# Revit family: REVIT-QW
name_source: partatom
category: Mechanical Equipment
revit_build: Autodesk Revit 2017 (Build: 20190507_1515(x64)
units: mm (PartAtom-declared; Revit-internal decimal feet)

## family parameters
Always vertical = Yes
Cut with Voids When Loaded = No
Part Type = Normal
Room Calculation Point = No
Round Connector Dimension = Use Radius
Shared = No
Work Plane-Based = No

## types (263) — shared parameters
Assembly Code = D3040400
Current = 2 A
Description = PVI QuickDraw - Water Heater
Disclaimer = This rendering is for building modeling purposes only. Submittal/catalog is still the contract document. PVI reserves the right to change design and specification without notice.
Drain Angle = 90.00°
Drain Supplemental Extension = 1"
Drain Supplemental Radius = 1/2"
Energy Radius = 14 9/16"
Frequency = 60 Hz
Location (default) = Please Enter Installation Location
Manufacturer = PVI Industries, LLC
Phase = 1
Rear Access Extension = 0"
Relief Valve NPT = 1"
Relief Valve Radius = 1/2"
URL = www.pvi.com
Voltage = 120 V

## per-type parameters (varying)
- 8200 L 1000A-QW: BW Inlet Conn X=4 9/16"; BW Inlet NPT=4"; BW Inlet Radius=2"; BW Inlet Y=18 11/16"; BW Outlet Conn X=4 9/16"; BW Outlet NPT=4"; BW Outlet Radius=2"; BW Outlet Y=33 11/16"; BW Plumbing Total Z=20 15/16"; BW Up=17 9/16"; BW Up Radius=2"; BW X=24 1/16"; BW Z=7 1/2"; Boiler Water Flow Rate at 180F=322 GPM; Cold Water Extension=9"; Cold Water Inlet Z=5"; Cold Water NPT=2 1/2"; Cold Water Radius=1 1/4"; Control Enclosure Location=20"; Control Panel Extension=44 1/2"; Drain Extension=41 3/8"; Drain NPT=1 1/2"; Drain Radius=3/4"; Energy Extension=42 1/2"; Flat Side Distance=75"; Front Skid Extension=112 1/2"; Height to Drain=3"; Height to Energy=31 5/8"; Height to Hot Outlet=60 3/4"; Height to Relief=60 3/8"; Hot Outlet Angle=90.00°; Hot Outlet Extension=38 1/2"; Hot Outlet NPT=3"; Hot Outlet Offset Horiz=38 1/2"; Hot Outlet Offset Vert=0"; Hot Outlet Radius=1 1/2"; Rear Skid Extension=37 1/2"; Recovery Rate 40F to 140F (GPH)=3800; Relief Valve Extension=40 1/2"; Skid Length=75"; Skid Spacing=43"; U Tube Extension=13 7/16"; U Tube Radius=8"; Unit Height=80 7/16"; Unit Radius=37 1/2"; Weight=3890
- 6900 L 1000A-QWD: BW Inlet Conn X=4 9/16"; BW Inlet NPT=4"; BW Inlet Radius=2"; BW Inlet Y=18 11/16"; BW Outlet Conn X=4 9/16"; BW Outlet NPT=4"; BW Outlet Radius=2"; BW Outlet Y=33 11/16"; BW Plumbing Total Z=20 15/16"; BW Up=17 9/16"; BW Up Radius=2"; BW X=24 1/16"; BW Z=7 1/2"; Boiler Water Flow Rate at 180F=286 GPM; Cold Water Extension=9"; Cold Water Inlet Z=5"; Cold Water NPT=2 1/2"; Cold Water Radius=1 1/4"; Control Enclosure Location=20"; Control Panel Extension=44 1/2"; Drain Extension=41 3/8"; Drain NPT=1 1/2"; Drain Radius=3/4"; Energy Extension=42 1/2"; Flat Side Distance=75"; Front Skid Extension=112 1/2"; Height to Drain=3"; Height to Energy=31 5/8"; Height to Hot Outlet=60 3/4"; Height to Relief=60 3/8"; Hot Outlet Angle=90.00°; Hot Outlet Extension=38 1/2"; Hot Outlet NPT=3"; Hot Outlet Offset Horiz=38 1/2"; Hot Outlet Offset Vert=0"; Hot Outlet Radius=1 1/2"; Rear Skid Extension=37 1/2"; Recovery Rate 40F to 140F (GPH)=3370; Relief Valve Extension=40 1/2"; Skid Length=75"; Skid Spacing=43"; U Tube Extension=13 7/16"; U Tube Radius=8"; Unit Height=80 7/16"; Unit Radius=37 1/2"; Weight=4190
- 6300 L 1000A-QW: BW Inlet Conn X=4"; BW Inlet NPT=4"; BW Inlet Radius=2"; BW Inlet Y=18 11/16"; BW Outlet Conn X=4"; BW Outlet NPT=4"; BW Outlet Radius=2"; BW Outlet Y=33 11/16"; BW Plumbing Total Z=21 3/16"; BW Up=17"; BW Up Radius=2"; BW X=23 1/2"; BW Z=7 1/2"; Boiler Water Flow Rate at 180F=251 GPM; Cold Water Extension=8"; Cold Water Inlet Z=4 1/2"; Cold Water NPT=2 1/2"; Cold Water Radius=1 1/4"; Control Enclosure Location=20"; Control Panel Extension=44 1/2"; Drain Extension=41 3/8"; Drain NPT=1 1/2"; Drain Radius=3/4"; Energy Extension=42 1/2"; Flat Side Distance=75"; Front Skid Extension=112 1/2"; Height to Drain=3"; Height to Energy=31 5/8"; Height to Hot Outlet=60 3/4"; Height to Relief=60 3/8"; Hot Outlet Angle=90.00°; Hot Outlet Extension=38 1/2"; Hot Outlet NPT=3"; Hot Outlet Offset Horiz=38 1/2"; Hot Outlet Offset Vert=0"; Hot Outlet Radius=1 1/2"; Rear Skid Extension=37 1/2"; Recovery Rate 40F to 140F (GPH)=2960; Relief Valve Extension=40 1/2"; Skid Length=75"; Skid Spacing=43"; U Tube Extension=13 11/16"; U Tube Radius=7"; Unit Height=80 7/16"; Unit Radius=37 1/2"; Weight=3730
- 6100 L 1000A-QWD: BW Inlet Conn X=4 9/16"; BW Inlet NPT=4"; BW Inlet Radius=2"; BW Inlet Y=18 11/16"; BW Outlet Conn X=4 9/16"; BW Outlet NPT=4"; BW Outlet Radius=2"; BW Outlet Y=33 11/16"; BW Plumbing Total Z=20 15/16"; BW Up=17 9/16"; BW Up Radius=2"; BW X=24 1/16"; BW Z=7 1/2"; Boiler Water Flow Rate at 180F=249 GPM; Cold Water Extension=9"; Cold Water Inlet Z=5"; Cold Water NPT=2 1/2"; Cold Water Radius=1 1/4"; Control Enclosure Location=20"; Control Panel Extension=44 1/2"; Drain Extension=41 3/8"; Drain NPT=1 1/2"; Drain Radius=3/4"; Energy Extension=42 1/2"; Flat Side Distance=75"; Front Skid Extension=112 1/2"; Height to Drain=3"; Height to Energy=31 5/8"; Height to Hot Outlet=60 3/4"; Height to Relief=60 3/8"; Hot Outlet Angle=90.00°; Hot Outlet Extension=38 1/2"; Hot Outlet NPT=3"; Hot Outlet Offset Horiz=38 1/2"; Hot Outlet Offset Vert=0"; Hot Outlet Radius=1 1/2"; Rear Skid Extension=37 1/2"; Recovery Rate 40F to 140F (GPH)=2930; Relief Valve Extension=40 1/2"; Skid Length=75"; Skid Spacing=43"; U Tube Extension=13 7/16"; U Tube Radius=8"; Unit Height=80 7/16"; Unit Radius=37 1/2"; Weight=4120
- 5400 L 1000A-QWD: BW Inlet Conn X=4"; BW Inlet NPT=4"; BW Inlet Radius=2"; BW Inlet Y=18 11/16"; BW Outlet Conn X=4"; BW Outlet NPT=4"; BW Outlet Radius=2"; BW Outlet Y=33 11/16"; BW Plumbing Total Z=21 3/16"; BW Up=17"; BW Up Radius=2"; BW X=23 1/2"; BW Z=7 1/2"; Boiler Water Flow Rate at 180F=222 GPM; Cold Water Extension=8"; Cold Water Inlet Z=4 1/2"; Cold Water NPT=2 1/2"; Cold Water Radius=1 1/4"; Control Enclosure Location=20"; Control Panel Extension=44 1/2"; Drain Extension=41 3/8"; Drain NPT=1 1/2"; Drain Radius=3/4"; Energy Extension=42 1/2"; Flat Side Distance=75"; Front Skid Extension=112 1/2"; Height to Drain=3"; Height to Energy=31 5/8"; Height to Hot Outlet=60 3/4"; Height to Relief=60 3/8"; Hot Outlet Angle=90.00°; Hot Outlet Extension=38 1/2"; Hot Outlet NPT=3"; Hot Outlet Offset Horiz=38 1/2"; Hot Outlet Offset Vert=0"; Hot Outlet Radius=1 1/2"; Rear Skid Extension=37 1/2"; Recovery Rate 40F to 140F (GPH)=2620; Relief Valve Extension=40 1/2"; Skid Length=75"; Skid Spacing=43"; U Tube Extension=13 11/16"; U Tube Radius=7"; Unit Height=80 7/16"; Unit Radius=37 1/2"; Weight=3960
- 4500 L 1000A-QW: BW Inlet Conn X=3 13/16"; BW Inlet NPT=3"; BW Inlet Radius=1 1/2"; BW Inlet Y=18 11/16"; BW Outlet Conn X=3 13/16"; BW Outlet NPT=3"; BW Outlet Radius=1 1/2"; BW Outlet Y=33 11/16"; BW Plumbing Total Z=18 9/16"; BW Up=16 13/16"; BW Up Radius=1 1/2"; BW X=23 5/16"; BW Z=7 1/2"; Boiler Water Flow Rate at 180F=203 GPM; Cold Water Extension=7 3/8"; Cold Water Inlet Z=5"; Cold Water NPT=2 1/2"; Cold Water Radius=1 1/4"; Control Enclosure Location=20"; Control Panel Extension=44 1/2"; Drain Extension=41 3/8"; Drain NPT=1 1/2"; Drain Radius=3/4"; Energy Extension=42 1/2"; Flat Side Distance=75"; Front Skid Extension=112 1/2"; Height to Drain=3"; Height to Energy=31 5/8"; Height to Hot Outlet=60 3/4"; Height to Relief=60 3/8"; Hot Outlet Angle=90.00°; Hot Outlet Extension=38 1/2"; Hot Outlet NPT=3"; Hot Outlet Offset Horiz=38 1/2"; Hot Outlet Offset Vert=0"; Hot Outlet Radius=1 1/2"; Rear Skid Extension=37 1/2"; Recovery Rate 40F to 140F (GPH)=2390; Relief Valve Extension=40 1/2"; Skid Length=75"; Skid Spacing=43"; U Tube Extension=11 1/16"; U Tube Radius=6 3/8"; Unit Height=80 7/16"; Unit Radius=37 1/2"; Weight=3640
- 4300 L 1000A-QW: BW Inlet Conn X=3 13/16"; BW Inlet NPT=3"; BW Inlet Radius=1 1/2"; BW Inlet Y=18 11/16"; BW Outlet Conn X=3 13/16"; BW Outlet NPT=3"; BW Outlet Radius=1 1/2"; BW Outlet Y=33 11/16"; BW Plumbing Total Z=18 9/16"; BW Up=16 13/16"; BW Up Radius=1 1/2"; BW X=23 5/16"; BW Z=7 1/2"; Boiler Water Flow Rate at 180F=179 GPM; Cold Water Extension=7 3/8"; Cold Water Inlet Z=5"; Cold Water NPT=2 1/2"; Cold Water Radius=1 1/4"; Control Enclosure Location=20"; Control Panel Extension=44 1/2"; Drain Extension=41 3/8"; Drain NPT=1 1/2"; Drain Radius=3/4"; Energy Extension=42 1/2"; Flat Side Distance=75"; Front Skid Extension=112 1/2"; Height to Drain=3"; Height to Energy=31 5/8"; Height to Hot Outlet=60 3/4"; Height to Relief=60 3/8"; Hot Outlet Angle=90.00°; Hot Outlet Extension=38 1/2"; Hot Outlet NPT=3"; Hot Outlet Offset Horiz=38 1/2"; Hot Outlet Offset Vert=0"; Hot Outlet Radius=1 1/2"; Rear Skid Extension=37 1/2"; Recovery Rate 40F to 140F (GPH)=2110; Relief Valve Extension=40 1/2"; Skid Length=75"; Skid Spacing=43"; U Tube Extension=11 1/16"; U Tube Radius=6 3/8"; Unit Height=80 7/16"; Unit Radius=37 1/2"; Weight=3610
- 4200 L 1000A-QWD: BW Inlet Conn X=3 13/16"; BW Inlet NPT=3"; BW Inlet Radius=1 1/2"; BW Inlet Y=18 11/16"; BW Outlet Conn X=3 13/16"; BW Outlet NPT=3"; BW Outlet Radius=1 1/2"; BW Outlet Y=33 11/16"; BW Plumbing Total Z=18 9/16"; BW Up=16 13/16"; BW Up Radius=1 1/2"; BW X=23 5/16"; BW Z=7 1/2"; Boiler Water Flow Rate at 180F=179 GPM; Cold Water Extension=7 3/8"; Cold Water Inlet Z=5"; Cold Water NPT=2 1/2"; Cold Water Radius=1 1/4"; Control Enclosure Location=20"; Control Panel Extension=44 1/2"; Drain Extension=41 3/8"; Drain NPT=1 1/2"; Drain Radius=3/4"; Energy Extension=42 1/2"; Flat Side Distance=75"; Front Skid Extension=112 1/2"; Height to Drain=3"; Height to Energy=31 5/8"; Height to Hot Outlet=60 3/4"; Height to Relief=60 3/8"; Hot Outlet Angle=90.00°; Hot Outlet Extension=38 1/2"; Hot Outlet NPT=3"; Hot Outlet Offset Horiz=38 1/2"; Hot Outlet Offset Vert=0"; Hot Outlet Radius=1 1/2"; Rear Skid Extension=37 1/2"; Recovery Rate 40F to 140F (GPH)=2100; Relief Valve Extension=40 1/2"; Skid Length=75"; Skid Spacing=43"; U Tube Extension=11 1/16"; U Tube Radius=6 3/8"; Unit Height=80 7/16"; Unit Radius=37 1/2"; Weight=3840
- 4000 L 1000A-QW: BW Inlet Conn X=3 13/16"; BW Inlet NPT=3"; BW Inlet Radius=1 1/2"; BW Inlet Y=18 11/16"; BW Outlet Conn X=3 13/16"; BW Outlet NPT=3"; BW Outlet Radius=1 1/2"; BW Outlet Y=33 11/16"; BW Plumbing Total Z=18 9/16"; BW Up=16 13/16"; BW Up Radius=1 1/2"; BW X=23 5/16"; BW Z=7 1/2"; Boiler Water Flow Rate at 180F=152 GPM; Cold Water Extension=7 3/8"; Cold Water Inlet Z=5"; Cold Water NPT=2 1/2"; Cold Water Radius=1 1/4"; Control Enclosure Location=20"; Control Panel Extension=44 1/2"; Drain Extension=41 3/8"; Drain NPT=1 1/2"; Drain Radius=3/4"; Energy Extension=42 1/2"; Flat Side Distance=75"; Front Skid Extension=112 1/2"; Height to Drain=3"; Height to Energy=31 5/8"; Height to Hot Outlet=60 3/4"; Height to Relief=60 3/8"; Hot Outlet Angle=90.00°; Hot Outlet Extension=38 1/2"; Hot Outlet NPT=3"; Hot Outlet Offset Horiz=38 1/2"; Hot Outlet Offset Vert=0"; Hot Outlet Radius=1 1/2"; Rear Skid Extension=37 1/2"; Recovery Rate 40F to 140F (GPH)=1790; Relief Valve Extension=40 1/2"; Skid Length=75"; Skid Spacing=43"; U Tube Extension=11 1/16"; U Tube Radius=6 3/8"; Unit Height=80 7/16"; Unit Radius=37 1/2"; Weight=3590
- 3500 L 1000A-QW: BW Inlet Conn X=2 15/16"; BW Inlet NPT=2 1/2"; BW Inlet Radius=1 1/4"; BW Inlet Y=18 11/16"; BW Outlet Conn X=2 15/16"; BW Outlet NPT=2 1/2"; BW Outlet Radius=1 1/4"; BW Outlet Y=33 11/16"; BW Plumbing Total Z=18 1/16"; BW Up=15 15/16"; BW Up Radius=1 1/4"; BW X=22 7/16"; BW Z=7 1/2"; Boiler Water Flow Rate at 180F=138 GPM; Cold Water Extension=6 3/8"; Cold Water Inlet Z=5 1/8"; Cold Water NPT=2 1/2"; Cold Water Radius=1 1/4"; Control Enclosure Location=20"; Control Panel Extension=44 1/2"; Drain Extension=41 3/8"; Drain NPT=1 1/2"; Drain Radius=3/4"; Energy Extension=42 1/2"; Flat Side Distance=75"; Front Skid Extension=112 1/2"; Height to Drain=3"; Height to Energy=31 5/8"; Height to Hot Outlet=60 3/4"; Height to Relief=60 3/8"; Hot Outlet Angle=90.00°; Hot Outlet Extension=38 1/2"; Hot Outlet NPT=3"; Hot Outlet Offset Horiz=38 1/2"; Hot Outlet Offset Vert=0"; Hot Outlet Radius=1 1/2"; Rear Skid Extension=37 1/2"; Recovery Rate 40F to 140F (GPH)=1630; Relief Valve Extension=40 1/2"; Skid Length=75"; Skid Spacing=43"; U Tube Extension=10 9/16"; U Tube Radius=5 3/8"; Unit Height=80 7/16"; Unit Radius=37 1/2"; Weight=3510
- 3400 L 1000A-QWD: BW Inlet Conn X=3 11/16"; BW Inlet NPT=2 1/2"; BW Inlet Radius=1 1/4"; BW Inlet Y=18 11/16"; BW Outlet Conn X=3 11/16"; BW Outlet NPT=2 1/2"; BW Outlet Radius=1 1/4"; BW Outlet Y=33 11/16"; BW Plumbing Total Z=18 9/16"; BW Up=16 13/16"; BW Up Radius=1 1/4"; BW X=23 5/16"; BW Z=7 1/2"; Boiler Water Flow Rate at 180F=138 GPM; Cold Water Extension=7 3/8"; Cold Water Inlet Z=5"; Cold Water NPT=2 1/2"; Cold Water Radius=1 1/4"; Control Enclosure Location=20"; Control Panel Extension=44 1/2"; Drain Extension=41 3/8"; Drain NPT=1 1/2"; Drain Radius=3/4"; Energy Extension=42 1/2"; Flat Side Distance=75"; Front Skid Extension=112 1/2"; Height to Drain=3"; Height to Energy=31 5/8"; Height to Hot Outlet=60 3/4"; Height to Relief=60 3/8"; Hot Outlet Angle=90.00°; Hot Outlet Extension=38 1/2"; Hot Outlet NPT=3"; Hot Outlet Offset Horiz=38 1/2"; Hot Outlet Offset Vert=0"; Hot Outlet Radius=1 1/2"; Rear Skid Extension=37 1/2"; Recovery Rate 40F to 140F (GPH)=1620; Relief Valve Extension=40 1/2"; Skid Length=75"; Skid Spacing=43"; U Tube Extension=11 1/16"; U Tube Radius=6 3/8"; Unit Height=80 7/16"; Unit Radius=37 1/2"; Weight=3760
- 3000 L 1000A-QW: BW Inlet Conn X=2 15/16"; BW Inlet NPT=2 1/2"; BW Inlet Radius=1 1/4"; BW Inlet Y=18 11/16"; BW Outlet Conn X=2 15/16"; BW Outlet NPT=2 1/2"; BW Outlet Radius=1 1/4"; BW Outlet Y=33 11/16"; BW Plumbing Total Z=18 1/16"; BW Up=15 15/16"; BW Up Radius=1 1/4"; BW X=22 7/16"; BW Z=7 1/2"; Boiler Water Flow Rate at 180F=120 GPM; Cold Water Extension=6 3/8"; Cold Water Inlet Z=5 1/8"; Cold Water NPT=2 1/2"; Cold Water Radius=1 1/4"; Control Enclosure Location=20"; Control Panel Extension=44 1/2"; Drain Extension=41 3/8"; Drain NPT=1 1/2"; Drain Radius=3/4"; Energy Extension=42 1/2"; Flat Side Distance=75"; Front Skid Extension=112 1/2"; Height to Drain=3"; Height to Energy=31 5/8"; Height to Hot Outlet=60 3/4"; Height to Relief=60 3/8"; Hot Outlet Angle=90.00°; Hot Outlet Extension=38 1/2"; Hot Outlet NPT=3"; Hot Outlet Offset Horiz=38 1/2"; Hot Outlet Offset Vert=0"; Hot Outlet Radius=1 1/2"; Rear Skid Extension=37 1/2"; Recovery Rate 40F to 140F (GPH)=1420; Relief Valve Extension=40 1/2"; Skid Length=75"; Skid Spacing=43"; U Tube Extension=10 9/16"; U Tube Radius=5 3/8"; Unit Height=80 7/16"; Unit Radius=37 1/2"; Weight=3500
- 2800 L 1000A-QWD: BW Inlet Conn X=3 11/16"; BW Inlet NPT=2 1/2"; BW Inlet Radius=1 1/4"; BW Inlet Y=12 3/8"; BW Outlet Conn X=3 11/16"; BW Outlet NPT=2 1/2"; BW Outlet Radius=1 1/4"; BW Outlet Y=23 7/16"; BW Plumbing Total Z=22 1/16"; BW Up=13 1/16"; BW Up Radius=1 1/4"; BW X=17 13/16"; BW Z=11 1/2"; Boiler Water Flow Rate at 180F=122 GPM; Cold Water Extension=7 3/8"; Cold Water Inlet Z=5 1/8"; Cold Water NPT=2 1/2"; Cold Water Radius=1 1/4"; Control Enclosure Location=20"; Control Panel Extension=44 1/2"; Drain Extension=41 3/8"; Drain NPT=1 1/2"; Drain Radius=3/4"; Energy Extension=42 1/2"; Flat Side Distance=75"; Front Skid Extension=112 1/2"; Height to Drain=3"; Height to Energy=31 5/8"; Height to Hot Outlet=60 3/4"; Height to Relief=60 3/8"; Hot Outlet Angle=90.00°; Hot Outlet Extension=38 1/2"; Hot Outlet NPT=3"; Hot Outlet Offset Horiz=38 1/2"; Hot Outlet Offset Vert=0"; Hot Outlet Radius=1 1/2"; Rear Skid Extension=37 1/2"; Recovery Rate 40F to 140F (GPH)=1430; Relief Valve Extension=40 1/2"; Skid Length=75"; Skid Spacing=43"; U Tube Extension=10 9/16"; U Tube Radius=6 3/8"; Unit Height=80 7/16"; Unit Radius=37 1/2"; Weight=3570
- 2600 L 1000A-QW: BW Inlet Conn X=2 15/16"; BW Inlet NPT=2 1/2"; BW Inlet Radius=1 1/4"; BW Inlet Y=12 3/8"; BW Outlet Conn X=2 15/16"; BW Outlet NPT=2 1/2"; BW Outlet Radius=1 1/4"; BW Outlet Y=23 7/16"; BW Plumbing Total Z=22 1/16"; BW Up=13 1/16"; BW Up Radius=1 1/4"; BW X=17 13/16"; BW Z=11 1/2"; Boiler Water Flow Rate at 180F=102 GPM; Cold Water Extension=6 3/8"; Cold Water Inlet Z=5 1/8"; Cold Water NPT=2 1/2"; Cold Water Radius=1 1/4"; Control Enclosure Location=20"; Control Panel Extension=44 1/2"; Drain Extension=41 3/8"; Drain NPT=1 1/2"; Drain Radius=3/4"; Energy Extension=42 1/2"; Flat Side Distance=75"; Front Skid Extension=112 1/2"; Height to Drain=3"; Height to Energy=31 5/8"; Height to Hot Outlet=60 3/4"; Height to Relief=60 3/8"; Hot Outlet Angle=90.00°; Hot Outlet Extension=38 1/2"; Hot Outlet NPT=3"; Hot Outlet Offset Horiz=38 1/2"; Hot Outlet Offset Vert=0"; Hot Outlet Radius=1 1/2"; Rear Skid Extension=37 1/2"; Recovery Rate 40F to 140F (GPH)=1200; Relief Valve Extension=40 1/2"; Skid Length=75"; Skid Spacing=43"; U Tube Extension=10 9/16"; U Tube Radius=5 3/8"; Unit Height=80 7/16"; Unit Radius=37 1/2"; Weight=3410
- 900 L 1000A-QWD: BW Inlet Conn X=2 1/2"; BW Inlet NPT=1 1/4"; BW Inlet Radius=5/8"; BW Inlet Y=6 3/4"; BW Outlet Conn X=2 1/2"; BW Outlet NPT=1 1/4"; BW Outlet Radius=5/8"; BW Outlet Y=14 1/16"; BW Plumbing Total Z=18 1/8"; BW Up=8 7/16"; BW Up Radius=5/8"; BW X=10 7/8"; BW Z=8 5/16"; Boiler Water Flow Rate at 180F=38 GPM; Cold Water Extension=5 5/16"; Cold Water Inlet Z=5 5/8"; Cold Water NPT=2"; Cold Water Radius=1"; Control Enclosure Location=20"; Control Panel Extension=44 1/2"; Drain Extension=41 3/8"; Drain NPT=1 1/2"; Drain Radius=3/4"; Energy Extension=42 1/2"; Flat Side Distance=75"; Front Skid Extension=112 1/2"; Height to Drain=3"; Height to Energy=31 5/8"; Height to Hot Outlet=60 3/4"; Height to Relief=60 3/8"; Hot Outlet Angle=90.00°; Hot Outlet Extension=38 1/2"; Hot Outlet NPT=3"; Hot Outlet Offset Horiz=38 1/2"; Hot Outlet Offset Vert=0"; Hot Outlet Radius=1 1/2"; Rear Skid Extension=37 1/2"; Recovery Rate 40F to 140F (GPH)=440; Relief Valve Extension=40 1/2"; Skid Length=75"; Skid Spacing=43"; U Tube Extension=9 13/16"; U Tube Radius=4 5/16"; Unit Height=80 7/16"; Unit Radius=37 1/2"; Weight=3260
- 800 L 1000A-QW: BW Inlet Conn X=1 7/8"; BW Inlet NPT=1 1/4"; BW Inlet Radius=5/8"; BW Inlet Y=6 3/4"; BW Outlet Conn X=1 7/8"; BW Outlet NPT=1 1/4"; BW Outlet Radius=5/8"; BW Outlet Y=14 1/16"; BW Plumbing Total Z=18 1/8"; BW Up=8 7/16"; BW Up Radius=5/8"; BW X=10 7/8"; BW Z=8 5/16"; Boiler Water Flow Rate at 180F=32 GPM; Cold Water Extension=4 5/16"; Cold Water Inlet Z=5 5/8"; Cold Water NPT=2"; Cold Water Radius=1"; Control Enclosure Location=20"; Control Panel Extension=44 1/2"; Drain Extension=41 3/8"; Drain NPT=1 1/2"; Drain Radius=3/4"; Energy Extension=42 1/2"; Flat Side Distance=75"; Front Skid Extension=112 1/2"; Height to Drain=3"; Height to Energy=31 5/8"; Height to Hot Outlet=60 3/4"; Height to Relief=60 3/8"; Hot Outlet Angle=90.00°; Hot Outlet Extension=38 1/2"; Hot Outlet NPT=3"; Hot Outlet Offset Horiz=38 1/2"; Hot Outlet Offset Vert=0"; Hot Outlet Radius=1 1/2"; Rear Skid Extension=37 1/2"; Recovery Rate 40F to 140F (GPH)=380; Relief Valve Extension=40 1/2"; Skid Length=75"; Skid Spacing=43"; U Tube Extension=9 13/16"; U Tube Radius=3 5/16"; Unit Height=80 7/16"; Unit Radius=37 1/2"; Weight=3200
- 700 L 1000A-QWD: BW Inlet Conn X=2 1/2"; BW Inlet NPT=1 1/4"; BW Inlet Radius=5/8"; BW Inlet Y=6 3/4"; BW Outlet Conn X=2 1/2"; BW Outlet NPT=1 1/4"; BW Outlet Radius=5/8"; BW Outlet Y=14 1/16"; BW Plumbing Total Z=18 1/8"; BW Up=8 7/16"; BW Up Radius=5/8"; BW X=10 7/8"; BW Z=8 5/16"; Boiler Water Flow Rate at 180F=29 GPM; Cold Water Extension=5 5/16"; Cold Water Inlet Z=5 5/8"; Cold Water NPT=2"; Cold Water Radius=1"; Control Enclosure Location=20"; Control Panel Extension=44 1/2"; Drain Extension=41 3/8"; Drain NPT=1 1/2"; Drain Radius=3/4"; Energy Extension=42 1/2"; Flat Side Distance=75"; Front Skid Extension=112 1/2"; Height to Drain=3"; Height to Energy=31 5/8"; Height to Hot Outlet=60 3/4"; Height to Relief=60 3/8"; Hot Outlet Angle=90.00°; Hot Outlet Extension=38 1/2"; Hot Outlet NPT=3"; Hot Outlet Offset Horiz=38 1/2"; Hot Outlet Offset Vert=0"; Hot Outlet Radius=1 1/2"; Rear Skid Extension=37 1/2"; Recovery Rate 40F to 140F (GPH)=340; Relief Valve Extension=40 1/2"; Skid Length=75"; Skid Spacing=43"; U Tube Extension=9 13/16"; U Tube Radius=4 5/16"; Unit Height=80 7/16"; Unit Radius=37 1/2"; Weight=3220
- 600 L 1000A-QW: BW Inlet Conn X=1 5/16"; BW Inlet NPT=1"; BW Inlet Radius=1/2"; BW Inlet Y=5 1/2"; BW Outlet Conn X=1 5/16"; BW Outlet NPT=1"; BW Outlet Radius=1/2"; BW Outlet Y=11 3/16"; BW Plumbing Total Z=15 1/2"; BW Up=5 13/16"; BW Up Radius=1/2"; BW X=7 15/16"; BW Z=6 1/16"; Boiler Water Flow Rate at 180F=23 GPM; Cold Water Extension=3 1/4"; Cold Water Inlet Z=5 5/8"; Cold Water NPT=2"; Cold Water Radius=1"; Control Enclosure Location=20"; Control Panel Extension=44 1/2"; Drain Extension=41 3/8"; Drain NPT=1 1/2"; Drain Radius=3/4"; Energy Extension=42 1/2"; Flat Side Distance=75"; Front Skid Extension=112 1/2"; Height to Drain=3"; Height to Energy=31 5/8"; Height to Hot Outlet=60 3/4"; Height to Relief=60 3/8"; Hot Outlet Angle=90.00°; Hot Outlet Extension=38 1/2"; Hot Outlet NPT=3"; Hot Outlet Offset Horiz=38 1/2"; Hot Outlet Offset Vert=0"; Hot Outlet Radius=1 1/2"; Rear Skid Extension=37 1/2"; Recovery Rate 40F to 140F (GPH)=270; Relief Valve Extension=40 1/2"; Skid Length=75"; Skid Spacing=43"; U Tube Extension=9 7/16"; U Tube Radius=2 1/4"; Unit Height=80 7/16"; Unit Radius=37 1/2"; Weight=3160
- 500 L 1000A-QWD: BW Inlet Conn X=1 5/16"; BW Inlet NPT=1"; BW Inlet Radius=1/2"; BW Inlet Y=5 1/2"; BW Outlet Conn X=1 5/16"; BW Outlet NPT=1"; BW Outlet Radius=1/2"; BW Outlet Y=11 3/16"; BW Plumbing Total Z=15 1/2"; BW Up=5 13/16"; BW Up Radius=1/2"; BW X=7 15/16"; BW Z=6 1/16"; Boiler Water Flow Rate at 180F=20 GPM; Cold Water Extension=3 1/4"; Cold Water Inlet Z=5 5/8"; Cold Water NPT=2"; Cold Water Radius=1"; Control Enclosure Location=20"; Control Panel Extension=44 1/2"; Drain Extension=41 3/8"; Drain NPT=1 1/2"; Drain Radius=3/4"; Energy Extension=42 1/2"; Flat Side Distance=75"; Front Skid Extension=112 1/2"; Height to Drain=3"; Height to Energy=31 5/8"; Height to Hot Outlet=60 3/4"; Height to Relief=60 3/8"; Hot Outlet Angle=90.00°; Hot Outlet Extension=38 1/2"; Hot Outlet NPT=3"; Hot Outlet Offset Horiz=38 1/2"; Hot Outlet Offset Vert=0"; Hot Outlet Radius=1 1/2"; Rear Skid Extension=37 1/2"; Recovery Rate 40F to 140F (GPH)=240; Relief Valve Extension=40 1/2"; Skid Length=75"; Skid Spacing=43"; U Tube Extension=9 7/16"; U Tube Radius=2 1/4"; Unit Height=80 7/16"; Unit Radius=37 1/2"; Weight=3180
- 300 L 1000A-QW: BW Inlet Conn X=1 5/16"; BW Inlet NPT=3/4"; BW Inlet Radius=3/8"; BW Inlet Y=5"; BW Outlet Conn X=1 5/16"; BW Outlet NPT=3/4"; BW Outlet Radius=3/8"; BW Outlet Y=9 1/16"; BW Plumbing Total Z=15 3/8"; BW Up=5 3/4"; BW Up Radius=3/8"; BW X=8 1/16"; BW Z=5 15/16"; Boiler Water Flow Rate at 180F=12 GPM; Cold Water Extension=3 1/4"; Cold Water Inlet Z=5 5/8"; Cold Water NPT=2"; Cold Water Radius=1"; Control Enclosure Location=20"; Control Panel Extension=44 1/2"; Drain Extension=41 3/8"; Drain NPT=1 1/2"; Drain Radius=3/4"; Energy Extension=42 1/2"; Flat Side Distance=75"; Front Skid Extension=112 1/2"; Height to Drain=3"; Height to Energy=31 5/8"; Height to Hot Outlet=60 3/4"; Height to Relief=60 3/8"; Hot Outlet Angle=90.00°; Hot Outlet Extension=38 1/2"; Hot Outlet NPT=3"; Hot Outlet Offset Horiz=38 1/2"; Hot Outlet Offset Vert=0"; Hot Outlet Radius=1 1/2"; Rear Skid Extension=37 1/2"; Recovery Rate 40F to 140F (GPH)=140; Relief Valve Extension=40 1/2"; Skid Length=75"; Skid Spacing=43"; U Tube Extension=9 7/16"; U Tube Radius=2 1/4"; Unit Height=80 7/16"; Unit Radius=37 1/2"; Weight=3160
- 250 L 1000A-QWD: BW Inlet Conn X=1 5/16"; BW Inlet NPT=3/4"; BW Inlet Radius=3/8"; BW Inlet Y=5"; BW Outlet Conn X=1 5/16"; BW Outlet NPT=3/4"; BW Outlet Radius=3/8"; BW Outlet Y=9 1/16"; BW Plumbing Total Z=15 3/8"; BW Up=5 3/4"; BW Up Radius=3/8"; BW X=8 1/16"; BW Z=5 15/16"; Boiler Water Flow Rate at 180F=11 GPM; Cold Water Extension=3 1/4"; Cold Water Inlet Z=5 5/8"; Cold Water NPT=2"; Cold Water Radius=1"; Control Enclosure Location=20"; Control Panel Extension=44 1/2"; Drain Extension=41 3/8"; Drain NPT=1 1/2"; Drain Radius=3/4"; Energy Extension=42 1/2"; Flat Side Distance=75"; Front Skid Extension=112 1/2"; Height to Drain=3"; Height to Energy=31 5/8"; Height to Hot Outlet=60 3/4"; Height to Relief=60 3/8"; Hot Outlet Angle=90.00°; Hot Outlet Extension=38 1/2"; Hot Outlet NPT=3"; Hot Outlet Offset Horiz=38 1/2"; Hot Outlet Offset Vert=0"; Hot Outlet Radius=1 1/2"; Rear Skid Extension=37 1/2"; Recovery Rate 40F to 140F (GPH)=130; Relief Valve Extension=40 1/2"; Skid Length=75"; Skid Spacing=43"; U Tube Extension=9 7/16"; U Tube Radius=2 1/4"; Unit Height=80 7/16"; Unit Radius=37 1/2"; Weight=3170
- 2300 L 1000A-QW: BW Inlet Conn X=2 15/16"; BW Inlet NPT=2"; BW Inlet Radius=1"; BW Inlet Y=12 3/8"; BW Outlet Conn X=2 15/16"; BW Outlet NPT=2"; BW Outlet Radius=1"; BW Outlet Y=23 7/16"; BW Plumbing Total Z=22 1/16"; BW Up=13 1/16"; BW Up Radius=1"; BW X=17 13/16"; BW Z=11 1/2"; Boiler Water Flow Rate at 180F=87 GPM; Cold Water Extension=6 3/8"; Cold Water Inlet Z=5 1/8"; Cold Water NPT=2 1/2"; Cold Water Radius=1 1/4"; Control Enclosure Location=20"; Control Panel Extension=44 1/2"; Drain Extension=41 3/8"; Drain NPT=1 1/2"; Drain Radius=3/4"; Energy Extension=42 1/2"; Flat Side Distance=75"; Front Skid Extension=112 1/2"; Height to Drain=3"; Height to Energy=31 5/8"; Height to Hot Outlet=60 3/4"; Height to Relief=60 3/8"; Hot Outlet Angle=90.00°; Hot Outlet Extension=38 1/2"; Hot Outlet NPT=3"; Hot Outlet Offset Horiz=38 1/2"; Hot Outlet Offset Vert=0"; Hot Outlet Radius=1 1/2"; Rear Skid Extension=37 1/2"; Recovery Rate 40F to 140F (GPH)=1020; Relief Valve Extension=40 1/2"; Skid Length=75"; Skid Spacing=43"; U Tube Extension=10 9/16"; U Tube Radius=5 3/8"; Unit Height=80 7/16"; Unit Radius=37 1/2"; Weight=3400
- 2200 L 1000A-QWD: BW Inlet Conn X=2 15/16"; BW Inlet NPT=2"; BW Inlet Radius=1"; BW Inlet Y=12 3/8"; BW Outlet Conn X=2 15/16"; BW Outlet NPT=2"; BW Outlet Radius=1"; BW Outlet Y=23 7/16"; BW Plumbing Total Z=22 1/16"; BW Up=13 1/16"; BW Up Radius=1"; BW X=17 13/16"; BW Z=11 1/2"; Boiler Water Flow Rate at 180F=92 GPM; Cold Water Extension=6 3/8"; Cold Water Inlet Z=5 1/8"; Cold Water NPT=2 1/2"; Cold Water Radius=1 1/4"; Control Enclosure Location=20"; Control Panel Extension=44 1/2"; Drain Extension=41 3/8"; Drain NPT=1 1/2"; Drain Radius=3/4"; Energy Extension=42 1/2"; Flat Side Distance=75"; Front Skid Extension=112 1/2"; Height to Drain=3"; Height to Energy=31 5/8"; Height to Hot Outlet=60 3/4"; Height to Relief=60 3/8"; Hot Outlet Angle=90.00°; Hot Outlet Extension=38 1/2"; Hot Outlet NPT=3"; Hot Outlet Offset Horiz=38 1/2"; Hot Outlet Offset Vert=0"; Hot Outlet Radius=1 1/2"; Rear Skid Extension=37 1/2"; Recovery Rate 40F to 140F (GPH)=1090; Relief Valve Extension=40 1/2"; Skid Length=75"; Skid Spacing=43"; U Tube Extension=10 9/16"; U Tube Radius=5 3/8"; Unit Height=80 7/16"; Unit Radius=37 1/2"; Weight=3520
- 2000 L 1000A-QW: BW Inlet Conn X=2 1/2"; BW Inlet NPT=2"; BW Inlet Radius=1"; BW Inlet Y=10 3/8"; BW Outlet Conn X=2 1/2"; BW Outlet NPT=2"; BW Outlet Radius=1"; BW Outlet Y=17 9/16"; BW Plumbing Total Z=20 1/8"; BW Up=10 3/8"; BW Up Radius=1"; BW X=12 13/16"; BW Z=9 5/16"; Boiler Water Flow Rate at 180F=80 GPM; Cold Water Extension=5 5/16"; Cold Water Inlet Z=5 3/8"; Cold Water NPT=2"; Cold Water Radius=1"; Control Enclosure Location=20"; Control Panel Extension=44 1/2"; Drain Extension=41 3/8"; Drain NPT=1 1/2"; Drain Radius=3/4"; Energy Extension=42 1/2"; Flat Side Distance=75"; Front Skid Extension=112 1/2"; Height to Drain=3"; Height to Energy=31 5/8"; Height to Hot Outlet=60 3/4"; Height to Relief=60 3/8"; Hot Outlet Angle=90.00°; Hot Outlet Extension=38 1/2"; Hot Outlet NPT=3"; Hot Outlet Offset Horiz=38 1/2"; Hot Outlet Offset Vert=0"; Hot Outlet Radius=1 1/2"; Rear Skid Extension=37 1/2"; Recovery Rate 40F to 140F (GPH)=950; Relief Valve Extension=40 1/2"; Skid Length=75"; Skid Spacing=43"; U Tube Extension=10 13/16"; U Tube Radius=4 5/16"; Unit Height=80 7/16"; Unit Radius=37 1/2"; Weight=3320
- 1900 L 1000A-QWD: BW Inlet Conn X=2 15/16"; BW Inlet NPT=2"; BW Inlet Radius=1"; BW Inlet Y=10 3/8"; BW Outlet Conn X=2 15/16"; BW Outlet NPT=2"; BW Outlet Radius=1"; BW Outlet Y=17 9/16"; BW Plumbing Total Z=19 7/8"; BW Up=10 13/16"; BW Up Radius=1"; BW X=13 7/8"; BW Z=9 5/16"; Boiler Water Flow Rate at 180F=80 GPM; Cold Water Extension=6 3/8"; Cold Water Inlet Z=5 1/8"; Cold Water NPT=2 1/2"; Cold Water Radius=1 1/4"; Control Enclosure Location=20"; Control Panel Extension=44 1/2"; Drain Extension=41 3/8"; Drain NPT=1 1/2"; Drain Radius=3/4"; Energy Extension=42 1/2"; Flat Side Distance=75"; Front Skid Extension=112 1/2"; Height to Drain=3"; Height to Energy=31 5/8"; Height to Hot Outlet=60 3/4"; Height to Relief=60 3/8"; Hot Outlet Angle=90.00°; Hot Outlet Extension=38 1/2"; Hot Outlet NPT=3"; Hot Outlet Offset Horiz=38 1/2"; Hot Outlet Offset Vert=0"; Hot Outlet Radius=1 1/2"; Rear Skid Extension=37 1/2"; Recovery Rate 40F to 140F (GPH)=950; Relief Valve Extension=40 1/2"; Skid Length=75"; Skid Spacing=43"; U Tube Extension=10 9/16"; U Tube Radius=5 3/8"; Unit Height=80 7/16"; Unit Radius=37 1/2"; Weight=3490
- 1500 L 1000A-QW: BW Inlet Conn X=2 1/2"; BW Inlet NPT=1 1/2"; BW Inlet Radius=3/4"; BW Inlet Y=10 3/8"; BW Outlet Conn X=2 1/2"; BW Outlet NPT=1 1/2"; BW Outlet Radius=3/4"; BW Outlet Y=17 9/16"; BW Plumbing Total Z=20 1/8"; BW Up=10 3/8"; BW Up Radius=3/4"; BW X=12 13/16"; BW Z=9 5/16"; Boiler Water Flow Rate at 180F=58 GPM; Cold Water Extension=5 5/16"; Cold Water Inlet Z=5 3/8"; Cold Water NPT=2"; Cold Water Radius=1"; Control Enclosure Location=20"; Control Panel Extension=44 1/2"; Drain Extension=41 3/8"; Drain NPT=1 1/2"; Drain Radius=3/4"; Energy Extension=42 1/2"; Flat Side Distance=75"; Front Skid Extension=112 1/2"; Height to Drain=3"; Height to Energy=31 5/8"; Height to Hot Outlet=60 3/4"; Height to Relief=60 3/8"; Hot Outlet Angle=90.00°; Hot Outlet Extension=38 1/2"; Hot Outlet NPT=3"; Hot Outlet Offset Horiz=38 1/2"; Hot Outlet Offset Vert=0"; Hot Outlet Radius=1 1/2"; Rear Skid Extension=37 1/2"; Recovery Rate 40F to 140F (GPH)=690; Relief Valve Extension=40 1/2"; Skid Length=75"; Skid Spacing=43"; U Tube Extension=10 13/16"; U Tube Radius=4 5/16"; Unit Height=80 7/16"; Unit Radius=37 1/2"; Weight=3300
- 1300 L 1000A-QWD: BW Inlet Conn X=2 1/2"; BW Inlet NPT=1 1/2"; BW Inlet Radius=3/4"; BW Inlet Y=8 3/8"; BW Outlet Conn X=2 1/2"; BW Outlet NPT=1 1/2"; BW Outlet Radius=3/4"; BW Outlet Y=15 1/4"; BW Plumbing Total Z=19 1/4"; BW Up=8 5/8"; BW Up Radius=3/4"; BW X=11 11/16"; BW Z=8 7/16"; Boiler Water Flow Rate at 180F=53 GPM; Cold Water Extension=5 5/16"; Cold Water Inlet Z=5 3/8"; Cold Water NPT=2"; Cold Water Radius=1"; Control Enclosure Location=20"; Control Panel Extension=44 1/2"; Drain Extension=41 3/8"; Drain NPT=1 1/2"; Drain Radius=3/4"; Energy Extension=42 1/2"; Flat Side Distance=75"; Front Skid Extension=112 1/2"; Height to Drain=3"; Height to Energy=31 5/8"; Height to Hot Outlet=60 3/4"; Height to Relief=60 3/8"; Hot Outlet Angle=90.00°; Hot Outlet Extension=38 1/2"; Hot Outlet NPT=3"; Hot Outlet Offset Horiz=38 1/2"; Hot Outlet Offset Vert=0"; Hot Outlet Radius=1 1/2"; Rear Skid Extension=37 1/2"; Recovery Rate 40F to 140F (GPH)=620; Relief Valve Extension=40 1/2"; Skid Length=75"; Skid Spacing=43"; U Tube Extension=10 13/16"; U Tube Radius=4 5/16"; Unit Height=80 7/16"; Unit Radius=37 1/2"; Weight=3340
- 1100 L 1000A-QW: BW Inlet Conn X=1 7/8"; BW Inlet NPT=1 1/4"; BW Inlet Radius=5/8"; BW Inlet Y=8 3/8"; BW Outlet Conn X=1 7/8"; BW Outlet NPT=1 1/4"; BW Outlet Radius=5/8"; BW Outlet Y=15 1/4"; BW Plumbing Total Z=18 1/4"; BW Up=8"; BW Up Radius=5/8"; BW X=11 1/16"; BW Z=8 7/16"; Boiler Water Flow Rate at 180F=43 GPM; Cold Water Extension=4 5/16"; Cold Water Inlet Z=5 5/8"; Cold Water NPT=2"; Cold Water Radius=1"; Control Enclosure Location=20"; Control Panel Extension=44 1/2"; Drain Extension=41 3/8"; Drain NPT=1 1/2"; Drain Radius=3/4"; Energy Extension=42 1/2"; Flat Side Distance=75"; Front Skid Extension=112 1/2"; Height to Drain=3"; Height to Energy=31 5/8"; Height to Hot Outlet=60 3/4"; Height to Relief=60 3/8"; Hot Outlet Angle=90.00°; Hot Outlet Extension=38 1/2"; Hot Outlet NPT=3"; Hot Outlet Offset Horiz=38 1/2"; Hot Outlet Offset Vert=0"; Hot Outlet Radius=1 1/2"; Rear Skid Extension=37 1/2"; Recovery Rate 40F to 140F (GPH)=510; Relief Valve Extension=40 1/2"; Skid Length=75"; Skid Spacing=43"; U Tube Extension=9 13/16"; U Tube Radius=3 5/16"; Unit Height=80 7/16"; Unit Radius=37 1/2"; Weight=3220
- 900 L 900A-QWD: BW Inlet Conn X=2 1/2"; BW Inlet NPT=1 1/4"; BW Inlet Radius=5/8"; BW Inlet Y=6 3/4"; BW Outlet Conn X=2 1/2"; BW Outlet NPT=1 1/4"; BW Outlet Radius=5/8"; BW Outlet Y=14 1/16"; BW Plumbing Total Z=18 1/8"; BW Up=8 7/16"; BW Up Radius=5/8"; BW X=10 7/8"; BW Z=8 5/16"; Boiler Water Flow Rate at 180F=38 GPM; Cold Water Extension=5 5/16"; Cold Water Inlet Z=5 5/8"; Cold Water NPT=2"; Cold Water Radius=1"; Control Enclosure Location=20"; Control Panel Extension=40 3/16"; Drain Extension=37 1/16"; Drain NPT=1 1/2"; Drain Radius=3/4"; Energy Extension=49 3/16"; Flat Side Distance=66 3/8"; Front Skid Extension=101 3/16"; Height to Drain=3 7/8"; Height to Energy=32 11/16"; Height to Hot Outlet=72 13/16"; Height to Relief=73 7/16"; Hot Outlet Angle=90.00°; Hot Outlet Extension=34 3/16"; Hot Outlet NPT=3"; Hot Outlet Offset Horiz=34 3/16"; Hot Outlet Offset Vert=0"; Hot Outlet Radius=1 1/2"; Rear Skid Extension=33 3/16"; Recovery Rate 40F to 140F (GPH)=440; Relief Valve Extension=36 3/16"; Skid Length=68"; Skid Spacing=36"; U Tube Extension=9 13/16"; U Tube Radius=4 5/16"; Unit Height=93 1/8"; Unit Radius=33 3/16"; Weight=2360
- 900 L 750A-QWD: BW Inlet Conn X=2 1/2"; BW Inlet NPT=1 1/4"; BW Inlet Radius=5/8"; BW Inlet Y=6 3/4"; BW Outlet Conn X=2 1/2"; BW Outlet NPT=1 1/4"; BW Outlet Radius=5/8"; BW Outlet Y=14 1/16"; BW Plumbing Total Z=18 1/8"; BW Up=8 7/16"; BW Up Radius=5/8"; BW X=10 7/8"; BW Z=8 5/16"; Boiler Water Flow Rate at 180F=38 GPM; Cold Water Extension=5 5/16"; Cold Water Inlet Z=5 5/8"; Cold Water NPT=2"; Cold Water Radius=1"; Control Enclosure Location=20"; Control Panel Extension=40 3/16"; Drain Extension=37 1/16"; Drain NPT=1 1/2"; Drain Radius=3/4"; Energy Extension=49 3/16"; Flat Side Distance=66 3/8"; Front Skid Extension=101 3/16"; Height to Drain=3 7/8"; Height to Energy=32 11/16"; Height to Hot Outlet=60 13/16"; Height to Relief=61 7/16"; Hot Outlet Angle=90.00°; Hot Outlet Extension=34 3/16"; Hot Outlet NPT=3"; Hot Outlet Offset Horiz=34 3/16"; Hot Outlet Offset Vert=0"; Hot Outlet Radius=1 1/2"; Rear Skid Extension=33 3/16"; Recovery Rate 40F to 140F (GPH)=440; Relief Valve Extension=36 3/16"; Skid Length=68"; Skid Spacing=36"; U Tube Extension=9 13/16"; U Tube Radius=4 5/16"; Unit Height=81 1/8"; Unit Radius=33 3/16"; Weight=2140
- 8200 L 900A-QW: BW Inlet Conn X=4 9/16"; BW Inlet NPT=4"; BW Inlet Radius=2"; BW Inlet Y=18 11/16"; BW Outlet Conn X=4 9/16"; BW Outlet NPT=4"; BW Outlet Radius=2"; BW Outlet Y=33 11/16"; BW Plumbing Total Z=20 15/16"; BW Up=17 9/16"; BW Up Radius=2"; BW X=24 1/16"; BW Z=7 1/2"; Boiler Water Flow Rate at 180F=322 GPM; Cold Water Extension=9"; Cold Water Inlet Z=5"; Cold Water NPT=2 1/2"; Cold Water Radius=1 1/4"; Control Enclosure Location=20"; Control Panel Extension=40 3/16"; Drain Extension=37 1/16"; Drain NPT=1 1/2"; Drain Radius=3/4"; Energy Extension=49 3/16"; Flat Side Distance=66 3/8"; Front Skid Extension=101 3/16"; Height to Drain=3 7/8"; Height to Energy=32 11/16"; Height to Hot Outlet=72 13/16"; Height to Relief=73 7/16"; Hot Outlet Angle=90.00°; Hot Outlet Extension=34 3/16"; Hot Outlet NPT=3"; Hot Outlet Offset Horiz=34 3/16"; Hot Outlet Offset Vert=0"; Hot Outlet Radius=1 1/2"; Rear Skid Extension=33 3/16"; Recovery Rate 40F to 140F (GPH)=3800; Relief Valve Extension=36 3/16"; Skid Length=68"; Skid Spacing=36"; U Tube Extension=13 7/16"; U Tube Radius=8"; Unit Height=93 1/8"; Unit Radius=33 3/16"; Weight=3000
- 8200 L 750A-QW: BW Inlet Conn X=4 9/16"; BW Inlet NPT=4"; BW Inlet Radius=2"; BW Inlet Y=18 11/16"; BW Outlet Conn X=4 9/16"; BW Outlet NPT=4"; BW Outlet Radius=2"; BW Outlet Y=33 11/16"; BW Plumbing Total Z=20 15/16"; BW Up=17 9/16"; BW Up Radius=2"; BW X=24 1/16"; BW Z=7 1/2"; Boiler Water Flow Rate at 180F=322 GPM; Cold Water Extension=9"; Cold Water Inlet Z=5"; Cold Water NPT=2 1/2"; Cold Water Radius=1 1/4"; Control Enclosure Location=20"; Control Panel Extension=40 3/16"; Drain Extension=37 1/16"; Drain NPT=1 1/2"; Drain Radius=3/4"; Energy Extension=49 3/16"; Flat Side Distance=66 3/8"; Front Skid Extension=101 3/16"; Height to Drain=3 7/8"; Height to Energy=32 11/16"; Height to Hot Outlet=60 13/16"; Height to Relief=61 7/16"; Hot Outlet Angle=90.00°; Hot Outlet Extension=34 3/16"; Hot Outlet NPT=3"; Hot Outlet Offset Horiz=34 3/16"; Hot Outlet Offset Vert=0"; Hot Outlet Radius=1 1/2"; Rear Skid Extension=33 3/16"; Recovery Rate 40F to 140F (GPH)=3800; Relief Valve Extension=36 3/16"; Skid Length=68"; Skid Spacing=36"; U Tube Extension=13 7/16"; U Tube Radius=8"; Unit Height=81 1/8"; Unit Radius=33 3/16"; Weight=2770
- 800 L 900A-QW: BW Inlet Conn X=1 7/8"; BW Inlet NPT=1 1/4"; BW Inlet Radius=5/8"; BW Inlet Y=6 3/4"; BW Outlet Conn X=1 7/8"; BW Outlet NPT=1 1/4"; BW Outlet Radius=5/8"; BW Outlet Y=14 1/16"; BW Plumbing Total Z=18 1/8"; BW Up=8 7/16"; BW Up Radius=5/8"; BW X=10 7/8"; BW Z=8 5/16"; Boiler Water Flow Rate at 180F=32 GPM; Cold Water Extension=4 5/16"; Cold Water Inlet Z=5 5/8"; Cold Water NPT=2"; Cold Water Radius=1"; Control Enclosure Location=20"; Control Panel Extension=40 3/16"; Drain Extension=37 1/16"; Drain NPT=1 1/2"; Drain Radius=3/4"; Energy Extension=49 3/16"; Flat Side Distance=66 3/8"; Front Skid Extension=101 3/16"; Height to Drain=3 7/8"; Height to Energy=32 11/16"; Height to Hot Outlet=72 13/16"; Height to Relief=73 7/16"; Hot Outlet Angle=90.00°; Hot Outlet Extension=34 3/16"; Hot Outlet NPT=3"; Hot Outlet Offset Horiz=34 3/16"; Hot Outlet Offset Vert=0"; Hot Outlet Radius=1 1/2"; Rear Skid Extension=33 3/16"; Recovery Rate 40F to 140F (GPH)=380; Relief Valve Extension=36 3/16"; Skid Length=68"; Skid Spacing=36"; U Tube Extension=9 13/16"; U Tube Radius=3 5/16"; Unit Height=93 1/8"; Unit Radius=33 3/16"; Weight=2310
- 800 L 750A-QW: BW Inlet Conn X=1 7/8"; BW Inlet NPT=1 1/4"; BW Inlet Radius=5/8"; BW Inlet Y=6 3/4"; BW Outlet Conn X=1 7/8"; BW Outlet NPT=1 1/4"; BW Outlet Radius=5/8"; BW Outlet Y=14 1/16"; BW Plumbing Total Z=18 1/8"; BW Up=8 7/16"; BW Up Radius=5/8"; BW X=10 7/8"; BW Z=8 5/16"; Boiler Water Flow Rate at 180F=32 GPM; Cold Water Extension=4 5/16"; Cold Water Inlet Z=5 5/8"; Cold Water NPT=2"; Cold Water Radius=1"; Control Enclosure Location=20"; Control Panel Extension=40 3/16"; Drain Extension=37 1/16"; Drain NPT=1 1/2"; Drain Radius=3/4"; Energy Extension=49 3/16"; Flat Side Distance=66 3/8"; Front Skid Extension=101 3/16"; Height to Drain=3 7/8"; Height to Energy=32 11/16"; Height to Hot Outlet=60 13/16"; Height to Relief=61 7/16"; Hot Outlet Angle=90.00°; Hot Outlet Extension=34 3/16"; Hot Outlet NPT=3"; Hot Outlet Offset Horiz=34 3/16"; Hot Outlet Offset Vert=0"; Hot Outlet Radius=1 1/2"; Rear Skid Extension=33 3/16"; Recovery Rate 40F to 140F (GPH)=380; Relief Valve Extension=36 3/16"; Skid Length=68"; Skid Spacing=36"; U Tube Extension=9 13/16"; U Tube Radius=3 5/16"; Unit Height=81 1/8"; Unit Radius=33 3/16"; Weight=2080
- 700 L 900A-QWD: BW Inlet Conn X=2 1/2"; BW Inlet NPT=1 1/4"; BW Inlet Radius=5/8"; BW Inlet Y=6 3/4"; BW Outlet Conn X=2 1/2"; BW Outlet NPT=1 1/4"; BW Outlet Radius=5/8"; BW Outlet Y=14 1/16"; BW Plumbing Total Z=18 1/8"; BW Up=8 7/16"; BW Up Radius=5/8"; BW X=10 7/8"; BW Z=8 5/16"; Boiler Water Flow Rate at 180F=29 GPM; Cold Water Extension=5 5/16"; Cold Water Inlet Z=5 5/8"; Cold Water NPT=2"; Cold Water Radius=1"; Control Enclosure Location=20"; Control Panel Extension=40 3/16"; Drain Extension=37 1/16"; Drain NPT=1 1/2"; Drain Radius=3/4"; Energy Extension=49 3/16"; Flat Side Distance=66 3/8"; Front Skid Extension=101 3/16"; Height to Drain=3 7/8"; Height to Energy=32 11/16"; Height to Hot Outlet=72 13/16"; Height to Relief=73 7/16"; Hot Outlet Angle=90.00°; Hot Outlet Extension=34 3/16"; Hot Outlet NPT=3"; Hot Outlet Offset Horiz=34 3/16"; Hot Outlet Offset Vert=0"; Hot Outlet Radius=1 1/2"; Rear Skid Extension=33 3/16"; Recovery Rate 40F to 140F (GPH)=340; Relief Valve Extension=36 3/16"; Skid Length=68"; Skid Spacing=36"; U Tube Extension=9 13/16"; U Tube Radius=4 5/16"; Unit Height=93 1/8"; Unit Radius=33 3/16"; Weight=2330
- 700 L 750A-QWD: BW Inlet Conn X=2 1/2"; BW Inlet NPT=1 1/4"; BW Inlet Radius=5/8"; BW Inlet Y=6 3/4"; BW Outlet Conn X=2 1/2"; BW Outlet NPT=1 1/4"; BW Outlet Radius=5/8"; BW Outlet Y=14 1/16"; BW Plumbing Total Z=18 1/8"; BW Up=8 7/16"; BW Up Radius=5/8"; BW X=10 7/8"; BW Z=8 5/16"; Boiler Water Flow Rate at 180F=29 GPM; Cold Water Extension=5 5/16"; Cold Water Inlet Z=5 5/8"; Cold Water NPT=2"; Cold Water Radius=1"; Control Enclosure Location=20"; Control Panel Extension=40 3/16"; Drain Extension=37 1/16"; Drain NPT=1 1/2"; Drain Radius=3/4"; Energy Extension=49 3/16"; Flat Side Distance=66 3/8"; Front Skid Extension=101 3/16"; Height to Drain=3 7/8"; Height to Energy=32 11/16"; Height to Hot Outlet=60 13/16"; Height to Relief=61 7/16"; Hot Outlet Angle=90.00°; Hot Outlet Extension=34 3/16"; Hot Outlet NPT=3"; Hot Outlet Offset Horiz=34 3/16"; Hot Outlet Offset Vert=0"; Hot Outlet Radius=1 1/2"; Rear Skid Extension=33 3/16"; Recovery Rate 40F to 140F (GPH)=340; Relief Valve Extension=36 3/16"; Skid Length=68"; Skid Spacing=36"; U Tube Extension=9 13/16"; U Tube Radius=4 5/16"; Unit Height=81 1/8"; Unit Radius=33 3/16"; Weight=2100
- 6900 L 900A-QWD: BW Inlet Conn X=4 9/16"; BW Inlet NPT=4"; BW Inlet Radius=2"; BW Inlet Y=18 11/16"; BW Outlet Conn X=4 9/16"; BW Outlet NPT=4"; BW Outlet Radius=2"; BW Outlet Y=33 11/16"; BW Plumbing Total Z=20 15/16"; BW Up=17 9/16"; BW Up Radius=2"; BW X=24 1/16"; BW Z=7 1/2"; Boiler Water Flow Rate at 180F=286 GPM; Cold Water Extension=9"; Cold Water Inlet Z=5"; Cold Water NPT=2 1/2"; Cold Water Radius=1 1/4"; Control Enclosure Location=20"; Control Panel Extension=40 3/16"; Drain Extension=37 1/16"; Drain NPT=1 1/2"; Drain Radius=3/4"; Energy Extension=49 3/16"; Flat Side Distance=66 3/8"; Front Skid Extension=101 3/16"; Height to Drain=3 7/8"; Height to Energy=32 11/16"; Height to Hot Outlet=72 13/16"; Height to Relief=73 7/16"; Hot Outlet Angle=90.00°; Hot Outlet Extension=34 3/16"; Hot Outlet NPT=3"; Hot Outlet Offset Horiz=34 3/16"; Hot Outlet Offset Vert=0"; Hot Outlet Radius=1 1/2"; Rear Skid Extension=33 3/16"; Recovery Rate 40F to 140F (GPH)=3370; Relief Valve Extension=36 3/16"; Skid Length=68"; Skid Spacing=36"; U Tube Extension=13 7/16"; U Tube Radius=8"; Unit Height=93 1/8"; Unit Radius=33 3/16"; Weight=3300
- 6900 L 750A-QWD: BW Inlet Conn X=4 9/16"; BW Inlet NPT=4"; BW Inlet Radius=2"; BW Inlet Y=18 11/16"; BW Outlet Conn X=4 9/16"; BW Outlet NPT=4"; BW Outlet Radius=2"; BW Outlet Y=33 11/16"; BW Plumbing Total Z=20 15/16"; BW Up=17 9/16"; BW Up Radius=2"; BW X=24 1/16"; BW Z=7 1/2"; Boiler Water Flow Rate at 180F=286 GPM; Cold Water Extension=9"; Cold Water Inlet Z=5"; Cold Water NPT=2 1/2"; Cold Water Radius=1 1/4"; Control Enclosure Location=20"; Control Panel Extension=40 3/16"; Drain Extension=37 1/16"; Drain NPT=1 1/2"; Drain Radius=3/4"; Energy Extension=49 3/16"; Flat Side Distance=66 3/8"; Front Skid Extension=101 3/16"; Height to Drain=3 7/8"; Height to Energy=32 11/16"; Height to Hot Outlet=60 13/16"; Height to Relief=61 7/16"; Hot Outlet Angle=90.00°; Hot Outlet Extension=34 3/16"; Hot Outlet NPT=3"; Hot Outlet Offset Horiz=34 3/16"; Hot Outlet Offset Vert=0"; Hot Outlet Radius=1 1/2"; Rear Skid Extension=33 3/16"; Recovery Rate 40F to 140F (GPH)=3370; Relief Valve Extension=36 3/16"; Skid Length=68"; Skid Spacing=36"; U Tube Extension=13 7/16"; U Tube Radius=8"; Unit Height=81 1/8"; Unit Radius=33 3/16"; Weight=3070
- 6300 L 900A-QW: BW Inlet Conn X=4"; BW Inlet NPT=4"; BW Inlet Radius=2"; BW Inlet Y=18 11/16"; BW Outlet Conn X=4"; BW Outlet NPT=4"; BW Outlet Radius=2"; BW Outlet Y=33 11/16"; BW Plumbing Total Z=21 3/16"; BW Up=17"; BW Up Radius=2"; BW X=23 1/2"; BW Z=7 1/2"; Boiler Water Flow Rate at 180F=251 GPM; Cold Water Extension=8"; Cold Water Inlet Z=4 1/2"; Cold Water NPT=2 1/2"; Cold Water Radius=1 1/4"; Control Enclosure Location=20"; Control Panel Extension=40 3/16"; Drain Extension=37 1/16"; Drain NPT=1 1/2"; Drain Radius=3/4"; Energy Extension=49 3/16"; Flat Side Distance=66 3/8"; Front Skid Extension=101 3/16"; Height to Drain=3 7/8"; Height to Energy=32 11/16"; Height to Hot Outlet=72 13/16"; Height to Relief=73 7/16"; Hot Outlet Angle=90.00°; Hot Outlet Extension=34 3/16"; Hot Outlet NPT=3"; Hot Outlet Offset Horiz=34 3/16"; Hot Outlet Offset Vert=0"; Hot Outlet Radius=1 1/2"; Rear Skid Extension=33 3/16"; Recovery Rate 40F to 140F (GPH)=2960; Relief Valve Extension=36 3/16"; Skid Length=68"; Skid Spacing=36"; U Tube Extension=13 11/16"; U Tube Radius=7"; Unit Height=93 1/8"; Unit Radius=33 3/16"; Weight=2830
- 6300 L 750A-QW: BW Inlet Conn X=4"; BW Inlet NPT=4"; BW Inlet Radius=2"; BW Inlet Y=18 11/16"; BW Outlet Conn X=4"; BW Outlet NPT=4"; BW Outlet Radius=2"; BW Outlet Y=33 11/16"; BW Plumbing Total Z=21 3/16"; BW Up=17"; BW Up Radius=2"; BW X=23 1/2"; BW Z=7 1/2"; Boiler Water Flow Rate at 180F=251 GPM; Cold Water Extension=8"; Cold Water Inlet Z=4 1/2"; Cold Water NPT=2 1/2"; Cold Water Radius=1 1/4"; Control Enclosure Location=20"; Control Panel Extension=40 3/16"; Drain Extension=37 1/16"; Drain NPT=1 1/2"; Drain Radius=3/4"; Energy Extension=49 3/16"; Flat Side Distance=66 3/8"; Front Skid Extension=101 3/16"; Height to Drain=3 7/8"; Height to Energy=32 11/16"; Height to Hot Outlet=60 13/16"; Height to Relief=61 7/16"; Hot Outlet Angle=90.00°; Hot Outlet Extension=34 3/16"; Hot Outlet NPT=3"; Hot Outlet Offset Horiz=34 3/16"; Hot Outlet Offset Vert=0"; Hot Outlet Radius=1 1/2"; Rear Skid Extension=33 3/16"; Recovery Rate 40F to 140F (GPH)=2960; Relief Valve Extension=36 3/16"; Skid Length=68"; Skid Spacing=36"; U Tube Extension=13 11/16"; U Tube Radius=7"; Unit Height=81 1/8"; Unit Radius=33 3/16"; Weight=2600
- 6100 L 900A-QWD: BW Inlet Conn X=4 9/16"; BW Inlet NPT=4"; BW Inlet Radius=2"; BW Inlet Y=18 11/16"; BW Outlet Conn X=4 9/16"; BW Outlet NPT=4"; BW Outlet Radius=2"; BW Outlet Y=33 11/16"; BW Plumbing Total Z=20 15/16"; BW Up=17 9/16"; BW Up Radius=2"; BW X=24 1/16"; BW Z=7 1/2"; Boiler Water Flow Rate at 180F=249 GPM; Cold Water Extension=9"; Cold Water Inlet Z=5"; Cold Water NPT=2 1/2"; Cold Water Radius=1 1/4"; Control Enclosure Location=20"; Control Panel Extension=40 3/16"; Drain Extension=37 1/16"; Drain NPT=1 1/2"; Drain Radius=3/4"; Energy Extension=49 3/16"; Flat Side Distance=66 3/8"; Front Skid Extension=101 3/16"; Height to Drain=3 7/8"; Height to Energy=32 11/16"; Height to Hot Outlet=72 13/16"; Height to Relief=73 7/16"; Hot Outlet Angle=90.00°; Hot Outlet Extension=34 3/16"; Hot Outlet NPT=3"; Hot Outlet Offset Horiz=34 3/16"; Hot Outlet Offset Vert=0"; Hot Outlet Radius=1 1/2"; Rear Skid Extension=33 3/16"; Recovery Rate 40F to 140F (GPH)=2930; Relief Valve Extension=36 3/16"; Skid Length=68"; Skid Spacing=36"; U Tube Extension=13 7/16"; U Tube Radius=8"; Unit Height=93 1/8"; Unit Radius=33 3/16"; Weight=3220
- 6100 L 750A-QWD: BW Inlet Conn X=4 9/16"; BW Inlet NPT=4"; BW Inlet Radius=2"; BW Inlet Y=18 11/16"; BW Outlet Conn X=4 9/16"; BW Outlet NPT=4"; BW Outlet Radius=2"; BW Outlet Y=33 11/16"; BW Plumbing Total Z=20 15/16"; BW Up=17 9/16"; BW Up Radius=2"; BW X=24 1/16"; BW Z=7 1/2"; Boiler Water Flow Rate at 180F=249 GPM; Cold Water Extension=9"; Cold Water Inlet Z=5"; Cold Water NPT=2 1/2"; Cold Water Radius=1 1/4"; Control Enclosure Location=20"; Control Panel Extension=40 3/16"; Drain Extension=37 1/16"; Drain NPT=1 1/2"; Drain Radius=3/4"; Energy Extension=49 3/16"; Flat Side Distance=66 3/8"; Front Skid Extension=101 3/16"; Height to Drain=3 7/8"; Height to Energy=32 11/16"; Height to Hot Outlet=60 13/16"; Height to Relief=61 7/16"; Hot Outlet Angle=90.00°; Hot Outlet Extension=34 3/16"; Hot Outlet NPT=3"; Hot Outlet Offset Horiz=34 3/16"; Hot Outlet Offset Vert=0"; Hot Outlet Radius=1 1/2"; Rear Skid Extension=33 3/16"; Recovery Rate 40F to 140F (GPH)=2930; Relief Valve Extension=36 3/16"; Skid Length=68"; Skid Spacing=36"; U Tube Extension=13 7/16"; U Tube Radius=8"; Unit Height=81 1/8"; Unit Radius=33 3/16"; Weight=2990
- 600 L 900A-QW: BW Inlet Conn X=1 5/16"; BW Inlet NPT=1"; BW Inlet Radius=1/2"; BW Inlet Y=5 1/2"; BW Outlet Conn X=1 5/16"; BW Outlet NPT=1"; BW Outlet Radius=1/2"; BW Outlet Y=11 3/16"; BW Plumbing Total Z=15 1/2"; BW Up=5 13/16"; BW Up Radius=1/2"; BW X=7 15/16"; BW Z=6 1/16"; Boiler Water Flow Rate at 180F=23 GPM; Cold Water Extension=3 1/4"; Cold Water Inlet Z=5 5/8"; Cold Water NPT=2"; Cold Water Radius=1"; Control Enclosure Location=20"; Control Panel Extension=40 3/16"; Drain Extension=37 1/16"; Drain NPT=1 1/2"; Drain Radius=3/4"; Energy Extension=49 3/16"; Flat Side Distance=66 3/8"; Front Skid Extension=101 3/16"; Height to Drain=3 7/8"; Height to Energy=32 11/16"; Height to Hot Outlet=72 13/16"; Height to Relief=73 7/16"; Hot Outlet Angle=90.00°; Hot Outlet Extension=34 3/16"; Hot Outlet NPT=3"; Hot Outlet Offset Horiz=34 3/16"; Hot Outlet Offset Vert=0"; Hot Outlet Radius=1 1/2"; Rear Skid Extension=33 3/16"; Recovery Rate 40F to 140F (GPH)=270; Relief Valve Extension=36 3/16"; Skid Length=68"; Skid Spacing=36"; U Tube Extension=9 7/16"; U Tube Radius=2 1/4"; Unit Height=93 1/8"; Unit Radius=33 3/16"; Weight=2270
- 600 L 750A-QW: BW Inlet Conn X=1 5/16"; BW Inlet NPT=1"; BW Inlet Radius=1/2"; BW Inlet Y=5 1/2"; BW Outlet Conn X=1 5/16"; BW Outlet NPT=1"; BW Outlet Radius=1/2"; BW Outlet Y=11 3/16"; BW Plumbing Total Z=15 1/2"; BW Up=5 13/16"; BW Up Radius=1/2"; BW X=7 15/16"; BW Z=6 1/16"; Boiler Water Flow Rate at 180F=23 GPM; Cold Water Extension=3 1/4"; Cold Water Inlet Z=5 5/8"; Cold Water NPT=2"; Cold Water Radius=1"; Control Enclosure Location=20"; Control Panel Extension=40 3/16"; Drain Extension=37 1/16"; Drain NPT=1 1/2"; Drain Radius=3/4"; Energy Extension=49 3/16"; Flat Side Distance=66 3/8"; Front Skid Extension=101 3/16"; Height to Drain=3 7/8"; Height to Energy=32 11/16"; Height to Hot Outlet=60 13/16"; Height to Relief=61 7/16"; Hot Outlet Angle=90.00°; Hot Outlet Extension=34 3/16"; Hot Outlet NPT=3"; Hot Outlet Offset Horiz=34 3/16"; Hot Outlet Offset Vert=0"; Hot Outlet Radius=1 1/2"; Rear Skid Extension=33 3/16"; Recovery Rate 40F to 140F (GPH)=270; Relief Valve Extension=36 3/16"; Skid Length=68"; Skid Spacing=36"; U Tube Extension=9 7/16"; U Tube Radius=2 1/4"; Unit Height=81 1/8"; Unit Radius=33 3/16"; Weight=2040
- 5400 L 900A-QWD: BW Inlet Conn X=4"; BW Inlet NPT=4"; BW Inlet Radius=2"; BW Inlet Y=18 11/16"; BW Outlet Conn X=4"; BW Outlet NPT=4"; BW Outlet Radius=2"; BW Outlet Y=33 11/16"; BW Plumbing Total Z=21 3/16"; BW Up=17"; BW Up Radius=2"; BW X=23 1/2"; BW Z=7 1/2"; Boiler Water Flow Rate at 180F=222 GPM; Cold Water Extension=8"; Cold Water Inlet Z=4 1/2"; Cold Water NPT=2 1/2"; Cold Water Radius=1 1/4"; Control Enclosure Location=20"; Control Panel Extension=40 3/16"; Drain Extension=37 1/16"; Drain NPT=1 1/2"; Drain Radius=3/4"; Energy Extension=49 3/16"; Flat Side Distance=66 3/8"; Front Skid Extension=101 3/16"; Height to Drain=3 7/8"; Height to Energy=32 11/16"; Height to Hot Outlet=72 13/16"; Height to Relief=73 7/16"; Hot Outlet Angle=90.00°; Hot Outlet Extension=34 3/16"; Hot Outlet NPT=3"; Hot Outlet Offset Horiz=34 3/16"; Hot Outlet Offset Vert=0"; Hot Outlet Radius=1 1/2"; Rear Skid Extension=33 3/16"; Recovery Rate 40F to 140F (GPH)=2620; Relief Valve Extension=36 3/16"; Skid Length=68"; Skid Spacing=36"; U Tube Extension=13 11/16"; U Tube Radius=7"; Unit Height=93 1/8"; Unit Radius=33 3/16"; Weight=3060
- 5400 L 750A-QWD: BW Inlet Conn X=4"; BW Inlet NPT=4"; BW Inlet Radius=2"; BW Inlet Y=18 11/16"; BW Outlet Conn X=4"; BW Outlet NPT=4"; BW Outlet Radius=2"; BW Outlet Y=33 11/16"; BW Plumbing Total Z=21 3/16"; BW Up=17"; BW Up Radius=2"; BW X=23 1/2"; BW Z=7 1/2"; Boiler Water Flow Rate at 180F=222 GPM; Cold Water Extension=8"; Cold Water Inlet Z=4 1/2"; Cold Water NPT=2 1/2"; Cold Water Radius=1 1/4"; Control Enclosure Location=20"; Control Panel Extension=40 3/16"; Drain Extension=37 1/16"; Drain NPT=1 1/2"; Drain Radius=3/4"; Energy Extension=49 3/16"; Flat Side Distance=66 3/8"; Front Skid Extension=101 3/16"; Height to Drain=3 7/8"; Height to Energy=32 11/16"; Height to Hot Outlet=60 13/16"; Height to Relief=61 7/16"; Hot Outlet Angle=90.00°; Hot Outlet Extension=34 3/16"; Hot Outlet NPT=3"; Hot Outlet Offset Horiz=34 3/16"; Hot Outlet Offset Vert=0"; Hot Outlet Radius=1 1/2"; Rear Skid Extension=33 3/16"; Recovery Rate 40F to 140F (GPH)=2620; Relief Valve Extension=36 3/16"; Skid Length=68"; Skid Spacing=36"; U Tube Extension=13 11/16"; U Tube Radius=7"; Unit Height=81 1/8"; Unit Radius=33 3/16"; Weight=2830
- 500 L 900A-QWD: BW Inlet Conn X=1 5/16"; BW Inlet NPT=1"; BW Inlet Radius=1/2"; BW Inlet Y=5 1/2"; BW Outlet Conn X=1 5/16"; BW Outlet NPT=1"; BW Outlet Radius=1/2"; BW Outlet Y=11 3/16"; BW Plumbing Total Z=15 1/2"; BW Up=5 13/16"; BW Up Radius=1/2"; BW X=7 15/16"; BW Z=6 1/16"; Boiler Water Flow Rate at 180F=20 GPM; Cold Water Extension=3 1/4"; Cold Water Inlet Z=5 5/8"; Cold Water NPT=2"; Cold Water Radius=1"; Control Enclosure Location=20"; Control Panel Extension=40 3/16"; Drain Extension=37 1/16"; Drain NPT=1 1/2"; Drain Radius=3/4"; Energy Extension=49 3/16"; Flat Side Distance=66 3/8"; Front Skid Extension=101 3/16"; Height to Drain=3 7/8"; Height to Energy=32 11/16"; Height to Hot Outlet=72 13/16"; Height to Relief=73 7/16"; Hot Outlet Angle=90.00°; Hot Outlet Extension=34 3/16"; Hot Outlet NPT=3"; Hot Outlet Offset Horiz=34 3/16"; Hot Outlet Offset Vert=0"; Hot Outlet Radius=1 1/2"; Rear Skid Extension=33 3/16"; Recovery Rate 40F to 140F (GPH)=240; Relief Valve Extension=36 3/16"; Skid Length=68"; Skid Spacing=36"; U Tube Extension=9 7/16"; U Tube Radius=2 1/4"; Unit Height=93 1/8"; Unit Radius=33 3/16"; Weight=2290
- 500 L 750A-QWD: BW Inlet Conn X=1 5/16"; BW Inlet NPT=1"; BW Inlet Radius=1/2"; BW Inlet Y=5 1/2"; BW Outlet Conn X=1 5/16"; BW Outlet NPT=1"; BW Outlet Radius=1/2"; BW Outlet Y=11 3/16"; BW Plumbing Total Z=15 1/2"; BW Up=5 13/16"; BW Up Radius=1/2"; BW X=7 15/16"; BW Z=6 1/16"; Boiler Water Flow Rate at 180F=20 GPM; Cold Water Extension=3 1/4"; Cold Water Inlet Z=5 5/8"; Cold Water NPT=2"; Cold Water Radius=1"; Control Enclosure Location=20"; Control Panel Extension=40 3/16"; Drain Extension=37 1/16"; Drain NPT=1 1/2"; Drain Radius=3/4"; Energy Extension=49 3/16"; Flat Side Distance=66 3/8"; Front Skid Extension=101 3/16"; Height to Drain=3 7/8"; Height to Energy=32 11/16"; Height to Hot Outlet=60 13/16"; Height to Relief=61 7/16"; Hot Outlet Angle=90.00°; Hot Outlet Extension=34 3/16"; Hot Outlet NPT=3"; Hot Outlet Offset Horiz=34 3/16"; Hot Outlet Offset Vert=0"; Hot Outlet Radius=1 1/2"; Rear Skid Extension=33 3/16"; Recovery Rate 40F to 140F (GPH)=240; Relief Valve Extension=36 3/16"; Skid Length=68"; Skid Spacing=36"; U Tube Extension=9 7/16"; U Tube Radius=2 1/4"; Unit Height=81 1/8"; Unit Radius=33 3/16"; Weight=2060
- 4500 L 900A-QW: BW Inlet Conn X=3 13/16"; BW Inlet NPT=3"; BW Inlet Radius=1 1/2"; BW Inlet Y=18 11/16"; BW Outlet Conn X=3 13/16"; BW Outlet NPT=3"; BW Outlet Radius=1 1/2"; BW Outlet Y=33 11/16"; BW Plumbing Total Z=18 9/16"; BW Up=16 13/16"; BW Up Radius=1 1/2"; BW X=23 5/16"; BW Z=7 1/2"; Boiler Water Flow Rate at 180F=203 GPM; Cold Water Extension=7 3/8"; Cold Water Inlet Z=5"; Cold Water NPT=2 1/2"; Cold Water Radius=1 1/4"; Control Enclosure Location=20"; Control Panel Extension=40 3/16"; Drain Extension=37 1/16"; Drain NPT=1 1/2"; Drain Radius=3/4"; Energy Extension=49 3/16"; Flat Side Distance=66 3/8"; Front Skid Extension=101 3/16"; Height to Drain=3 7/8"; Height to Energy=32 11/16"; Height to Hot Outlet=72 13/16"; Height to Relief=73 7/16"; Hot Outlet Angle=90.00°; Hot Outlet Extension=34 3/16"; Hot Outlet NPT=3"; Hot Outlet Offset Horiz=34 3/16"; Hot Outlet Offset Vert=0"; Hot Outlet Radius=1 1/2"; Rear Skid Extension=33 3/16"; Recovery Rate 40F to 140F (GPH)=2390; Relief Valve Extension=36 3/16"; Skid Length=68"; Skid Spacing=36"; U Tube Extension=11 1/16"; U Tube Radius=6 3/8"; Unit Height=93 1/8"; Unit Radius=33 3/16"; Weight=2740
- 4500 L 750A-QW: BW Inlet Conn X=3 13/16"; BW Inlet NPT=3"; BW Inlet Radius=1 1/2"; BW Inlet Y=18 11/16"; BW Outlet Conn X=3 13/16"; BW Outlet NPT=3"; BW Outlet Radius=1 1/2"; BW Outlet Y=33 11/16"; BW Plumbing Total Z=18 9/16"; BW Up=16 13/16"; BW Up Radius=1 1/2"; BW X=23 5/16"; BW Z=7 1/2"; Boiler Water Flow Rate at 180F=203 GPM; Cold Water Extension=7 3/8"; Cold Water Inlet Z=5"; Cold Water NPT=2 1/2"; Cold Water Radius=1 1/4"; Control Enclosure Location=20"; Control Panel Extension=40 3/16"; Drain Extension=37 1/16"; Drain NPT=1 1/2"; Drain Radius=3/4"; Energy Extension=49 3/16"; Flat Side Distance=66 3/8"; Front Skid Extension=101 3/16"; Height to Drain=3 7/8"; Height to Energy=32 11/16"; Height to Hot Outlet=60 13/16"; Height to Relief=61 7/16"; Hot Outlet Angle=90.00°; Hot Outlet Extension=34 3/16"; Hot Outlet NPT=3"; Hot Outlet Offset Horiz=34 3/16"; Hot Outlet Offset Vert=0"; Hot Outlet Radius=1 1/2"; Rear Skid Extension=33 3/16"; Recovery Rate 40F to 140F (GPH)=2390; Relief Valve Extension=36 3/16"; Skid Length=68"; Skid Spacing=36"; U Tube Extension=11 1/16"; U Tube Radius=6 3/8"; Unit Height=81 1/8"; Unit Radius=33 3/16"; Weight=2510
- 4300 L 900A-QW: BW Inlet Conn X=3 13/16"; BW Inlet NPT=3"; BW Inlet Radius=1 1/2"; BW Inlet Y=18 11/16"; BW Outlet Conn X=3 13/16"; BW Outlet NPT=3"; BW Outlet Radius=1 1/2"; BW Outlet Y=33 11/16"; BW Plumbing Total Z=18 9/16"; BW Up=16 13/16"; BW Up Radius=1 1/2"; BW X=23 5/16"; BW Z=7 1/2"; Boiler Water Flow Rate at 180F=179 GPM; Cold Water Extension=7 3/8"; Cold Water Inlet Z=5"; Cold Water NPT=2 1/2"; Cold Water Radius=1 1/4"; Control Enclosure Location=20"; Control Panel Extension=40 3/16"; Drain Extension=37 1/16"; Drain NPT=1 1/2"; Drain Radius=3/4"; Energy Extension=49 3/16"; Flat Side Distance=66 3/8"; Front Skid Extension=101 3/16"; Height to Drain=3 7/8"; Height to Energy=32 11/16"; Height to Hot Outlet=72 13/16"; Height to Relief=73 7/16"; Hot Outlet Angle=90.00°; Hot Outlet Extension=34 3/16"; Hot Outlet NPT=3"; Hot Outlet Offset Horiz=34 3/16"; Hot Outlet Offset Vert=0"; Hot Outlet Radius=1 1/2"; Rear Skid Extension=33 3/16"; Recovery Rate 40F to 140F (GPH)=2110; Relief Valve Extension=36 3/16"; Skid Length=68"; Skid Spacing=36"; U Tube Extension=11 1/16"; U Tube Radius=6 3/8"; Unit Height=93 1/8"; Unit Radius=33 3/16"; Weight=2720
- 4300 L 750A-QW: BW Inlet Conn X=3 13/16"; BW Inlet NPT=3"; BW Inlet Radius=1 1/2"; BW Inlet Y=18 11/16"; BW Outlet Conn X=3 13/16"; BW Outlet NPT=3"; BW Outlet Radius=1 1/2"; BW Outlet Y=33 11/16"; BW Plumbing Total Z=18 9/16"; BW Up=16 13/16"; BW Up Radius=1 1/2"; BW X=23 5/16"; BW Z=7 1/2"; Boiler Water Flow Rate at 180F=179 GPM; Cold Water Extension=7 3/8"; Cold Water Inlet Z=5"; Cold Water NPT=2 1/2"; Cold Water Radius=1 1/4"; Control Enclosure Location=20"; Control Panel Extension=40 3/16"; Drain Extension=37 1/16"; Drain NPT=1 1/2"; Drain Radius=3/4"; Energy Extension=49 3/16"; Flat Side Distance=66 3/8"; Front Skid Extension=101 3/16"; Height to Drain=3 7/8"; Height to Energy=32 11/16"; Height to Hot Outlet=60 13/16"; Height to Relief=61 7/16"; Hot Outlet Angle=90.00°; Hot Outlet Extension=34 3/16"; Hot Outlet NPT=3"; Hot Outlet Offset Horiz=34 3/16"; Hot Outlet Offset Vert=0"; Hot Outlet Radius=1 1/2"; Rear Skid Extension=33 3/16"; Recovery Rate 40F to 140F (GPH)=2110; Relief Valve Extension=36 3/16"; Skid Length=68"; Skid Spacing=36"; U Tube Extension=11 1/16"; U Tube Radius=6 3/8"; Unit Height=81 1/8"; Unit Radius=33 3/16"; Weight=2490
- 4200 L 900A-QWD: BW Inlet Conn X=3 13/16"; BW Inlet NPT=3"; BW Inlet Radius=1 1/2"; BW Inlet Y=18 11/16"; BW Outlet Conn X=3 13/16"; BW Outlet NPT=3"; BW Outlet Radius=1 1/2"; BW Outlet Y=33 11/16"; BW Plumbing Total Z=18 9/16"; BW Up=16 13/16"; BW Up Radius=1 1/2"; BW X=23 5/16"; BW Z=7 1/2"; Boiler Water Flow Rate at 180F=179 GPM; Cold Water Extension=7 3/8"; Cold Water Inlet Z=5"; Cold Water NPT=2 1/2"; Cold Water Radius=1 1/4"; Control Enclosure Location=20"; Control Panel Extension=40 3/16"; Drain Extension=37 1/16"; Drain NPT=1 1/2"; Drain Radius=3/4"; Energy Extension=49 3/16"; Flat Side Distance=66 3/8"; Front Skid Extension=101 3/16"; Height to Drain=3 7/8"; Height to Energy=32 11/16"; Height to Hot Outlet=72 13/16"; Height to Relief=73 7/16"; Hot Outlet Angle=90.00°; Hot Outlet Extension=34 3/16"; Hot Outlet NPT=3"; Hot Outlet Offset Horiz=34 3/16"; Hot Outlet Offset Vert=0"; Hot Outlet Radius=1 1/2"; Rear Skid Extension=33 3/16"; Recovery Rate 40F to 140F (GPH)=2100; Relief Valve Extension=36 3/16"; Skid Length=68"; Skid Spacing=36"; U Tube Extension=11 1/16"; U Tube Radius=6 3/8"; Unit Height=93 1/8"; Unit Radius=33 3/16"; Weight=2950
- 4200 L 750A-QWD: BW Inlet Conn X=3 13/16"; BW Inlet NPT=3"; BW Inlet Radius=1 1/2"; BW Inlet Y=18 11/16"; BW Outlet Conn X=3 13/16"; BW Outlet NPT=3"; BW Outlet Radius=1 1/2"; BW Outlet Y=33 11/16"; BW Plumbing Total Z=18 9/16"; BW Up=16 13/16"; BW Up Radius=1 1/2"; BW X=23 5/16"; BW Z=7 1/2"; Boiler Water Flow Rate at 180F=179 GPM; Cold Water Extension=7 3/8"; Cold Water Inlet Z=5"; Cold Water NPT=2 1/2"; Cold Water Radius=1 1/4"; Control Enclosure Location=20"; Control Panel Extension=40 3/16"; Drain Extension=37 1/16"; Drain NPT=1 1/2"; Drain Radius=3/4"; Energy Extension=49 3/16"; Flat Side Distance=66 3/8"; Front Skid Extension=101 3/16"; Height to Drain=3 7/8"; Height to Energy=32 11/16"; Height to Hot Outlet=60 13/16"; Height to Relief=61 7/16"; Hot Outlet Angle=90.00°; Hot Outlet Extension=34 3/16"; Hot Outlet NPT=3"; Hot Outlet Offset Horiz=34 3/16"; Hot Outlet Offset Vert=0"; Hot Outlet Radius=1 1/2"; Rear Skid Extension=33 3/16"; Recovery Rate 40F to 140F (GPH)=2100; Relief Valve Extension=36 3/16"; Skid Length=68"; Skid Spacing=36"; U Tube Extension=11 1/16"; U Tube Radius=6 3/8"; Unit Height=81 1/8"; Unit Radius=33 3/16"; Weight=2720
- 4000 L 900A-QW: BW Inlet Conn X=3 13/16"; BW Inlet NPT=3"; BW Inlet Radius=1 1/2"; BW Inlet Y=18 11/16"; BW Outlet Conn X=3 13/16"; BW Outlet NPT=3"; BW Outlet Radius=1 1/2"; BW Outlet Y=33 11/16"; BW Plumbing Total Z=18 9/16"; BW Up=16 13/16"; BW Up Radius=1 1/2"; BW X=23 5/16"; BW Z=7 1/2"; Boiler Water Flow Rate at 180F=152 GPM; Cold Water Extension=7 3/8"; Cold Water Inlet Z=5"; Cold Water NPT=2 1/2"; Cold Water Radius=1 1/4"; Control Enclosure Location=20"; Control Panel Extension=40 3/16"; Drain Extension=37 1/16"; Drain NPT=1 1/2"; Drain Radius=3/4"; Energy Extension=49 3/16"; Flat Side Distance=66 3/8"; Front Skid Extension=101 3/16"; Height to Drain=3 7/8"; Height to Energy=32 11/16"; Height to Hot Outlet=72 13/16"; Height to Relief=73 7/16"; Hot Outlet Angle=90.00°; Hot Outlet Extension=34 3/16"; Hot Outlet NPT=3"; Hot Outlet Offset Horiz=34 3/16"; Hot Outlet Offset Vert=0"; Hot Outlet Radius=1 1/2"; Rear Skid Extension=33 3/16"; Recovery Rate 40F to 140F (GPH)=1790; Relief Valve Extension=36 3/16"; Skid Length=68"; Skid Spacing=36"; U Tube Extension=11 1/16"; U Tube Radius=6 3/8"; Unit Height=93 1/8"; Unit Radius=33 3/16"; Weight=2690
- 4000 L 750A-QW: BW Inlet Conn X=3 13/16"; BW Inlet NPT=3"; BW Inlet Radius=1 1/2"; BW Inlet Y=18 11/16"; BW Outlet Conn X=3 13/16"; BW Outlet NPT=3"; BW Outlet Radius=1 1/2"; BW Outlet Y=33 11/16"; BW Plumbing Total Z=18 9/16"; BW Up=16 13/16"; BW Up Radius=1 1/2"; BW X=23 5/16"; BW Z=7 1/2"; Boiler Water Flow Rate at 180F=152 GPM; Cold Water Extension=7 3/8"; Cold Water Inlet Z=5"; Cold Water NPT=2 1/2"; Cold Water Radius=1 1/4"; Control Enclosure Location=20"; Control Panel Extension=40 3/16"; Drain Extension=37 1/16"; Drain NPT=1 1/2"; Drain Radius=3/4"; Energy Extension=49 3/16"; Flat Side Distance=66 3/8"; Front Skid Extension=101 3/16"; Height to Drain=3 7/8"; Height to Energy=32 11/16"; Height to Hot Outlet=60 13/16"; Height to Relief=61 7/16"; Hot Outlet Angle=90.00°; Hot Outlet Extension=34 3/16"; Hot Outlet NPT=3"; Hot Outlet Offset Horiz=34 3/16"; Hot Outlet Offset Vert=0"; Hot Outlet Radius=1 1/2"; Rear Skid Extension=33 3/16"; Recovery Rate 40F to 140F (GPH)=1790; Relief Valve Extension=36 3/16"; Skid Length=68"; Skid Spacing=36"; U Tube Extension=11 1/16"; U Tube Radius=6 3/8"; Unit Height=81 1/8"; Unit Radius=33 3/16"; Weight=2460
- 3500 L 900A-QW: BW Inlet Conn X=2 15/16"; BW Inlet NPT=2 1/2"; BW Inlet Radius=1 1/4"; BW Inlet Y=18 11/16"; BW Outlet Conn X=2 15/16"; BW Outlet NPT=2 1/2"; BW Outlet Radius=1 1/4"; BW Outlet Y=33 11/16"; BW Plumbing Total Z=18 1/16"; BW Up=15 15/16"; BW Up Radius=1 1/4"; BW X=22 7/16"; BW Z=7 1/2"; Boiler Water Flow Rate at 180F=138 GPM; Cold Water Extension=6 3/8"; Cold Water Inlet Z=5 1/8"; Cold Water NPT=2 1/2"; Cold Water Radius=1 1/4"; Control Enclosure Location=20"; Control Panel Extension=40 3/16"; Drain Extension=37 1/16"; Drain NPT=1 1/2"; Drain Radius=3/4"; Energy Extension=49 3/16"; Flat Side Distance=66 3/8"; Front Skid Extension=101 3/16"; Height to Drain=3 7/8"; Height to Energy=32 11/16"; Height to Hot Outlet=72 13/16"; Height to Relief=73 7/16"; Hot Outlet Angle=90.00°; Hot Outlet Extension=34 3/16"; Hot Outlet NPT=3"; Hot Outlet Offset Horiz=34 3/16"; Hot Outlet Offset Vert=0"; Hot Outlet Radius=1 1/2"; Rear Skid Extension=33 3/16"; Recovery Rate 40F to 140F (GPH)=1630; Relief Valve Extension=36 3/16"; Skid Length=68"; Skid Spacing=36"; U Tube Extension=10 9/16"; U Tube Radius=5 3/8"; Unit Height=93 1/8"; Unit Radius=33 3/16"; Weight=2610
- 3500 L 750A-QW: BW Inlet Conn X=2 15/16"; BW Inlet NPT=2 1/2"; BW Inlet Radius=1 1/4"; BW Inlet Y=18 11/16"; BW Outlet Conn X=2 15/16"; BW Outlet NPT=2 1/2"; BW Outlet Radius=1 1/4"; BW Outlet Y=33 11/16"; BW Plumbing Total Z=18 1/16"; BW Up=15 15/16"; BW Up Radius=1 1/4"; BW X=22 7/16"; BW Z=7 1/2"; Boiler Water Flow Rate at 180F=138 GPM; Cold Water Extension=6 3/8"; Cold Water Inlet Z=5 1/8"; Cold Water NPT=2 1/2"; Cold Water Radius=1 1/4"; Control Enclosure Location=20"; Control Panel Extension=40 3/16"; Drain Extension=37 1/16"; Drain NPT=1 1/2"; Drain Radius=3/4"; Energy Extension=49 3/16"; Flat Side Distance=66 3/8"; Front Skid Extension=101 3/16"; Height to Drain=3 7/8"; Height to Energy=32 11/16"; Height to Hot Outlet=60 13/16"; Height to Relief=61 7/16"; Hot Outlet Angle=90.00°; Hot Outlet Extension=34 3/16"; Hot Outlet NPT=3"; Hot Outlet Offset Horiz=34 3/16"; Hot Outlet Offset Vert=0"; Hot Outlet Radius=1 1/2"; Rear Skid Extension=33 3/16"; Recovery Rate 40F to 140F (GPH)=1630; Relief Valve Extension=36 3/16"; Skid Length=68"; Skid Spacing=36"; U Tube Extension=10 9/16"; U Tube Radius=5 3/8"; Unit Height=81 1/8"; Unit Radius=33 3/16"; Weight=2370
- 3400 L 900A-QWD: BW Inlet Conn X=3 11/16"; BW Inlet NPT=2 1/2"; BW Inlet Radius=1 1/4"; BW Inlet Y=18 11/16"; BW Outlet Conn X=3 11/16"; BW Outlet NPT=2 1/2"; BW Outlet Radius=1 1/4"; BW Outlet Y=33 11/16"; BW Plumbing Total Z=18 9/16"; BW Up=16 13/16"; BW Up Radius=1 1/4"; BW X=23 5/16"; BW Z=7 1/2"; Boiler Water Flow Rate at 180F=138 GPM; Cold Water Extension=7 3/8"; Cold Water Inlet Z=5"; Cold Water NPT=2 1/2"; Cold Water Radius=1 1/4"; Control Enclosure Location=20"; Control Panel Extension=40 3/16"; Drain Extension=37 1/16"; Drain NPT=1 1/2"; Drain Radius=3/4"; Energy Extension=49 3/16"; Flat Side Distance=66 3/8"; Front Skid Extension=101 3/16"; Height to Drain=3 7/8"; Height to Energy=32 11/16"; Height to Hot Outlet=72 13/16"; Height to Relief=73 7/16"; Hot Outlet Angle=90.00°; Hot Outlet Extension=34 3/16"; Hot Outlet NPT=3"; Hot Outlet Offset Horiz=34 3/16"; Hot Outlet Offset Vert=0"; Hot Outlet Radius=1 1/2"; Rear Skid Extension=33 3/16"; Recovery Rate 40F to 140F (GPH)=1620; Relief Valve Extension=36 3/16"; Skid Length=68"; Skid Spacing=36"; U Tube Extension=11 1/16"; U Tube Radius=6 3/8"; Unit Height=93 1/8"; Unit Radius=33 3/16"; Weight=2860
- 3400 L 750A-QWD: BW Inlet Conn X=3 11/16"; BW Inlet NPT=2 1/2"; BW Inlet Radius=1 1/4"; BW Inlet Y=18 11/16"; BW Outlet Conn X=3 11/16"; BW Outlet NPT=2 1/2"; BW Outlet Radius=1 1/4"; BW Outlet Y=33 11/16"; BW Plumbing Total Z=18 9/16"; BW Up=16 13/16"; BW Up Radius=1 1/4"; BW X=23 5/16"; BW Z=7 1/2"; Boiler Water Flow Rate at 180F=138 GPM; Cold Water Extension=7 3/8"; Cold Water Inlet Z=5"; Cold Water NPT=2 1/2"; Cold Water Radius=1 1/4"; Control Enclosure Location=20"; Control Panel Extension=40 3/16"; Drain Extension=37 1/16"; Drain NPT=1 1/2"; Drain Radius=3/4"; Energy Extension=49 3/16"; Flat Side Distance=66 3/8"; Front Skid Extension=101 3/16"; Height to Drain=3 7/8"; Height to Energy=32 11/16"; Height to Hot Outlet=60 13/16"; Height to Relief=61 7/16"; Hot Outlet Angle=90.00°; Hot Outlet Extension=34 3/16"; Hot Outlet NPT=3"; Hot Outlet Offset Horiz=34 3/16"; Hot Outlet Offset Vert=0"; Hot Outlet Radius=1 1/2"; Rear Skid Extension=33 3/16"; Recovery Rate 40F to 140F (GPH)=1620; Relief Valve Extension=36 3/16"; Skid Length=68"; Skid Spacing=36"; U Tube Extension=11 1/16"; U Tube Radius=6 3/8"; Unit Height=81 1/8"; Unit Radius=33 3/16"; Weight=2640
- 3000 L 900A-QW: BW Inlet Conn X=2 15/16"; BW Inlet NPT=2 1/2"; BW Inlet Radius=1 1/4"; BW Inlet Y=18 11/16"; BW Outlet Conn X=2 15/16"; BW Outlet NPT=2 1/2"; BW Outlet Radius=1 1/4"; BW Outlet Y=33 11/16"; BW Plumbing Total Z=18 1/16"; BW Up=15 15/16"; BW Up Radius=1 1/4"; BW X=22 7/16"; BW Z=7 1/2"; Boiler Water Flow Rate at 180F=120 GPM; Cold Water Extension=6 3/8"; Cold Water Inlet Z=5 1/8"; Cold Water NPT=2 1/2"; Cold Water Radius=1 1/4"; Control Enclosure Location=20"; Control Panel Extension=40 3/16"; Drain Extension=37 1/16"; Drain NPT=1 1/2"; Drain Radius=3/4"; Energy Extension=49 3/16"; Flat Side Distance=66 3/8"; Front Skid Extension=101 3/16"; Height to Drain=3 7/8"; Height to Energy=32 11/16"; Height to Hot Outlet=72 13/16"; Height to Relief=73 7/16"; Hot Outlet Angle=90.00°; Hot Outlet Extension=34 3/16"; Hot Outlet NPT=3"; Hot Outlet Offset Horiz=34 3/16"; Hot Outlet Offset Vert=0"; Hot Outlet Radius=1 1/2"; Rear Skid Extension=33 3/16"; Recovery Rate 40F to 140F (GPH)=1420; Relief Valve Extension=36 3/16"; Skid Length=68"; Skid Spacing=36"; U Tube Extension=10 9/16"; U Tube Radius=5 3/8"; Unit Height=93 1/8"; Unit Radius=33 3/16"; Weight=2600
- 3000 L 750A-QW: BW Inlet Conn X=2 15/16"; BW Inlet NPT=2 1/2"; BW Inlet Radius=1 1/4"; BW Inlet Y=18 11/16"; BW Outlet Conn X=2 15/16"; BW Outlet NPT=2 1/2"; BW Outlet Radius=1 1/4"; BW Outlet Y=33 11/16"; BW Plumbing Total Z=18 1/16"; BW Up=15 15/16"; BW Up Radius=1 1/4"; BW X=22 7/16"; BW Z=7 1/2"; Boiler Water Flow Rate at 180F=120 GPM; Cold Water Extension=6 3/8"; Cold Water Inlet Z=5 1/8"; Cold Water NPT=2 1/2"; Cold Water Radius=1 1/4"; Control Enclosure Location=20"; Control Panel Extension=40 3/16"; Drain Extension=37 1/16"; Drain NPT=1 1/2"; Drain Radius=3/4"; Energy Extension=49 3/16"; Flat Side Distance=66 3/8"; Front Skid Extension=101 3/16"; Height to Drain=3 7/8"; Height to Energy=32 11/16"; Height to Hot Outlet=60 13/16"; Height to Relief=61 7/16"; Hot Outlet Angle=90.00°; Hot Outlet Extension=34 3/16"; Hot Outlet NPT=3"; Hot Outlet Offset Horiz=34 3/16"; Hot Outlet Offset Vert=0"; Hot Outlet Radius=1 1/2"; Rear Skid Extension=33 3/16"; Recovery Rate 40F to 140F (GPH)=1420; Relief Valve Extension=36 3/16"; Skid Length=68"; Skid Spacing=36"; U Tube Extension=10 9/16"; U Tube Radius=5 3/8"; Unit Height=81 1/8"; Unit Radius=33 3/16"; Weight=2370
- 300 L 900A-QW: BW Inlet Conn X=1 5/16"; BW Inlet NPT=3/4"; BW Inlet Radius=3/8"; BW Inlet Y=5"; BW Outlet Conn X=1 5/16"; BW Outlet NPT=3/4"; BW Outlet Radius=3/8"; BW Outlet Y=9 1/16"; BW Plumbing Total Z=15 3/8"; BW Up=5 3/4"; BW Up Radius=3/8"; BW X=8 1/16"; BW Z=5 15/16"; Boiler Water Flow Rate at 180F=12 GPM; Cold Water Extension=3 1/4"; Cold Water Inlet Z=5 5/8"; Cold Water NPT=2"; Cold Water Radius=1"; Control Enclosure Location=20"; Control Panel Extension=40 3/16"; Drain Extension=37 1/16"; Drain NPT=1 1/2"; Drain Radius=3/4"; Energy Extension=49 3/16"; Flat Side Distance=66 3/8"; Front Skid Extension=101 3/16"; Height to Drain=3 7/8"; Height to Energy=32 11/16"; Height to Hot Outlet=72 13/16"; Height to Relief=73 7/16"; Hot Outlet Angle=90.00°; Hot Outlet Extension=34 3/16"; Hot Outlet NPT=3"; Hot Outlet Offset Horiz=34 3/16"; Hot Outlet Offset Vert=0"; Hot Outlet Radius=1 1/2"; Rear Skid Extension=33 3/16"; Recovery Rate 40F to 140F (GPH)=140; Relief Valve Extension=36 3/16"; Skid Length=68"; Skid Spacing=36"; U Tube Extension=9 7/16"; U Tube Radius=2 1/4"; Unit Height=93 1/8"; Unit Radius=33 3/16"; Weight=2260
- 300 L 750A-QW: BW Inlet Conn X=1 5/16"; BW Inlet NPT=3/4"; BW Inlet Radius=3/8"; BW Inlet Y=5"; BW Outlet Conn X=1 5/16"; BW Outlet NPT=3/4"; BW Outlet Radius=3/8"; BW Outlet Y=9 1/16"; BW Plumbing Total Z=15 3/8"; BW Up=5 3/4"; BW Up Radius=3/8"; BW X=8 1/16"; BW Z=5 15/16"; Boiler Water Flow Rate at 180F=12 GPM; Cold Water Extension=3 1/4"; Cold Water Inlet Z=5 5/8"; Cold Water NPT=2"; Cold Water Radius=1"; Control Enclosure Location=20"; Control Panel Extension=40 3/16"; Drain Extension=37 1/16"; Drain NPT=1 1/2"; Drain Radius=3/4"; Energy Extension=49 3/16"; Flat Side Distance=66 3/8"; Front Skid Extension=101 3/16"; Height to Drain=3 7/8"; Height to Energy=32 11/16"; Height to Hot Outlet=60 13/16"; Height to Relief=61 7/16"; Hot Outlet Angle=90.00°; Hot Outlet Extension=34 3/16"; Hot Outlet NPT=3"; Hot Outlet Offset Horiz=34 3/16"; Hot Outlet Offset Vert=0"; Hot Outlet Radius=1 1/2"; Rear Skid Extension=33 3/16"; Recovery Rate 40F to 140F (GPH)=140; Relief Valve Extension=36 3/16"; Skid Length=68"; Skid Spacing=36"; U Tube Extension=9 7/16"; U Tube Radius=2 1/4"; Unit Height=81 1/8"; Unit Radius=33 3/16"; Weight=2030
- 2800 L 900A-QWD: BW Inlet Conn X=3 11/16"; BW Inlet NPT=2 1/2"; BW Inlet Radius=1 1/4"; BW Inlet Y=12 3/8"; BW Outlet Conn X=3 11/16"; BW Outlet NPT=2 1/2"; BW Outlet Radius=1 1/4"; BW Outlet Y=23 7/16"; BW Plumbing Total Z=22 1/16"; BW Up=13 1/16"; BW Up Radius=1 1/4"; BW X=17 13/16"; BW Z=11 1/2"; Boiler Water Flow Rate at 180F=122 GPM; Cold Water Extension=7 3/8"; Cold Water Inlet Z=5 1/8"; Cold Water NPT=2 1/2"; Cold Water Radius=1 1/4"; Control Enclosure Location=20"; Control Panel Extension=40 3/16"; Drain Extension=37 1/16"; Drain NPT=1 1/2"; Drain Radius=3/4"; Energy Extension=49 3/16"; Flat Side Distance=66 3/8"; Front Skid Extension=101 3/16"; Height to Drain=3 7/8"; Height to Energy=32 11/16"; Height to Hot Outlet=72 13/16"; Height to Relief=73 7/16"; Hot Outlet Angle=90.00°; Hot Outlet Extension=34 3/16"; Hot Outlet NPT=3"; Hot Outlet Offset Horiz=34 3/16"; Hot Outlet Offset Vert=0"; Hot Outlet Radius=1 1/2"; Rear Skid Extension=33 3/16"; Recovery Rate 40F to 140F (GPH)=1430; Relief Valve Extension=36 3/16"; Skid Length=68"; Skid Spacing=36"; U Tube Extension=10 9/16"; U Tube Radius=6 3/8"; Unit Height=93 1/8"; Unit Radius=33 3/16"; Weight=2680
- 2800 L 750A-QWD: BW Inlet Conn X=3 11/16"; BW Inlet NPT=2 1/2"; BW Inlet Radius=1 1/4"; BW Inlet Y=12 3/8"; BW Outlet Conn X=3 11/16"; BW Outlet NPT=2 1/2"; BW Outlet Radius=1 1/4"; BW Outlet Y=23 7/16"; BW Plumbing Total Z=22 1/16"; BW Up=13 1/16"; BW Up Radius=1 1/4"; BW X=17 13/16"; BW Z=11 1/2"; Boiler Water Flow Rate at 180F=122 GPM; Cold Water Extension=7 3/8"; Cold Water Inlet Z=5 1/8"; Cold Water NPT=2 1/2"; Cold Water Radius=1 1/4"; Control Enclosure Location=20"; Control Panel Extension=40 3/16"; Drain Extension=37 1/16"; Drain NPT=1 1/2"; Drain Radius=3/4"; Energy Extension=49 3/16"; Flat Side Distance=66 3/8"; Front Skid Extension=101 3/16"; Height to Drain=3 7/8"; Height to Energy=32 11/16"; Height to Hot Outlet=60 13/16"; Height to Relief=61 7/16"; Hot Outlet Angle=90.00°; Hot Outlet Extension=34 3/16"; Hot Outlet NPT=3"; Hot Outlet Offset Horiz=34 3/16"; Hot Outlet Offset Vert=0"; Hot Outlet Radius=1 1/2"; Rear Skid Extension=33 3/16"; Recovery Rate 40F to 140F (GPH)=1430; Relief Valve Extension=36 3/16"; Skid Length=68"; Skid Spacing=36"; U Tube Extension=10 9/16"; U Tube Radius=6 3/8"; Unit Height=81 1/8"; Unit Radius=33 3/16"; Weight=2440
- 2600 L 900A-QW: BW Inlet Conn X=2 15/16"; BW Inlet NPT=2 1/2"; BW Inlet Radius=1 1/4"; BW Inlet Y=12 3/8"; BW Outlet Conn X=2 15/16"; BW Outlet NPT=2 1/2"; BW Outlet Radius=1 1/4"; BW Outlet Y=23 7/16"; BW Plumbing Total Z=22 1/16"; BW Up=13 1/16"; BW Up Radius=1 1/4"; BW X=17 13/16"; BW Z=11 1/2"; Boiler Water Flow Rate at 180F=102 GPM; Cold Water Extension=6 3/8"; Cold Water Inlet Z=5 1/8"; Cold Water NPT=2 1/2"; Cold Water Radius=1 1/4"; Control Enclosure Location=20"; Control Panel Extension=40 3/16"; Drain Extension=37 1/16"; Drain NPT=1 1/2"; Drain Radius=3/4"; Energy Extension=49 3/16"; Flat Side Distance=66 3/8"; Front Skid Extension=101 3/16"; Height to Drain=3 7/8"; Height to Energy=32 11/16"; Height to Hot Outlet=72 13/16"; Height to Relief=73 7/16"; Hot Outlet Angle=90.00°; Hot Outlet Extension=34 3/16"; Hot Outlet NPT=3"; Hot Outlet Offset Horiz=34 3/16"; Hot Outlet Offset Vert=0"; Hot Outlet Radius=1 1/2"; Rear Skid Extension=33 3/16"; Recovery Rate 40F to 140F (GPH)=1200; Relief Valve Extension=36 3/16"; Skid Length=68"; Skid Spacing=36"; U Tube Extension=10 9/16"; U Tube Radius=5 3/8"; Unit Height=93 1/8"; Unit Radius=33 3/16"; Weight=2510
- 2600 L 750A-QW: BW Inlet Conn X=2 15/16"; BW Inlet NPT=2 1/2"; BW Inlet Radius=1 1/4"; BW Inlet Y=12 3/8"; BW Outlet Conn X=2 15/16"; BW Outlet NPT=2 1/2"; BW Outlet Radius=1 1/4"; BW Outlet Y=23 7/16"; BW Plumbing Total Z=22 1/16"; BW Up=13 1/16"; BW Up Radius=1 1/4"; BW X=17 13/16"; BW Z=11 1/2"; Boiler Water Flow Rate at 180F=102 GPM; Cold Water Extension=6 3/8"; Cold Water Inlet Z=5 1/8"; Cold Water NPT=2 1/2"; Cold Water Radius=1 1/4"; Control Enclosure Location=20"; Control Panel Extension=40 3/16"; Drain Extension=37 1/16"; Drain NPT=1 1/2"; Drain Radius=3/4"; Energy Extension=49 3/16"; Flat Side Distance=66 3/8"; Front Skid Extension=101 3/16"; Height to Drain=3 7/8"; Height to Energy=32 11/16"; Height to Hot Outlet=60 13/16"; Height to Relief=61 7/16"; Hot Outlet Angle=90.00°; Hot Outlet Extension=34 3/16"; Hot Outlet NPT=3"; Hot Outlet Offset Horiz=34 3/16"; Hot Outlet Offset Vert=0"; Hot Outlet Radius=1 1/2"; Rear Skid Extension=33 3/16"; Recovery Rate 40F to 140F (GPH)=1200; Relief Valve Extension=36 3/16"; Skid Length=68"; Skid Spacing=36"; U Tube Extension=10 9/16"; U Tube Radius=5 3/8"; Unit Height=81 1/8"; Unit Radius=33 3/16"; Weight=2280
- 250 L 900A-QWD: BW Inlet Conn X=1 5/16"; BW Inlet NPT=3/4"; BW Inlet Radius=3/8"; BW Inlet Y=5"; BW Outlet Conn X=1 5/16"; BW Outlet NPT=3/4"; BW Outlet Radius=3/8"; BW Outlet Y=9 1/16"; BW Plumbing Total Z=15 3/8"; BW Up=5 3/4"; BW Up Radius=3/8"; BW X=8 1/16"; BW Z=5 15/16"; Boiler Water Flow Rate at 180F=11 GPM; Cold Water Extension=3 1/4"; Cold Water Inlet Z=5 5/8"; Cold Water NPT=2"; Cold Water Radius=1"; Control Enclosure Location=20"; Control Panel Extension=40 3/16"; Drain Extension=37 1/16"; Drain NPT=1 1/2"; Drain Radius=3/4"; Energy Extension=49 3/16"; Flat Side Distance=66 3/8"; Front Skid Extension=101 3/16"; Height to Drain=3 7/8"; Height to Energy=32 11/16"; Height to Hot Outlet=72 13/16"; Height to Relief=73 7/16"; Hot Outlet Angle=90.00°; Hot Outlet Extension=34 3/16"; Hot Outlet NPT=3"; Hot Outlet Offset Horiz=34 3/16"; Hot Outlet Offset Vert=0"; Hot Outlet Radius=1 1/2"; Rear Skid Extension=33 3/16"; Recovery Rate 40F to 140F (GPH)=130; Relief Valve Extension=36 3/16"; Skid Length=68"; Skid Spacing=36"; U Tube Extension=9 7/16"; U Tube Radius=2 1/4"; Unit Height=93 1/8"; Unit Radius=33 3/16"; Weight=2280
- 250 L 750A-QWD: BW Inlet Conn X=1 5/16"; BW Inlet NPT=3/4"; BW Inlet Radius=3/8"; BW Inlet Y=5"; BW Outlet Conn X=1 5/16"; BW Outlet NPT=3/4"; BW Outlet Radius=3/8"; BW Outlet Y=9 1/16"; BW Plumbing Total Z=15 3/8"; BW Up=5 3/4"; BW Up Radius=3/8"; BW X=8 1/16"; BW Z=5 15/16"; Boiler Water Flow Rate at 180F=11 GPM; Cold Water Extension=3 1/4"; Cold Water Inlet Z=5 5/8"; Cold Water NPT=2"; Cold Water Radius=1"; Control Enclosure Location=20"; Control Panel Extension=40 3/16"; Drain Extension=37 1/16"; Drain NPT=1 1/2"; Drain Radius=3/4"; Energy Extension=49 3/16"; Flat Side Distance=66 3/8"; Front Skid Extension=101 3/16"; Height to Drain=3 7/8"; Height to Energy=32 11/16"; Height to Hot Outlet=60 13/16"; Height to Relief=61 7/16"; Hot Outlet Angle=90.00°; Hot Outlet Extension=34 3/16"; Hot Outlet NPT=3"; Hot Outlet Offset Horiz=34 3/16"; Hot Outlet Offset Vert=0"; Hot Outlet Radius=1 1/2"; Rear Skid Extension=33 3/16"; Recovery Rate 40F to 140F (GPH)=130; Relief Valve Extension=36 3/16"; Skid Length=68"; Skid Spacing=36"; U Tube Extension=9 7/16"; U Tube Radius=2 1/4"; Unit Height=81 1/8"; Unit Radius=33 3/16"; Weight=2050
- 2300 L 900A-QW: BW Inlet Conn X=2 15/16"; BW Inlet NPT=2"; BW Inlet Radius=1"; BW Inlet Y=12 3/8"; BW Outlet Conn X=2 15/16"; BW Outlet NPT=2"; BW Outlet Radius=1"; BW Outlet Y=23 7/16"; BW Plumbing Total Z=22 1/16"; BW Up=13 1/16"; BW Up Radius=1"; BW X=17 13/16"; BW Z=11 1/2"; Boiler Water Flow Rate at 180F=87 GPM; Cold Water Extension=6 3/8"; Cold Water Inlet Z=5 1/8"; Cold Water NPT=2 1/2"; Cold Water Radius=1 1/4"; Control Enclosure Location=20"; Control Panel Extension=40 3/16"; Drain Extension=37 1/16"; Drain NPT=1 1/2"; Drain Radius=3/4"; Energy Extension=49 3/16"; Flat Side Distance=66 3/8"; Front Skid Extension=101 3/16"; Height to Drain=3 7/8"; Height to Energy=32 11/16"; Height to Hot Outlet=72 13/16"; Height to Relief=73 7/16"; Hot Outlet Angle=90.00°; Hot Outlet Extension=34 3/16"; Hot Outlet NPT=3"; Hot Outlet Offset Horiz=34 3/16"; Hot Outlet Offset Vert=0"; Hot Outlet Radius=1 1/2"; Rear Skid Extension=33 3/16"; Recovery Rate 40F to 140F (GPH)=1020; Relief Valve Extension=36 3/16"; Skid Length=68"; Skid Spacing=36"; U Tube Extension=10 9/16"; U Tube Radius=5 3/8"; Unit Height=93 1/8"; Unit Radius=33 3/16"; Weight=2500
- 2300 L 750A-QW: BW Inlet Conn X=2 15/16"; BW Inlet NPT=2"; BW Inlet Radius=1"; BW Inlet Y=12 3/8"; BW Outlet Conn X=2 15/16"; BW Outlet NPT=2"; BW Outlet Radius=1"; BW Outlet Y=23 7/16"; BW Plumbing Total Z=22 1/16"; BW Up=13 1/16"; BW Up Radius=1"; BW X=17 13/16"; BW Z=11 1/2"; Boiler Water Flow Rate at 180F=87 GPM; Cold Water Extension=6 3/8"; Cold Water Inlet Z=5 1/8"; Cold Water NPT=2 1/2"; Cold Water Radius=1 1/4"; Control Enclosure Location=20"; Control Panel Extension=40 3/16"; Drain Extension=37 1/16"; Drain NPT=1 1/2"; Drain Radius=3/4"; Energy Extension=49 3/16"; Flat Side Distance=66 3/8"; Front Skid Extension=101 3/16"; Height to Drain=3 7/8"; Height to Energy=32 11/16"; Height to Hot Outlet=60 13/16"; Height to Relief=61 7/16"; Hot Outlet Angle=90.00°; Hot Outlet Extension=34 3/16"; Hot Outlet NPT=3"; Hot Outlet Offset Horiz=34 3/16"; Hot Outlet Offset Vert=0"; Hot Outlet Radius=1 1/2"; Rear Skid Extension=33 3/16"; Recovery Rate 40F to 140F (GPH)=1020; Relief Valve Extension=36 3/16"; Skid Length=68"; Skid Spacing=36"; U Tube Extension=10 9/16"; U Tube Radius=5 3/8"; Unit Height=81 1/8"; Unit Radius=33 3/16"; Weight=2270
- 2200 L 900A-QWD: BW Inlet Conn X=2 15/16"; BW Inlet NPT=2"; BW Inlet Radius=1"; BW Inlet Y=12 3/8"; BW Outlet Conn X=2 15/16"; BW Outlet NPT=2"; BW Outlet Radius=1"; BW Outlet Y=23 7/16"; BW Plumbing Total Z=22 1/16"; BW Up=13 1/16"; BW Up Radius=1"; BW X=17 13/16"; BW Z=11 1/2"; Boiler Water Flow Rate at 180F=92 GPM; Cold Water Extension=6 3/8"; Cold Water Inlet Z=5 1/8"; Cold Water NPT=2 1/2"; Cold Water Radius=1 1/4"; Control Enclosure Location=20"; Control Panel Extension=40 3/16"; Drain Extension=37 1/16"; Drain NPT=1 1/2"; Drain Radius=3/4"; Energy Extension=49 3/16"; Flat Side Distance=66 3/8"; Front Skid Extension=101 3/16"; Height to Drain=3 7/8"; Height to Energy=32 11/16"; Height to Hot Outlet=72 13/16"; Height to Relief=73 7/16"; Hot Outlet Angle=90.00°; Hot Outlet Extension=34 3/16"; Hot Outlet NPT=3"; Hot Outlet Offset Horiz=34 3/16"; Hot Outlet Offset Vert=0"; Hot Outlet Radius=1 1/2"; Rear Skid Extension=33 3/16"; Recovery Rate 40F to 140F (GPH)=1090; Relief Valve Extension=36 3/16"; Skid Length=68"; Skid Spacing=36"; U Tube Extension=10 9/16"; U Tube Radius=5 3/8"; Unit Height=93 1/8"; Unit Radius=33 3/16"; Weight=2630
- 2200 L 750A-QWD: BW Inlet Conn X=2 15/16"; BW Inlet NPT=2"; BW Inlet Radius=1"; BW Inlet Y=12 3/8"; BW Outlet Conn X=2 15/16"; BW Outlet NPT=2"; BW Outlet Radius=1"; BW Outlet Y=23 7/16"; BW Plumbing Total Z=22 1/16"; BW Up=13 1/16"; BW Up Radius=1"; BW X=17 13/16"; BW Z=11 1/2"; Boiler Water Flow Rate at 180F=92 GPM; Cold Water Extension=6 3/8"; Cold Water Inlet Z=5 1/8"; Cold Water NPT=2 1/2"; Cold Water Radius=1 1/4"; Control Enclosure Location=20"; Control Panel Extension=40 3/16"; Drain Extension=37 1/16"; Drain NPT=1 1/2"; Drain Radius=3/4"; Energy Extension=49 3/16"; Flat Side Distance=66 3/8"; Front Skid Extension=101 3/16"; Height to Drain=3 7/8"; Height to Energy=32 11/16"; Height to Hot Outlet=60 13/16"; Height to Relief=61 7/16"; Hot Outlet Angle=90.00°; Hot Outlet Extension=34 3/16"; Hot Outlet NPT=3"; Hot Outlet Offset Horiz=34 3/16"; Hot Outlet Offset Vert=0"; Hot Outlet Radius=1 1/2"; Rear Skid Extension=33 3/16"; Recovery Rate 40F to 140F (GPH)=1090; Relief Valve Extension=36 3/16"; Skid Length=68"; Skid Spacing=36"; U Tube Extension=10 9/16"; U Tube Radius=5 3/8"; Unit Height=81 1/8"; Unit Radius=33 3/16"; Weight=2400
- 2000 L 900A-QW: BW Inlet Conn X=2 1/2"; BW Inlet NPT=2"; BW Inlet Radius=1"; BW Inlet Y=10 3/8"; BW Outlet Conn X=2 1/2"; BW Outlet NPT=2"; BW Outlet Radius=1"; BW Outlet Y=17 9/16"; BW Plumbing Total Z=20 1/8"; BW Up=10 3/8"; BW Up Radius=1"; BW X=12 13/16"; BW Z=9 5/16"; Boiler Water Flow Rate at 180F=80 GPM; Cold Water Extension=5 5/16"; Cold Water Inlet Z=5 3/8"; Cold Water NPT=2"; Cold Water Radius=1"; Control Enclosure Location=20"; Control Panel Extension=40 3/16"; Drain Extension=37 1/16"; Drain NPT=1 1/2"; Drain Radius=3/4"; Energy Extension=49 3/16"; Flat Side Distance=66 3/8"; Front Skid Extension=101 3/16"; Height to Drain=3 7/8"; Height to Energy=32 11/16"; Height to Hot Outlet=72 13/16"; Height to Relief=73 7/16"; Hot Outlet Angle=90.00°; Hot Outlet Extension=34 3/16"; Hot Outlet NPT=3"; Hot Outlet Offset Horiz=34 3/16"; Hot Outlet Offset Vert=0"; Hot Outlet Radius=1 1/2"; Rear Skid Extension=33 3/16"; Recovery Rate 40F to 140F (GPH)=950; Relief Valve Extension=36 3/16"; Skid Length=68"; Skid Spacing=36"; U Tube Extension=10 13/16"; U Tube Radius=4 5/16"; Unit Height=93 1/8"; Unit Radius=33 3/16"; Weight=2420
- 2000 L 750A-QW: BW Inlet Conn X=2 1/2"; BW Inlet NPT=2"; BW Inlet Radius=1"; BW Inlet Y=10 3/8"; BW Outlet Conn X=2 1/2"; BW Outlet NPT=2"; BW Outlet Radius=1"; BW Outlet Y=17 9/16"; BW Plumbing Total Z=20 1/8"; BW Up=10 3/8"; BW Up Radius=1"; BW X=12 13/16"; BW Z=9 5/16"; Boiler Water Flow Rate at 180F=80 GPM; Cold Water Extension=5 5/16"; Cold Water Inlet Z=5 3/8"; Cold Water NPT=2"; Cold Water Radius=1"; Control Enclosure Location=20"; Control Panel Extension=40 3/16"; Drain Extension=37 1/16"; Drain NPT=1 1/2"; Drain Radius=3/4"; Energy Extension=49 3/16"; Flat Side Distance=66 3/8"; Front Skid Extension=101 3/16"; Height to Drain=3 7/8"; Height to Energy=32 11/16"; Height to Hot Outlet=60 13/16"; Height to Relief=61 7/16"; Hot Outlet Angle=90.00°; Hot Outlet Extension=34 3/16"; Hot Outlet NPT=3"; Hot Outlet Offset Horiz=34 3/16"; Hot Outlet Offset Vert=0"; Hot Outlet Radius=1 1/2"; Rear Skid Extension=33 3/16"; Recovery Rate 40F to 140F (GPH)=950; Relief Valve Extension=36 3/16"; Skid Length=68"; Skid Spacing=36"; U Tube Extension=10 13/16"; U Tube Radius=4 5/16"; Unit Height=81 1/8"; Unit Radius=33 3/16"; Weight=2200
- 1900 L 900A-QWD: BW Inlet Conn X=2 15/16"; BW Inlet NPT=2"; BW Inlet Radius=1"; BW Inlet Y=10 3/8"; BW Outlet Conn X=2 15/16"; BW Outlet NPT=2"; BW Outlet Radius=1"; BW Outlet Y=17 9/16"; BW Plumbing Total Z=19 7/8"; BW Up=10 13/16"; BW Up Radius=1"; BW X=13 7/8"; BW Z=9 5/16"; Boiler Water Flow Rate at 180F=80 GPM; Cold Water Extension=6 3/8"; Cold Water Inlet Z=5 1/8"; Cold Water NPT=2 1/2"; Cold Water Radius=1 1/4"; Control Enclosure Location=20"; Control Panel Extension=40 3/16"; Drain Extension=37 1/16"; Drain NPT=1 1/2"; Drain Radius=3/4"; Energy Extension=49 3/16"; Flat Side Distance=66 3/8"; Front Skid Extension=101 3/16"; Height to Drain=3 7/8"; Height to Energy=32 11/16"; Height to Hot Outlet=72 13/16"; Height to Relief=73 7/16"; Hot Outlet Angle=90.00°; Hot Outlet Extension=34 3/16"; Hot Outlet NPT=3"; Hot Outlet Offset Horiz=34 3/16"; Hot Outlet Offset Vert=0"; Hot Outlet Radius=1 1/2"; Rear Skid Extension=33 3/16"; Recovery Rate 40F to 140F (GPH)=950; Relief Valve Extension=36 3/16"; Skid Length=68"; Skid Spacing=36"; U Tube Extension=10 9/16"; U Tube Radius=5 3/8"; Unit Height=93 1/8"; Unit Radius=33 3/16"; Weight=2590
- 1900 L 750A-QWD: BW Inlet Conn X=2 15/16"; BW Inlet NPT=2"; BW Inlet Radius=1"; BW Inlet Y=10 3/8"; BW Outlet Conn X=2 15/16"; BW Outlet NPT=2"; BW Outlet Radius=1"; BW Outlet Y=17 9/16"; BW Plumbing Total Z=19 7/8"; BW Up=10 13/16"; BW Up Radius=1"; BW X=13 7/8"; BW Z=9 5/16"; Boiler Water Flow Rate at 180F=80 GPM; Cold Water Extension=6 3/8"; Cold Water Inlet Z=5 1/8"; Cold Water NPT=2 1/2"; Cold Water Radius=1 1/4"; Control Enclosure Location=20"; Control Panel Extension=40 3/16"; Drain Extension=37 1/16"; Drain NPT=1 1/2"; Drain Radius=3/4"; Energy Extension=49 3/16"; Flat Side Distance=66 3/8"; Front Skid Extension=101 3/16"; Height to Drain=3 7/8"; Height to Energy=32 11/16"; Height to Hot Outlet=60 13/16"; Height to Relief=61 7/16"; Hot Outlet Angle=90.00°; Hot Outlet Extension=34 3/16"; Hot Outlet NPT=3"; Hot Outlet Offset Horiz=34 3/16"; Hot Outlet Offset Vert=0"; Hot Outlet Radius=1 1/2"; Rear Skid Extension=33 3/16"; Recovery Rate 40F to 140F (GPH)=920; Relief Valve Extension=36 3/16"; Skid Length=68"; Skid Spacing=36"; U Tube Extension=10 9/16"; U Tube Radius=5 3/8"; Unit Height=81 1/8"; Unit Radius=33 3/16"; Weight=2360
- 1500 L 900A-QW: BW Inlet Conn X=2 1/2"; BW Inlet NPT=1 1/2"; BW Inlet Radius=3/4"; BW Inlet Y=10 3/8"; BW Outlet Conn X=2 1/2"; BW Outlet NPT=1 1/2"; BW Outlet Radius=3/4"; BW Outlet Y=17 9/16"; BW Plumbing Total Z=20 1/8"; BW Up=10 3/8"; BW Up Radius=3/4"; BW X=12 13/16"; BW Z=9 5/16"; Boiler Water Flow Rate at 180F=58 GPM; Cold Water Extension=5 5/16"; Cold Water Inlet Z=5 3/8"; Cold Water NPT=2"; Cold Water Radius=1"; Control Enclosure Location=20"; Control Panel Extension=40 3/16"; Drain Extension=37 1/16"; Drain NPT=1 1/2"; Drain Radius=3/4"; Energy Extension=49 3/16"; Flat Side Distance=66 3/8"; Front Skid Extension=101 3/16"; Height to Drain=3 7/8"; Height to Energy=32 11/16"; Height to Hot Outlet=72 13/16"; Height to Relief=73 7/16"; Hot Outlet Angle=90.00°; Hot Outlet Extension=34 3/16"; Hot Outlet NPT=3"; Hot Outlet Offset Horiz=34 3/16"; Hot Outlet Offset Vert=0"; Hot Outlet Radius=1 1/2"; Rear Skid Extension=33 3/16"; Recovery Rate 40F to 140F (GPH)=690; Relief Valve Extension=36 3/16"; Skid Length=68"; Skid Spacing=36"; U Tube Extension=10 13/16"; U Tube Radius=4 5/16"; Unit Height=93 1/8"; Unit Radius=33 3/16"; Weight=2400
- 1500 L 750A-QW: BW Inlet Conn X=2 1/2"; BW Inlet NPT=1 1/2"; BW Inlet Radius=3/4"; BW Inlet Y=10 3/8"; BW Outlet Conn X=2 1/2"; BW Outlet NPT=1 1/2"; BW Outlet Radius=3/4"; BW Outlet Y=17 9/16"; BW Plumbing Total Z=20 1/8"; BW Up=10 3/8"; BW Up Radius=3/4"; BW X=12 13/16"; BW Z=9 5/16"; Boiler Water Flow Rate at 180F=58 GPM; Cold Water Extension=5 5/16"; Cold Water Inlet Z=5 3/8"; Cold Water NPT=2"; Cold Water Radius=1"; Control Enclosure Location=20"; Control Panel Extension=40 3/16"; Drain Extension=37 1/16"; Drain NPT=1 1/2"; Drain Radius=3/4"; Energy Extension=49 3/16"; Flat Side Distance=66 3/8"; Front Skid Extension=101 3/16"; Height to Drain=3 7/8"; Height to Energy=32 11/16"; Height to Hot Outlet=60 13/16"; Height to Relief=61 7/16"; Hot Outlet Angle=90.00°; Hot Outlet Extension=34 3/16"; Hot Outlet NPT=3"; Hot Outlet Offset Horiz=34 3/16"; Hot Outlet Offset Vert=0"; Hot Outlet Radius=1 1/2"; Rear Skid Extension=33 3/16"; Recovery Rate 40F to 140F (GPH)=690; Relief Valve Extension=36 3/16"; Skid Length=68"; Skid Spacing=36"; U Tube Extension=10 13/16"; U Tube Radius=4 5/16"; Unit Height=81 1/8"; Unit Radius=33 3/16"; Weight=2180
- 1300 L 900A-QWD: BW Inlet Conn X=2 1/2"; BW Inlet NPT=1 1/2"; BW Inlet Radius=3/4"; BW Inlet Y=8 3/8"; BW Outlet Conn X=2 1/2"; BW Outlet NPT=1 1/2"; BW Outlet Radius=3/4"; BW Outlet Y=15 1/4"; BW Plumbing Total Z=19 1/4"; BW Up=8 5/8"; BW Up Radius=3/4"; BW X=11 11/16"; BW Z=8 7/16"; Boiler Water Flow Rate at 180F=53 GPM; Cold Water Extension=5 5/16"; Cold Water Inlet Z=5 3/8"; Cold Water NPT=2"; Cold Water Radius=1"; Control Enclosure Location=20"; Control Panel Extension=40 3/16"; Drain Extension=37 1/16"; Drain NPT=1 1/2"; Drain Radius=3/4"; Energy Extension=49 3/16"; Flat Side Distance=66 3/8"; Front Skid Extension=101 3/16"; Height to Drain=3 7/8"; Height to Energy=32 11/16"; Height to Hot Outlet=72 13/16"; Height to Relief=73 7/16"; Hot Outlet Angle=90.00°; Hot Outlet Extension=34 3/16"; Hot Outlet NPT=3"; Hot Outlet Offset Horiz=34 3/16"; Hot Outlet Offset Vert=0"; Hot Outlet Radius=1 1/2"; Rear Skid Extension=33 3/16"; Recovery Rate 40F to 140F (GPH)=620; Relief Valve Extension=36 3/16"; Skid Length=68"; Skid Spacing=36"; U Tube Extension=10 13/16"; U Tube Radius=4 5/16"; Unit Height=93 1/8"; Unit Radius=33 3/16"; Weight=2450
- 1300 L 750A-QWD: BW Inlet Conn X=2 1/2"; BW Inlet NPT=1 1/2"; BW Inlet Radius=3/4"; BW Inlet Y=8 3/8"; BW Outlet Conn X=2 1/2"; BW Outlet NPT=1 1/2"; BW Outlet Radius=3/4"; BW Outlet Y=15 1/4"; BW Plumbing Total Z=19 1/4"; BW Up=8 5/8"; BW Up Radius=3/4"; BW X=11 11/16"; BW Z=8 7/16"; Boiler Water Flow Rate at 180F=53 GPM; Cold Water Extension=5 5/16"; Cold Water Inlet Z=5 3/8"; Cold Water NPT=2"; Cold Water Radius=1"; Control Enclosure Location=20"; Control Panel Extension=40 3/16"; Drain Extension=37 1/16"; Drain NPT=1 1/2"; Drain Radius=3/4"; Energy Extension=49 3/16"; Flat Side Distance=66 3/8"; Front Skid Extension=101 3/16"; Height to Drain=3 7/8"; Height to Energy=32 11/16"; Height to Hot Outlet=60 13/16"; Height to Relief=61 7/16"; Hot Outlet Angle=90.00°; Hot Outlet Extension=34 3/16"; Hot Outlet NPT=3"; Hot Outlet Offset Horiz=34 3/16"; Hot Outlet Offset Vert=0"; Hot Outlet Radius=1 1/2"; Rear Skid Extension=33 3/16"; Recovery Rate 40F to 140F (GPH)=620; Relief Valve Extension=36 3/16"; Skid Length=68"; Skid Spacing=36"; U Tube Extension=10 13/16"; U Tube Radius=4 5/16"; Unit Height=81 1/8"; Unit Radius=33 3/16"; Weight=2220
- 1100 L 900A-QW: BW Inlet Conn X=1 7/8"; BW Inlet NPT=1 1/4"; BW Inlet Radius=5/8"; BW Inlet Y=8 3/8"; BW Outlet Conn X=1 7/8"; BW Outlet NPT=1 1/4"; BW Outlet Radius=5/8"; BW Outlet Y=15 1/4"; BW Plumbing Total Z=18 1/4"; BW Up=8"; BW Up Radius=5/8"; BW X=11 1/16"; BW Z=8 7/16"; Boiler Water Flow Rate at 180F=43 GPM; Cold Water Extension=4 5/16"; Cold Water Inlet Z=5 5/8"; Cold Water NPT=2"; Cold Water Radius=1"; Control Enclosure Location=20"; Control Panel Extension=40 3/16"; Drain Extension=37 1/16"; Drain NPT=1 1/2"; Drain Radius=3/4"; Energy Extension=49 3/16"; Flat Side Distance=66 3/8"; Front Skid Extension=101 3/16"; Height to Drain=3 7/8"; Height to Energy=32 11/16"; Height to Hot Outlet=72 13/16"; Height to Relief=73 7/16"; Hot Outlet Angle=90.00°; Hot Outlet Extension=34 3/16"; Hot Outlet NPT=3"; Hot Outlet Offset Horiz=34 3/16"; Hot Outlet Offset Vert=0"; Hot Outlet Radius=1 1/2"; Rear Skid Extension=33 3/16"; Recovery Rate 40F to 140F (GPH)=510; Relief Valve Extension=36 3/16"; Skid Length=68"; Skid Spacing=36"; U Tube Extension=9 13/16"; U Tube Radius=3 5/16"; Unit Height=93 1/8"; Unit Radius=33 3/16"; Weight=2323
- 1100 L 750A-QW: BW Inlet Conn X=1 7/8"; BW Inlet NPT=1 1/4"; BW Inlet Radius=5/8"; BW Inlet Y=8 3/8"; BW Outlet Conn X=1 7/8"; BW Outlet NPT=1 1/4"; BW Outlet Radius=5/8"; BW Outlet Y=15 1/4"; BW Plumbing Total Z=18 1/4"; BW Up=8"; BW Up Radius=5/8"; BW X=11 1/16"; BW Z=8 7/16"; Boiler Water Flow Rate at 180F=43 GPM; Cold Water Extension=4 5/16"; Cold Water Inlet Z=5 5/8"; Cold Water NPT=2"; Cold Water Radius=1"; Control Enclosure Location=20"; Control Panel Extension=40 3/16"; Drain Extension=37 1/16"; Drain NPT=1 1/2"; Drain Radius=3/4"; Energy Extension=49 3/16"; Flat Side Distance=66 3/8"; Front Skid Extension=101 3/16"; Height to Drain=3 7/8"; Height to Energy=32 11/16"; Height to Hot Outlet=60 13/16"; Height to Relief=61 7/16"; Hot Outlet Angle=90.00°; Hot Outlet Extension=34 3/16"; Hot Outlet NPT=3"; Hot Outlet Offset Horiz=34 3/16"; Hot Outlet Offset Vert=0"; Hot Outlet Radius=1 1/2"; Rear Skid Extension=33 3/16"; Recovery Rate 40F to 140F (GPH)=510; Relief Valve Extension=36 3/16"; Skid Length=68"; Skid Spacing=36"; U Tube Extension=9 13/16"; U Tube Radius=3 5/16"; Unit Height=81 1/8"; Unit Radius=33 3/16"; Weight=2093
- 900 L 600A-QWD: BW Inlet Conn X=2 1/2"; BW Inlet NPT=1 1/4"; BW Inlet Radius=5/8"; BW Inlet Y=6 3/4"; BW Outlet Conn X=2 1/2"; BW Outlet NPT=1 1/4"; BW Outlet Radius=5/8"; BW Outlet Y=14 1/16"; BW Plumbing Total Z=18 1/8"; BW Up=8 7/16"; BW Up Radius=5/8"; BW X=10 7/8"; BW Z=8 5/16"; Boiler Water Flow Rate at 180F=38 GPM; Cold Water Extension=5 5/16"; Cold Water Inlet Z=5 5/8"; Cold Water NPT=2"; Cold Water Radius=1"; Control Enclosure Location=20"; Control Panel Extension=34 7/8"; Drain Extension=31 3/4"; Drain NPT=1 1/2"; Drain Radius=3/4"; Energy Extension=32 7/8"; Flat Side Distance=55 3/4"; Front Skid Extension=82 3/8"; Height to Drain=1 3/4"; Height to Energy=29 15/16"; Height to Hot Outlet=69 3/8"; Height to Relief=70"; Hot Outlet Angle=90.00°; Hot Outlet Extension=28 7/8"; Hot Outlet NPT=3"; Hot Outlet Offset Horiz=28 7/8"; Hot Outlet Offset Vert=0"; Hot Outlet Radius=1 1/2"; Rear Skid Extension=27 7/8"; Recovery Rate 40F to 140F (GPH)=440; Relief Valve Extension=30 7/8"; Skid Length=54 1/2"; Skid Spacing=27"; U Tube Extension=9 13/16"; U Tube Radius=4 5/16"; Unit Height=88 5/8"; Unit Radius=27 7/8"; Weight=2000
- 900 L 500A-QWD: BW Inlet Conn X=2 1/2"; BW Inlet NPT=1 1/4"; BW Inlet Radius=5/8"; BW Inlet Y=6 3/4"; BW Outlet Conn X=2 1/2"; BW Outlet NPT=1 1/4"; BW Outlet Radius=5/8"; BW Outlet Y=14 1/16"; BW Plumbing Total Z=18 1/8"; BW Up=8 7/16"; BW Up Radius=5/8"; BW X=10 7/8"; BW Z=8 5/16"; Boiler Water Flow Rate at 180F=38 GPM; Cold Water Extension=5 5/16"; Cold Water Inlet Z=5 5/8"; Cold Water NPT=2"; Cold Water Radius=1"; Control Enclosure Location=20"; Control Panel Extension=34 7/8"; Drain Extension=31 3/4"; Drain NPT=1 1/2"; Drain Radius=3/4"; Energy Extension=32 7/8"; Flat Side Distance=55 3/4"; Front Skid Extension=82 3/8"; Height to Drain=1 3/4"; Height to Energy=29 15/16"; Height to Hot Outlet=57 3/8"; Height to Relief=58"; Hot Outlet Angle=90.00°; Hot Outlet Extension=28 7/8"; Hot Outlet NPT=3"; Hot Outlet Offset Horiz=28 7/8"; Hot Outlet Offset Vert=0"; Hot Outlet Radius=1 1/2"; Rear Skid Extension=27 7/8"; Recovery Rate 40F to 140F (GPH)=440; Relief Valve Extension=30 7/8"; Skid Length=54 1/2"; Skid Spacing=27"; U Tube Extension=9 13/16"; U Tube Radius=4 5/16"; Unit Height=76 1/16"; Unit Radius=27 7/8"; Weight=1770
- 8200 L 600A-QW: BW Inlet Conn X=4 9/16"; BW Inlet NPT=4"; BW Inlet Radius=2"; BW Inlet Y=18 11/16"; BW Outlet Conn X=4 9/16"; BW Outlet NPT=4"; BW Outlet Radius=2"; BW Outlet Y=33 11/16"; BW Plumbing Total Z=20 15/16"; BW Up=17 9/16"; BW Up Radius=2"; BW X=24 1/16"; BW Z=7 1/2"; Boiler Water Flow Rate at 180F=322 GPM; Cold Water Extension=9"; Cold Water Inlet Z=5"; Cold Water NPT=2 1/2"; Cold Water Radius=1 1/4"; Control Enclosure Location=20"; Control Panel Extension=34 7/8"; Drain Extension=31 3/4"; Drain NPT=1 1/2"; Drain Radius=3/4"; Energy Extension=32 7/8"; Flat Side Distance=55 3/4"; Front Skid Extension=82 3/8"; Height to Drain=1 3/4"; Height to Energy=29 15/16"; Height to Hot Outlet=69 3/8"; Height to Relief=70"; Hot Outlet Angle=90.00°; Hot Outlet Extension=28 7/8"; Hot Outlet NPT=3"; Hot Outlet Offset Horiz=28 7/8"; Hot Outlet Offset Vert=0"; Hot Outlet Radius=1 1/2"; Rear Skid Extension=27 7/8"; Recovery Rate 40F to 140F (GPH)=3800; Relief Valve Extension=30 7/8"; Skid Length=54 1/2"; Skid Spacing=27"; U Tube Extension=13 7/16"; U Tube Radius=8"; Unit Height=88 5/8"; Unit Radius=27 7/8"; Weight=2630
- 8200 L 500A-QW: BW Inlet Conn X=4 9/16"; BW Inlet NPT=4"; BW Inlet Radius=2"; BW Inlet Y=18 11/16"; BW Outlet Conn X=4 9/16"; BW Outlet NPT=4"; BW Outlet Radius=2"; BW Outlet Y=33 11/16"; BW Plumbing Total Z=20 15/16"; BW Up=17 9/16"; BW Up Radius=2"; BW X=24 1/16"; BW Z=7 1/2"; Boiler Water Flow Rate at 180F=322 GPM; Cold Water Extension=9"; Cold Water Inlet Z=5"; Cold Water NPT=2 1/2"; Cold Water Radius=1 1/4"; Control Enclosure Location=20"; Control Panel Extension=34 7/8"; Drain Extension=31 3/4"; Drain NPT=1 1/2"; Drain Radius=3/4"; Energy Extension=32 7/8"; Flat Side Distance=55 3/4"; Front Skid Extension=82 3/8"; Height to Drain=1 3/4"; Height to Energy=29 15/16"; Height to Hot Outlet=57 3/8"; Height to Relief=58"; Hot Outlet Angle=90.00°; Hot Outlet Extension=28 7/8"; Hot Outlet NPT=3"; Hot Outlet Offset Horiz=28 7/8"; Hot Outlet Offset Vert=0"; Hot Outlet Radius=1 1/2"; Rear Skid Extension=27 7/8"; Recovery Rate 40F to 140F (GPH)=3800; Relief Valve Extension=30 7/8"; Skid Length=54 1/2"; Skid Spacing=27"; U Tube Extension=13 7/16"; U Tube Radius=8"; Unit Height=76 1/16"; Unit Radius=27 7/8"; Weight=2400
- 800 L 600A-QW: BW Inlet Conn X=1 7/8"; BW Inlet NPT=1 1/4"; BW Inlet Radius=5/8"; BW Inlet Y=6 3/4"; BW Outlet Conn X=1 7/8"; BW Outlet NPT=1 1/4"; BW Outlet Radius=5/8"; BW Outlet Y=14 1/16"; BW Plumbing Total Z=18 1/8"; BW Up=8 7/16"; BW Up Radius=5/8"; BW X=10 7/8"; BW Z=8 5/16"; Boiler Water Flow Rate at 180F=32 GPM; Cold Water Extension=4 5/16"; Cold Water Inlet Z=5 5/8"; Cold Water NPT=2"; Cold Water Radius=1"; Control Enclosure Location=20"; Control Panel Extension=34 7/8"; Drain Extension=31 3/4"; Drain NPT=1 1/2"; Drain Radius=3/4"; Energy Extension=32 7/8"; Flat Side Distance=55 3/4"; Front Skid Extension=82 3/8"; Height to Drain=1 3/4"; Height to Energy=29 15/16"; Height to Hot Outlet=69 3/8"; Height to Relief=70"; Hot Outlet Angle=90.00°; Hot Outlet Extension=28 7/8"; Hot Outlet NPT=3"; Hot Outlet Offset Horiz=28 7/8"; Hot Outlet Offset Vert=0"; Hot Outlet Radius=1 1/2"; Rear Skid Extension=27 7/8"; Recovery Rate 40F to 140F (GPH)=380; Relief Valve Extension=30 7/8"; Skid Length=54 1/2"; Skid Spacing=27"; U Tube Extension=9 13/16"; U Tube Radius=3 5/16"; Unit Height=88 5/8"; Unit Radius=27 7/8"; Weight=1950
- 800 L 500A-QW: BW Inlet Conn X=1 7/8"; BW Inlet NPT=1 1/4"; BW Inlet Radius=5/8"; BW Inlet Y=6 3/4"; BW Outlet Conn X=1 7/8"; BW Outlet NPT=1 1/4"; BW Outlet Radius=5/8"; BW Outlet Y=14 1/16"; BW Plumbing Total Z=18 1/8"; BW Up=8 7/16"; BW Up Radius=5/8"; BW X=10 7/8"; BW Z=8 5/16"; Boiler Water Flow Rate at 180F=32 GPM; Cold Water Extension=4 5/16"; Cold Water Inlet Z=5 5/8"; Cold Water NPT=2"; Cold Water Radius=1"; Control Enclosure Location=20"; Control Panel Extension=34 7/8"; Drain Extension=31 3/4"; Drain NPT=1 1/2"; Drain Radius=3/4"; Energy Extension=32 7/8"; Flat Side Distance=55 3/4"; Front Skid Extension=82 3/8"; Height to Drain=1 3/4"; Height to Energy=29 15/16"; Height to Hot Outlet=57 3/8"; Height to Relief=58"; Hot Outlet Angle=90.00°; Hot Outlet Extension=28 7/8"; Hot Outlet NPT=3"; Hot Outlet Offset Horiz=28 7/8"; Hot Outlet Offset Vert=0"; Hot Outlet Radius=1 1/2"; Rear Skid Extension=27 7/8"; Recovery Rate 40F to 140F (GPH)=380; Relief Valve Extension=30 7/8"; Skid Length=54 1/2"; Skid Spacing=27"; U Tube Extension=9 13/16"; U Tube Radius=3 5/16"; Unit Height=76 1/16"; Unit Radius=27 7/8"; Weight=1720
- 700 L 600A-QWD: BW Inlet Conn X=2 1/2"; BW Inlet NPT=1 1/4"; BW Inlet Radius=5/8"; BW Inlet Y=6 3/4"; BW Outlet Conn X=2 1/2"; BW Outlet NPT=1 1/4"; BW Outlet Radius=5/8"; BW Outlet Y=14 1/16"; BW Plumbing Total Z=18 1/8"; BW Up=8 7/16"; BW Up Radius=5/8"; BW X=10 7/8"; BW Z=8 5/16"; Boiler Water Flow Rate at 180F=29 GPM; Cold Water Extension=5 5/16"; Cold Water Inlet Z=5 5/8"; Cold Water NPT=2"; Cold Water Radius=1"; Control Enclosure Location=20"; Control Panel Extension=34 7/8"; Drain Extension=31 3/4"; Drain NPT=1 1/2"; Drain Radius=3/4"; Energy Extension=32 7/8"; Flat Side Distance=55 3/4"; Front Skid Extension=82 3/8"; Height to Drain=1 3/4"; Height to Energy=29 15/16"; Height to Hot Outlet=69 3/8"; Height to Relief=70"; Hot Outlet Angle=90.00°; Hot Outlet Extension=28 7/8"; Hot Outlet NPT=3"; Hot Outlet Offset Horiz=28 7/8"; Hot Outlet Offset Vert=0"; Hot Outlet Radius=1 1/2"; Rear Skid Extension=27 7/8"; Recovery Rate 40F to 140F (GPH)=340; Relief Valve Extension=30 7/8"; Skid Length=54 1/2"; Skid Spacing=27"; U Tube Extension=9 13/16"; U Tube Radius=4 5/16"; Unit Height=88 5/8"; Unit Radius=27 7/8"; Weight=1960
- 700 L 500A-QWD: BW Inlet Conn X=2 1/2"; BW Inlet NPT=1 1/4"; BW Inlet Radius=5/8"; BW Inlet Y=6 3/4"; BW Outlet Conn X=2 1/2"; BW Outlet NPT=1 1/4"; BW Outlet Radius=5/8"; BW Outlet Y=14 1/16"; BW Plumbing Total Z=18 1/8"; BW Up=8 7/16"; BW Up Radius=5/8"; BW X=10 7/8"; BW Z=8 5/16"; Boiler Water Flow Rate at 180F=29 GPM; Cold Water Extension=5 5/16"; Cold Water Inlet Z=5 5/8"; Cold Water NPT=2"; Cold Water Radius=1"; Control Enclosure Location=20"; Control Panel Extension=34 7/8"; Drain Extension=31 3/4"; Drain NPT=1 1/2"; Drain Radius=3/4"; Energy Extension=32 7/8"; Flat Side Distance=55 3/4"; Front Skid Extension=82 3/8"; Height to Drain=1 3/4"; Height to Energy=29 15/16"; Height to Hot Outlet=57 3/8"; Height to Relief=58"; Hot Outlet Angle=90.00°; Hot Outlet Extension=28 7/8"; Hot Outlet NPT=3"; Hot Outlet Offset Horiz=28 7/8"; Hot Outlet Offset Vert=0"; Hot Outlet Radius=1 1/2"; Rear Skid Extension=27 7/8"; Recovery Rate 40F to 140F (GPH)=340; Relief Valve Extension=30 7/8"; Skid Length=54 1/2"; Skid Spacing=27"; U Tube Extension=9 13/16"; U Tube Radius=4 5/16"; Unit Height=76 1/16"; Unit Radius=27 7/8"; Weight=1740
- 6900 L 600A-QWD: BW Inlet Conn X=4 9/16"; BW Inlet NPT=4"; BW Inlet Radius=2"; BW Inlet Y=18 11/16"; BW Outlet Conn X=4 9/16"; BW Outlet NPT=4"; BW Outlet Radius=2"; BW Outlet Y=33 11/16"; BW Plumbing Total Z=20 15/16"; BW Up=17 9/16"; BW Up Radius=2"; BW X=24 1/16"; BW Z=7 1/2"; Boiler Water Flow Rate at 180F=286 GPM; Cold Water Extension=9"; Cold Water Inlet Z=5"; Cold Water NPT=2 1/2"; Cold Water Radius=1 1/4"; Control Enclosure Location=20"; Control Panel Extension=34 7/8"; Drain Extension=31 3/4"; Drain NPT=1 1/2"; Drain Radius=3/4"; Energy Extension=32 7/8"; Flat Side Distance=55 3/4"; Front Skid Extension=82 3/8"; Height to Drain=1 3/4"; Height to Energy=29 15/16"; Height to Hot Outlet=69 3/8"; Height to Relief=70"; Hot Outlet Angle=90.00°; Hot Outlet Extension=28 7/8"; Hot Outlet NPT=3"; Hot Outlet Offset Horiz=28 7/8"; Hot Outlet Offset Vert=0"; Hot Outlet Radius=1 1/2"; Rear Skid Extension=27 7/8"; Recovery Rate 40F to 140F (GPH)=3370; Relief Valve Extension=30 7/8"; Skid Length=54 1/2"; Skid Spacing=27"; U Tube Extension=13 7/16"; U Tube Radius=8"; Unit Height=88 5/8"; Unit Radius=27 7/8"; Weight=2930
- 6900 L 500A-QWD: BW Inlet Conn X=4 9/16"; BW Inlet NPT=4"; BW Inlet Radius=2"; BW Inlet Y=18 11/16"; BW Outlet Conn X=4 9/16"; BW Outlet NPT=4"; BW Outlet Radius=2"; BW Outlet Y=33 11/16"; BW Plumbing Total Z=20 15/16"; BW Up=17 9/16"; BW Up Radius=2"; BW X=24 1/16"; BW Z=7 1/2"; Boiler Water Flow Rate at 180F=286 GPM; Cold Water Extension=9"; Cold Water Inlet Z=5"; Cold Water NPT=2 1/2"; Cold Water Radius=1 1/4"; Control Enclosure Location=20"; Control Panel Extension=34 7/8"; Drain Extension=31 3/4"; Drain NPT=1 1/2"; Drain Radius=3/4"; Energy Extension=32 7/8"; Flat Side Distance=55 3/4"; Front Skid Extension=82 3/8"; Height to Drain=1 3/4"; Height to Energy=29 15/16"; Height to Hot Outlet=57 3/8"; Height to Relief=58"; Hot Outlet Angle=90.00°; Hot Outlet Extension=28 7/8"; Hot Outlet NPT=3"; Hot Outlet Offset Horiz=28 7/8"; Hot Outlet Offset Vert=0"; Hot Outlet Radius=1 1/2"; Rear Skid Extension=27 7/8"; Recovery Rate 40F to 140F (GPH)=3370; Relief Valve Extension=30 7/8"; Skid Length=54 1/2"; Skid Spacing=27"; U Tube Extension=13 7/16"; U Tube Radius=8"; Unit Height=76 1/16"; Unit Radius=27 7/8"; Weight=2700
- 6300 L 600A-QW: BW Inlet Conn X=4"; BW Inlet NPT=4"; BW Inlet Radius=2"; BW Inlet Y=18 11/16"; BW Outlet Conn X=4"; BW Outlet NPT=4"; BW Outlet Radius=2"; BW Outlet Y=33 11/16"; BW Plumbing Total Z=21 3/16"; BW Up=17"; BW Up Radius=2"; BW X=23 1/2"; BW Z=7 1/2"; Boiler Water Flow Rate at 180F=251 GPM; Cold Water Extension=8"; Cold Water Inlet Z=4 1/2"; Cold Water NPT=2 1/2"; Cold Water Radius=1 1/4"; Control Enclosure Location=20"; Control Panel Extension=34 7/8"; Drain Extension=31 3/4"; Drain NPT=1 1/2"; Drain Radius=3/4"; Energy Extension=32 7/8"; Flat Side Distance=55 3/4"; Front Skid Extension=82 3/8"; Height to Drain=1 3/4"; Height to Energy=29 15/16"; Height to Hot Outlet=69 3/8"; Height to Relief=70"; Hot Outlet Angle=90.00°; Hot Outlet Extension=28 7/8"; Hot Outlet NPT=3"; Hot Outlet Offset Horiz=28 7/8"; Hot Outlet Offset Vert=0"; Hot Outlet Radius=1 1/2"; Rear Skid Extension=27 7/8"; Recovery Rate 40F to 140F (GPH)=2960; Relief Valve Extension=30 7/8"; Skid Length=54 1/2"; Skid Spacing=27"; U Tube Extension=13 11/16"; U Tube Radius=7"; Unit Height=88 5/8"; Unit Radius=27 7/8"; Weight=2460
- 6300 L 500A-QW: BW Inlet Conn X=4"; BW Inlet NPT=4"; BW Inlet Radius=2"; BW Inlet Y=18 11/16"; BW Outlet Conn X=4"; BW Outlet NPT=4"; BW Outlet Radius=2"; BW Outlet Y=33 11/16"; BW Plumbing Total Z=21 3/16"; BW Up=17"; BW Up Radius=2"; BW X=23 1/2"; BW Z=7 1/2"; Boiler Water Flow Rate at 180F=251 GPM; Cold Water Extension=8"; Cold Water Inlet Z=4 1/2"; Cold Water NPT=2 1/2"; Cold Water Radius=1 1/4"; Control Enclosure Location=20"; Control Panel Extension=34 7/8"; Drain Extension=31 3/4"; Drain NPT=1 1/2"; Drain Radius=3/4"; Energy Extension=32 7/8"; Flat Side Distance=55 3/4"; Front Skid Extension=82 3/8"; Height to Drain=1 3/4"; Height to Energy=29 15/16"; Height to Hot Outlet=57 3/8"; Height to Relief=58"; Hot Outlet Angle=90.00°; Hot Outlet Extension=28 7/8"; Hot Outlet NPT=3"; Hot Outlet Offset Horiz=28 7/8"; Hot Outlet Offset Vert=0"; Hot Outlet Radius=1 1/2"; Rear Skid Extension=27 7/8"; Recovery Rate 40F to 140F (GPH)=2960; Relief Valve Extension=30 7/8"; Skid Length=54 1/2"; Skid Spacing=27"; U Tube Extension=13 11/16"; U Tube Radius=7"; Unit Height=76 1/16"; Unit Radius=27 7/8"; Weight=2240
- 6100 L 600A-QWD: BW Inlet Conn X=4 9/16"; BW Inlet NPT=4"; BW Inlet Radius=2"; BW Inlet Y=18 11/16"; BW Outlet Conn X=4 9/16"; BW Outlet NPT=4"; BW Outlet Radius=2"; BW Outlet Y=33 11/16"; BW Plumbing Total Z=20 15/16"; BW Up=17 9/16"; BW Up Radius=2"; BW X=24 1/16"; BW Z=7 1/2"; Boiler Water Flow Rate at 180F=249 GPM; Cold Water Extension=9"; Cold Water Inlet Z=5"; Cold Water NPT=2 1/2"; Cold Water Radius=1 1/4"; Control Enclosure Location=20"; Control Panel Extension=34 7/8"; Drain Extension=31 3/4"; Drain NPT=1 1/2"; Drain Radius=3/4"; Energy Extension=32 7/8"; Flat Side Distance=55 3/4"; Front Skid Extension=82 3/8"; Height to Drain=1 3/4"; Height to Energy=29 15/16"; Height to Hot Outlet=69 3/8"; Height to Relief=70"; Hot Outlet Angle=90.00°; Hot Outlet Extension=28 7/8"; Hot Outlet NPT=3"; Hot Outlet Offset Horiz=28 7/8"; Hot Outlet Offset Vert=0"; Hot Outlet Radius=1 1/2"; Rear Skid Extension=27 7/8"; Recovery Rate 40F to 140F (GPH)=2930; Relief Valve Extension=30 7/8"; Skid Length=54 1/2"; Skid Spacing=27"; U Tube Extension=13 7/16"; U Tube Radius=8"; Unit Height=88 5/8"; Unit Radius=27 7/8"; Weight=2850
- 6100 L 500A-QWD: BW Inlet Conn X=4 9/16"; BW Inlet NPT=4"; BW Inlet Radius=2"; BW Inlet Y=18 11/16"; BW Outlet Conn X=4 9/16"; BW Outlet NPT=4"; BW Outlet Radius=2"; BW Outlet Y=33 11/16"; BW Plumbing Total Z=20 15/16"; BW Up=17 9/16"; BW Up Radius=2"; BW X=24 1/16"; BW Z=7 1/2"; Boiler Water Flow Rate at 180F=249 GPM; Cold Water Extension=9"; Cold Water Inlet Z=5"; Cold Water NPT=2 1/2"; Cold Water Radius=1 1/4"; Control Enclosure Location=20"; Control Panel Extension=34 7/8"; Drain Extension=31 3/4"; Drain NPT=1 1/2"; Drain Radius=3/4"; Energy Extension=32 7/8"; Flat Side Distance=55 3/4"; Front Skid Extension=82 3/8"; Height to Drain=1 3/4"; Height to Energy=29 15/16"; Height to Hot Outlet=57 3/8"; Height to Relief=58"; Hot Outlet Angle=90.00°; Hot Outlet Extension=28 7/8"; Hot Outlet NPT=3"; Hot Outlet Offset Horiz=28 7/8"; Hot Outlet Offset Vert=0"; Hot Outlet Radius=1 1/2"; Rear Skid Extension=27 7/8"; Recovery Rate 40F to 140F (GPH)=2930; Relief Valve Extension=30 7/8"; Skid Length=54 1/2"; Skid Spacing=27"; U Tube Extension=13 7/16"; U Tube Radius=8"; Unit Height=76 1/16"; Unit Radius=27 7/8"; Weight=2630
- 600 L 600A-QW: BW Inlet Conn X=1 5/16"; BW Inlet NPT=1"; BW Inlet Radius=1/2"; BW Inlet Y=5 1/2"; BW Outlet Conn X=1 5/16"; BW Outlet NPT=1"; BW Outlet Radius=1/2"; BW Outlet Y=11 3/16"; BW Plumbing Total Z=15 1/2"; BW Up=5 13/16"; BW Up Radius=1/2"; BW X=7 15/16"; BW Z=6 1/16"; Boiler Water Flow Rate at 180F=23 GPM; Cold Water Extension=3 1/4"; Cold Water Inlet Z=5 5/8"; Cold Water NPT=2"; Cold Water Radius=1"; Control Enclosure Location=20"; Control Panel Extension=34 7/8"; Drain Extension=31 3/4"; Drain NPT=1 1/2"; Drain Radius=3/4"; Energy Extension=32 7/8"; Flat Side Distance=55 3/4"; Front Skid Extension=82 3/8"; Height to Drain=1 3/4"; Height to Energy=29 15/16"; Height to Hot Outlet=69 3/8"; Height to Relief=70"; Hot Outlet Angle=90.00°; Hot Outlet Extension=28 7/8"; Hot Outlet NPT=3"; Hot Outlet Offset Horiz=28 7/8"; Hot Outlet Offset Vert=0"; Hot Outlet Radius=1 1/2"; Rear Skid Extension=27 7/8"; Recovery Rate 40F to 140F (GPH)=270; Relief Valve Extension=30 7/8"; Skid Length=54 1/2"; Skid Spacing=27"; U Tube Extension=9 7/16"; U Tube Radius=2 1/4"; Unit Height=88 5/8"; Unit Radius=27 7/8"; Weight=1900
- 600 L 500A-QW: BW Inlet Conn X=1 5/16"; BW Inlet NPT=1"; BW Inlet Radius=1/2"; BW Inlet Y=5 1/2"; BW Outlet Conn X=1 5/16"; BW Outlet NPT=1"; BW Outlet Radius=1/2"; BW Outlet Y=11 3/16"; BW Plumbing Total Z=15 1/2"; BW Up=5 13/16"; BW Up Radius=1/2"; BW X=7 15/16"; BW Z=6 1/16"; Boiler Water Flow Rate at 180F=23 GPM; Cold Water Extension=3 1/4"; Cold Water Inlet Z=5 5/8"; Cold Water NPT=2"; Cold Water Radius=1"; Control Enclosure Location=20"; Control Panel Extension=34 7/8"; Drain Extension=31 3/4"; Drain NPT=1 1/2"; Drain Radius=3/4"; Energy Extension=32 7/8"; Flat Side Distance=55 3/4"; Front Skid Extension=82 3/8"; Height to Drain=1 3/4"; Height to Energy=29 15/16"; Height to Hot Outlet=57 3/8"; Height to Relief=58"; Hot Outlet Angle=90.00°; Hot Outlet Extension=28 7/8"; Hot Outlet NPT=3"; Hot Outlet Offset Horiz=28 7/8"; Hot Outlet Offset Vert=0"; Hot Outlet Radius=1 1/2"; Rear Skid Extension=27 7/8"; Recovery Rate 40F to 140F (GPH)=270; Relief Valve Extension=30 7/8"; Skid Length=54 1/2"; Skid Spacing=27"; U Tube Extension=9 7/16"; U Tube Radius=2 1/4"; Unit Height=76 1/16"; Unit Radius=27 7/8"; Weight=1680
- 5400 L 600A-QWD: BW Inlet Conn X=4"; BW Inlet NPT=4"; BW Inlet Radius=2"; BW Inlet Y=18 11/16"; BW Outlet Conn X=4"; BW Outlet NPT=4"; BW Outlet Radius=2"; BW Outlet Y=33 11/16"; BW Plumbing Total Z=21 3/16"; BW Up=17"; BW Up Radius=2"; BW X=23 1/2"; BW Z=7 1/2"; Boiler Water Flow Rate at 180F=222 GPM; Cold Water Extension=8"; Cold Water Inlet Z=4 1/2"; Cold Water NPT=2 1/2"; Cold Water Radius=1 1/4"; Control Enclosure Location=20"; Control Panel Extension=34 7/8"; Drain Extension=31 3/4"; Drain NPT=1 1/2"; Drain Radius=3/4"; Energy Extension=32 7/8"; Flat Side Distance=55 3/4"; Front Skid Extension=82 3/8"; Height to Drain=1 3/4"; Height to Energy=29 15/16"; Height to Hot Outlet=69 3/8"; Height to Relief=70"; Hot Outlet Angle=90.00°; Hot Outlet Extension=28 7/8"; Hot Outlet NPT=3"; Hot Outlet Offset Horiz=28 7/8"; Hot Outlet Offset Vert=0"; Hot Outlet Radius=1 1/2"; Rear Skid Extension=27 7/8"; Recovery Rate 40F to 140F (GPH)=2620; Relief Valve Extension=30 7/8"; Skid Length=54 1/2"; Skid Spacing=27"; U Tube Extension=13 11/16"; U Tube Radius=7"; Unit Height=88 5/8"; Unit Radius=27 7/8"; Weight=2690
- 5400 L 500A-QWD: BW Inlet Conn X=4"; BW Inlet NPT=4"; BW Inlet Radius=2"; BW Inlet Y=18 11/16"; BW Outlet Conn X=4"; BW Outlet NPT=4"; BW Outlet Radius=2"; BW Outlet Y=33 11/16"; BW Plumbing Total Z=21 3/16"; BW Up=17"; BW Up Radius=2"; BW X=23 1/2"; BW Z=7 1/2"; Boiler Water Flow Rate at 180F=222 GPM; Cold Water Extension=8"; Cold Water Inlet Z=4 1/2"; Cold Water NPT=2 1/2"; Cold Water Radius=1 1/4"; Control Enclosure Location=20"; Control Panel Extension=34 7/8"; Drain Extension=31 3/4"; Drain NPT=1 1/2"; Drain Radius=3/4"; Energy Extension=32 7/8"; Flat Side Distance=55 3/4"; Front Skid Extension=82 3/8"; Height to Drain=1 3/4"; Height to Energy=29 15/16"; Height to Hot Outlet=57 3/8"; Height to Relief=58"; Hot Outlet Angle=90.00°; Hot Outlet Extension=28 7/8"; Hot Outlet NPT=3"; Hot Outlet Offset Horiz=28 7/8"; Hot Outlet Offset Vert=0"; Hot Outlet Radius=1 1/2"; Rear Skid Extension=27 7/8"; Recovery Rate 40F to 140F (GPH)=2620; Relief Valve Extension=30 7/8"; Skid Length=54 1/2"; Skid Spacing=27"; U Tube Extension=13 11/16"; U Tube Radius=7"; Unit Height=76 1/16"; Unit Radius=27 7/8"; Weight=2470
- 500 L 600A-QWD: BW Inlet Conn X=1 5/16"; BW Inlet NPT=1"; BW Inlet Radius=1/2"; BW Inlet Y=5 1/2"; BW Outlet Conn X=1 5/16"; BW Outlet NPT=1"; BW Outlet Radius=1/2"; BW Outlet Y=11 3/16"; BW Plumbing Total Z=15 1/2"; BW Up=5 13/16"; BW Up Radius=1/2"; BW X=7 15/16"; BW Z=6 1/16"; Boiler Water Flow Rate at 180F=20 GPM; Cold Water Extension=3 1/4"; Cold Water Inlet Z=5 5/8"; Cold Water NPT=2"; Cold Water Radius=1"; Control Enclosure Location=20"; Control Panel Extension=34 7/8"; Drain Extension=31 3/4"; Drain NPT=1 1/2"; Drain Radius=3/4"; Energy Extension=32 7/8"; Flat Side Distance=55 3/4"; Front Skid Extension=82 3/8"; Height to Drain=1 3/4"; Height to Energy=29 15/16"; Height to Hot Outlet=69 3/8"; Height to Relief=70"; Hot Outlet Angle=90.00°; Hot Outlet Extension=28 7/8"; Hot Outlet NPT=3"; Hot Outlet Offset Horiz=28 7/8"; Hot Outlet Offset Vert=0"; Hot Outlet Radius=1 1/2"; Rear Skid Extension=27 7/8"; Recovery Rate 40F to 140F (GPH)=240; Relief Valve Extension=30 7/8"; Skid Length=54 1/2"; Skid Spacing=27"; U Tube Extension=9 7/16"; U Tube Radius=2 1/4"; Unit Height=88 5/8"; Unit Radius=27 7/8"; Weight=1920
- 500 L 500A-QWD: BW Inlet Conn X=1 5/16"; BW Inlet NPT=1"; BW Inlet Radius=1/2"; BW Inlet Y=5 1/2"; BW Outlet Conn X=1 5/16"; BW Outlet NPT=1"; BW Outlet Radius=1/2"; BW Outlet Y=11 3/16"; BW Plumbing Total Z=15 1/2"; BW Up=5 13/16"; BW Up Radius=1/2"; BW X=7 15/16"; BW Z=6 1/16"; Boiler Water Flow Rate at 180F=20 GPM; Cold Water Extension=3 1/4"; Cold Water Inlet Z=5 5/8"; Cold Water NPT=2"; Cold Water Radius=1"; Control Enclosure Location=20"; Control Panel Extension=34 7/8"; Drain Extension=31 3/4"; Drain NPT=1 1/2"; Drain Radius=3/4"; Energy Extension=32 7/8"; Flat Side Distance=55 3/4"; Front Skid Extension=82 3/8"; Height to Drain=1 3/4"; Height to Energy=29 15/16"; Height to Hot Outlet=57 3/8"; Height to Relief=58"; Hot Outlet Angle=90.00°; Hot Outlet Extension=28 7/8"; Hot Outlet NPT=3"; Hot Outlet Offset Horiz=28 7/8"; Hot Outlet Offset Vert=0"; Hot Outlet Radius=1 1/2"; Rear Skid Extension=27 7/8"; Recovery Rate 40F to 140F (GPH)=240; Relief Valve Extension=30 7/8"; Skid Length=54 1/2"; Skid Spacing=27"; U Tube Extension=9 7/16"; U Tube Radius=2 1/4"; Unit Height=76 1/16"; Unit Radius=27 7/8"; Weight=1690
- 4500 L 600A-QW: BW Inlet Conn X=3 13/16"; BW Inlet NPT=3"; BW Inlet Radius=1 1/2"; BW Inlet Y=18 11/16"; BW Outlet Conn X=3 13/16"; BW Outlet NPT=3"; BW Outlet Radius=1 1/2"; BW Outlet Y=33 11/16"; BW Plumbing Total Z=18 9/16"; BW Up=16 13/16"; BW Up Radius=1 1/2"; BW X=23 5/16"; BW Z=7 1/2"; Boiler Water Flow Rate at 180F=203 GPM; Cold Water Extension=7 3/8"; Cold Water Inlet Z=5"; Cold Water NPT=2 1/2"; Cold Water Radius=1 1/4"; Control Enclosure Location=20"; Control Panel Extension=34 7/8"; Drain Extension=31 3/4"; Drain NPT=1 1/2"; Drain Radius=3/4"; Energy Extension=32 7/8"; Flat Side Distance=55 3/4"; Front Skid Extension=82 3/8"; Height to Drain=1 3/4"; Height to Energy=29 15/16"; Height to Hot Outlet=69 3/8"; Height to Relief=70"; Hot Outlet Angle=90.00°; Hot Outlet Extension=28 7/8"; Hot Outlet NPT=3"; Hot Outlet Offset Horiz=28 7/8"; Hot Outlet Offset Vert=0"; Hot Outlet Radius=1 1/2"; Rear Skid Extension=27 7/8"; Recovery Rate 40F to 140F (GPH)=2390; Relief Valve Extension=30 7/8"; Skid Length=54 1/2"; Skid Spacing=27"; U Tube Extension=11 1/16"; U Tube Radius=6 3/8"; Unit Height=88 5/8"; Unit Radius=27 7/8"; Weight=2370
- 4500 L 500A-QW: BW Inlet Conn X=3 13/16"; BW Inlet NPT=3"; BW Inlet Radius=1 1/2"; BW Inlet Y=18 11/16"; BW Outlet Conn X=3 13/16"; BW Outlet NPT=3"; BW Outlet Radius=1 1/2"; BW Outlet Y=33 11/16"; BW Plumbing Total Z=18 9/16"; BW Up=16 13/16"; BW Up Radius=1 1/2"; BW X=23 5/16"; BW Z=7 1/2"; Boiler Water Flow Rate at 180F=203 GPM; Cold Water Extension=7 3/8"; Cold Water Inlet Z=5"; Cold Water NPT=2 1/2"; Cold Water Radius=1 1/4"; Control Enclosure Location=20"; Control Panel Extension=34 7/8"; Drain Extension=31 3/4"; Drain NPT=1 1/2"; Drain Radius=3/4"; Energy Extension=32 7/8"; Flat Side Distance=55 3/4"; Front Skid Extension=82 3/8"; Height to Drain=1 3/4"; Height to Energy=29 15/16"; Height to Hot Outlet=57 3/8"; Height to Relief=58"; Hot Outlet Angle=90.00°; Hot Outlet Extension=28 7/8"; Hot Outlet NPT=3"; Hot Outlet Offset Horiz=28 7/8"; Hot Outlet Offset Vert=0"; Hot Outlet Radius=1 1/2"; Rear Skid Extension=27 7/8"; Recovery Rate 40F to 140F (GPH)=2390; Relief Valve Extension=30 7/8"; Skid Length=54 1/2"; Skid Spacing=27"; U Tube Extension=11 1/16"; U Tube Radius=6 3/8"; Unit Height=76 1/16"; Unit Radius=27 7/8"; Weight=2140
- 4300 L 600A-QW: BW Inlet Conn X=3 13/16"; BW Inlet NPT=3"; BW Inlet Radius=1 1/2"; BW Inlet Y=18 11/16"; BW Outlet Conn X=3 13/16"; BW Outlet NPT=3"; BW Outlet Radius=1 1/2"; BW Outlet Y=33 11/16"; BW Plumbing Total Z=18 9/16"; BW Up=16 13/16"; BW Up Radius=1 1/2"; BW X=23 5/16"; BW Z=7 1/2"; Boiler Water Flow Rate at 180F=179 GPM; Cold Water Extension=7 3/8"; Cold Water Inlet Z=5"; Cold Water NPT=2 1/2"; Cold Water Radius=1 1/4"; Control Enclosure Location=20"; Control Panel Extension=34 7/8"; Drain Extension=31 3/4"; Drain NPT=1 1/2"; Drain Radius=3/4"; Energy Extension=32 7/8"; Flat Side Distance=55 3/4"; Front Skid Extension=82 3/8"; Height to Drain=1 3/4"; Height to Energy=29 15/16"; Height to Hot Outlet=69 3/8"; Height to Relief=70"; Hot Outlet Angle=90.00°; Hot Outlet Extension=28 7/8"; Hot Outlet NPT=3"; Hot Outlet Offset Horiz=28 7/8"; Hot Outlet Offset Vert=0"; Hot Outlet Radius=1 1/2"; Rear Skid Extension=27 7/8"; Recovery Rate 40F to 140F (GPH)=2110; Relief Valve Extension=30 7/8"; Skid Length=54 1/2"; Skid Spacing=27"; U Tube Extension=11 1/16"; U Tube Radius=6 3/8"; Unit Height=88 5/8"; Unit Radius=27 7/8"; Weight=2350
- 4300 L 500A-QW: BW Inlet Conn X=3 13/16"; BW Inlet NPT=3"; BW Inlet Radius=1 1/2"; BW Inlet Y=18 11/16"; BW Outlet Conn X=3 13/16"; BW Outlet NPT=3"; BW Outlet Radius=1 1/2"; BW Outlet Y=33 11/16"; BW Plumbing Total Z=18 9/16"; BW Up=16 13/16"; BW Up Radius=1 1/2"; BW X=23 5/16"; BW Z=7 1/2"; Boiler Water Flow Rate at 180F=179 GPM; Cold Water Extension=7 3/8"; Cold Water Inlet Z=5"; Cold Water NPT=2 1/2"; Cold Water Radius=1 1/4"; Control Enclosure Location=20"; Control Panel Extension=34 7/8"; Drain Extension=31 3/4"; Drain NPT=1 1/2"; Drain Radius=3/4"; Energy Extension=32 7/8"; Flat Side Distance=55 3/4"; Front Skid Extension=82 3/8"; Height to Drain=1 3/4"; Height to Energy=29 15/16"; Height to Hot Outlet=57 3/8"; Height to Relief=58"; Hot Outlet Angle=90.00°; Hot Outlet Extension=28 7/8"; Hot Outlet NPT=3"; Hot Outlet Offset Horiz=28 7/8"; Hot Outlet Offset Vert=0"; Hot Outlet Radius=1 1/2"; Rear Skid Extension=27 7/8"; Recovery Rate 40F to 140F (GPH)=2110; Relief Valve Extension=30 7/8"; Skid Length=54 1/2"; Skid Spacing=27"; U Tube Extension=11 1/16"; U Tube Radius=6 3/8"; Unit Height=76 1/16"; Unit Radius=27 7/8"; Weight=2120
- 4200 L 600A-QWD: BW Inlet Conn X=3 13/16"; BW Inlet NPT=3"; BW Inlet Radius=1 1/2"; BW Inlet Y=18 11/16"; BW Outlet Conn X=3 13/16"; BW Outlet NPT=3"; BW Outlet Radius=1 1/2"; BW Outlet Y=33 11/16"; BW Plumbing Total Z=18 9/16"; BW Up=16 13/16"; BW Up Radius=1 1/2"; BW X=23 5/16"; BW Z=7 1/2"; Boiler Water Flow Rate at 180F=179 GPM; Cold Water Extension=7 3/8"; Cold Water Inlet Z=5"; Cold Water NPT=2 1/2"; Cold Water Radius=1 1/4"; Control Enclosure Location=20"; Control Panel Extension=34 7/8"; Drain Extension=31 3/4"; Drain NPT=1 1/2"; Drain Radius=3/4"; Energy Extension=32 7/8"; Flat Side Distance=55 3/4"; Front Skid Extension=82 3/8"; Height to Drain=1 3/4"; Height to Energy=29 15/16"; Height to Hot Outlet=69 3/8"; Height to Relief=70"; Hot Outlet Angle=90.00°; Hot Outlet Extension=28 7/8"; Hot Outlet NPT=3"; Hot Outlet Offset Horiz=28 7/8"; Hot Outlet Offset Vert=0"; Hot Outlet Radius=1 1/2"; Rear Skid Extension=27 7/8"; Recovery Rate 40F to 140F (GPH)=2100; Relief Valve Extension=30 7/8"; Skid Length=54 1/2"; Skid Spacing=27"; U Tube Extension=11 1/16"; U Tube Radius=6 3/8"; Unit Height=88 5/8"; Unit Radius=27 7/8"; Weight=2580
- 4200 L 500A-QWD: BW Inlet Conn X=3 13/16"; BW Inlet NPT=3"; BW Inlet Radius=1 1/2"; BW Inlet Y=18 11/16"; BW Outlet Conn X=3 13/16"; BW Outlet NPT=3"; BW Outlet Radius=1 1/2"; BW Outlet Y=33 11/16"; BW Plumbing Total Z=18 9/16"; BW Up=16 13/16"; BW Up Radius=1 1/2"; BW X=23 5/16"; BW Z=7 1/2"; Boiler Water Flow Rate at 180F=179 GPM; Cold Water Extension=7 3/8"; Cold Water Inlet Z=5"; Cold Water NPT=2 1/2"; Cold Water Radius=1 1/4"; Control Enclosure Location=20"; Control Panel Extension=34 7/8"; Drain Extension=31 3/4"; Drain NPT=1 1/2"; Drain Radius=3/4"; Energy Extension=32 7/8"; Flat Side Distance=55 3/4"; Front Skid Extension=82 3/8"; Height to Drain=1 3/4"; Height to Energy=29 15/16"; Height to Hot Outlet=57 3/8"; Height to Relief=58"; Hot Outlet Angle=90.00°; Hot Outlet Extension=28 7/8"; Hot Outlet NPT=3"; Hot Outlet Offset Horiz=28 7/8"; Hot Outlet Offset Vert=0"; Hot Outlet Radius=1 1/2"; Rear Skid Extension=27 7/8"; Recovery Rate 40F to 140F (GPH)=2100; Relief Valve Extension=30 7/8"; Skid Length=54 1/2"; Skid Spacing=27"; U Tube Extension=11 1/16"; U Tube Radius=6 3/8"; Unit Height=76 1/16"; Unit Radius=27 7/8"; Weight=2350
- 4000 L 600A-QW: BW Inlet Conn X=3 13/16"; BW Inlet NPT=3"; BW Inlet Radius=1 1/2"; BW Inlet Y=18 11/16"; BW Outlet Conn X=3 13/16"; BW Outlet NPT=3"; BW Outlet Radius=1 1/2"; BW Outlet Y=33 11/16"; BW Plumbing Total Z=18 9/16"; BW Up=16 13/16"; BW Up Radius=1 1/2"; BW X=23 5/16"; BW Z=7 1/2"; Boiler Water Flow Rate at 180F=152 GPM; Cold Water Extension=7 3/8"; Cold Water Inlet Z=5"; Cold Water NPT=2 1/2"; Cold Water Radius=1 1/4"; Control Enclosure Location=20"; Control Panel Extension=34 7/8"; Drain Extension=31 3/4"; Drain NPT=1 1/2"; Drain Radius=3/4"; Energy Extension=32 7/8"; Flat Side Distance=55 3/4"; Front Skid Extension=82 3/8"; Height to Drain=1 3/4"; Height to Energy=29 15/16"; Height to Hot Outlet=69 3/8"; Height to Relief=70"; Hot Outlet Angle=90.00°; Hot Outlet Extension=28 7/8"; Hot Outlet NPT=3"; Hot Outlet Offset Horiz=28 7/8"; Hot Outlet Offset Vert=0"; Hot Outlet Radius=1 1/2"; Rear Skid Extension=27 7/8"; Recovery Rate 40F to 140F (GPH)=1790; Relief Valve Extension=30 7/8"; Skid Length=54 1/2"; Skid Spacing=27"; U Tube Extension=11 1/16"; U Tube Radius=6 3/8"; Unit Height=88 5/8"; Unit Radius=27 7/8"; Weight=2320
- 4000 L 500A-QW: BW Inlet Conn X=3 13/16"; BW Inlet NPT=3"; BW Inlet Radius=1 1/2"; BW Inlet Y=18 11/16"; BW Outlet Conn X=3 13/16"; BW Outlet NPT=3"; BW Outlet Radius=1 1/2"; BW Outlet Y=33 11/16"; BW Plumbing Total Z=18 9/16"; BW Up=16 13/16"; BW Up Radius=1 1/2"; BW X=23 5/16"; BW Z=7 1/2"; Boiler Water Flow Rate at 180F=152 GPM; Cold Water Extension=7 3/8"; Cold Water Inlet Z=5"; Cold Water NPT=2 1/2"; Cold Water Radius=1 1/4"; Control Enclosure Location=20"; Control Panel Extension=34 7/8"; Drain Extension=31 3/4"; Drain NPT=1 1/2"; Drain Radius=3/4"; Energy Extension=32 7/8"; Flat Side Distance=55 3/4"; Front Skid Extension=82 3/8"; Height to Drain=1 3/4"; Height to Energy=29 15/16"; Height to Hot Outlet=57 3/8"; Height to Relief=58"; Hot Outlet Angle=90.00°; Hot Outlet Extension=28 7/8"; Hot Outlet NPT=3"; Hot Outlet Offset Horiz=28 7/8"; Hot Outlet Offset Vert=0"; Hot Outlet Radius=1 1/2"; Rear Skid Extension=27 7/8"; Recovery Rate 40F to 140F (GPH)=1790; Relief Valve Extension=30 7/8"; Skid Length=54 1/2"; Skid Spacing=27"; U Tube Extension=11 1/16"; U Tube Radius=6 3/8"; Unit Height=76 1/16"; Unit Radius=27 7/8"; Weight=2100
- 3500 L 600A-QW: BW Inlet Conn X=2 15/16"; BW Inlet NPT=2 1/2"; BW Inlet Radius=1 1/4"; BW Inlet Y=18 11/16"; BW Outlet Conn X=2 15/16"; BW Outlet NPT=2 1/2"; BW Outlet Radius=1 1/4"; BW Outlet Y=33 11/16"; BW Plumbing Total Z=18 1/16"; BW Up=15 15/16"; BW Up Radius=1 1/4"; BW X=22 7/16"; BW Z=7 1/2"; Boiler Water Flow Rate at 180F=138 GPM; Cold Water Extension=6 3/8"; Cold Water Inlet Z=5 1/8"; Cold Water NPT=2 1/2"; Cold Water Radius=1 1/4"; Control Enclosure Location=20"; Control Panel Extension=34 7/8"; Drain Extension=31 3/4"; Drain NPT=1 1/2"; Drain Radius=3/4"; Energy Extension=32 7/8"; Flat Side Distance=55 3/4"; Front Skid Extension=82 3/8"; Height to Drain=1 3/4"; Height to Energy=29 15/16"; Height to Hot Outlet=69 3/8"; Height to Relief=70"; Hot Outlet Angle=90.00°; Hot Outlet Extension=28 7/8"; Hot Outlet NPT=3"; Hot Outlet Offset Horiz=28 7/8"; Hot Outlet Offset Vert=0"; Hot Outlet Radius=1 1/2"; Rear Skid Extension=27 7/8"; Recovery Rate 40F to 140F (GPH)=1630; Relief Valve Extension=30 7/8"; Skid Length=54 1/2"; Skid Spacing=27"; U Tube Extension=10 9/16"; U Tube Radius=5 3/8"; Unit Height=88 5/8"; Unit Radius=27 7/8"; Weight=2230
- 3500 L 500A-QW: BW Inlet Conn X=2 15/16"; BW Inlet NPT=2 1/2"; BW Inlet Radius=1 1/4"; BW Inlet Y=18 11/16"; BW Outlet Conn X=2 15/16"; BW Outlet NPT=2 1/2"; BW Outlet Radius=1 1/4"; BW Outlet Y=33 11/16"; BW Plumbing Total Z=18 1/16"; BW Up=15 15/16"; BW Up Radius=1 1/4"; BW X=22 7/16"; BW Z=7 1/2"; Boiler Water Flow Rate at 180F=138 GPM; Cold Water Extension=6 3/8"; Cold Water Inlet Z=5 1/8"; Cold Water NPT=2 1/2"; Cold Water Radius=1 1/4"; Control Enclosure Location=20"; Control Panel Extension=34 7/8"; Drain Extension=31 3/4"; Drain NPT=1 1/2"; Drain Radius=3/4"; Energy Extension=32 7/8"; Flat Side Distance=55 3/4"; Front Skid Extension=82 3/8"; Height to Drain=1 3/4"; Height to Energy=29 15/16"; Height to Hot Outlet=57 3/8"; Height to Relief=58"; Hot Outlet Angle=90.00°; Hot Outlet Extension=28 7/8"; Hot Outlet NPT=3"; Hot Outlet Offset Horiz=28 7/8"; Hot Outlet Offset Vert=0"; Hot Outlet Radius=1 1/2"; Rear Skid Extension=27 7/8"; Recovery Rate 40F to 140F (GPH)=1630; Relief Valve Extension=30 7/8"; Skid Length=54 1/2"; Skid Spacing=27"; U Tube Extension=10 9/16"; U Tube Radius=5 3/8"; Unit Height=76 1/16"; Unit Radius=27 7/8"; Weight=2000
- 3400 L 600A-QWD: BW Inlet Conn X=3 11/16"; BW Inlet NPT=2 1/2"; BW Inlet Radius=1 1/4"; BW Inlet Y=18 11/16"; BW Outlet Conn X=3 11/16"; BW Outlet NPT=2 1/2"; BW Outlet Radius=1 1/4"; BW Outlet Y=33 11/16"; BW Plumbing Total Z=18 9/16"; BW Up=16 13/16"; BW Up Radius=1 1/4"; BW X=23 5/16"; BW Z=7 1/2"; Boiler Water Flow Rate at 180F=138 GPM; Cold Water Extension=7 3/8"; Cold Water Inlet Z=5"; Cold Water NPT=2 1/2"; Cold Water Radius=1 1/4"; Control Enclosure Location=20"; Control Panel Extension=34 7/8"; Drain Extension=31 3/4"; Drain NPT=1 1/2"; Drain Radius=3/4"; Energy Extension=32 7/8"; Flat Side Distance=55 3/4"; Front Skid Extension=82 3/8"; Height to Drain=1 3/4"; Height to Energy=29 15/16"; Height to Hot Outlet=69 3/8"; Height to Relief=70"; Hot Outlet Angle=90.00°; Hot Outlet Extension=28 7/8"; Hot Outlet NPT=3"; Hot Outlet Offset Horiz=28 7/8"; Hot Outlet Offset Vert=0"; Hot Outlet Radius=1 1/2"; Rear Skid Extension=27 7/8"; Recovery Rate 40F to 140F (GPH)=1620; Relief Valve Extension=30 7/8"; Skid Length=54 1/2"; Skid Spacing=27"; U Tube Extension=11 1/16"; U Tube Radius=6 3/8"; Unit Height=88 5/8"; Unit Radius=27 7/8"; Weight=2500
- 3400 L 500A-QWD: BW Inlet Conn X=3 11/16"; BW Inlet NPT=2 1/2"; BW Inlet Radius=1 1/4"; BW Inlet Y=18 11/16"; BW Outlet Conn X=3 11/16"; BW Outlet NPT=2 1/2"; BW Outlet Radius=1 1/4"; BW Outlet Y=33 11/16"; BW Plumbing Total Z=18 9/16"; BW Up=16 13/16"; BW Up Radius=1 1/4"; BW X=23 5/16"; BW Z=7 1/2"; Boiler Water Flow Rate at 180F=138 GPM; Cold Water Extension=7 3/8"; Cold Water Inlet Z=5"; Cold Water NPT=2 1/2"; Cold Water Radius=1 1/4"; Control Enclosure Location=20"; Control Panel Extension=34 7/8"; Drain Extension=31 3/4"; Drain NPT=1 1/2"; Drain Radius=3/4"; Energy Extension=32 7/8"; Flat Side Distance=55 3/4"; Front Skid Extension=82 3/8"; Height to Drain=1 3/4"; Height to Energy=29 15/16"; Height to Hot Outlet=57 3/8"; Height to Relief=58"; Hot Outlet Angle=90.00°; Hot Outlet Extension=28 7/8"; Hot Outlet NPT=3"; Hot Outlet Offset Horiz=28 7/8"; Hot Outlet Offset Vert=0"; Hot Outlet Radius=1 1/2"; Rear Skid Extension=27 7/8"; Recovery Rate 40F to 140F (GPH)=1620; Relief Valve Extension=30 7/8"; Skid Length=54 1/2"; Skid Spacing=27"; U Tube Extension=11 1/16"; U Tube Radius=6 3/8"; Unit Height=76 1/16"; Unit Radius=27 7/8"; Weight=2270
- 3000 L 600A-QW: BW Inlet Conn X=2 15/16"; BW Inlet NPT=2 1/2"; BW Inlet Radius=1 1/4"; BW Inlet Y=18 11/16"; BW Outlet Conn X=2 15/16"; BW Outlet NPT=2 1/2"; BW Outlet Radius=1 1/4"; BW Outlet Y=33 11/16"; BW Plumbing Total Z=18 1/16"; BW Up=15 15/16"; BW Up Radius=1 1/4"; BW X=22 7/16"; BW Z=7 1/2"; Boiler Water Flow Rate at 180F=120 GPM; Cold Water Extension=6 3/8"; Cold Water Inlet Z=5 1/8"; Cold Water NPT=2 1/2"; Cold Water Radius=1 1/4"; Control Enclosure Location=20"; Control Panel Extension=34 7/8"; Drain Extension=31 3/4"; Drain NPT=1 1/2"; Drain Radius=3/4"; Energy Extension=32 7/8"; Flat Side Distance=55 3/4"; Front Skid Extension=82 3/8"; Height to Drain=1 3/4"; Height to Energy=29 15/16"; Height to Hot Outlet=69 3/8"; Height to Relief=70"; Hot Outlet Angle=90.00°; Hot Outlet Extension=28 7/8"; Hot Outlet NPT=3"; Hot Outlet Offset Horiz=28 7/8"; Hot Outlet Offset Vert=0"; Hot Outlet Radius=1 1/2"; Rear Skid Extension=27 7/8"; Recovery Rate 40F to 140F (GPH)=1420; Relief Valve Extension=30 7/8"; Skid Length=54 1/2"; Skid Spacing=27"; U Tube Extension=10 9/16"; U Tube Radius=5 3/8"; Unit Height=88 5/8"; Unit Radius=27 7/8"; Weight=2230
- 3000 L 500A-QW: BW Inlet Conn X=2 15/16"; BW Inlet NPT=2 1/2"; BW Inlet Radius=1 1/4"; BW Inlet Y=18 11/16"; BW Outlet Conn X=2 15/16"; BW Outlet NPT=2 1/2"; BW Outlet Radius=1 1/4"; BW Outlet Y=33 11/16"; BW Plumbing Total Z=18 1/16"; BW Up=15 15/16"; BW Up Radius=1 1/4"; BW X=22 7/16"; BW Z=7 1/2"; Boiler Water Flow Rate at 180F=120 GPM; Cold Water Extension=6 3/8"; Cold Water Inlet Z=5 1/8"; Cold Water NPT=2 1/2"; Cold Water Radius=1 1/4"; Control Enclosure Location=20"; Control Panel Extension=34 7/8"; Drain Extension=31 3/4"; Drain NPT=1 1/2"; Drain Radius=3/4"; Energy Extension=32 7/8"; Flat Side Distance=55 3/4"; Front Skid Extension=82 3/8"; Height to Drain=1 3/4"; Height to Energy=29 15/16"; Height to Hot Outlet=57 3/8"; Height to Relief=58"; Hot Outlet Angle=90.00°; Hot Outlet Extension=28 7/8"; Hot Outlet NPT=3"; Hot Outlet Offset Horiz=28 7/8"; Hot Outlet Offset Vert=0"; Hot Outlet Radius=1 1/2"; Rear Skid Extension=27 7/8"; Recovery Rate 40F to 140F (GPH)=1420; Relief Valve Extension=30 7/8"; Skid Length=54 1/2"; Skid Spacing=27"; U Tube Extension=10 9/16"; U Tube Radius=5 3/8"; Unit Height=76 1/16"; Unit Radius=27 7/8"; Weight=2000
- 300 L 600A-QW: BW Inlet Conn X=1 5/16"; BW Inlet NPT=3/4"; BW Inlet Radius=3/8"; BW Inlet Y=5"; BW Outlet Conn X=1 5/16"; BW Outlet NPT=3/4"; BW Outlet Radius=3/8"; BW Outlet Y=9 1/16"; BW Plumbing Total Z=15 3/8"; BW Up=5 3/4"; BW Up Radius=3/8"; BW X=8 1/16"; BW Z=5 15/16"; Boiler Water Flow Rate at 180F=12 GPM; Cold Water Extension=3 1/4"; Cold Water Inlet Z=5 5/8"; Cold Water NPT=2"; Cold Water Radius=1"; Control Enclosure Location=20"; Control Panel Extension=34 7/8"; Drain Extension=31 3/4"; Drain NPT=1 1/2"; Drain Radius=3/4"; Energy Extension=32 7/8"; Flat Side Distance=55 3/4"; Front Skid Extension=82 3/8"; Height to Drain=1 3/4"; Height to Energy=29 15/16"; Height to Hot Outlet=69 3/8"; Height to Relief=70"; Hot Outlet Angle=90.00°; Hot Outlet Extension=28 7/8"; Hot Outlet NPT=3"; Hot Outlet Offset Horiz=28 7/8"; Hot Outlet Offset Vert=0"; Hot Outlet Radius=1 1/2"; Rear Skid Extension=27 7/8"; Recovery Rate 40F to 140F (GPH)=140; Relief Valve Extension=30 7/8"; Skid Length=54 1/2"; Skid Spacing=27"; U Tube Extension=9 7/16"; U Tube Radius=2 1/4"; Unit Height=88 5/8"; Unit Radius=27 7/8"; Weight=1890
- 300 L 500A-QW: BW Inlet Conn X=1 5/16"; BW Inlet NPT=3/4"; BW Inlet Radius=3/8"; BW Inlet Y=5"; BW Outlet Conn X=1 5/16"; BW Outlet NPT=3/4"; BW Outlet Radius=3/8"; BW Outlet Y=9 1/16"; BW Plumbing Total Z=15 3/8"; BW Up=5 3/4"; BW Up Radius=3/8"; BW X=8 1/16"; BW Z=5 15/16"; Boiler Water Flow Rate at 180F=12 GPM; Cold Water Extension=3 1/4"; Cold Water Inlet Z=5 5/8"; Cold Water NPT=2"; Cold Water Radius=1"; Control Enclosure Location=20"; Control Panel Extension=34 7/8"; Drain Extension=31 3/4"; Drain NPT=1 1/2"; Drain Radius=3/4"; Energy Extension=32 7/8"; Flat Side Distance=55 3/4"; Front Skid Extension=82 3/8"; Height to Drain=1 3/4"; Height to Energy=29 15/16"; Height to Hot Outlet=57 3/8"; Height to Relief=58"; Hot Outlet Angle=90.00°; Hot Outlet Extension=28 7/8"; Hot Outlet NPT=3"; Hot Outlet Offset Horiz=28 7/8"; Hot Outlet Offset Vert=0"; Hot Outlet Radius=1 1/2"; Rear Skid Extension=27 7/8"; Recovery Rate 40F to 140F (GPH)=140; Relief Valve Extension=30 7/8"; Skid Length=54 1/2"; Skid Spacing=27"; U Tube Extension=9 7/16"; U Tube Radius=2 1/4"; Unit Height=76 1/16"; Unit Radius=27 7/8"; Weight=1670
- 2800 L 600A-QWD: BW Inlet Conn X=3 11/16"; BW Inlet NPT=2 1/2"; BW Inlet Radius=1 1/4"; BW Inlet Y=12 3/8"; BW Outlet Conn X=3 11/16"; BW Outlet NPT=2 1/2"; BW Outlet Radius=1 1/4"; BW Outlet Y=23 7/16"; BW Plumbing Total Z=22 1/16"; BW Up=13 1/16"; BW Up Radius=1 1/4"; BW X=17 13/16"; BW Z=11 1/2"; Boiler Water Flow Rate at 180F=122 GPM; Cold Water Extension=7 3/8"; Cold Water Inlet Z=5 1/8"; Cold Water NPT=2 1/2"; Cold Water Radius=1 1/4"; Control Enclosure Location=20"; Control Panel Extension=34 7/8"; Drain Extension=31 3/4"; Drain NPT=1 1/2"; Drain Radius=3/4"; Energy Extension=32 7/8"; Flat Side Distance=55 3/4"; Front Skid Extension=82 3/8"; Height to Drain=1 3/4"; Height to Energy=29 15/16"; Height to Hot Outlet=69 3/8"; Height to Relief=70"; Hot Outlet Angle=90.00°; Hot Outlet Extension=28 7/8"; Hot Outlet NPT=3"; Hot Outlet Offset Horiz=28 7/8"; Hot Outlet Offset Vert=0"; Hot Outlet Radius=1 1/2"; Rear Skid Extension=27 7/8"; Recovery Rate 40F to 140F (GPH)=1430; Relief Valve Extension=30 7/8"; Skid Length=54 1/2"; Skid Spacing=27"; U Tube Extension=10 9/16"; U Tube Radius=6 3/8"; Unit Height=88 5/8"; Unit Radius=27 7/8"; Weight=2300
- 2800 L 500A-QWD: BW Inlet Conn X=3 11/16"; BW Inlet NPT=2 1/2"; BW Inlet Radius=1 1/4"; BW Inlet Y=12 3/8"; BW Outlet Conn X=3 11/16"; BW Outlet NPT=2 1/2"; BW Outlet Radius=1 1/4"; BW Outlet Y=23 7/16"; BW Plumbing Total Z=22 1/16"; BW Up=13 1/16"; BW Up Radius=1 1/4"; BW X=17 13/16"; BW Z=11 1/2"; Boiler Water Flow Rate at 180F=122 GPM; Cold Water Extension=7 3/8"; Cold Water Inlet Z=5 1/8"; Cold Water NPT=2 1/2"; Cold Water Radius=1 1/4"; Control Enclosure Location=20"; Control Panel Extension=34 7/8"; Drain Extension=31 3/4"; Drain NPT=1 1/2"; Drain Radius=3/4"; Energy Extension=32 7/8"; Flat Side Distance=55 3/4"; Front Skid Extension=82 3/8"; Height to Drain=1 3/4"; Height to Energy=29 15/16"; Height to Hot Outlet=57 3/8"; Height to Relief=58"; Hot Outlet Angle=90.00°; Hot Outlet Extension=28 7/8"; Hot Outlet NPT=3"; Hot Outlet Offset Horiz=28 7/8"; Hot Outlet Offset Vert=0"; Hot Outlet Radius=1 1/2"; Rear Skid Extension=27 7/8"; Recovery Rate 40F to 140F (GPH)=1430; Relief Valve Extension=30 7/8"; Skid Length=54 1/2"; Skid Spacing=27"; U Tube Extension=10 9/16"; U Tube Radius=6 3/8"; Unit Height=76 1/16"; Unit Radius=27 7/8"; Weight=2080
- 2600 L 600A-QW: BW Inlet Conn X=2 15/16"; BW Inlet NPT=2 1/2"; BW Inlet Radius=1 1/4"; BW Inlet Y=12 3/8"; BW Outlet Conn X=2 15/16"; BW Outlet NPT=2 1/2"; BW Outlet Radius=1 1/4"; BW Outlet Y=23 7/16"; BW Plumbing Total Z=22 1/16"; BW Up=13 1/16"; BW Up Radius=1 1/4"; BW X=17 13/16"; BW Z=11 1/2"; Boiler Water Flow Rate at 180F=102 GPM; Cold Water Extension=6 3/8"; Cold Water Inlet Z=5 1/8"; Cold Water NPT=2 1/2"; Cold Water Radius=1 1/4"; Control Enclosure Location=20"; Control Panel Extension=34 7/8"; Drain Extension=31 3/4"; Drain NPT=1 1/2"; Drain Radius=3/4"; Energy Extension=32 7/8"; Flat Side Distance=55 3/4"; Front Skid Extension=82 3/8"; Height to Drain=1 3/4"; Height to Energy=29 15/16"; Height to Hot Outlet=69 3/8"; Height to Relief=70"; Hot Outlet Angle=90.00°; Hot Outlet Extension=28 7/8"; Hot Outlet NPT=3"; Hot Outlet Offset Horiz=28 7/8"; Hot Outlet Offset Vert=0"; Hot Outlet Radius=1 1/2"; Rear Skid Extension=27 7/8"; Recovery Rate 40F to 140F (GPH)=1200; Relief Valve Extension=30 7/8"; Skid Length=54 1/2"; Skid Spacing=27"; U Tube Extension=10 9/16"; U Tube Radius=5 3/8"; Unit Height=88 5/8"; Unit Radius=27 7/8"; Weight=2140
- 2600 L 500A-QW: BW Inlet Conn X=2 15/16"; BW Inlet NPT=2 1/2"; BW Inlet Radius=1 1/4"; BW Inlet Y=12 3/8"; BW Outlet Conn X=2 15/16"; BW Outlet NPT=2 1/2"; BW Outlet Radius=1 1/4"; BW Outlet Y=23 7/16"; BW Plumbing Total Z=22 1/16"; BW Up=13 1/16"; BW Up Radius=1 1/4"; BW X=17 13/16"; BW Z=11 1/2"; Boiler Water Flow Rate at 180F=102 GPM; Cold Water Extension=6 3/8"; Cold Water Inlet Z=5 1/8"; Cold Water NPT=2 1/2"; Cold Water Radius=1 1/4"; Control Enclosure Location=20"; Control Panel Extension=34 7/8"; Drain Extension=31 3/4"; Drain NPT=1 1/2"; Drain Radius=3/4"; Energy Extension=32 7/8"; Flat Side Distance=55 3/4"; Front Skid Extension=82 3/8"; Height to Drain=1 3/4"; Height to Energy=29 15/16"; Height to Hot Outlet=57 3/8"; Height to Relief=58"; Hot Outlet Angle=90.00°; Hot Outlet Extension=28 7/8"; Hot Outlet NPT=3"; Hot Outlet Offset Horiz=28 7/8"; Hot Outlet Offset Vert=0"; Hot Outlet Radius=1 1/2"; Rear Skid Extension=27 7/8"; Recovery Rate 40F to 140F (GPH)=1200; Relief Valve Extension=30 7/8"; Skid Length=54 1/2"; Skid Spacing=27"; U Tube Extension=10 9/16"; U Tube Radius=5 3/8"; Unit Height=76 1/16"; Unit Radius=27 7/8"; Weight=1920
- 250 L 600A-QWD: BW Inlet Conn X=1 5/16"; BW Inlet NPT=3/4"; BW Inlet Radius=3/8"; BW Inlet Y=5"; BW Outlet Conn X=1 5/16"; BW Outlet NPT=3/4"; BW Outlet Radius=3/8"; BW Outlet Y=9 1/16"; BW Plumbing Total Z=15 3/8"; BW Up=5 3/4"; BW Up Radius=3/8"; BW X=8 1/16"; BW Z=5 15/16"; Boiler Water Flow Rate at 180F=16 GPM; Cold Water Extension=3 1/4"; Cold Water Inlet Z=5 5/8"; Cold Water NPT=2"; Cold Water Radius=1"; Control Enclosure Location=20"; Control Panel Extension=34 7/8"; Drain Extension=31 3/4"; Drain NPT=1 1/2"; Drain Radius=3/4"; Energy Extension=32 7/8"; Flat Side Distance=55 3/4"; Front Skid Extension=82 3/8"; Height to Drain=1 3/4"; Height to Energy=29 15/16"; Height to Hot Outlet=69 3/8"; Height to Relief=70"; Hot Outlet Angle=90.00°; Hot Outlet Extension=28 7/8"; Hot Outlet NPT=3"; Hot Outlet Offset Horiz=28 7/8"; Hot Outlet Offset Vert=0"; Hot Outlet Radius=1 1/2"; Rear Skid Extension=27 7/8"; Recovery Rate 40F to 140F (GPH)=180; Relief Valve Extension=30 7/8"; Skid Length=54 1/2"; Skid Spacing=27"; U Tube Extension=9 7/16"; U Tube Radius=2 1/4"; Unit Height=88 5/8"; Unit Radius=27 7/8"; Weight=1910
- 250 L 500A-QWD: BW Inlet Conn X=1 5/16"; BW Inlet NPT=3/4"; BW Inlet Radius=3/8"; BW Inlet Y=5"; BW Outlet Conn X=1 5/16"; BW Outlet NPT=3/4"; BW Outlet Radius=3/8"; BW Outlet Y=9 1/16"; BW Plumbing Total Z=15 3/8"; BW Up=5 3/4"; BW Up Radius=3/8"; BW X=8 1/16"; BW Z=5 15/16"; Boiler Water Flow Rate at 180F=11 GPM; Cold Water Extension=3 1/4"; Cold Water Inlet Z=5 5/8"; Cold Water NPT=2"; Cold Water Radius=1"; Control Enclosure Location=20"; Control Panel Extension=34 7/8"; Drain Extension=31 3/4"; Drain NPT=1 1/2"; Drain Radius=3/4"; Energy Extension=32 7/8"; Flat Side Distance=55 3/4"; Front Skid Extension=82 3/8"; Height to Drain=1 3/4"; Height to Energy=29 15/16"; Height to Hot Outlet=57 3/8"; Height to Relief=58"; Hot Outlet Angle=90.00°; Hot Outlet Extension=28 7/8"; Hot Outlet NPT=3"; Hot Outlet Offset Horiz=28 7/8"; Hot Outlet Offset Vert=0"; Hot Outlet Radius=1 1/2"; Rear Skid Extension=27 7/8"; Recovery Rate 40F to 140F (GPH)=130; Relief Valve Extension=30 7/8"; Skid Length=54 1/2"; Skid Spacing=27"; U Tube Extension=9 7/16"; U Tube Radius=2 1/4"; Unit Height=76 1/16"; Unit Radius=27 7/8"; Weight=1680
- 2300 L 600A-QW: BW Inlet Conn X=2 15/16"; BW Inlet NPT=2"; BW Inlet Radius=1"; BW Inlet Y=12 3/8"; BW Outlet Conn X=2 15/16"; BW Outlet NPT=2"; BW Outlet Radius=1"; BW Outlet Y=23 7/16"; BW Plumbing Total Z=22 1/16"; BW Up=13 1/16"; BW Up Radius=1"; BW X=17 13/16"; BW Z=11 1/2"; Boiler Water Flow Rate at 180F=87 GPM; Cold Water Extension=6 3/8"; Cold Water Inlet Z=5 1/8"; Cold Water NPT=2 1/2"; Cold Water Radius=1 1/4"; Control Enclosure Location=20"; Control Panel Extension=34 7/8"; Drain Extension=31 3/4"; Drain NPT=1 1/2"; Drain Radius=3/4"; Energy Extension=32 7/8"; Flat Side Distance=55 3/4"; Front Skid Extension=82 3/8"; Height to Drain=1 3/4"; Height to Energy=29 15/16"; Height to Hot Outlet=69 3/8"; Height to Relief=70"; Hot Outlet Angle=90.00°; Hot Outlet Extension=28 7/8"; Hot Outlet NPT=3"; Hot Outlet Offset Horiz=28 7/8"; Hot Outlet Offset Vert=0"; Hot Outlet Radius=1 1/2"; Rear Skid Extension=27 7/8"; Recovery Rate 40F to 140F (GPH)=1020; Relief Valve Extension=30 7/8"; Skid Length=54 1/2"; Skid Spacing=27"; U Tube Extension=10 9/16"; U Tube Radius=5 3/8"; Unit Height=88 5/8"; Unit Radius=27 7/8"; Weight=2130
- 2300 L 500A-QW: BW Inlet Conn X=2 15/16"; BW Inlet NPT=2"; BW Inlet Radius=1"; BW Inlet Y=12 3/8"; BW Outlet Conn X=2 15/16"; BW Outlet NPT=2"; BW Outlet Radius=1"; BW Outlet Y=23 7/16"; BW Plumbing Total Z=22 1/16"; BW Up=13 1/16"; BW Up Radius=1"; BW X=17 13/16"; BW Z=11 1/2"; Boiler Water Flow Rate at 180F=87 GPM; Cold Water Extension=6 3/8"; Cold Water Inlet Z=5 1/8"; Cold Water NPT=2 1/2"; Cold Water Radius=1 1/4"; Control Enclosure Location=20"; Control Panel Extension=34 7/8"; Drain Extension=31 3/4"; Drain NPT=1 1/2"; Drain Radius=3/4"; Energy Extension=32 7/8"; Flat Side Distance=55 3/4"; Front Skid Extension=82 3/8"; Height to Drain=1 3/4"; Height to Energy=29 15/16"; Height to Hot Outlet=57 3/8"; Height to Relief=58"; Hot Outlet Angle=90.00°; Hot Outlet Extension=28 7/8"; Hot Outlet NPT=3"; Hot Outlet Offset Horiz=28 7/8"; Hot Outlet Offset Vert=0"; Hot Outlet Radius=1 1/2"; Rear Skid Extension=27 7/8"; Recovery Rate 40F to 140F (GPH)=1020; Relief Valve Extension=30 7/8"; Skid Length=54 1/2"; Skid Spacing=27"; U Tube Extension=10 9/16"; U Tube Radius=5 3/8"; Unit Height=76 1/16"; Unit Radius=27 7/8"; Weight=1910
- 2200 L 600A-QWD: BW Inlet Conn X=2 15/16"; BW Inlet NPT=2"; BW Inlet Radius=1"; BW Inlet Y=12 3/8"; BW Outlet Conn X=2 15/16"; BW Outlet NPT=2"; BW Outlet Radius=1"; BW Outlet Y=23 7/16"; BW Plumbing Total Z=22 1/16"; BW Up=13 1/16"; BW Up Radius=1"; BW X=17 13/16"; BW Z=11 1/2"; Boiler Water Flow Rate at 180F=92 GPM; Cold Water Extension=6 3/8"; Cold Water Inlet Z=5 1/8"; Cold Water NPT=2 1/2"; Cold Water Radius=1 1/4"; Control Enclosure Location=20"; Control Panel Extension=34 7/8"; Drain Extension=31 3/4"; Drain NPT=1 1/2"; Drain Radius=3/4"; Energy Extension=32 7/8"; Flat Side Distance=55 3/4"; Front Skid Extension=82 3/8"; Height to Drain=1 3/4"; Height to Energy=29 15/16"; Height to Hot Outlet=69 3/8"; Height to Relief=70"; Hot Outlet Angle=90.00°; Hot Outlet Extension=28 7/8"; Hot Outlet NPT=3"; Hot Outlet Offset Horiz=28 7/8"; Hot Outlet Offset Vert=0"; Hot Outlet Radius=1 1/2"; Rear Skid Extension=27 7/8"; Recovery Rate 40F to 140F (GPH)=1090; Relief Valve Extension=30 7/8"; Skid Length=54 1/2"; Skid Spacing=27"; U Tube Extension=10 9/16"; U Tube Radius=5 3/8"; Unit Height=88 5/8"; Unit Radius=27 7/8"; Weight=2260
- 2200 L 500A-QWD: BW Inlet Conn X=2 15/16"; BW Inlet NPT=2"; BW Inlet Radius=1"; BW Inlet Y=12 3/8"; BW Outlet Conn X=2 15/16"; BW Outlet NPT=2"; BW Outlet Radius=1"; BW Outlet Y=23 7/16"; BW Plumbing Total Z=22 1/16"; BW Up=13 1/16"; BW Up Radius=1"; BW X=17 13/16"; BW Z=11 1/2"; Boiler Water Flow Rate at 180F=92 GPM; Cold Water Extension=6 3/8"; Cold Water Inlet Z=5 1/8"; Cold Water NPT=2 1/2"; Cold Water Radius=1 1/4"; Control Enclosure Location=20"; Control Panel Extension=34 7/8"; Drain Extension=31 3/4"; Drain NPT=1 1/2"; Drain Radius=3/4"; Energy Extension=32 7/8"; Flat Side Distance=55 3/4"; Front Skid Extension=82 3/8"; Height to Drain=1 3/4"; Height to Energy=29 15/16"; Height to Hot Outlet=57 3/8"; Height to Relief=58"; Hot Outlet Angle=90.00°; Hot Outlet Extension=28 7/8"; Hot Outlet NPT=3"; Hot Outlet Offset Horiz=28 7/8"; Hot Outlet Offset Vert=0"; Hot Outlet Radius=1 1/2"; Rear Skid Extension=27 7/8"; Recovery Rate 40F to 140F (GPH)=1090; Relief Valve Extension=30 7/8"; Skid Length=54 1/2"; Skid Spacing=27"; U Tube Extension=10 9/16"; U Tube Radius=5 3/8"; Unit Height=76 1/16"; Unit Radius=27 7/8"; Weight=2030
- 2000 L 600A-QW: BW Inlet Conn X=2 1/2"; BW Inlet NPT=2"; BW Inlet Radius=1"; BW Inlet Y=10 3/8"; BW Outlet Conn X=2 1/2"; BW Outlet NPT=2"; BW Outlet Radius=1"; BW Outlet Y=17 9/16"; BW Plumbing Total Z=20 1/8"; BW Up=10 3/8"; BW Up Radius=1"; BW X=12 13/16"; BW Z=9 5/16"; Boiler Water Flow Rate at 180F=80 GPM; Cold Water Extension=5 5/16"; Cold Water Inlet Z=5 3/8"; Cold Water NPT=2"; Cold Water Radius=1"; Control Enclosure Location=20"; Control Panel Extension=34 7/8"; Drain Extension=31 3/4"; Drain NPT=1 1/2"; Drain Radius=3/4"; Energy Extension=32 7/8"; Flat Side Distance=55 3/4"; Front Skid Extension=82 3/8"; Height to Drain=1 3/4"; Height to Energy=29 15/16"; Height to Hot Outlet=69 3/8"; Height to Relief=70"; Hot Outlet Angle=90.00°; Hot Outlet Extension=28 7/8"; Hot Outlet NPT=3"; Hot Outlet Offset Horiz=28 7/8"; Hot Outlet Offset Vert=0"; Hot Outlet Radius=1 1/2"; Rear Skid Extension=27 7/8"; Recovery Rate 40F to 140F (GPH)=950; Relief Valve Extension=30 7/8"; Skid Length=54 1/2"; Skid Spacing=27"; U Tube Extension=10 13/16"; U Tube Radius=4 5/16"; Unit Height=88 5/8"; Unit Radius=27 7/8"; Weight=2060
- 2000 L 500A-QW: BW Inlet Conn X=2 1/2"; BW Inlet NPT=2"; BW Inlet Radius=1"; BW Inlet Y=10 3/8"; BW Outlet Conn X=2 1/2"; BW Outlet NPT=2"; BW Outlet Radius=1"; BW Outlet Y=17 9/16"; BW Plumbing Total Z=20 1/8"; BW Up=10 3/8"; BW Up Radius=1"; BW X=12 13/16"; BW Z=9 5/16"; Boiler Water Flow Rate at 180F=80 GPM; Cold Water Extension=5 5/16"; Cold Water Inlet Z=5 3/8"; Cold Water NPT=2"; Cold Water Radius=1"; Control Enclosure Location=20"; Control Panel Extension=34 7/8"; Drain Extension=31 3/4"; Drain NPT=1 1/2"; Drain Radius=3/4"; Energy Extension=32 7/8"; Flat Side Distance=55 3/4"; Front Skid Extension=82 3/8"; Height to Drain=1 3/4"; Height to Energy=29 15/16"; Height to Hot Outlet=57 3/8"; Height to Relief=58"; Hot Outlet Angle=90.00°; Hot Outlet Extension=28 7/8"; Hot Outlet NPT=3"; Hot Outlet Offset Horiz=28 7/8"; Hot Outlet Offset Vert=0"; Hot Outlet Radius=1 1/2"; Rear Skid Extension=27 7/8"; Recovery Rate 40F to 140F (GPH)=950; Relief Valve Extension=30 7/8"; Skid Length=54 1/2"; Skid Spacing=27"; U Tube Extension=10 13/16"; U Tube Radius=4 5/16"; Unit Height=76 1/16"; Unit Radius=27 7/8"; Weight=1830
- 1900 L 600A-QWD: BW Inlet Conn X=2 15/16"; BW Inlet NPT=2"; BW Inlet Radius=1"; BW Inlet Y=10 3/8"; BW Outlet Conn X=2 15/16"; BW Outlet NPT=2"; BW Outlet Radius=1"; BW Outlet Y=17 9/16"; BW Plumbing Total Z=19 7/8"; BW Up=10 13/16"; BW Up Radius=1"; BW X=13 7/8"; BW Z=9 5/16"; Boiler Water Flow Rate at 180F=80 GPM; Cold Water Extension=6 3/8"; Cold Water Inlet Z=5 1/8"; Cold Water NPT=2 1/2"; Cold Water Radius=1 1/4"; Control Enclosure Location=20"; Control Panel Extension=34 7/8"; Drain Extension=31 3/4"; Drain NPT=1 1/2"; Drain Radius=3/4"; Energy Extension=32 7/8"; Flat Side Distance=55 3/4"; Front Skid Extension=82 3/8"; Height to Drain=1 3/4"; Height to Energy=29 15/16"; Height to Hot Outlet=69 3/8"; Height to Relief=70"; Hot Outlet Angle=90.00°; Hot Outlet Extension=28 7/8"; Hot Outlet NPT=3"; Hot Outlet Offset Horiz=28 7/8"; Hot Outlet Offset Vert=0"; Hot Outlet Radius=1 1/2"; Rear Skid Extension=27 7/8"; Recovery Rate 40F to 140F (GPH)=950; Relief Valve Extension=30 7/8"; Skid Length=54 1/2"; Skid Spacing=27"; U Tube Extension=10 9/16"; U Tube Radius=5 3/8"; Unit Height=88 5/8"; Unit Radius=27 7/8"; Weight=2220
- 1900 L 500A-QWD: BW Inlet Conn X=2 15/16"; BW Inlet NPT=2"; BW Inlet Radius=1"; BW Inlet Y=10 3/8"; BW Outlet Conn X=2 15/16"; BW Outlet NPT=2"; BW Outlet Radius=1"; BW Outlet Y=17 9/16"; BW Plumbing Total Z=19 7/8"; BW Up=10 13/16"; BW Up Radius=1"; BW X=13 7/8"; BW Z=9 5/16"; Boiler Water Flow Rate at 180F=80 GPM; Cold Water Extension=6 3/8"; Cold Water Inlet Z=5 1/8"; Cold Water NPT=2 1/2"; Cold Water Radius=1 1/4"; Control Enclosure Location=20"; Control Panel Extension=34 7/8"; Drain Extension=31 3/4"; Drain NPT=1 1/2"; Drain Radius=3/4"; Energy Extension=32 7/8"; Flat Side Distance=55 3/4"; Front Skid Extension=82 3/8"; Height to Drain=1 3/4"; Height to Energy=29 15/16"; Height to Hot Outlet=57 3/8"; Height to Relief=58"; Hot Outlet Angle=90.00°; Hot Outlet Extension=28 7/8"; Hot Outlet NPT=3"; Hot Outlet Offset Horiz=28 7/8"; Hot Outlet Offset Vert=0"; Hot Outlet Radius=1 1/2"; Rear Skid Extension=27 7/8"; Recovery Rate 40F to 140F (GPH)=950; Relief Valve Extension=30 7/8"; Skid Length=54 1/2"; Skid Spacing=27"; U Tube Extension=10 9/16"; U Tube Radius=5 3/8"; Unit Height=76 1/16"; Unit Radius=27 7/8"; Weight=2000
- 1500 L 600A-QW: BW Inlet Conn X=2 1/2"; BW Inlet NPT=1 1/2"; BW Inlet Radius=3/4"; BW Inlet Y=10 3/8"; BW Outlet Conn X=2 1/2"; BW Outlet NPT=1 1/2"; BW Outlet Radius=3/4"; BW Outlet Y=17 9/16"; BW Plumbing Total Z=20 1/8"; BW Up=10 3/8"; BW Up Radius=3/4"; BW X=12 13/16"; BW Z=9 5/16"; Boiler Water Flow Rate at 180F=58 GPM; Cold Water Extension=5 5/16"; Cold Water Inlet Z=5 3/8"; Cold Water NPT=2"; Cold Water Radius=1"; Control Enclosure Location=20"; Control Panel Extension=34 7/8"; Drain Extension=31 3/4"; Drain NPT=1 1/2"; Drain Radius=3/4"; Energy Extension=32 7/8"; Flat Side Distance=55 3/4"; Front Skid Extension=82 3/8"; Height to Drain=1 3/4"; Height to Energy=29 15/16"; Height to Hot Outlet=69 3/8"; Height to Relief=70"; Hot Outlet Angle=90.00°; Hot Outlet Extension=28 7/8"; Hot Outlet NPT=3"; Hot Outlet Offset Horiz=28 7/8"; Hot Outlet Offset Vert=0"; Hot Outlet Radius=1 1/2"; Rear Skid Extension=27 7/8"; Recovery Rate 40F to 140F (GPH)=690; Relief Valve Extension=30 7/8"; Skid Length=54 1/2"; Skid Spacing=27"; U Tube Extension=10 13/16"; U Tube Radius=4 5/16"; Unit Height=88 5/8"; Unit Radius=27 7/8"; Weight=2040
- 1500 L 500A-QW: BW Inlet Conn X=2 1/2"; BW Inlet NPT=1 1/2"; BW Inlet Radius=3/4"; BW Inlet Y=10 3/8"; BW Outlet Conn X=2 1/2"; BW Outlet NPT=1 1/2"; BW Outlet Radius=3/4"; BW Outlet Y=17 9/16"; BW Plumbing Total Z=20 1/8"; BW Up=10 3/8"; BW Up Radius=3/4"; BW X=12 13/16"; BW Z=9 5/16"; Boiler Water Flow Rate at 180F=58 GPM; Cold Water Extension=5 5/16"; Cold Water Inlet Z=5 3/8"; Cold Water NPT=2"; Cold Water Radius=1"; Control Enclosure Location=20"; Control Panel Extension=34 7/8"; Drain Extension=31 3/4"; Drain NPT=1 1/2"; Drain Radius=3/4"; Energy Extension=32 7/8"; Flat Side Distance=55 3/4"; Front Skid Extension=82 3/8"; Height to Drain=1 3/4"; Height to Energy=29 15/16"; Height to Hot Outlet=57 3/8"; Height to Relief=58"; Hot Outlet Angle=90.00°; Hot Outlet Extension=28 7/8"; Hot Outlet NPT=3"; Hot Outlet Offset Horiz=28 7/8"; Hot Outlet Offset Vert=0"; Hot Outlet Radius=1 1/2"; Rear Skid Extension=27 7/8"; Recovery Rate 40F to 140F (GPH)=690; Relief Valve Extension=30 7/8"; Skid Length=54 1/2"; Skid Spacing=27"; U Tube Extension=10 13/16"; U Tube Radius=4 5/16"; Unit Height=76 1/16"; Unit Radius=27 7/8"; Weight=1810
- 1300 L 600A-QWD: BW Inlet Conn X=2 1/2"; BW Inlet NPT=1 1/2"; BW Inlet Radius=3/4"; BW Inlet Y=8 3/8"; BW Outlet Conn X=2 1/2"; BW Outlet NPT=1 1/2"; BW Outlet Radius=3/4"; BW Outlet Y=15 1/4"; BW Plumbing Total Z=19 1/4"; BW Up=8 5/8"; BW Up Radius=3/4"; BW X=11 11/16"; BW Z=8 7/16"; Boiler Water Flow Rate at 180F=53 GPM; Cold Water Extension=5 5/16"; Cold Water Inlet Z=5 3/8"; Cold Water NPT=2"; Cold Water Radius=1"; Control Enclosure Location=20"; Control Panel Extension=34 7/8"; Drain Extension=31 3/4"; Drain NPT=1 1/2"; Drain Radius=3/4"; Energy Extension=32 7/8"; Flat Side Distance=55 3/4"; Front Skid Extension=82 3/8"; Height to Drain=1 3/4"; Height to Energy=29 15/16"; Height to Hot Outlet=69 3/8"; Height to Relief=70"; Hot Outlet Angle=90.00°; Hot Outlet Extension=28 7/8"; Hot Outlet NPT=3"; Hot Outlet Offset Horiz=28 7/8"; Hot Outlet Offset Vert=0"; Hot Outlet Radius=1 1/2"; Rear Skid Extension=27 7/8"; Recovery Rate 40F to 140F (GPH)=620; Relief Valve Extension=30 7/8"; Skid Length=54 1/2"; Skid Spacing=27"; U Tube Extension=10 13/16"; U Tube Radius=4 5/16"; Unit Height=88 5/8"; Unit Radius=27 7/8"; Weight=2080
- 1300 L 500A-QWD: BW Inlet Conn X=2 1/2"; BW Inlet NPT=1 1/2"; BW Inlet Radius=3/4"; BW Inlet Y=8 3/8"; BW Outlet Conn X=2 1/2"; BW Outlet NPT=1 1/2"; BW Outlet Radius=3/4"; BW Outlet Y=15 1/4"; BW Plumbing Total Z=19 1/4"; BW Up=8 5/8"; BW Up Radius=3/4"; BW X=11 11/16"; BW Z=8 7/16"; Boiler Water Flow Rate at 180F=53 GPM; Cold Water Extension=5 5/16"; Cold Water Inlet Z=5 3/8"; Cold Water NPT=2"; Cold Water Radius=1"; Control Enclosure Location=20"; Control Panel Extension=34 7/8"; Drain Extension=31 3/4"; Drain NPT=1 1/2"; Drain Radius=3/4"; Energy Extension=32 7/8"; Flat Side Distance=55 3/4"; Front Skid Extension=82 3/8"; Height to Drain=1 3/4"; Height to Energy=29 15/16"; Height to Hot Outlet=57 3/8"; Height to Relief=58"; Hot Outlet Angle=90.00°; Hot Outlet Extension=28 7/8"; Hot Outlet NPT=3"; Hot Outlet Offset Horiz=28 7/8"; Hot Outlet Offset Vert=0"; Hot Outlet Radius=1 1/2"; Rear Skid Extension=27 7/8"; Recovery Rate 40F to 140F (GPH)=620; Relief Valve Extension=30 7/8"; Skid Length=54 1/2"; Skid Spacing=27"; U Tube Extension=10 13/16"; U Tube Radius=4 5/16"; Unit Height=76 1/16"; Unit Radius=27 7/8"; Weight=1850
- 1100 L 600A-QW: BW Inlet Conn X=1 7/8"; BW Inlet NPT=1 1/4"; BW Inlet Radius=5/8"; BW Inlet Y=8 3/8"; BW Outlet Conn X=1 7/8"; BW Outlet NPT=1 1/4"; BW Outlet Radius=5/8"; BW Outlet Y=15 1/4"; BW Plumbing Total Z=18 1/4"; BW Up=8"; BW Up Radius=5/8"; BW X=11 1/16"; BW Z=8 7/16"; Boiler Water Flow Rate at 180F=43 GPM; Cold Water Extension=4 5/16"; Cold Water Inlet Z=5 5/8"; Cold Water NPT=2"; Cold Water Radius=1"; Control Enclosure Location=20"; Control Panel Extension=34 7/8"; Drain Extension=31 3/4"; Drain NPT=1 1/2"; Drain Radius=3/4"; Energy Extension=32 7/8"; Flat Side Distance=55 3/4"; Front Skid Extension=82 3/8"; Height to Drain=1 3/4"; Height to Energy=29 15/16"; Height to Hot Outlet=69 3/8"; Height to Relief=70"; Hot Outlet Angle=90.00°; Hot Outlet Extension=28 7/8"; Hot Outlet NPT=3"; Hot Outlet Offset Horiz=28 7/8"; Hot Outlet Offset Vert=0"; Hot Outlet Radius=1 1/2"; Rear Skid Extension=27 7/8"; Recovery Rate 40F to 140F (GPH)=510; Relief Valve Extension=30 7/8"; Skid Length=54 1/2"; Skid Spacing=27"; U Tube Extension=9 13/16"; U Tube Radius=3 5/16"; Unit Height=88 5/8"; Unit Radius=27 7/8"; Weight=1950
- 1100 L 500A-QW: BW Inlet Conn X=1 7/8"; BW Inlet NPT=1 1/4"; BW Inlet Radius=5/8"; BW Inlet Y=8 3/8"; BW Outlet Conn X=1 7/8"; BW Outlet NPT=1 1/4"; BW Outlet Radius=5/8"; BW Outlet Y=15 1/4"; BW Plumbing Total Z=18 1/4"; BW Up=8"; BW Up Radius=5/8"; BW X=11 1/16"; BW Z=8 7/16"; Boiler Water Flow Rate at 180F=43 GPM; Cold Water Extension=4 5/16"; Cold Water Inlet Z=5 5/8"; Cold Water NPT=2"; Cold Water Radius=1"; Control Enclosure Location=20"; Control Panel Extension=34 7/8"; Drain Extension=31 3/4"; Drain NPT=1 1/2"; Drain Radius=3/4"; Energy Extension=32 7/8"; Flat Side Distance=55 3/4"; Front Skid Extension=82 3/8"; Height to Drain=1 3/4"; Height to Energy=29 15/16"; Height to Hot Outlet=57 3/8"; Height to Relief=58"; Hot Outlet Angle=90.00°; Hot Outlet Extension=28 7/8"; Hot Outlet NPT=3"; Hot Outlet Offset Horiz=28 7/8"; Hot Outlet Offset Vert=0"; Hot Outlet Radius=1 1/2"; Rear Skid Extension=27 7/8"; Recovery Rate 40F to 140F (GPH)=510; Relief Valve Extension=30 7/8"; Skid Length=54 1/2"; Skid Spacing=27"; U Tube Extension=9 13/16"; U Tube Radius=3 5/16"; Unit Height=76 1/16"; Unit Radius=27 7/8"; Weight=1730
- 900 L 400A-QWD: BW Inlet Conn X=2 1/2"; BW Inlet NPT=1 1/4"; BW Inlet Radius=5/8"; BW Inlet Y=6 3/4"; BW Outlet Conn X=2 1/2"; BW Outlet NPT=1 1/4"; BW Outlet Radius=5/8"; BW Outlet Y=14 1/16"; BW Plumbing Total Z=18 1/8"; BW Up=8 7/16"; BW Up Radius=5/8"; BW X=10 7/8"; BW Z=8 5/16"; Boiler Water Flow Rate at 180F=38 GPM; Cold Water Extension=5 5/16"; Cold Water Inlet Z=5 5/8"; Cold Water NPT=2"; Cold Water Radius=1"; Control Enclosure Location=20"; Control Panel Extension=29 3/4"; Drain Extension=26 5/8"; Drain NPT=1"; Drain Radius=1/2"; Energy Extension=27 13/16"; Flat Side Distance=45 1/2"; Front Skid Extension=77 3/4"; Height to Drain=1 3/4"; Height to Energy=28 11/16"; Height to Hot Outlet=68 1/8"; Height to Relief=68 11/16"; Hot Outlet Angle=90.00°; Hot Outlet Extension=23 3/4"; Hot Outlet NPT=2"; Hot Outlet Offset Horiz=23 3/4"; Hot Outlet Offset Vert=0"; Hot Outlet Radius=1"; Rear Skid Extension=22 3/4"; Recovery Rate 40F to 140F (GPH)=440; Relief Valve Extension=25 3/4"; Skid Length=55"; Skid Spacing=27"; U Tube Extension=9 13/16"; U Tube Radius=4 5/16"; Unit Height=85 1/8"; Unit Radius=22 3/4"; Weight=1430
- 900 L 300A-QWD: BW Inlet Conn X=2 1/2"; BW Inlet NPT=1 1/4"; BW Inlet Radius=5/8"; BW Inlet Y=6 3/4"; BW Outlet Conn X=2 1/2"; BW Outlet NPT=1 1/4"; BW Outlet Radius=5/8"; BW Outlet Y=14 1/16"; BW Plumbing Total Z=18 1/8"; BW Up=8 7/16"; BW Up Radius=5/8"; BW X=10 7/8"; BW Z=8 5/16"; Boiler Water Flow Rate at 180F=38 GPM; Cold Water Extension=5 5/16"; Cold Water Inlet Z=5 5/8"; Cold Water NPT=2"; Cold Water Radius=1"; Control Enclosure Location=20"; Control Panel Extension=29 3/4"; Drain Extension=26 5/8"; Drain NPT=1"; Drain Radius=1/2"; Energy Extension=27 13/16"; Flat Side Distance=45 1/2"; Front Skid Extension=77 3/4"; Height to Drain=1 3/4"; Height to Energy=28 11/16"; Height to Hot Outlet=50 3/8"; Height to Relief=56 3/4"; Hot Outlet Angle=0.00°; Hot Outlet Extension=23 3/4"; Hot Outlet NPT=2"; Hot Outlet Offset Horiz=0"; Hot Outlet Offset Vert=23 3/4"; Hot Outlet Radius=1"; Rear Skid Extension=22 3/4"; Recovery Rate 40F to 140F (GPH)=440; Relief Valve Extension=25 3/4"; Skid Length=55"; Skid Spacing=27"; U Tube Extension=9 13/16"; U Tube Radius=4 5/16"; Unit Height=73 1/8"; Unit Radius=22 3/4"; Weight=1340
- 900 L 250A-QWD: BW Inlet Conn X=2 1/2"; BW Inlet NPT=1 1/4"; BW Inlet Radius=5/8"; BW Inlet Y=6 3/4"; BW Outlet Conn X=2 1/2"; BW Outlet NPT=1 1/4"; BW Outlet Radius=5/8"; BW Outlet Y=14 1/16"; BW Plumbing Total Z=20 7/16"; BW Up=8 7/16"; BW Up Radius=5/8"; BW X=10 7/8"; BW Z=8 5/16"; Boiler Water Flow Rate at 180F=38 GPM; Cold Water Extension=5 5/16"; Cold Water Inlet Z=5 5/8"; Cold Water NPT=2"; Cold Water Radius=1"; Control Enclosure Location=15 1/2"; Control Panel Extension=29 3/4"; Drain Extension=26 5/8"; Drain NPT=1"; Drain Radius=1/2"; Energy Extension=38 13/16"; Flat Side Distance=45 1/2"; Front Skid Extension=77 3/4"; Height to Drain=1 3/4"; Height to Energy=28 11/16"; Height to Hot Outlet=38 3/8"; Height to Relief=44 3/4"; Hot Outlet Angle=0.00°; Hot Outlet Extension=23 3/4"; Hot Outlet NPT=2"; Hot Outlet Offset Horiz=0"; Hot Outlet Offset Vert=23 3/4"; Hot Outlet Radius=1"; Rear Skid Extension=22 3/4"; Recovery Rate 40F to 140F (GPH)=440; Relief Valve Extension=25 3/4"; Skid Length=55"; Skid Spacing=27"; U Tube Extension=12 1/8"; U Tube Radius=4 5/16"; Unit Height=61 1/8"; Unit Radius=22 3/4"; Weight=1280
- 8200 L 400A-QW: BW Inlet Conn X=4 9/16"; BW Inlet NPT=4"; BW Inlet Radius=2"; BW Inlet Y=18 11/16"; BW Outlet Conn X=4 9/16"; BW Outlet NPT=4"; BW Outlet Radius=2"; BW Outlet Y=33 11/16"; BW Plumbing Total Z=20 15/16"; BW Up=17 9/16"; BW Up Radius=2"; BW X=24 1/16"; BW Z=7 1/2"; Boiler Water Flow Rate at 180F=322 GPM; Cold Water Extension=9"; Cold Water Inlet Z=5"; Cold Water NPT=2 1/2"; Cold Water Radius=1 1/4"; Control Enclosure Location=20"; Control Panel Extension=29 3/4"; Drain Extension=26 5/8"; Drain NPT=1"; Drain Radius=1/2"; Energy Extension=38 13/16"; Flat Side Distance=45 1/2"; Front Skid Extension=77 3/4"; Height to Drain=1 3/4"; Height to Energy=28 11/16"; Height to Hot Outlet=68 1/8"; Height to Relief=68 11/16"; Hot Outlet Angle=90.00°; Hot Outlet Extension=23 3/4"; Hot Outlet NPT=2"; Hot Outlet Offset Horiz=23 3/4"; Hot Outlet Offset Vert=0"; Hot Outlet Radius=1"; Rear Skid Extension=22 3/4"; Recovery Rate 40F to 140F (GPH)=3800; Relief Valve Extension=25 3/4"; Skid Length=55"; Skid Spacing=27"; U Tube Extension=13 7/16"; U Tube Radius=8"; Unit Height=85 1/8"; Unit Radius=22 3/4"; Weight=2060
- 8200 L 300A-QW: BW Inlet Conn X=4 9/16"; BW Inlet NPT=4"; BW Inlet Radius=2"; BW Inlet Y=18 11/16"; BW Outlet Conn X=4 9/16"; BW Outlet NPT=4"; BW Outlet Radius=2"; BW Outlet Y=33 11/16"; BW Plumbing Total Z=20 15/16"; BW Up=17 9/16"; BW Up Radius=2"; BW X=24 1/16"; BW Z=7 1/2"; Boiler Water Flow Rate at 180F=322 GPM; Cold Water Extension=9"; Cold Water Inlet Z=5"; Cold Water NPT=2 1/2"; Cold Water Radius=1 1/4"; Control Enclosure Location=20"; Control Panel Extension=29 3/4"; Drain Extension=26 5/8"; Drain NPT=1"; Drain Radius=1/2"; Energy Extension=38 13/16"; Flat Side Distance=45 1/2"; Front Skid Extension=77 3/4"; Height to Drain=1 3/4"; Height to Energy=28 11/16"; Height to Hot Outlet=50 3/8"; Height to Relief=56 3/4"; Hot Outlet Angle=0.00°; Hot Outlet Extension=23 3/4"; Hot Outlet NPT=2"; Hot Outlet Offset Horiz=0"; Hot Outlet Offset Vert=23 3/4"; Hot Outlet Radius=1"; Rear Skid Extension=22 3/4"; Recovery Rate 40F to 140F (GPH)=3800; Relief Valve Extension=25 3/4"; Skid Length=55"; Skid Spacing=27"; U Tube Extension=13 7/16"; U Tube Radius=8"; Unit Height=73 1/8"; Unit Radius=22 3/4"; Weight=1980
- 8200 L 250A-QW: BW Inlet Conn X=4 9/16"; BW Inlet NPT=4"; BW Inlet Radius=2"; BW Inlet Y=18 11/16"; BW Outlet Conn X=4 9/16"; BW Outlet NPT=4"; BW Outlet Radius=2"; BW Outlet Y=33 11/16"; BW Plumbing Total Z=24 3/8"; BW Up=17 9/16"; BW Up Radius=2"; BW X=24 1/16"; BW Z=7 1/2"; Boiler Water Flow Rate at 180F=322 GPM; Cold Water Extension=9"; Cold Water Inlet Z=5"; Cold Water NPT=2 1/2"; Cold Water Radius=1 1/4"; Control Enclosure Location=15 1/2"; Control Panel Extension=29 3/4"; Drain Extension=26 5/8"; Drain NPT=1"; Drain Radius=1/2"; Energy Extension=38 13/16"; Flat Side Distance=45 1/2"; Front Skid Extension=77 3/4"; Height to Drain=1 3/4"; Height to Energy=28 11/16"; Height to Hot Outlet=38 3/8"; Height to Relief=44 3/4"; Hot Outlet Angle=0.00°; Hot Outlet Extension=23 3/4"; Hot Outlet NPT=2"; Hot Outlet Offset Horiz=0"; Hot Outlet Offset Vert=23 3/4"; Hot Outlet Radius=1"; Rear Skid Extension=22 3/4"; Recovery Rate 40F to 140F (GPH)=3800; Relief Valve Extension=25 3/4"; Skid Length=55"; Skid Spacing=27"; U Tube Extension=16 7/8"; U Tube Radius=8"; Unit Height=61 1/8"; Unit Radius=22 3/4"; Weight=1920
- 800 L 400A-QW: BW Inlet Conn X=1 7/8"; BW Inlet NPT=1 1/4"; BW Inlet Radius=5/8"; BW Inlet Y=6 3/4"; BW Outlet Conn X=1 7/8"; BW Outlet NPT=1 1/4"; BW Outlet Radius=5/8"; BW Outlet Y=14 1/16"; BW Plumbing Total Z=18 1/8"; BW Up=8 7/16"; BW Up Radius=5/8"; BW X=10 7/8"; BW Z=8 5/16"; Boiler Water Flow Rate at 180F=32 GPM; Cold Water Extension=4 5/16"; Cold Water Inlet Z=5 5/8"; Cold Water NPT=2"; Cold Water Radius=1"; Control Enclosure Location=20"; Control Panel Extension=29 3/4"; Drain Extension=26 5/8"; Drain NPT=1"; Drain Radius=1/2"; Energy Extension=27 13/16"; Flat Side Distance=45 1/2"; Front Skid Extension=68 3/4"; Height to Drain=1 3/4"; Height to Energy=28 11/16"; Height to Hot Outlet=68 1/8"; Height to Relief=68 11/16"; Hot Outlet Angle=90.00°; Hot Outlet Extension=23 3/4"; Hot Outlet NPT=2"; Hot Outlet Offset Horiz=23 3/4"; Hot Outlet Offset Vert=0"; Hot Outlet Radius=1"; Rear Skid Extension=22 3/4"; Recovery Rate 40F to 140F (GPH)=380; Relief Valve Extension=25 3/4"; Skid Length=46"; Skid Spacing=27"; U Tube Extension=9 13/16"; U Tube Radius=3 5/16"; Unit Height=85 1/8"; Unit Radius=22 3/4"; Weight=1380
- 800 L 300A-QW: BW Inlet Conn X=1 7/8"; BW Inlet NPT=1 1/4"; BW Inlet Radius=5/8"; BW Inlet Y=6 3/4"; BW Outlet Conn X=1 7/8"; BW Outlet NPT=1 1/4"; BW Outlet Radius=5/8"; BW Outlet Y=14 1/16"; BW Plumbing Total Z=18 1/8"; BW Up=8 7/16"; BW Up Radius=5/8"; BW X=10 7/8"; BW Z=8 5/16"; Boiler Water Flow Rate at 180F=32 GPM; Cold Water Extension=4 5/16"; Cold Water Inlet Z=5 5/8"; Cold Water NPT=2"; Cold Water Radius=1"; Control Enclosure Location=20"; Control Panel Extension=29 3/4"; Drain Extension=26 5/8"; Drain NPT=1"; Drain Radius=1/2"; Energy Extension=27 13/16"; Flat Side Distance=45 1/2"; Front Skid Extension=68 3/4"; Height to Drain=1 3/4"; Height to Energy=28 11/16"; Height to Hot Outlet=50 3/8"; Height to Relief=56 3/4"; Hot Outlet Angle=0.00°; Hot Outlet Extension=23 3/4"; Hot Outlet NPT=2"; Hot Outlet Offset Horiz=0"; Hot Outlet Offset Vert=23 3/4"; Hot Outlet Radius=1"; Rear Skid Extension=22 3/4"; Recovery Rate 40F to 140F (GPH)=380; Relief Valve Extension=25 3/4"; Skid Length=46"; Skid Spacing=27"; U Tube Extension=9 13/16"; U Tube Radius=3 5/16"; Unit Height=73 1/8"; Unit Radius=22 3/4"; Weight=1290
- 800 L 250A-QW: BW Inlet Conn X=1 7/8"; BW Inlet NPT=1 1/4"; BW Inlet Radius=5/8"; BW Inlet Y=6 3/4"; BW Outlet Conn X=1 7/8"; BW Outlet NPT=1 1/4"; BW Outlet Radius=5/8"; BW Outlet Y=14 1/16"; BW Plumbing Total Z=20 7/16"; BW Up=8 7/16"; BW Up Radius=5/8"; BW X=10 7/8"; BW Z=8 5/16"; Boiler Water Flow Rate at 180F=32 GPM; Cold Water Extension=4 5/16"; Cold Water Inlet Z=5 5/8"; Cold Water NPT=2"; Cold Water Radius=1"; Control Enclosure Location=15 1/2"; Control Panel Extension=29 3/4"; Drain Extension=26 5/8"; Drain NPT=1"; Drain Radius=1/2"; Energy Extension=27 13/16"; Flat Side Distance=45 1/2"; Front Skid Extension=68 3/4"; Height to Drain=1 3/4"; Height to Energy=28 11/16"; Height to Hot Outlet=38 3/8"; Height to Relief=44 3/4"; Hot Outlet Angle=0.00°; Hot Outlet Extension=23 3/4"; Hot Outlet NPT=2"; Hot Outlet Offset Horiz=0"; Hot Outlet Offset Vert=23 3/4"; Hot Outlet Radius=1"; Rear Skid Extension=22 3/4"; Recovery Rate 40F to 140F (GPH)=380; Relief Valve Extension=25 3/4"; Skid Length=46"; Skid Spacing=27"; U Tube Extension=12 1/8"; U Tube Radius=3 5/16"; Unit Height=61 1/8"; Unit Radius=22 3/4"; Weight=1230
- 700 L 400A-QWD: BW Inlet Conn X=2 1/2"; BW Inlet NPT=1 1/4"; BW Inlet Radius=5/8"; BW Inlet Y=6 3/4"; BW Outlet Conn X=2 1/2"; BW Outlet NPT=1 1/4"; BW Outlet Radius=5/8"; BW Outlet Y=14 1/16"; BW Plumbing Total Z=18 1/8"; BW Up=8 7/16"; BW Up Radius=5/8"; BW X=10 7/8"; BW Z=8 5/16"; Boiler Water Flow Rate at 180F=29 GPM; Cold Water Extension=5 5/16"; Cold Water Inlet Z=5 5/8"; Cold Water NPT=2"; Cold Water Radius=1"; Control Enclosure Location=20"; Control Panel Extension=29 3/4"; Drain Extension=26 5/8"; Drain NPT=1"; Drain Radius=1/2"; Energy Extension=27 13/16"; Flat Side Distance=45 1/2"; Front Skid Extension=68 3/4"; Height to Drain=1 3/4"; Height to Energy=28 11/16"; Height to Hot Outlet=68 1/8"; Height to Relief=68 11/16"; Hot Outlet Angle=90.00°; Hot Outlet Extension=23 3/4"; Hot Outlet NPT=2"; Hot Outlet Offset Horiz=23 3/4"; Hot Outlet Offset Vert=0"; Hot Outlet Radius=1"; Rear Skid Extension=22 3/4"; Recovery Rate 40F to 140F (GPH)=340; Relief Valve Extension=25 3/4"; Skid Length=46"; Skid Spacing=27"; U Tube Extension=9 13/16"; U Tube Radius=4 5/16"; Unit Height=85 1/8"; Unit Radius=22 3/4"; Weight=1400
- 700 L 300A-QWD: BW Inlet Conn X=2 1/2"; BW Inlet NPT=1 1/4"; BW Inlet Radius=5/8"; BW Inlet Y=6 3/4"; BW Outlet Conn X=2 1/2"; BW Outlet NPT=1 1/4"; BW Outlet Radius=5/8"; BW Outlet Y=14 1/16"; BW Plumbing Total Z=18 1/8"; BW Up=8 7/16"; BW Up Radius=5/8"; BW X=10 7/8"; BW Z=8 5/16"; Boiler Water Flow Rate at 180F=29 GPM; Cold Water Extension=5 5/16"; Cold Water Inlet Z=5 5/8"; Cold Water NPT=2"; Cold Water Radius=1"; Control Enclosure Location=20"; Control Panel Extension=29 3/4"; Drain Extension=26 5/8"; Drain NPT=1"; Drain Radius=1/2"; Energy Extension=27 13/16"; Flat Side Distance=45 1/2"; Front Skid Extension=68 3/4"; Height to Drain=1 3/4"; Height to Energy=28 11/16"; Height to Hot Outlet=50 3/8"; Height to Relief=56 3/4"; Hot Outlet Angle=0.00°; Hot Outlet Extension=23 3/4"; Hot Outlet NPT=2"; Hot Outlet Offset Horiz=0"; Hot Outlet Offset Vert=23 3/4"; Hot Outlet Radius=1"; Rear Skid Extension=22 3/4"; Recovery Rate 40F to 140F (GPH)=340; Relief Valve Extension=25 3/4"; Skid Length=46"; Skid Spacing=27"; U Tube Extension=9 13/16"; U Tube Radius=4 5/16"; Unit Height=73 1/8"; Unit Radius=22 3/4"; Weight=1310
- 700 L 250A-QWD: BW Inlet Conn X=2 1/2"; BW Inlet NPT=1 1/4"; BW Inlet Radius=5/8"; BW Inlet Y=6 3/4"; BW Outlet Conn X=2 1/2"; BW Outlet NPT=1 1/4"; BW Outlet Radius=5/8"; BW Outlet Y=14 1/16"; BW Plumbing Total Z=20 7/16"; BW Up=8 7/16"; BW Up Radius=5/8"; BW X=10 7/8"; BW Z=8 5/16"; Boiler Water Flow Rate at 180F=29 GPM; Cold Water Extension=5 5/16"; Cold Water Inlet Z=5 5/8"; Cold Water NPT=2"; Cold Water Radius=1"; Control Enclosure Location=15 1/2"; Control Panel Extension=29 3/4"; Drain Extension=26 5/8"; Drain NPT=1"; Drain Radius=1/2"; Energy Extension=27 13/16"; Flat Side Distance=45 1/2"; Front Skid Extension=68 3/4"; Height to Drain=1 3/4"; Height to Energy=28 11/16"; Height to Hot Outlet=38 3/8"; Height to Relief=44 3/4"; Hot Outlet Angle=0.00°; Hot Outlet Extension=23 3/4"; Hot Outlet NPT=2"; Hot Outlet Offset Horiz=0"; Hot Outlet Offset Vert=23 3/4"; Hot Outlet Radius=1"; Rear Skid Extension=22 3/4"; Recovery Rate 40F to 140F (GPH)=340; Relief Valve Extension=25 3/4"; Skid Length=46"; Skid Spacing=27"; U Tube Extension=12 1/8"; U Tube Radius=4 5/16"; Unit Height=61 1/8"; Unit Radius=22 3/4"; Weight=1250
- 6900 L 400A-QWD: BW Inlet Conn X=4 9/16"; BW Inlet NPT=4"; BW Inlet Radius=2"; BW Inlet Y=18 11/16"; BW Outlet Conn X=4 9/16"; BW Outlet NPT=4"; BW Outlet Radius=2"; BW Outlet Y=33 11/16"; BW Plumbing Total Z=20 15/16"; BW Up=17 9/16"; BW Up Radius=2"; BW X=24 1/16"; BW Z=7 1/2"; Boiler Water Flow Rate at 180F=286 GPM; Cold Water Extension=9"; Cold Water Inlet Z=5"; Cold Water NPT=2 1/2"; Cold Water Radius=1 1/4"; Control Enclosure Location=20"; Control Panel Extension=29 3/4"; Drain Extension=26 5/8"; Drain NPT=1"; Drain Radius=1/2"; Energy Extension=38 13/16"; Flat Side Distance=45 1/2"; Front Skid Extension=77 3/4"; Height to Drain=1 3/4"; Height to Energy=28 11/16"; Height to Hot Outlet=68 1/8"; Height to Relief=68 11/16"; Hot Outlet Angle=90.00°; Hot Outlet Extension=23 3/4"; Hot Outlet NPT=2"; Hot Outlet Offset Horiz=23 3/4"; Hot Outlet Offset Vert=0"; Hot Outlet Radius=1"; Rear Skid Extension=22 3/4"; Recovery Rate 40F to 140F (GPH)=3370; Relief Valve Extension=25 3/4"; Skid Length=55"; Skid Spacing=27"; U Tube Extension=13 7/16"; U Tube Radius=8"; Unit Height=85 1/8"; Unit Radius=22 3/4"; Weight=2360
- 6900 L 300A-QWD: BW Inlet Conn X=4 9/16"; BW Inlet NPT=4"; BW Inlet Radius=2"; BW Inlet Y=18 11/16"; BW Outlet Conn X=4 9/16"; BW Outlet NPT=4"; BW Outlet Radius=2"; BW Outlet Y=33 11/16"; BW Plumbing Total Z=20 15/16"; BW Up=17 9/16"; BW Up Radius=2"; BW X=24 1/16"; BW Z=7 1/2"; Boiler Water Flow Rate at 180F=286 GPM; Cold Water Extension=9"; Cold Water Inlet Z=5"; Cold Water NPT=2 1/2"; Cold Water Radius=1 1/4"; Control Enclosure Location=20"; Control Panel Extension=29 3/4"; Drain Extension=26 5/8"; Drain NPT=1"; Drain Radius=1/2"; Energy Extension=38 13/16"; Flat Side Distance=45 1/2"; Front Skid Extension=77 3/4"; Height to Drain=1 3/4"; Height to Energy=28 11/16"; Height to Hot Outlet=50 3/8"; Height to Relief=56 3/4"; Hot Outlet Angle=0.00°; Hot Outlet Extension=23 3/4"; Hot Outlet NPT=2"; Hot Outlet Offset Horiz=0"; Hot Outlet Offset Vert=23 3/4"; Hot Outlet Radius=1"; Rear Skid Extension=22 3/4"; Recovery Rate 40F to 140F (GPH)=3370; Relief Valve Extension=25 3/4"; Skid Length=55"; Skid Spacing=27"; U Tube Extension=13 7/16"; U Tube Radius=8"; Unit Height=73 1/8"; Unit Radius=22 3/4"; Weight=2280
- 6900 L 250A-QWD: BW Inlet Conn X=4 9/16"; BW Inlet NPT=4"; BW Inlet Radius=2"; BW Inlet Y=18 11/16"; BW Outlet Conn X=4 9/16"; BW Outlet NPT=4"; BW Outlet Radius=2"; BW Outlet Y=33 11/16"; BW Plumbing Total Z=24 3/8"; BW Up=17 9/16"; BW Up Radius=2"; BW X=24 1/16"; BW Z=7 1/2"; Boiler Water Flow Rate at 180F=286 GPM; Cold Water Extension=9"; Cold Water Inlet Z=5"; Cold Water NPT=2 1/2"; Cold Water Radius=1 1/4"; Control Enclosure Location=15 1/2"; Control Panel Extension=29 3/4"; Drain Extension=26 5/8"; Drain NPT=1"; Drain Radius=1/2"; Energy Extension=38 13/16"; Flat Side Distance=45 1/2"; Front Skid Extension=77 3/4"; Height to Drain=1 3/4"; Height to Energy=28 11/16"; Height to Hot Outlet=38 3/8"; Height to Relief=44 3/4"; Hot Outlet Angle=0.00°; Hot Outlet Extension=23 3/4"; Hot Outlet NPT=2"; Hot Outlet Offset Horiz=0"; Hot Outlet Offset Vert=23 3/4"; Hot Outlet Radius=1"; Rear Skid Extension=22 3/4"; Recovery Rate 40F to 140F (GPH)=3370; Relief Valve Extension=25 3/4"; Skid Length=55"; Skid Spacing=27"; U Tube Extension=16 7/8"; U Tube Radius=8"; Unit Height=61 1/8"; Unit Radius=22 3/4"; Weight=2220
- 6300 L 400A-QW: BW Inlet Conn X=4"; BW Inlet NPT=4"; BW Inlet Radius=2"; BW Inlet Y=18 11/16"; BW Outlet Conn X=4"; BW Outlet NPT=4"; BW Outlet Radius=2"; BW Outlet Y=33 11/16"; BW Plumbing Total Z=21 3/16"; BW Up=17"; BW Up Radius=2"; BW X=23 1/2"; BW Z=7 1/2"; Boiler Water Flow Rate at 180F=251 GPM; Cold Water Extension=8"; Cold Water Inlet Z=4 1/2"; Cold Water NPT=2 1/2"; Cold Water Radius=1 1/4"; Control Enclosure Location=20"; Control Panel Extension=29 3/4"; Drain Extension=26 5/8"; Drain NPT=1"; Drain Radius=1/2"; Energy Extension=38 13/16"; Flat Side Distance=45 1/2"; Front Skid Extension=77 3/4"; Height to Drain=1 3/4"; Height to Energy=28 11/16"; Height to Hot Outlet=68 1/8"; Height to Relief=68 11/16"; Hot Outlet Angle=90.00°; Hot Outlet Extension=23 3/4"; Hot Outlet NPT=2"; Hot Outlet Offset Horiz=23 3/4"; Hot Outlet Offset Vert=0"; Hot Outlet Radius=1"; Rear Skid Extension=22 3/4"; Recovery Rate 40F to 140F (GPH)=2960; Relief Valve Extension=25 3/4"; Skid Length=55"; Skid Spacing=27"; U Tube Extension=13 11/16"; U Tube Radius=7"; Unit Height=85 1/8"; Unit Radius=22 3/4"; Weight=1900
- 6300 L 300A-QW: BW Inlet Conn X=4"; BW Inlet NPT=4"; BW Inlet Radius=2"; BW Inlet Y=18 11/16"; BW Outlet Conn X=4"; BW Outlet NPT=4"; BW Outlet Radius=2"; BW Outlet Y=33 11/16"; BW Plumbing Total Z=21 3/16"; BW Up=17"; BW Up Radius=2"; BW X=23 1/2"; BW Z=7 1/2"; Boiler Water Flow Rate at 180F=251 GPM; Cold Water Extension=8"; Cold Water Inlet Z=4 1/2"; Cold Water NPT=2 1/2"; Cold Water Radius=1 1/4"; Control Enclosure Location=20"; Control Panel Extension=29 3/4"; Drain Extension=26 5/8"; Drain NPT=1"; Drain Radius=1/2"; Energy Extension=38 13/16"; Flat Side Distance=45 1/2"; Front Skid Extension=77 3/4"; Height to Drain=1 3/4"; Height to Energy=28 11/16"; Height to Hot Outlet=50 3/8"; Height to Relief=56 3/4"; Hot Outlet Angle=0.00°; Hot Outlet Extension=23 3/4"; Hot Outlet NPT=2"; Hot Outlet Offset Horiz=0"; Hot Outlet Offset Vert=23 3/4"; Hot Outlet Radius=1"; Rear Skid Extension=22 3/4"; Recovery Rate 40F to 140F (GPH)=2960; Relief Valve Extension=25 3/4"; Skid Length=55"; Skid Spacing=27"; U Tube Extension=13 11/16"; U Tube Radius=7"; Unit Height=73 1/8"; Unit Radius=22 3/4"; Weight=1810
- 6300 L 250A-QW: BW Inlet Conn X=4"; BW Inlet NPT=4"; BW Inlet Radius=2"; BW Inlet Y=18 11/16"; BW Outlet Conn X=4"; BW Outlet NPT=4"; BW Outlet Radius=2"; BW Outlet Y=33 11/16"; BW Plumbing Total Z=23 7/8"; BW Up=17"; BW Up Radius=2"; BW X=23 1/2"; BW Z=7 1/2"; Boiler Water Flow Rate at 180F=251 GPM; Cold Water Extension=8"; Cold Water Inlet Z=4 1/2"; Cold Water NPT=2 1/2"; Cold Water Radius=1 1/4"; Control Enclosure Location=15 1/2"; Control Panel Extension=29 3/4"; Drain Extension=26 5/8"; Drain NPT=1"; Drain Radius=1/2"; Energy Extension=38 13/16"; Flat Side Distance=45 1/2"; Front Skid Extension=77 3/4"; Height to Drain=1 3/4"; Height to Energy=28 11/16"; Height to Hot Outlet=38 3/8"; Height to Relief=44 3/4"; Hot Outlet Angle=0.00°; Hot Outlet Extension=23 3/4"; Hot Outlet NPT=2"; Hot Outlet Offset Horiz=0"; Hot Outlet Offset Vert=23 3/4"; Hot Outlet Radius=1"; Rear Skid Extension=22 3/4"; Recovery Rate 40F to 140F (GPH)=2960; Relief Valve Extension=25 3/4"; Skid Length=55"; Skid Spacing=27"; U Tube Extension=16 3/8"; U Tube Radius=7"; Unit Height=61 1/8"; Unit Radius=22 3/4"; Weight=1750
- 6100 L 400A-QWD: BW Inlet Conn X=4 9/16"; BW Inlet NPT=4"; BW Inlet Radius=2"; BW Inlet Y=18 11/16"; BW Outlet Conn X=4 9/16"; BW Outlet NPT=4"; BW Outlet Radius=2"; BW Outlet Y=33 11/16"; BW Plumbing Total Z=20 15/16"; BW Up=17 9/16"; BW Up Radius=2"; BW X=24 1/16"; BW Z=7 1/2"; Boiler Water Flow Rate at 180F=249 GPM; Cold Water Extension=9"; Cold Water Inlet Z=5"; Cold Water NPT=2 1/2"; Cold Water Radius=1 1/4"; Control Enclosure Location=20"; Control Panel Extension=29 3/4"; Drain Extension=26 5/8"; Drain NPT=1"; Drain Radius=1/2"; Energy Extension=27 13/16"; Flat Side Distance=45 1/2"; Front Skid Extension=77 3/4"; Height to Drain=1 3/4"; Height to Energy=28 11/16"; Height to Hot Outlet=68 1/8"; Height to Relief=68 11/16"; Hot Outlet Angle=90.00°; Hot Outlet Extension=23 3/4"; Hot Outlet NPT=2"; Hot Outlet Offset Horiz=23 3/4"; Hot Outlet Offset Vert=0"; Hot Outlet Radius=1"; Rear Skid Extension=22 3/4"; Recovery Rate 40F to 140F (GPH)=2930; Relief Valve Extension=25 3/4"; Skid Length=55"; Skid Spacing=27"; U Tube Extension=13 7/16"; U Tube Radius=8"; Unit Height=85 1/8"; Unit Radius=22 3/4"; Weight=2290
- 6100 L 300A-QWD: BW Inlet Conn X=4 9/16"; BW Inlet NPT=4"; BW Inlet Radius=2"; BW Inlet Y=18 11/16"; BW Outlet Conn X=4 9/16"; BW Outlet NPT=4"; BW Outlet Radius=2"; BW Outlet Y=33 11/16"; BW Plumbing Total Z=20 15/16"; BW Up=17 9/16"; BW Up Radius=2"; BW X=24 1/16"; BW Z=7 1/2"; Boiler Water Flow Rate at 180F=249 GPM; Cold Water Extension=9"; Cold Water Inlet Z=5"; Cold Water NPT=2 1/2"; Cold Water Radius=1 1/4"; Control Enclosure Location=20"; Control Panel Extension=29 3/4"; Drain Extension=26 5/8"; Drain NPT=1"; Drain Radius=1/2"; Energy Extension=27 13/16"; Flat Side Distance=45 1/2"; Front Skid Extension=77 3/4"; Height to Drain=1 3/4"; Height to Energy=28 11/16"; Height to Hot Outlet=50 3/8"; Height to Relief=56 3/4"; Hot Outlet Angle=0.00°; Hot Outlet Extension=23 3/4"; Hot Outlet NPT=2"; Hot Outlet Offset Horiz=0"; Hot Outlet Offset Vert=23 3/4"; Hot Outlet Radius=1"; Rear Skid Extension=22 3/4"; Recovery Rate 40F to 140F (GPH)=2930; Relief Valve Extension=25 3/4"; Skid Length=55"; Skid Spacing=27"; U Tube Extension=13 7/16"; U Tube Radius=8"; Unit Height=73 1/8"; Unit Radius=22 3/4"; Weight=2200
- 6100 L 250A-QWD: BW Inlet Conn X=4 9/16"; BW Inlet NPT=4"; BW Inlet Radius=2"; BW Inlet Y=18 11/16"; BW Outlet Conn X=4 9/16"; BW Outlet NPT=4"; BW Outlet Radius=2"; BW Outlet Y=33 11/16"; BW Plumbing Total Z=24 3/8"; BW Up=17 9/16"; BW Up Radius=2"; BW X=24 1/16"; BW Z=7 1/2"; Boiler Water Flow Rate at 180F=249 GPM; Cold Water Extension=9"; Cold Water Inlet Z=5"; Cold Water NPT=2 1/2"; Cold Water Radius=1 1/4"; Control Enclosure Location=15 1/2"; Control Panel Extension=29 3/4"; Drain Extension=26 5/8"; Drain NPT=1"; Drain Radius=1/2"; Energy Extension=27 13/16"; Flat Side Distance=45 1/2"; Front Skid Extension=77 3/4"; Height to Drain=1 3/4"; Height to Energy=28 11/16"; Height to Hot Outlet=38 3/8"; Height to Relief=44 3/4"; Hot Outlet Angle=0.00°; Hot Outlet Extension=23 3/4"; Hot Outlet NPT=2"; Hot Outlet Offset Horiz=0"; Hot Outlet Offset Vert=23 3/4"; Hot Outlet Radius=1"; Rear Skid Extension=22 3/4"; Recovery Rate 40F to 140F (GPH)=2930; Relief Valve Extension=25 3/4"; Skid Length=55"; Skid Spacing=27"; U Tube Extension=16 7/8"; U Tube Radius=8"; Unit Height=61 1/8"; Unit Radius=22 3/4"; Weight=2140
- 600 L 400A-QW: BW Inlet Conn X=1 5/16"; BW Inlet NPT=1"; BW Inlet Radius=1/2"; BW Inlet Y=5 1/2"; BW Outlet Conn X=1 5/16"; BW Outlet NPT=1"; BW Outlet Radius=1/2"; BW Outlet Y=11 3/16"; BW Plumbing Total Z=15 1/2"; BW Up=5 13/16"; BW Up Radius=1/2"; BW X=7 15/16"; BW Z=6 1/16"; Boiler Water Flow Rate at 180F=23 GPM; Cold Water Extension=3 1/4"; Cold Water Inlet Z=5 5/8"; Cold Water NPT=2"; Cold Water Radius=1"; Control Enclosure Location=20"; Control Panel Extension=29 3/4"; Drain Extension=26 5/8"; Drain NPT=1"; Drain Radius=1/2"; Energy Extension=38 13/16"; Flat Side Distance=45 1/2"; Front Skid Extension=77 3/4"; Height to Drain=1 3/4"; Height to Energy=28 11/16"; Height to Hot Outlet=68 1/8"; Height to Relief=68 11/16"; Hot Outlet Angle=90.00°; Hot Outlet Extension=23 3/4"; Hot Outlet NPT=2"; Hot Outlet Offset Horiz=23 3/4"; Hot Outlet Offset Vert=0"; Hot Outlet Radius=1"; Rear Skid Extension=22 3/4"; Recovery Rate 40F to 140F (GPH)=270; Relief Valve Extension=25 3/4"; Skid Length=55"; Skid Spacing=27"; U Tube Extension=9 7/16"; U Tube Radius=2 1/4"; Unit Height=85 1/8"; Unit Radius=22 3/4"; Weight=1340
- 600 L 300A-QW: BW Inlet Conn X=1 5/16"; BW Inlet NPT=1"; BW Inlet Radius=1/2"; BW Inlet Y=5 1/2"; BW Outlet Conn X=1 5/16"; BW Outlet NPT=1"; BW Outlet Radius=1/2"; BW Outlet Y=11 3/16"; BW Plumbing Total Z=15 1/2"; BW Up=5 13/16"; BW Up Radius=1/2"; BW X=7 15/16"; BW Z=6 1/16"; Boiler Water Flow Rate at 180F=23 GPM; Cold Water Extension=3 1/4"; Cold Water Inlet Z=5 5/8"; Cold Water NPT=2"; Cold Water Radius=1"; Control Enclosure Location=20"; Control Panel Extension=29 3/4"; Drain Extension=26 5/8"; Drain NPT=1"; Drain Radius=1/2"; Energy Extension=38 13/16"; Flat Side Distance=45 1/2"; Front Skid Extension=77 3/4"; Height to Drain=1 3/4"; Height to Energy=28 11/16"; Height to Hot Outlet=50 3/8"; Height to Relief=56 3/4"; Hot Outlet Angle=0.00°; Hot Outlet Extension=23 3/4"; Hot Outlet NPT=2"; Hot Outlet Offset Horiz=0"; Hot Outlet Offset Vert=23 3/4"; Hot Outlet Radius=1"; Rear Skid Extension=22 3/4"; Recovery Rate 40F to 140F (GPH)=270; Relief Valve Extension=25 3/4"; Skid Length=55"; Skid Spacing=27"; U Tube Extension=9 7/16"; U Tube Radius=2 1/4"; Unit Height=73 1/8"; Unit Radius=22 3/4"; Weight=1250
- 600 L 250A-QW: BW Inlet Conn X=1 5/16"; BW Inlet NPT=1"; BW Inlet Radius=1/2"; BW Inlet Y=5 1/2"; BW Outlet Conn X=1 5/16"; BW Outlet NPT=1"; BW Outlet Radius=1/2"; BW Outlet Y=11 3/16"; BW Plumbing Total Z=17 5/16"; BW Up=5 13/16"; BW Up Radius=1/2"; BW X=7 15/16"; BW Z=6 1/16"; Boiler Water Flow Rate at 180F=23 GPM; Cold Water Extension=3 1/4"; Cold Water Inlet Z=5 5/8"; Cold Water NPT=2"; Cold Water Radius=1"; Control Enclosure Location=15 1/2"; Control Panel Extension=29 3/4"; Drain Extension=26 5/8"; Drain NPT=1"; Drain Radius=1/2"; Energy Extension=38 13/16"; Flat Side Distance=45 1/2"; Front Skid Extension=77 3/4"; Height to Drain=1 3/4"; Height to Energy=28 11/16"; Height to Hot Outlet=38 3/8"; Height to Relief=44 3/4"; Hot Outlet Angle=0.00°; Hot Outlet Extension=23 3/4"; Hot Outlet NPT=2"; Hot Outlet Offset Horiz=0"; Hot Outlet Offset Vert=23 3/4"; Hot Outlet Radius=1"; Rear Skid Extension=22 3/4"; Recovery Rate 40F to 140F (GPH)=270; Relief Valve Extension=25 3/4"; Skid Length=55"; Skid Spacing=27"; U Tube Extension=11 1/4"; U Tube Radius=2 1/4"; Unit Height=61 1/8"; Unit Radius=22 3/4"; Weight=1190
- 5400 L 400A-QWD: BW Inlet Conn X=4"; BW Inlet NPT=4"; BW Inlet Radius=2"; BW Inlet Y=18 11/16"; BW Outlet Conn X=4"; BW Outlet NPT=4"; BW Outlet Radius=2"; BW Outlet Y=33 11/16"; BW Plumbing Total Z=21 3/16"; BW Up=17"; BW Up Radius=2"; BW X=23 1/2"; BW Z=7 1/2"; Boiler Water Flow Rate at 180F=222 GPM; Cold Water Extension=8"; Cold Water Inlet Z=4 1/2"; Cold Water NPT=2 1/2"; Cold Water Radius=1 1/4"; Control Enclosure Location=20"; Control Panel Extension=29 3/4"; Drain Extension=26 5/8"; Drain NPT=1"; Drain Radius=1/2"; Energy Extension=38 13/16"; Flat Side Distance=45 1/2"; Front Skid Extension=77 3/4"; Height to Drain=1 3/4"; Height to Energy=28 11/16"; Height to Hot Outlet=68 1/8"; Height to Relief=68 11/16"; Hot Outlet Angle=90.00°; Hot Outlet Extension=23 3/4"; Hot Outlet NPT=2"; Hot Outlet Offset Horiz=23 3/4"; Hot Outlet Offset Vert=0"; Hot Outlet Radius=1"; Rear Skid Extension=22 3/4"; Recovery Rate 40F to 140F (GPH)=2620; Relief Valve Extension=25 3/4"; Skid Length=55"; Skid Spacing=27"; U Tube Extension=13 11/16"; U Tube Radius=7"; Unit Height=85 1/8"; Unit Radius=22 3/4"; Weight=2130
- 5400 L 300A-QWD: BW Inlet Conn X=4"; BW Inlet NPT=4"; BW Inlet Radius=2"; BW Inlet Y=18 11/16"; BW Outlet Conn X=4"; BW Outlet NPT=4"; BW Outlet Radius=2"; BW Outlet Y=33 11/16"; BW Plumbing Total Z=21 3/16"; BW Up=17"; BW Up Radius=2"; BW X=23 1/2"; BW Z=7 1/2"; Boiler Water Flow Rate at 180F=222 GPM; Cold Water Extension=8"; Cold Water Inlet Z=4 1/2"; Cold Water NPT=2 1/2"; Cold Water Radius=1 1/4"; Control Enclosure Location=20"; Control Panel Extension=29 3/4"; Drain Extension=26 5/8"; Drain NPT=1"; Drain Radius=1/2"; Energy Extension=38 13/16"; Flat Side Distance=45 1/2"; Front Skid Extension=77 3/4"; Height to Drain=1 3/4"; Height to Energy=28 11/16"; Height to Hot Outlet=50 3/8"; Height to Relief=56 3/4"; Hot Outlet Angle=0.00°; Hot Outlet Extension=23 3/4"; Hot Outlet NPT=2"; Hot Outlet Offset Horiz=0"; Hot Outlet Offset Vert=23 3/4"; Hot Outlet Radius=1"; Rear Skid Extension=22 3/4"; Recovery Rate 40F to 140F (GPH)=2620; Relief Valve Extension=25 3/4"; Skid Length=55"; Skid Spacing=27"; U Tube Extension=13 11/16"; U Tube Radius=7"; Unit Height=73 1/8"; Unit Radius=22 3/4"; Weight=2040
- 5400 L 250A-QWD: BW Inlet Conn X=4"; BW Inlet NPT=4"; BW Inlet Radius=2"; BW Inlet Y=18 11/16"; BW Outlet Conn X=4"; BW Outlet NPT=4"; BW Outlet Radius=2"; BW Outlet Y=33 11/16"; BW Plumbing Total Z=23 7/8"; BW Up=17"; BW Up Radius=2"; BW X=23 1/2"; BW Z=7 1/2"; Boiler Water Flow Rate at 180F=222 GPM; Cold Water Extension=8"; Cold Water Inlet Z=4 1/2"; Cold Water NPT=2 1/2"; Cold Water Radius=1 1/4"; Control Enclosure Location=15 1/2"; Control Panel Extension=29 3/4"; Drain Extension=26 5/8"; Drain NPT=1"; Drain Radius=1/2"; Energy Extension=38 13/16"; Flat Side Distance=45 1/2"; Front Skid Extension=77 3/4"; Height to Drain=1 3/4"; Height to Energy=28 11/16"; Height to Hot Outlet=38 3/8"; Height to Relief=44 3/4"; Hot Outlet Angle=0.00°; Hot Outlet Extension=23 3/4"; Hot Outlet NPT=2"; Hot Outlet Offset Horiz=0"; Hot Outlet Offset Vert=23 3/4"; Hot Outlet Radius=1"; Rear Skid Extension=22 3/4"; Recovery Rate 40F to 140F (GPH)=2620; Relief Valve Extension=25 3/4"; Skid Length=55"; Skid Spacing=27"; U Tube Extension=16 3/8"; U Tube Radius=7"; Unit Height=61 1/8"; Unit Radius=22 3/4"; Weight=1980
- 500 L 400A-QWD: BW Inlet Conn X=1 5/16"; BW Inlet NPT=1"; BW Inlet Radius=1/2"; BW Inlet Y=5 1/2"; BW Outlet Conn X=1 5/16"; BW Outlet NPT=1"; BW Outlet Radius=1/2"; BW Outlet Y=11 3/16"; BW Plumbing Total Z=15 1/2"; BW Up=5 13/16"; BW Up Radius=1/2"; BW X=7 15/16"; BW Z=6 1/16"; Boiler Water Flow Rate at 180F=20 GPM; Cold Water Extension=3 1/4"; Cold Water Inlet Z=5 5/8"; Cold Water NPT=2"; Cold Water Radius=1"; Control Enclosure Location=20"; Control Panel Extension=29 3/4"; Drain Extension=26 5/8"; Drain NPT=1"; Drain Radius=1/2"; Energy Extension=38 13/16"; Flat Side Distance=45 1/2"; Front Skid Extension=77 3/4"; Height to Drain=1 3/4"; Height to Energy=28 11/16"; Height to Hot Outlet=68 1/8"; Height to Relief=68 11/16"; Hot Outlet Angle=90.00°; Hot Outlet Extension=23 3/4"; Hot Outlet NPT=2"; Hot Outlet Offset Horiz=23 3/4"; Hot Outlet Offset Vert=0"; Hot Outlet Radius=1"; Rear Skid Extension=22 3/4"; Recovery Rate 40F to 140F (GPH)=240; Relief Valve Extension=25 3/4"; Skid Length=55"; Skid Spacing=27"; U Tube Extension=9 7/16"; U Tube Radius=2 1/4"; Unit Height=85 1/8"; Unit Radius=22 3/4"; Weight=1350
- 500 L 300A-QWD: BW Inlet Conn X=1 5/16"; BW Inlet NPT=1"; BW Inlet Radius=1/2"; BW Inlet Y=5 1/2"; BW Outlet Conn X=1 5/16"; BW Outlet NPT=1"; BW Outlet Radius=1/2"; BW Outlet Y=11 3/16"; BW Plumbing Total Z=15 1/2"; BW Up=5 13/16"; BW Up Radius=1/2"; BW X=7 15/16"; BW Z=6 1/16"; Boiler Water Flow Rate at 180F=20 GPM; Cold Water Extension=3 1/4"; Cold Water Inlet Z=5 5/8"; Cold Water NPT=2"; Cold Water Radius=1"; Control Enclosure Location=20"; Control Panel Extension=29 3/4"; Drain Extension=26 5/8"; Drain NPT=1"; Drain Radius=1/2"; Energy Extension=38 13/16"; Flat Side Distance=45 1/2"; Front Skid Extension=77 3/4"; Height to Drain=1 3/4"; Height to Energy=28 11/16"; Height to Hot Outlet=50 3/8"; Height to Relief=56 3/4"; Hot Outlet Angle=0.00°; Hot Outlet Extension=23 3/4"; Hot Outlet NPT=2"; Hot Outlet Offset Horiz=0"; Hot Outlet Offset Vert=23 3/4"; Hot Outlet Radius=1"; Rear Skid Extension=22 3/4"; Recovery Rate 40F to 140F (GPH)=240; Relief Valve Extension=25 3/4"; Skid Length=55"; Skid Spacing=27"; U Tube Extension=9 7/16"; U Tube Radius=2 1/4"; Unit Height=73 1/8"; Unit Radius=22 3/4"; Weight=1270
- 500 L 250A-QWD: BW Inlet Conn X=1 5/16"; BW Inlet NPT=1"; BW Inlet Radius=1/2"; BW Inlet Y=5 1/2"; BW Outlet Conn X=1 5/16"; BW Outlet NPT=1"; BW Outlet Radius=1/2"; BW Outlet Y=11 3/16"; BW Plumbing Total Z=17 5/16"; BW Up=5 13/16"; BW Up Radius=1/2"; BW X=7 15/16"; BW Z=6 1/16"; Boiler Water Flow Rate at 180F=20 GPM; Cold Water Extension=3 1/4"; Cold Water Inlet Z=5 5/8"; Cold Water NPT=2"; Cold Water Radius=1"; Control Enclosure Location=15 1/2"; Control Panel Extension=29 3/4"; Drain Extension=26 5/8"; Drain NPT=1"; Drain Radius=1/2"; Energy Extension=38 13/16"; Flat Side Distance=45 1/2"; Front Skid Extension=77 3/4"; Height to Drain=1 3/4"; Height to Energy=28 11/16"; Height to Hot Outlet=38 3/8"; Height to Relief=44 3/4"; Hot Outlet Angle=0.00°; Hot Outlet Extension=23 3/4"; Hot Outlet NPT=2"; Hot Outlet Offset Horiz=0"; Hot Outlet Offset Vert=23 3/4"; Hot Outlet Radius=1"; Rear Skid Extension=22 3/4"; Recovery Rate 40F to 140F (GPH)=240; Relief Valve Extension=25 3/4"; Skid Length=55"; Skid Spacing=27"; U Tube Extension=11 1/4"; U Tube Radius=2 1/4"; Unit Height=61 1/8"; Unit Radius=22 3/4"; Weight=1210
- 4500 L 400A-QW: BW Inlet Conn X=3 13/16"; BW Inlet NPT=3"; BW Inlet Radius=1 1/2"; BW Inlet Y=18 11/16"; BW Outlet Conn X=3 13/16"; BW Outlet NPT=3"; BW Outlet Radius=1 1/2"; BW Outlet Y=33 11/16"; BW Plumbing Total Z=18 9/16"; BW Up=16 13/16"; BW Up Radius=1 1/2"; BW X=23 5/16"; BW Z=7 1/2"; Boiler Water Flow Rate at 180F=203 GPM; Cold Water Extension=7 3/8"; Cold Water Inlet Z=5"; Cold Water NPT=2 1/2"; Cold Water Radius=1 1/4"; Control Enclosure Location=20"; Control Panel Extension=29 3/4"; Drain Extension=26 5/8"; Drain NPT=1"; Drain Radius=1/2"; Energy Extension=38 13/16"; Flat Side Distance=45 1/2"; Front Skid Extension=77 3/4"; Height to Drain=1 3/4"; Height to Energy=28 11/16"; Height to Hot Outlet=68 1/8"; Height to Relief=68 11/16"; Hot Outlet Angle=90.00°; Hot Outlet Extension=23 3/4"; Hot Outlet NPT=2"; Hot Outlet Offset Horiz=23 3/4"; Hot Outlet Offset Vert=0"; Hot Outlet Radius=1"; Rear Skid Extension=22 3/4"; Recovery Rate 40F to 140F (GPH)=2390; Relief Valve Extension=25 3/4"; Skid Length=55"; Skid Spacing=27"; U Tube Extension=11 1/16"; U Tube Radius=6 3/8"; Unit Height=85 1/8"; Unit Radius=22 3/4"; Weight=1800
- 4500 L 300A-QW: BW Inlet Conn X=3 13/16"; BW Inlet NPT=3"; BW Inlet Radius=1 1/2"; BW Inlet Y=18 11/16"; BW Outlet Conn X=3 13/16"; BW Outlet NPT=3"; BW Outlet Radius=1 1/2"; BW Outlet Y=33 11/16"; BW Plumbing Total Z=18 9/16"; BW Up=16 13/16"; BW Up Radius=1 1/2"; BW X=23 5/16"; BW Z=7 1/2"; Boiler Water Flow Rate at 180F=203 GPM; Cold Water Extension=7 3/8"; Cold Water Inlet Z=5"; Cold Water NPT=2 1/2"; Cold Water Radius=1 1/4"; Control Enclosure Location=20"; Control Panel Extension=29 3/4"; Drain Extension=26 5/8"; Drain NPT=1"; Drain Radius=1/2"; Energy Extension=38 13/16"; Flat Side Distance=45 1/2"; Front Skid Extension=77 3/4"; Height to Drain=1 3/4"; Height to Energy=28 11/16"; Height to Hot Outlet=50 3/8"; Height to Relief=56 3/4"; Hot Outlet Angle=0.00°; Hot Outlet Extension=23 3/4"; Hot Outlet NPT=2"; Hot Outlet Offset Horiz=0"; Hot Outlet Offset Vert=23 3/4"; Hot Outlet Radius=1"; Rear Skid Extension=22 3/4"; Recovery Rate 40F to 140F (GPH)=2390; Relief Valve Extension=25 3/4"; Skid Length=55"; Skid Spacing=27"; U Tube Extension=11 1/16"; U Tube Radius=6 3/8"; Unit Height=73 1/8"; Unit Radius=22 3/4"; Weight=1720
- 4500 L 250A-QW: BW Inlet Conn X=3 13/16"; BW Inlet NPT=3"; BW Inlet Radius=1 1/2"; BW Inlet Y=18 11/16"; BW Outlet Conn X=3 13/16"; BW Outlet NPT=3"; BW Outlet Radius=1 1/2"; BW Outlet Y=33 11/16"; BW Plumbing Total Z=20 3/4"; BW Up=16 13/16"; BW Up Radius=1 1/2"; BW X=23 5/16"; BW Z=7 1/2"; Boiler Water Flow Rate at 180F=203 GPM; Cold Water Extension=7 3/8"; Cold Water Inlet Z=5"; Cold Water NPT=2 1/2"; Cold Water Radius=1 1/4"; Control Enclosure Location=15 1/2"; Control Panel Extension=29 3/4"; Drain Extension=26 5/8"; Drain NPT=1"; Drain Radius=1/2"; Energy Extension=38 13/16"; Flat Side Distance=45 1/2"; Front Skid Extension=77 3/4"; Height to Drain=1 3/4"; Height to Energy=28 11/16"; Height to Hot Outlet=38 3/8"; Height to Relief=44 3/4"; Hot Outlet Angle=0.00°; Hot Outlet Extension=23 3/4"; Hot Outlet NPT=2"; Hot Outlet Offset Horiz=0"; Hot Outlet Offset Vert=23 3/4"; Hot Outlet Radius=1"; Rear Skid Extension=22 3/4"; Recovery Rate 40F to 140F (GPH)=2390; Relief Valve Extension=25 3/4"; Skid Length=55"; Skid Spacing=27"; U Tube Extension=13 1/4"; U Tube Radius=6 3/8"; Unit Height=61 1/8"; Unit Radius=22 3/4"; Weight=1660
- 4300 L 400A-QW: BW Inlet Conn X=3 13/16"; BW Inlet NPT=3"; BW Inlet Radius=1 1/2"; BW Inlet Y=18 11/16"; BW Outlet Conn X=3 13/16"; BW Outlet NPT=3"; BW Outlet Radius=1 1/2"; BW Outlet Y=33 11/16"; BW Plumbing Total Z=18 9/16"; BW Up=16 13/16"; BW Up Radius=1 1/2"; BW X=23 5/16"; BW Z=7 1/2"; Boiler Water Flow Rate at 180F=179 GPM; Cold Water Extension=7 3/8"; Cold Water Inlet Z=5"; Cold Water NPT=2 1/2"; Cold Water Radius=1 1/4"; Control Enclosure Location=20"; Control Panel Extension=29 3/4"; Drain Extension=26 5/8"; Drain NPT=1"; Drain Radius=1/2"; Energy Extension=38 13/16"; Flat Side Distance=45 1/2"; Front Skid Extension=77 3/4"; Height to Drain=1 3/4"; Height to Energy=28 11/16"; Height to Hot Outlet=68 1/8"; Height to Relief=68 11/16"; Hot Outlet Angle=90.00°; Hot Outlet Extension=23 3/4"; Hot Outlet NPT=2"; Hot Outlet Offset Horiz=23 3/4"; Hot Outlet Offset Vert=0"; Hot Outlet Radius=1"; Rear Skid Extension=22 3/4"; Recovery Rate 40F to 140F (GPH)=2110; Relief Valve Extension=25 3/4"; Skid Length=55"; Skid Spacing=27"; U Tube Extension=11 1/16"; U Tube Radius=6 3/8"; Unit Height=85 1/8"; Unit Radius=22 3/4"; Weight=1780
- 4300 L 300A-QW: BW Inlet Conn X=3 13/16"; BW Inlet NPT=3"; BW Inlet Radius=1 1/2"; BW Inlet Y=18 11/16"; BW Outlet Conn X=3 13/16"; BW Outlet NPT=3"; BW Outlet Radius=1 1/2"; BW Outlet Y=33 11/16"; BW Plumbing Total Z=18 9/16"; BW Up=16 13/16"; BW Up Radius=1 1/2"; BW X=23 5/16"; BW Z=7 1/2"; Boiler Water Flow Rate at 180F=152 GPM; Cold Water Extension=7 3/8"; Cold Water Inlet Z=5"; Cold Water NPT=2 1/2"; Cold Water Radius=1 1/4"; Control Enclosure Location=20"; Control Panel Extension=29 3/4"; Drain Extension=26 5/8"; Drain NPT=1"; Drain Radius=1/2"; Energy Extension=38 13/16"; Flat Side Distance=45 1/2"; Front Skid Extension=77 3/4"; Height to Drain=1 3/4"; Height to Energy=28 11/16"; Height to Hot Outlet=50 3/8"; Height to Relief=56 3/4"; Hot Outlet Angle=0.00°; Hot Outlet Extension=23 3/4"; Hot Outlet NPT=2"; Hot Outlet Offset Horiz=0"; Hot Outlet Offset Vert=23 3/4"; Hot Outlet Radius=1"; Rear Skid Extension=22 3/4"; Recovery Rate 40F to 140F (GPH)=1790; Relief Valve Extension=25 3/4"; Skid Length=55"; Skid Spacing=27"; U Tube Extension=11 1/16"; U Tube Radius=6 3/8"; Unit Height=73 1/8"; Unit Radius=22 3/4"; Weight=1700
- 4300 L 250A-QW: BW Inlet Conn X=3 13/16"; BW Inlet NPT=3"; BW Inlet Radius=1 1/2"; BW Inlet Y=18 11/16"; BW Outlet Conn X=3 13/16"; BW Outlet NPT=3"; BW Outlet Radius=1 1/2"; BW Outlet Y=33 11/16"; BW Plumbing Total Z=20 3/4"; BW Up=16 13/16"; BW Up Radius=1 1/2"; BW X=23 5/16"; BW Z=7 1/2"; Boiler Water Flow Rate at 180F=179 GPM; Cold Water Extension=7 3/8"; Cold Water Inlet Z=5"; Cold Water NPT=2 1/2"; Cold Water Radius=1 1/4"; Control Enclosure Location=15 1/2"; Control Panel Extension=29 3/4"; Drain Extension=26 5/8"; Drain NPT=1"; Drain Radius=1/2"; Energy Extension=38 13/16"; Flat Side Distance=45 1/2"; Front Skid Extension=77 3/4"; Height to Drain=1 3/4"; Height to Energy=28 11/16"; Height to Hot Outlet=38 3/8"; Height to Relief=44 3/4"; Hot Outlet Angle=0.00°; Hot Outlet Extension=23 3/4"; Hot Outlet NPT=2"; Hot Outlet Offset Horiz=0"; Hot Outlet Offset Vert=23 3/4"; Hot Outlet Radius=1"; Rear Skid Extension=22 3/4"; Recovery Rate 40F to 140F (GPH)=2110; Relief Valve Extension=25 3/4"; Skid Length=55"; Skid Spacing=27"; U Tube Extension=13 1/4"; U Tube Radius=6 3/8"; Unit Height=61 1/8"; Unit Radius=22 3/4"; Weight=1640
- 4200 L 400A-QWD: BW Inlet Conn X=3 13/16"; BW Inlet NPT=3"; BW Inlet Radius=1 1/2"; BW Inlet Y=18 11/16"; BW Outlet Conn X=3 13/16"; BW Outlet NPT=3"; BW Outlet Radius=1 1/2"; BW Outlet Y=33 11/16"; BW Plumbing Total Z=18 9/16"; BW Up=16 13/16"; BW Up Radius=1 1/2"; BW X=23 5/16"; BW Z=7 1/2"; Boiler Water Flow Rate at 180F=179 GPM; Cold Water Extension=7 3/8"; Cold Water Inlet Z=5"; Cold Water NPT=2 1/2"; Cold Water Radius=1 1/4"; Control Enclosure Location=20"; Control Panel Extension=29 3/4"; Drain Extension=26 5/8"; Drain NPT=1"; Drain Radius=1/2"; Energy Extension=38 13/16"; Flat Side Distance=45 1/2"; Front Skid Extension=77 3/4"; Height to Drain=1 3/4"; Height to Energy=28 11/16"; Height to Hot Outlet=68 1/8"; Height to Relief=68 11/16"; Hot Outlet Angle=90.00°; Hot Outlet Extension=23 3/4"; Hot Outlet NPT=2"; Hot Outlet Offset Horiz=23 3/4"; Hot Outlet Offset Vert=0"; Hot Outlet Radius=1"; Rear Skid Extension=22 3/4"; Recovery Rate 40F to 140F (GPH)=2100; Relief Valve Extension=25 3/4"; Skid Length=55"; Skid Spacing=27"; U Tube Extension=11 1/16"; U Tube Radius=6 3/8"; Unit Height=85 1/8"; Unit Radius=22 3/4"; Weight=2010
- 4200 L 300A-QWD: BW Inlet Conn X=3 13/16"; BW Inlet NPT=3"; BW Inlet Radius=1 1/2"; BW Inlet Y=18 11/16"; BW Outlet Conn X=3 13/16"; BW Outlet NPT=3"; BW Outlet Radius=1 1/2"; BW Outlet Y=33 11/16"; BW Plumbing Total Z=18 9/16"; BW Up=16 13/16"; BW Up Radius=1 1/2"; BW X=23 5/16"; BW Z=7 1/2"; Boiler Water Flow Rate at 180F=179 GPM; Cold Water Extension=7 3/8"; Cold Water Inlet Z=5"; Cold Water NPT=2 1/2"; Cold Water Radius=1 1/4"; Control Enclosure Location=20"; Control Panel Extension=29 3/4"; Drain Extension=26 5/8"; Drain NPT=1"; Drain Radius=1/2"; Energy Extension=38 13/16"; Flat Side Distance=45 1/2"; Front Skid Extension=77 3/4"; Height to Drain=1 3/4"; Height to Energy=28 11/16"; Height to Hot Outlet=50 3/8"; Height to Relief=56 3/4"; Hot Outlet Angle=0.00°; Hot Outlet Extension=23 3/4"; Hot Outlet NPT=2"; Hot Outlet Offset Horiz=0"; Hot Outlet Offset Vert=23 3/4"; Hot Outlet Radius=1"; Rear Skid Extension=22 3/4"; Recovery Rate 40F to 140F (GPH)=2100; Relief Valve Extension=25 3/4"; Skid Length=55"; Skid Spacing=27"; U Tube Extension=11 1/16"; U Tube Radius=6 3/8"; Unit Height=73 1/8"; Unit Radius=22 3/4"; Weight=1930
- 4200 L 250A-QWD: BW Inlet Conn X=3 13/16"; BW Inlet NPT=3"; BW Inlet Radius=1 1/2"; BW Inlet Y=18 11/16"; BW Outlet Conn X=3 13/16"; BW Outlet NPT=3"; BW Outlet Radius=1 1/2"; BW Outlet Y=33 11/16"; BW Plumbing Total Z=20 3/4"; BW Up=16 13/16"; BW Up Radius=1 1/2"; BW X=23 5/16"; BW Z=7 1/2"; Boiler Water Flow Rate at 180F=179 GPM; Cold Water Extension=7 3/8"; Cold Water Inlet Z=5"; Cold Water NPT=2 1/2"; Cold Water Radius=1 1/4"; Control Enclosure Location=15 1/2"; Control Panel Extension=29 3/4"; Drain Extension=26 5/8"; Drain NPT=1"; Drain Radius=1/2"; Energy Extension=38 13/16"; Flat Side Distance=45 1/2"; Front Skid Extension=77 3/4"; Height to Drain=1 3/4"; Height to Energy=28 11/16"; Height to Hot Outlet=38 3/8"; Height to Relief=44 3/4"; Hot Outlet Angle=0.00°; Hot Outlet Extension=23 3/4"; Hot Outlet NPT=2"; Hot Outlet Offset Horiz=0"; Hot Outlet Offset Vert=23 3/4"; Hot Outlet Radius=1"; Rear Skid Extension=22 3/4"; Recovery Rate 40F to 140F (GPH)=2100; Relief Valve Extension=25 3/4"; Skid Length=55"; Skid Spacing=27"; U Tube Extension=13 1/4"; U Tube Radius=6 3/8"; Unit Height=61 1/8"; Unit Radius=22 3/4"; Weight=1870
- 4000 L 400A-QW: BW Inlet Conn X=3 13/16"; BW Inlet NPT=3"; BW Inlet Radius=1 1/2"; BW Inlet Y=18 11/16"; BW Outlet Conn X=3 13/16"; BW Outlet NPT=3"; BW Outlet Radius=1 1/2"; BW Outlet Y=33 11/16"; BW Plumbing Total Z=18 9/16"; BW Up=16 13/16"; BW Up Radius=1 1/2"; BW X=23 5/16"; BW Z=7 1/2"; Boiler Water Flow Rate at 180F=152 GPM; Cold Water Extension=7 3/8"; Cold Water Inlet Z=5"; Cold Water NPT=2 1/2"; Cold Water Radius=1 1/4"; Control Enclosure Location=20"; Control Panel Extension=29 3/4"; Drain Extension=26 5/8"; Drain NPT=1"; Drain Radius=1/2"; Energy Extension=27 13/16"; Flat Side Distance=45 1/2"; Front Skid Extension=77 3/4"; Height to Drain=1 3/4"; Height to Energy=28 11/16"; Height to Hot Outlet=68 1/8"; Height to Relief=68 11/16"; Hot Outlet Angle=90.00°; Hot Outlet Extension=23 3/4"; Hot Outlet NPT=2"; Hot Outlet Offset Horiz=23 3/4"; Hot Outlet Offset Vert=0"; Hot Outlet Radius=1"; Rear Skid Extension=22 3/4"; Recovery Rate 40F to 140F (GPH)=1790; Relief Valve Extension=25 3/4"; Skid Length=55"; Skid Spacing=27"; U Tube Extension=11 1/16"; U Tube Radius=6 3/8"; Unit Height=85 1/8"; Unit Radius=22 3/4"; Weight=1760
- 4000 L 300A-QW: BW Inlet Conn X=3 13/16"; BW Inlet NPT=3"; BW Inlet Radius=1 1/2"; BW Inlet Y=18 11/16"; BW Outlet Conn X=3 13/16"; BW Outlet NPT=3"; BW Outlet Radius=1 1/2"; BW Outlet Y=33 11/16"; BW Plumbing Total Z=18 9/16"; BW Up=16 13/16"; BW Up Radius=1 1/2"; BW X=23 5/16"; BW Z=7 1/2"; Boiler Water Flow Rate at 180F=152 GPM; Cold Water Extension=7 3/8"; Cold Water Inlet Z=5"; Cold Water NPT=2 1/2"; Cold Water Radius=1 1/4"; Control Enclosure Location=20"; Control Panel Extension=29 3/4"; Drain Extension=26 5/8"; Drain NPT=1"; Drain Radius=1/2"; Energy Extension=27 13/16"; Flat Side Distance=45 1/2"; Front Skid Extension=77 3/4"; Height to Drain=1 3/4"; Height to Energy=28 11/16"; Height to Hot Outlet=50 3/8"; Height to Relief=56 3/4"; Hot Outlet Angle=0.00°; Hot Outlet Extension=23 3/4"; Hot Outlet NPT=2"; Hot Outlet Offset Horiz=0"; Hot Outlet Offset Vert=23 3/4"; Hot Outlet Radius=1"; Rear Skid Extension=22 3/4"; Recovery Rate 40F to 140F (GPH)=1790; Relief Valve Extension=25 3/4"; Skid Length=55"; Skid Spacing=27"; U Tube Extension=11 1/16"; U Tube Radius=6 3/8"; Unit Height=73 1/8"; Unit Radius=22 3/4"; Weight=1670
- 4000 L 250A-QW: BW Inlet Conn X=3 13/16"; BW Inlet NPT=3"; BW Inlet Radius=1 1/2"; BW Inlet Y=18 11/16"; BW Outlet Conn X=3 13/16"; BW Outlet NPT=3"; BW Outlet Radius=1 1/2"; BW Outlet Y=33 11/16"; BW Plumbing Total Z=20 3/4"; BW Up=16 13/16"; BW Up Radius=1 1/2"; BW X=23 5/16"; BW Z=7 1/2"; Boiler Water Flow Rate at 180F=152 GPM; Cold Water Extension=7 3/8"; Cold Water Inlet Z=5"; Cold Water NPT=2 1/2"; Cold Water Radius=1 1/4"; Control Enclosure Location=15 1/2"; Control Panel Extension=29 3/4"; Drain Extension=26 5/8"; Drain NPT=1"; Drain Radius=1/2"; Energy Extension=27 13/16"; Flat Side Distance=45 1/2"; Front Skid Extension=77 3/4"; Height to Drain=1 3/4"; Height to Energy=28 11/16"; Height to Hot Outlet=38 3/8"; Height to Relief=44 3/4"; Hot Outlet Angle=0.00°; Hot Outlet Extension=23 3/4"; Hot Outlet NPT=2"; Hot Outlet Offset Horiz=0"; Hot Outlet Offset Vert=23 3/4"; Hot Outlet Radius=1"; Rear Skid Extension=22 3/4"; Recovery Rate 40F to 140F (GPH)=1790; Relief Valve Extension=25 3/4"; Skid Length=55"; Skid Spacing=27"; U Tube Extension=13 1/4"; U Tube Radius=6 3/8"; Unit Height=61 1/8"; Unit Radius=22 3/4"; Weight=1610
- 3500 L 400A-QW: BW Inlet Conn X=2 15/16"; BW Inlet NPT=2 1/2"; BW Inlet Radius=1 1/4"; BW Inlet Y=18 11/16"; BW Outlet Conn X=2 15/16"; BW Outlet NPT=2 1/2"; BW Outlet Radius=1 1/4"; BW Outlet Y=33 11/16"; BW Plumbing Total Z=18 1/16"; BW Up=15 15/16"; BW Up Radius=1 1/4"; BW X=22 7/16"; BW Z=7 1/2"; Boiler Water Flow Rate at 180F=138 GPM; Cold Water Extension=6 3/8"; Cold Water Inlet Z=5 1/8"; Cold Water NPT=2 1/2"; Cold Water Radius=1 1/4"; Control Enclosure Location=20"; Control Panel Extension=29 3/4"; Drain Extension=26 5/8"; Drain NPT=1"; Drain Radius=1/2"; Energy Extension=38 13/16"; Flat Side Distance=45 1/2"; Front Skid Extension=77 3/4"; Height to Drain=1 3/4"; Height to Energy=28 11/16"; Height to Hot Outlet=68 1/8"; Height to Relief=68 11/16"; Hot Outlet Angle=90.00°; Hot Outlet Extension=23 3/4"; Hot Outlet NPT=2"; Hot Outlet Offset Horiz=23 3/4"; Hot Outlet Offset Vert=0"; Hot Outlet Radius=1"; Rear Skid Extension=22 3/4"; Recovery Rate 40F to 140F (GPH)=1630; Relief Valve Extension=25 3/4"; Skid Length=55"; Skid Spacing=27"; U Tube Extension=10 9/16"; U Tube Radius=5 3/8"; Unit Height=85 1/8"; Unit Radius=22 3/4"; Weight=1660
- 3500 L 300A-QW: BW Inlet Conn X=2 15/16"; BW Inlet NPT=2 1/2"; BW Inlet Radius=1 1/4"; BW Inlet Y=18 11/16"; BW Outlet Conn X=2 15/16"; BW Outlet NPT=2 1/2"; BW Outlet Radius=1 1/4"; BW Outlet Y=33 11/16"; BW Plumbing Total Z=18 1/16"; BW Up=15 15/16"; BW Up Radius=1 1/4"; BW X=22 7/16"; BW Z=7 1/2"; Boiler Water Flow Rate at 180F=138 GPM; Cold Water Extension=6 3/8"; Cold Water Inlet Z=5 1/8"; Cold Water NPT=2 1/2"; Cold Water Radius=1 1/4"; Control Enclosure Location=20"; Control Panel Extension=29 3/4"; Drain Extension=26 5/8"; Drain NPT=1"; Drain Radius=1/2"; Energy Extension=38 13/16"; Flat Side Distance=45 1/2"; Front Skid Extension=77 3/4"; Height to Drain=1 3/4"; Height to Energy=28 11/16"; Height to Hot Outlet=50 3/8"; Height to Relief=56 3/4"; Hot Outlet Angle=0.00°; Hot Outlet Extension=23 3/4"; Hot Outlet NPT=2"; Hot Outlet Offset Horiz=0"; Hot Outlet Offset Vert=23 3/4"; Hot Outlet Radius=1"; Rear Skid Extension=22 3/4"; Recovery Rate 40F to 140F (GPH)=1630; Relief Valve Extension=25 3/4"; Skid Length=55"; Skid Spacing=27"; U Tube Extension=10 9/16"; U Tube Radius=5 3/8"; Unit Height=73 1/8"; Unit Radius=22 3/4"; Weight=1590
- 3500 L 250A-QW: BW Inlet Conn X=2 15/16"; BW Inlet NPT=2 1/2"; BW Inlet Radius=1 1/4"; BW Inlet Y=18 11/16"; BW Outlet Conn X=2 15/16"; BW Outlet NPT=2 1/2"; BW Outlet Radius=1 1/4"; BW Outlet Y=33 11/16"; BW Plumbing Total Z=20 7/16"; BW Up=15 15/16"; BW Up Radius=1 1/4"; BW X=22 7/16"; BW Z=7 1/2"; Boiler Water Flow Rate at 180F=138 GPM; Cold Water Extension=6 3/8"; Cold Water Inlet Z=5 1/8"; Cold Water NPT=2 1/2"; Cold Water Radius=1 1/4"; Control Enclosure Location=15 1/2"; Control Panel Extension=29 3/4"; Drain Extension=26 5/8"; Drain NPT=1"; Drain Radius=1/2"; Energy Extension=38 13/16"; Flat Side Distance=45 1/2"; Front Skid Extension=77 3/4"; Height to Drain=1 3/4"; Height to Energy=28 11/16"; Height to Hot Outlet=38 3/8"; Height to Relief=44 3/4"; Hot Outlet Angle=0.00°; Hot Outlet Extension=23 3/4"; Hot Outlet NPT=2"; Hot Outlet Offset Horiz=0"; Hot Outlet Offset Vert=23 3/4"; Hot Outlet Radius=1"; Rear Skid Extension=22 3/4"; Recovery Rate 40F to 140F (GPH)=1630; Relief Valve Extension=25 3/4"; Skid Length=55"; Skid Spacing=27"; U Tube Extension=12 15/16"; U Tube Radius=5 3/8"; Unit Height=61 1/8"; Unit Radius=22 3/4"; Weight=1530
- 3400 L 400A-QWD: BW Inlet Conn X=3 11/16"; BW Inlet NPT=2 1/2"; BW Inlet Radius=1 1/4"; BW Inlet Y=18 11/16"; BW Outlet Conn X=3 11/16"; BW Outlet NPT=2 1/2"; BW Outlet Radius=1 1/4"; BW Outlet Y=33 11/16"; BW Plumbing Total Z=18 9/16"; BW Up=16 13/16"; BW Up Radius=1 1/4"; BW X=23 5/16"; BW Z=7 1/2"; Boiler Water Flow Rate at 180F=138 GPM; Cold Water Extension=7 3/8"; Cold Water Inlet Z=5"; Cold Water NPT=2 1/2"; Cold Water Radius=1 1/4"; Control Enclosure Location=20"; Control Panel Extension=29 3/4"; Drain Extension=26 5/8"; Drain NPT=1"; Drain Radius=1/2"; Energy Extension=27 13/16"; Flat Side Distance=45 1/2"; Front Skid Extension=77 3/4"; Height to Drain=1 3/4"; Height to Energy=28 11/16"; Height to Hot Outlet=68 1/8"; Height to Relief=68 11/16"; Hot Outlet Angle=90.00°; Hot Outlet Extension=23 3/4"; Hot Outlet NPT=2"; Hot Outlet Offset Horiz=23 3/4"; Hot Outlet Offset Vert=0"; Hot Outlet Radius=1"; Rear Skid Extension=22 3/4"; Recovery Rate 40F to 140F (GPH)=1620; Relief Valve Extension=25 3/4"; Skid Length=55"; Skid Spacing=27"; U Tube Extension=11 1/16"; U Tube Radius=6 3/8"; Unit Height=85 1/8"; Unit Radius=22 3/4"; Weight=1930
- 3400 L 300A-QWD: BW Inlet Conn X=3 11/16"; BW Inlet NPT=2 1/2"; BW Inlet Radius=1 1/4"; BW Inlet Y=18 11/16"; BW Outlet Conn X=3 11/16"; BW Outlet NPT=2 1/2"; BW Outlet Radius=1 1/4"; BW Outlet Y=33 11/16"; BW Plumbing Total Z=18 9/16"; BW Up=16 13/16"; BW Up Radius=1 1/4"; BW X=23 5/16"; BW Z=7 1/2"; Boiler Water Flow Rate at 180F=138 GPM; Cold Water Extension=7 3/8"; Cold Water Inlet Z=5"; Cold Water NPT=2 1/2"; Cold Water Radius=1 1/4"; Control Enclosure Location=20"; Control Panel Extension=29 3/4"; Drain Extension=26 5/8"; Drain NPT=1"; Drain Radius=1/2"; Energy Extension=27 13/16"; Flat Side Distance=45 1/2"; Front Skid Extension=77 3/4"; Height to Drain=1 3/4"; Height to Energy=28 11/16"; Height to Hot Outlet=50 3/8"; Height to Relief=56 3/4"; Hot Outlet Angle=0.00°; Hot Outlet Extension=23 3/4"; Hot Outlet NPT=2"; Hot Outlet Offset Horiz=0"; Hot Outlet Offset Vert=23 3/4"; Hot Outlet Radius=1"; Rear Skid Extension=22 3/4"; Recovery Rate 40F to 140F (GPH)=1620; Relief Valve Extension=25 3/4"; Skid Length=55"; Skid Spacing=27"; U Tube Extension=11 1/16"; U Tube Radius=6 3/8"; Unit Height=73 1/8"; Unit Radius=22 3/4"; Weight=1840
- 3400 L 250A-QWD: BW Inlet Conn X=3 11/16"; BW Inlet NPT=2 1/2"; BW Inlet Radius=1 1/4"; BW Inlet Y=18 11/16"; BW Outlet Conn X=3 11/16"; BW Outlet NPT=2 1/2"; BW Outlet Radius=1 1/4"; BW Outlet Y=33 11/16"; BW Plumbing Total Z=20 3/4"; BW Up=16 13/16"; BW Up Radius=1 1/4"; BW X=23 5/16"; BW Z=7 1/2"; Boiler Water Flow Rate at 180F=138 GPM; Cold Water Extension=7 3/8"; Cold Water Inlet Z=5"; Cold Water NPT=2 1/2"; Cold Water Radius=1 1/4"; Control Enclosure Location=15 1/2"; Control Panel Extension=29 3/4"; Drain Extension=26 5/8"; Drain NPT=1"; Drain Radius=1/2"; Energy Extension=27 13/16"; Flat Side Distance=45 1/2"; Front Skid Extension=77 3/4"; Height to Drain=1 3/4"; Height to Energy=28 11/16"; Height to Hot Outlet=38 3/8"; Height to Relief=44 3/4"; Hot Outlet Angle=0.00°; Hot Outlet Extension=23 3/4"; Hot Outlet NPT=2"; Hot Outlet Offset Horiz=0"; Hot Outlet Offset Vert=23 3/4"; Hot Outlet Radius=1"; Rear Skid Extension=22 3/4"; Recovery Rate 40F to 140F (GPH)=1620; Relief Valve Extension=25 3/4"; Skid Length=55"; Skid Spacing=27"; U Tube Extension=13 1/4"; U Tube Radius=6 3/8"; Unit Height=61 1/8"; Unit Radius=22 3/4"; Weight=1780
- 3000 L 400A-QW: BW Inlet Conn X=2 15/16"; BW Inlet NPT=2 1/2"; BW Inlet Radius=1 1/4"; BW Inlet Y=18 11/16"; BW Outlet Conn X=2 15/16"; BW Outlet NPT=2 1/2"; BW Outlet Radius=1 1/4"; BW Outlet Y=33 11/16"; BW Plumbing Total Z=18 1/16"; BW Up=15 15/16"; BW Up Radius=1 1/4"; BW X=22 7/16"; BW Z=7 1/2"; Boiler Water Flow Rate at 180F=120 GPM; Cold Water Extension=6 3/8"; Cold Water Inlet Z=5 1/8"; Cold Water NPT=2 1/2"; Cold Water Radius=1 1/4"; Control Enclosure Location=20"; Control Panel Extension=29 3/4"; Drain Extension=26 5/8"; Drain NPT=1"; Drain Radius=1/2"; Energy Extension=38 13/16"; Flat Side Distance=45 1/2"; Front Skid Extension=77 3/4"; Height to Drain=1 3/4"; Height to Energy=28 11/16"; Height to Hot Outlet=68 1/8"; Height to Relief=68 11/16"; Hot Outlet Angle=90.00°; Hot Outlet Extension=23 3/4"; Hot Outlet NPT=2"; Hot Outlet Offset Horiz=23 3/4"; Hot Outlet Offset Vert=0"; Hot Outlet Radius=1"; Rear Skid Extension=22 3/4"; Recovery Rate 40F to 140F (GPH)=1420; Relief Valve Extension=25 3/4"; Skid Length=55"; Skid Spacing=27"; U Tube Extension=10 9/16"; U Tube Radius=5 3/8"; Unit Height=85 1/8"; Unit Radius=22 3/4"; Weight=1660
- 3000 L 300A-QW: BW Inlet Conn X=2 15/16"; BW Inlet NPT=2 1/2"; BW Inlet Radius=1 1/4"; BW Inlet Y=18 11/16"; BW Outlet Conn X=2 15/16"; BW Outlet NPT=2 1/2"; BW Outlet Radius=1 1/4"; BW Outlet Y=33 11/16"; BW Plumbing Total Z=18 1/16"; BW Up=15 15/16"; BW Up Radius=1 1/4"; BW X=22 7/16"; BW Z=7 1/2"; Boiler Water Flow Rate at 180F=120 GPM; Cold Water Extension=6 3/8"; Cold Water Inlet Z=5 1/8"; Cold Water NPT=2 1/2"; Cold Water Radius=1 1/4"; Control Enclosure Location=20"; Control Panel Extension=29 3/4"; Drain Extension=26 5/8"; Drain NPT=1"; Drain Radius=1/2"; Energy Extension=38 13/16"; Flat Side Distance=45 1/2"; Front Skid Extension=77 3/4"; Height to Drain=1 3/4"; Height to Energy=28 11/16"; Height to Hot Outlet=50 3/8"; Height to Relief=56 3/4"; Hot Outlet Angle=0.00°; Hot Outlet Extension=23 3/4"; Hot Outlet NPT=2"; Hot Outlet Offset Horiz=0"; Hot Outlet Offset Vert=23 3/4"; Hot Outlet Radius=1"; Rear Skid Extension=22 3/4"; Recovery Rate 40F to 140F (GPH)=1420; Relief Valve Extension=25 3/4"; Skid Length=55"; Skid Spacing=27"; U Tube Extension=10 9/16"; U Tube Radius=5 3/8"; Unit Height=73 1/8"; Unit Radius=22 3/4"; Weight=1580
- 3000 L 250A-QW: BW Inlet Conn X=2 15/16"; BW Inlet NPT=2 1/2"; BW Inlet Radius=1 1/4"; BW Inlet Y=18 11/16"; BW Outlet Conn X=2 15/16"; BW Outlet NPT=2 1/2"; BW Outlet Radius=1 1/4"; BW Outlet Y=33 11/16"; BW Plumbing Total Z=20 7/16"; BW Up=15 15/16"; BW Up Radius=1 1/4"; BW X=22 7/16"; BW Z=7 1/2"; Boiler Water Flow Rate at 180F=120 GPM; Cold Water Extension=6 3/8"; Cold Water Inlet Z=5 1/8"; Cold Water NPT=2 1/2"; Cold Water Radius=1 1/4"; Control Enclosure Location=15 1/2"; Control Panel Extension=29 3/4"; Drain Extension=26 5/8"; Drain NPT=1"; Drain Radius=1/2"; Energy Extension=38 13/16"; Flat Side Distance=45 1/2"; Front Skid Extension=77 3/4"; Height to Drain=1 3/4"; Height to Energy=28 11/16"; Height to Hot Outlet=38 3/8"; Height to Relief=44 3/4"; Hot Outlet Angle=0.00°; Hot Outlet Extension=23 3/4"; Hot Outlet NPT=2"; Hot Outlet Offset Horiz=0"; Hot Outlet Offset Vert=23 3/4"; Hot Outlet Radius=1"; Rear Skid Extension=22 3/4"; Recovery Rate 40F to 140F (GPH)=1420; Relief Valve Extension=25 3/4"; Skid Length=55"; Skid Spacing=27"; U Tube Extension=12 15/16"; U Tube Radius=5 3/8"; Unit Height=61 1/8"; Unit Radius=22 3/4"; Weight=1520
- 300 L 400A-QW: BW Inlet Conn X=1 5/16"; BW Inlet NPT=3/4"; BW Inlet Radius=3/8"; BW Inlet Y=5"; BW Outlet Conn X=1 5/16"; BW Outlet NPT=3/4"; BW Outlet Radius=3/8"; BW Outlet Y=9 1/16"; BW Plumbing Total Z=15 3/8"; BW Up=5 3/4"; BW Up Radius=3/8"; BW X=8 1/16"; BW Z=5 15/16"; Boiler Water Flow Rate at 180F=12 GPM; Cold Water Extension=3 1/4"; Cold Water Inlet Z=5 5/8"; Cold Water NPT=2"; Cold Water Radius=1"; Control Enclosure Location=20"; Control Panel Extension=29 3/4"; Drain Extension=26 5/8"; Drain NPT=1"; Drain Radius=1/2"; Energy Extension=27 13/16"; Flat Side Distance=45 1/2"; Front Skid Extension=68 3/4"; Height to Drain=1 3/4"; Height to Energy=28 11/16"; Height to Hot Outlet=68 1/8"; Height to Relief=68 11/16"; Hot Outlet Angle=90.00°; Hot Outlet Extension=23 3/4"; Hot Outlet NPT=2"; Hot Outlet Offset Horiz=23 3/4"; Hot Outlet Offset Vert=0"; Hot Outlet Radius=1"; Rear Skid Extension=22 3/4"; Recovery Rate 40F to 140F (GPH)=140; Relief Valve Extension=25 3/4"; Skid Length=46"; Skid Spacing=27"; U Tube Extension=9 7/16"; U Tube Radius=2 1/4"; Unit Height=85 1/8"; Unit Radius=22 3/4"; Weight=1330
- 300 L 300A-QW: BW Inlet Conn X=1 5/16"; BW Inlet NPT=3/4"; BW Inlet Radius=3/8"; BW Inlet Y=5"; BW Outlet Conn X=1 5/16"; BW Outlet NPT=3/4"; BW Outlet Radius=3/8"; BW Outlet Y=9 1/16"; BW Plumbing Total Z=15 3/8"; BW Up=5 3/4"; BW Up Radius=3/8"; BW X=8 1/16"; BW Z=5 15/16"; Boiler Water Flow Rate at 180F=12 GPM; Cold Water Extension=3 1/4"; Cold Water Inlet Z=5 5/8"; Cold Water NPT=2"; Cold Water Radius=1"; Control Enclosure Location=20"; Control Panel Extension=29 3/4"; Drain Extension=26 5/8"; Drain NPT=1"; Drain Radius=1/2"; Energy Extension=27 13/16"; Flat Side Distance=45 1/2"; Front Skid Extension=68 3/4"; Height to Drain=1 3/4"; Height to Energy=28 11/16"; Height to Hot Outlet=50 3/8"; Height to Relief=56 3/4"; Hot Outlet Angle=0.00°; Hot Outlet Extension=23 3/4"; Hot Outlet NPT=2"; Hot Outlet Offset Horiz=0"; Hot Outlet Offset Vert=23 3/4"; Hot Outlet Radius=1"; Rear Skid Extension=22 3/4"; Recovery Rate 40F to 140F (GPH)=140; Relief Valve Extension=25 3/4"; Skid Length=46"; Skid Spacing=27"; U Tube Extension=9 7/16"; U Tube Radius=2 1/4"; Unit Height=73 1/8"; Unit Radius=22 3/4"; Weight=1240
- 300 L 250A-QW: BW Inlet Conn X=1 5/16"; BW Inlet NPT=3/4"; BW Inlet Radius=3/8"; BW Inlet Y=5"; BW Outlet Conn X=1 5/16"; BW Outlet NPT=3/4"; BW Outlet Radius=3/8"; BW Outlet Y=9 1/16"; BW Plumbing Total Z=17 3/16"; BW Up=5 3/4"; BW Up Radius=3/8"; BW X=8 1/16"; BW Z=5 15/16"; Boiler Water Flow Rate at 180F=12 GPM; Cold Water Extension=3 1/4"; Cold Water Inlet Z=5 5/8"; Cold Water NPT=2"; Cold Water Radius=1"; Control Enclosure Location=15 1/2"; Control Panel Extension=29 3/4"; Drain Extension=26 5/8"; Drain NPT=1"; Drain Radius=1/2"; Energy Extension=27 13/16"; Flat Side Distance=45 1/2"; Front Skid Extension=68 3/4"; Height to Drain=1 3/4"; Height to Energy=28 11/16"; Height to Hot Outlet=38 3/8"; Height to Relief=44 3/4"; Hot Outlet Angle=0.00°; Hot Outlet Extension=23 3/4"; Hot Outlet NPT=2"; Hot Outlet Offset Horiz=0"; Hot Outlet Offset Vert=23 3/4"; Hot Outlet Radius=1"; Rear Skid Extension=22 3/4"; Recovery Rate 40F to 140F (GPH)=140; Relief Valve Extension=25 3/4"; Skid Length=46"; Skid Spacing=27"; U Tube Extension=11 1/4"; U Tube Radius=2 1/4"; Unit Height=61 1/8"; Unit Radius=22 3/4"; Weight=1180
- 2800 L 400A-QWD: BW Inlet Conn X=3 11/16"; BW Inlet NPT=2 1/2"; BW Inlet Radius=1 1/4"; BW Inlet Y=12 3/8"; BW Outlet Conn X=3 11/16"; BW Outlet NPT=2 1/2"; BW Outlet Radius=1 1/4"; BW Outlet Y=23 7/16"; BW Plumbing Total Z=22 1/16"; BW Up=13 1/16"; BW Up Radius=1 1/4"; BW X=17 13/16"; BW Z=11 1/2"; Boiler Water Flow Rate at 180F=122 GPM; Cold Water Extension=7 3/8"; Cold Water Inlet Z=5 1/8"; Cold Water NPT=2 1/2"; Cold Water Radius=1 1/4"; Control Enclosure Location=20"; Control Panel Extension=29 3/4"; Drain Extension=26 5/8"; Drain NPT=1"; Drain Radius=1/2"; Energy Extension=38 13/16"; Flat Side Distance=45 1/2"; Front Skid Extension=77 3/4"; Height to Drain=1 3/4"; Height to Energy=28 11/16"; Height to Hot Outlet=68 1/8"; Height to Relief=68 11/16"; Hot Outlet Angle=90.00°; Hot Outlet Extension=23 3/4"; Hot Outlet NPT=2"; Hot Outlet Offset Horiz=23 3/4"; Hot Outlet Offset Vert=0"; Hot Outlet Radius=1"; Rear Skid Extension=22 3/4"; Recovery Rate 40F to 140F (GPH)=1430; Relief Valve Extension=25 3/4"; Skid Length=55"; Skid Spacing=27"; U Tube Extension=10 9/16"; U Tube Radius=6 3/8"; Unit Height=85 1/8"; Unit Radius=22 3/4"; Weight=1740
- 2800 L 300A-QWD: BW Inlet Conn X=3 11/16"; BW Inlet NPT=2 1/2"; BW Inlet Radius=1 1/4"; BW Inlet Y=12 3/8"; BW Outlet Conn X=3 11/16"; BW Outlet NPT=2 1/2"; BW Outlet Radius=1 1/4"; BW Outlet Y=23 7/16"; BW Plumbing Total Z=22 1/16"; BW Up=13 1/16"; BW Up Radius=1 1/4"; BW X=17 13/16"; BW Z=11 1/2"; Boiler Water Flow Rate at 180F=122 GPM; Cold Water Extension=7 3/8"; Cold Water Inlet Z=5 1/8"; Cold Water NPT=2 1/2"; Cold Water Radius=1 1/4"; Control Enclosure Location=20"; Control Panel Extension=29 3/4"; Drain Extension=26 5/8"; Drain NPT=1"; Drain Radius=1/2"; Energy Extension=38 13/16"; Flat Side Distance=45 1/2"; Front Skid Extension=77 3/4"; Height to Drain=1 3/4"; Height to Energy=28 11/16"; Height to Hot Outlet=50 3/8"; Height to Relief=56 3/4"; Hot Outlet Angle=0.00°; Hot Outlet Extension=23 3/4"; Hot Outlet NPT=2"; Hot Outlet Offset Horiz=0"; Hot Outlet Offset Vert=23 3/4"; Hot Outlet Radius=1"; Rear Skid Extension=22 3/4"; Recovery Rate 40F to 140F (GPH)=1430; Relief Valve Extension=25 3/4"; Skid Length=55"; Skid Spacing=27"; U Tube Extension=10 9/16"; U Tube Radius=6 3/8"; Unit Height=73 1/8"; Unit Radius=22 3/4"; Weight=1660
- 2800 L 250A-QWD: BW Inlet Conn X=3 11/16"; BW Inlet NPT=2 1/2"; BW Inlet Radius=1 1/4"; BW Inlet Y=12 3/8"; BW Outlet Conn X=3 11/16"; BW Outlet NPT=2 1/2"; BW Outlet Radius=1 1/4"; BW Outlet Y=23 7/16"; BW Plumbing Total Z=24 7/16"; BW Up=13 1/16"; BW Up Radius=1 1/4"; BW X=17 13/16"; BW Z=11 1/2"; Boiler Water Flow Rate at 180F=122 GPM; Cold Water Extension=7 3/8"; Cold Water Inlet Z=5 1/8"; Cold Water NPT=2 1/2"; Cold Water Radius=1 1/4"; Control Enclosure Location=15 1/2"; Control Panel Extension=29 3/4"; Drain Extension=26 5/8"; Drain NPT=1"; Drain Radius=1/2"; Energy Extension=38 13/16"; Flat Side Distance=45 1/2"; Front Skid Extension=77 3/4"; Height to Drain=1 3/4"; Height to Energy=28 11/16"; Height to Hot Outlet=38 3/8"; Height to Relief=44 3/4"; Hot Outlet Angle=0.00°; Hot Outlet Extension=23 3/4"; Hot Outlet NPT=2"; Hot Outlet Offset Horiz=0"; Hot Outlet Offset Vert=23 3/4"; Hot Outlet Radius=1"; Rear Skid Extension=22 3/4"; Recovery Rate 40F to 140F (GPH)=1430; Relief Valve Extension=25 3/4"; Skid Length=55"; Skid Spacing=27"; U Tube Extension=12 15/16"; U Tube Radius=6 3/8"; Unit Height=61 1/8"; Unit Radius=22 3/4"; Weight=1600
- 2600 L 400A-QW: BW Inlet Conn X=2 15/16"; BW Inlet NPT=2 1/2"; BW Inlet Radius=1 1/4"; BW Inlet Y=12 3/8"; BW Outlet Conn X=2 15/16"; BW Outlet NPT=2 1/2"; BW Outlet Radius=1 1/4"; BW Outlet Y=23 7/16"; BW Plumbing Total Z=22 1/16"; BW Up=13 1/16"; BW Up Radius=1 1/4"; BW X=17 13/16"; BW Z=11 1/2"; Boiler Water Flow Rate at 180F=102 GPM; Cold Water Extension=6 3/8"; Cold Water Inlet Z=5 1/8"; Cold Water NPT=2 1/2"; Cold Water Radius=1 1/4"; Control Enclosure Location=20"; Control Panel Extension=29 3/4"; Drain Extension=26 5/8"; Drain NPT=1"; Drain Radius=1/2"; Energy Extension=27 13/16"; Flat Side Distance=45 1/2"; Front Skid Extension=77 3/4"; Height to Drain=1 3/4"; Height to Energy=28 11/16"; Height to Hot Outlet=68 1/8"; Height to Relief=68 11/16"; Hot Outlet Angle=90.00°; Hot Outlet Extension=23 3/4"; Hot Outlet NPT=2"; Hot Outlet Offset Horiz=23 3/4"; Hot Outlet Offset Vert=0"; Hot Outlet Radius=1"; Rear Skid Extension=22 3/4"; Recovery Rate 40F to 140F (GPH)=1200; Relief Valve Extension=25 3/4"; Skid Length=55"; Skid Spacing=27"; U Tube Extension=10 9/16"; U Tube Radius=5 3/8"; Unit Height=85 1/8"; Unit Radius=22 3/4"; Weight=1580
- 2600 L 300A-QW: BW Inlet Conn X=2 15/16"; BW Inlet NPT=2 1/2"; BW Inlet Radius=1 1/4"; BW Inlet Y=12 3/8"; BW Outlet Conn X=2 15/16"; BW Outlet NPT=2 1/2"; BW Outlet Radius=1 1/4"; BW Outlet Y=23 7/16"; BW Plumbing Total Z=22 1/16"; BW Up=13 1/16"; BW Up Radius=1 1/4"; BW X=17 13/16"; BW Z=11 1/2"; Boiler Water Flow Rate at 180F=102 GPM; Cold Water Extension=6 3/8"; Cold Water Inlet Z=5 1/8"; Cold Water NPT=2 1/2"; Cold Water Radius=1 1/4"; Control Enclosure Location=20"; Control Panel Extension=29 3/4"; Drain Extension=26 5/8"; Drain NPT=1"; Drain Radius=1/2"; Energy Extension=27 13/16"; Flat Side Distance=45 1/2"; Front Skid Extension=77 3/4"; Height to Drain=1 3/4"; Height to Energy=28 11/16"; Height to Hot Outlet=50 3/8"; Height to Relief=56 3/4"; Hot Outlet Angle=0.00°; Hot Outlet Extension=23 3/4"; Hot Outlet NPT=2"; Hot Outlet Offset Horiz=0"; Hot Outlet Offset Vert=23 3/4"; Hot Outlet Radius=1"; Rear Skid Extension=22 3/4"; Recovery Rate 40F to 140F (GPH)=1200; Relief Valve Extension=25 3/4"; Skid Length=55"; Skid Spacing=27"; U Tube Extension=10 9/16"; U Tube Radius=5 3/8"; Unit Height=73 1/8"; Unit Radius=22 3/4"; Weight=1490
- 2600 L 250A-QW: BW Inlet Conn X=2 15/16"; BW Inlet NPT=2 1/2"; BW Inlet Radius=1 1/4"; BW Inlet Y=12 3/8"; BW Outlet Conn X=2 15/16"; BW Outlet NPT=2 1/2"; BW Outlet Radius=1 1/4"; BW Outlet Y=23 7/16"; BW Plumbing Total Z=24 7/16"; BW Up=13 1/16"; BW Up Radius=1 1/4"; BW X=17 13/16"; BW Z=11 1/2"; Boiler Water Flow Rate at 180F=102 GPM; Cold Water Extension=6 3/8"; Cold Water Inlet Z=5 1/8"; Cold Water NPT=2 1/2"; Cold Water Radius=1 1/4"; Control Enclosure Location=15 1/2"; Control Panel Extension=29 3/4"; Drain Extension=26 5/8"; Drain NPT=1"; Drain Radius=1/2"; Energy Extension=27 13/16"; Flat Side Distance=45 1/2"; Front Skid Extension=77 3/4"; Height to Drain=1 3/4"; Height to Energy=28 11/16"; Height to Hot Outlet=38 3/8"; Height to Relief=44 3/4"; Hot Outlet Angle=0.00°; Hot Outlet Extension=23 3/4"; Hot Outlet NPT=2"; Hot Outlet Offset Horiz=0"; Hot Outlet Offset Vert=23 3/4"; Hot Outlet Radius=1"; Rear Skid Extension=22 3/4"; Recovery Rate 40F to 140F (GPH)=1200; Relief Valve Extension=25 3/4"; Skid Length=55"; Skid Spacing=27"; U Tube Extension=12 15/16"; U Tube Radius=5 3/8"; Unit Height=61 1/8"; Unit Radius=22 3/4"; Weight=1430
- 250 L 400A-QWD: BW Inlet Conn X=1 5/16"; BW Inlet NPT=3/4"; BW Inlet Radius=3/8"; BW Inlet Y=5"; BW Outlet Conn X=1 5/16"; BW Outlet NPT=3/4"; BW Outlet Radius=3/8"; BW Outlet Y=9 1/16"; BW Plumbing Total Z=15 3/8"; BW Up=5 3/4"; BW Up Radius=3/8"; BW X=8 1/16"; BW Z=5 15/16"; Boiler Water Flow Rate at 180F=11 GPM; Cold Water Extension=3 1/4"; Cold Water Inlet Z=5 5/8"; Cold Water NPT=2"; Cold Water Radius=1"; Control Enclosure Location=20"; Control Panel Extension=29 3/4"; Drain Extension=26 5/8"; Drain NPT=1"; Drain Radius=1/2"; Energy Extension=27 13/16"; Flat Side Distance=45 1/2"; Front Skid Extension=68 3/4"; Height to Drain=1 3/4"; Height to Energy=28 11/16"; Height to Hot Outlet=68 1/8"; Height to Relief=68 11/16"; Hot Outlet Angle=90.00°; Hot Outlet Extension=23 3/4"; Hot Outlet NPT=2"; Hot Outlet Offset Horiz=23 3/4"; Hot Outlet Offset Vert=0"; Hot Outlet Radius=1"; Rear Skid Extension=22 3/4"; Recovery Rate 40F to 140F (GPH)=130; Relief Valve Extension=25 3/4"; Skid Length=46"; Skid Spacing=27"; U Tube Extension=9 7/16"; U Tube Radius=2 1/4"; Unit Height=85 1/8"; Unit Radius=22 3/4"; Weight=1340
- 250 L 300A-QWD: BW Inlet Conn X=1 5/16"; BW Inlet NPT=3/4"; BW Inlet Radius=3/8"; BW Inlet Y=5"; BW Outlet Conn X=1 5/16"; BW Outlet NPT=3/4"; BW Outlet Radius=3/8"; BW Outlet Y=9 1/16"; BW Plumbing Total Z=15 3/8"; BW Up=5 3/4"; BW Up Radius=3/8"; BW X=8 1/16"; BW Z=5 15/16"; Boiler Water Flow Rate at 180F=11 GPM; Cold Water Extension=3 1/4"; Cold Water Inlet Z=5 5/8"; Cold Water NPT=2"; Cold Water Radius=1"; Control Enclosure Location=20"; Control Panel Extension=29 3/4"; Drain Extension=26 5/8"; Drain NPT=1"; Drain Radius=1/2"; Energy Extension=27 13/16"; Flat Side Distance=45 1/2"; Front Skid Extension=68 3/4"; Height to Drain=1 3/4"; Height to Energy=28 11/16"; Height to Hot Outlet=50 3/8"; Height to Relief=56 3/4"; Hot Outlet Angle=0.00°; Hot Outlet Extension=23 3/4"; Hot Outlet NPT=2"; Hot Outlet Offset Horiz=0"; Hot Outlet Offset Vert=23 3/4"; Hot Outlet Radius=1"; Rear Skid Extension=22 3/4"; Recovery Rate 40F to 140F (GPH)=130; Relief Valve Extension=25 3/4"; Skid Length=46"; Skid Spacing=27"; U Tube Extension=9 7/16"; U Tube Radius=2 1/4"; Unit Height=73 1/8"; Unit Radius=22 3/4"; Weight=1260
- 250 L 250A-QWD: BW Inlet Conn X=1 5/16"; BW Inlet NPT=3/4"; BW Inlet Radius=3/8"; BW Inlet Y=5"; BW Outlet Conn X=1 5/16"; BW Outlet NPT=3/4"; BW Outlet Radius=3/8"; BW Outlet Y=9 1/16"; BW Plumbing Total Z=17 3/16"; BW Up=5 3/4"; BW Up Radius=3/8"; BW X=8 1/16"; BW Z=5 15/16"; Boiler Water Flow Rate at 180F=11 GPM; Cold Water Extension=3 1/4"; Cold Water Inlet Z=5 5/8"; Cold Water NPT=2"; Cold Water Radius=1"; Control Enclosure Location=15 1/2"; Control Panel Extension=29 3/4"; Drain Extension=26 5/8"; Drain NPT=1"; Drain Radius=1/2"; Energy Extension=27 13/16"; Flat Side Distance=45 1/2"; Front Skid Extension=68 3/4"; Height to Drain=1 3/4"; Height to Energy=28 11/16"; Height to Hot Outlet=38 3/8"; Height to Relief=44 3/4"; Hot Outlet Angle=0.00°; Hot Outlet Extension=23 3/4"; Hot Outlet NPT=2"; Hot Outlet Offset Horiz=0"; Hot Outlet Offset Vert=23 3/4"; Hot Outlet Radius=1"; Rear Skid Extension=22 3/4"; Recovery Rate 40F to 140F (GPH)=130; Relief Valve Extension=25 3/4"; Skid Length=46"; Skid Spacing=27"; U Tube Extension=11 1/4"; U Tube Radius=2 1/4"; Unit Height=61 1/8"; Unit Radius=22 3/4"; Weight=1200
- 2300 L 400A-QW: BW Inlet Conn X=2 15/16"; BW Inlet NPT=2"; BW Inlet Radius=1"; BW Inlet Y=12 3/8"; BW Outlet Conn X=2 15/16"; BW Outlet NPT=2"; BW Outlet Radius=1"; BW Outlet Y=23 7/16"; BW Plumbing Total Z=22 1/16"; BW Up=13 1/16"; BW Up Radius=1"; BW X=17 13/16"; BW Z=11 1/2"; Boiler Water Flow Rate at 180F=87 GPM; Cold Water Extension=6 3/8"; Cold Water Inlet Z=5 1/8"; Cold Water NPT=2 1/2"; Cold Water Radius=1 1/4"; Control Enclosure Location=20"; Control Panel Extension=29 3/4"; Drain Extension=26 5/8"; Drain NPT=1"; Drain Radius=1/2"; Energy Extension=27 13/16"; Flat Side Distance=45 1/2"; Front Skid Extension=77 3/4"; Height to Drain=1 3/4"; Height to Energy=28 11/16"; Height to Hot Outlet=68 1/8"; Height to Relief=68 11/16"; Hot Outlet Angle=90.00°; Hot Outlet Extension=23 3/4"; Hot Outlet NPT=2"; Hot Outlet Offset Horiz=23 3/4"; Hot Outlet Offset Vert=0"; Hot Outlet Radius=1"; Rear Skid Extension=22 3/4"; Recovery Rate 40F to 140F (GPH)=1020; Relief Valve Extension=25 3/4"; Skid Length=55"; Skid Spacing=27"; U Tube Extension=10 9/16"; U Tube Radius=5 3/8"; Unit Height=85 1/8"; Unit Radius=22 3/4"; Weight=1570
- 2300 L 300A-QW: BW Inlet Conn X=2 15/16"; BW Inlet NPT=2"; BW Inlet Radius=1"; BW Inlet Y=12 3/8"; BW Outlet Conn X=2 15/16"; BW Outlet NPT=2"; BW Outlet Radius=1"; BW Outlet Y=23 7/16"; BW Plumbing Total Z=22 1/16"; BW Up=13 1/16"; BW Up Radius=1"; BW X=17 13/16"; BW Z=11 1/2"; Boiler Water Flow Rate at 180F=87 GPM; Cold Water Extension=6 3/8"; Cold Water Inlet Z=5 1/8"; Cold Water NPT=2 1/2"; Cold Water Radius=1 1/4"; Control Enclosure Location=20"; Control Panel Extension=29 3/4"; Drain Extension=26 5/8"; Drain NPT=1"; Drain Radius=1/2"; Energy Extension=27 13/16"; Flat Side Distance=45 1/2"; Front Skid Extension=77 3/4"; Height to Drain=1 3/4"; Height to Energy=28 11/16"; Height to Hot Outlet=50 3/8"; Height to Relief=56 3/4"; Hot Outlet Angle=0.00°; Hot Outlet Extension=23 3/4"; Hot Outlet NPT=2"; Hot Outlet Offset Horiz=0"; Hot Outlet Offset Vert=23 3/4"; Hot Outlet Radius=1"; Rear Skid Extension=22 3/4"; Recovery Rate 40F to 140F (GPH)=1020; Relief Valve Extension=25 3/4"; Skid Length=55"; Skid Spacing=27"; U Tube Extension=10 9/16"; U Tube Radius=5 3/8"; Unit Height=73 1/8"; Unit Radius=22 3/4"; Weight=1480
- 2300 L 250A-QW: BW Inlet Conn X=2 15/16"; BW Inlet NPT=2"; BW Inlet Radius=1"; BW Inlet Y=12 3/8"; BW Outlet Conn X=2 15/16"; BW Outlet NPT=2"; BW Outlet Radius=1"; BW Outlet Y=23 7/16"; BW Plumbing Total Z=24 7/16"; BW Up=13 1/16"; BW Up Radius=1"; BW X=17 13/16"; BW Z=11 1/2"; Boiler Water Flow Rate at 180F=87 GPM; Cold Water Extension=6 3/8"; Cold Water Inlet Z=5 1/8"; Cold Water NPT=2 1/2"; Cold Water Radius=1 1/4"; Control Enclosure Location=15 1/2"; Control Panel Extension=29 3/4"; Drain Extension=26 5/8"; Drain NPT=1"; Drain Radius=1/2"; Energy Extension=27 13/16"; Flat Side Distance=45 1/2"; Front Skid Extension=77 3/4"; Height to Drain=1 3/4"; Height to Energy=28 11/16"; Height to Hot Outlet=38 3/8"; Height to Relief=44 3/4"; Hot Outlet Angle=0.00°; Hot Outlet Extension=23 3/4"; Hot Outlet NPT=2"; Hot Outlet Offset Horiz=0"; Hot Outlet Offset Vert=23 3/4"; Hot Outlet Radius=1"; Rear Skid Extension=22 3/4"; Recovery Rate 40F to 140F (GPH)=1020; Relief Valve Extension=25 3/4"; Skid Length=55"; Skid Spacing=27"; U Tube Extension=12 15/16"; U Tube Radius=5 3/8"; Unit Height=61 1/8"; Unit Radius=22 3/4"; Weight=1420
- 2200 L 400A-QWD: BW Inlet Conn X=2 15/16"; BW Inlet NPT=2"; BW Inlet Radius=1"; BW Inlet Y=12 3/8"; BW Outlet Conn X=2 15/16"; BW Outlet NPT=2"; BW Outlet Radius=1"; BW Outlet Y=23 7/16"; BW Plumbing Total Z=22 1/16"; BW Up=13 1/16"; BW Up Radius=1"; BW X=17 13/16"; BW Z=11 1/2"; Boiler Water Flow Rate at 180F=92 GPM; Cold Water Extension=6 3/8"; Cold Water Inlet Z=5 1/8"; Cold Water NPT=2 1/2"; Cold Water Radius=1 1/4"; Control Enclosure Location=20"; Control Panel Extension=29 3/4"; Drain Extension=26 5/8"; Drain NPT=1"; Drain Radius=1/2"; Energy Extension=27 13/16"; Flat Side Distance=45 1/2"; Front Skid Extension=77 3/4"; Height to Drain=1 3/4"; Height to Energy=28 11/16"; Height to Hot Outlet=68 1/8"; Height to Relief=68 11/16"; Hot Outlet Angle=90.00°; Hot Outlet Extension=23 3/4"; Hot Outlet NPT=2"; Hot Outlet Offset Horiz=23 3/4"; Hot Outlet Offset Vert=0"; Hot Outlet Radius=1"; Rear Skid Extension=22 3/4"; Recovery Rate 40F to 140F (GPH)=1090; Relief Valve Extension=25 3/4"; Skid Length=55"; Skid Spacing=27"; U Tube Extension=10 9/16"; U Tube Radius=5 3/8"; Unit Height=85 1/8"; Unit Radius=22 3/4"; Weight=1690
- 2200 L 300A-QWD: BW Inlet Conn X=2 15/16"; BW Inlet NPT=2"; BW Inlet Radius=1"; BW Inlet Y=12 3/8"; BW Outlet Conn X=2 15/16"; BW Outlet NPT=2"; BW Outlet Radius=1"; BW Outlet Y=23 7/16"; BW Plumbing Total Z=22 1/16"; BW Up=13 1/16"; BW Up Radius=1"; BW X=17 13/16"; BW Z=11 1/2"; Boiler Water Flow Rate at 180F=92 GPM; Cold Water Extension=6 3/8"; Cold Water Inlet Z=5 1/8"; Cold Water NPT=2 1/2"; Cold Water Radius=1 1/4"; Control Enclosure Location=20"; Control Panel Extension=29 3/4"; Drain Extension=26 5/8"; Drain NPT=1"; Drain Radius=1/2"; Energy Extension=27 13/16"; Flat Side Distance=45 1/2"; Front Skid Extension=77 3/4"; Height to Drain=1 3/4"; Height to Energy=28 11/16"; Height to Hot Outlet=50 3/8"; Height to Relief=56 3/4"; Hot Outlet Angle=0.00°; Hot Outlet Extension=23 3/4"; Hot Outlet NPT=2"; Hot Outlet Offset Horiz=0"; Hot Outlet Offset Vert=23 3/4"; Hot Outlet Radius=1"; Rear Skid Extension=22 3/4"; Recovery Rate 40F to 140F (GPH)=1090; Relief Valve Extension=25 3/4"; Skid Length=55"; Skid Spacing=27"; U Tube Extension=10 9/16"; U Tube Radius=5 3/8"; Unit Height=73 1/8"; Unit Radius=22 3/4"; Weight=1610
- 2200 L 250A-QWD: BW Inlet Conn X=2 15/16"; BW Inlet NPT=2"; BW Inlet Radius=1"; BW Inlet Y=12 3/8"; BW Outlet Conn X=2 15/16"; BW Outlet NPT=2"; BW Outlet Radius=1"; BW Outlet Y=23 7/16"; BW Plumbing Total Z=24 7/16"; BW Up=13 1/16"; BW Up Radius=1"; BW X=17 13/16"; BW Z=11 1/2"; Boiler Water Flow Rate at 180F=92 GPM; Cold Water Extension=6 3/8"; Cold Water Inlet Z=5 1/8"; Cold Water NPT=2 1/2"; Cold Water Radius=1 1/4"; Control Enclosure Location=15 1/2"; Control Panel Extension=29 3/4"; Drain Extension=26 5/8"; Drain NPT=1"; Drain Radius=1/2"; Energy Extension=27 13/16"; Flat Side Distance=45 1/2"; Front Skid Extension=77 3/4"; Height to Drain=1 3/4"; Height to Energy=28 11/16"; Height to Hot Outlet=38 3/8"; Height to Relief=44 3/4"; Hot Outlet Angle=0.00°; Hot Outlet Extension=23 3/4"; Hot Outlet NPT=2"; Hot Outlet Offset Horiz=0"; Hot Outlet Offset Vert=23 3/4"; Hot Outlet Radius=1"; Rear Skid Extension=22 3/4"; Recovery Rate 40F to 140F (GPH)=1090; Relief Valve Extension=25 3/4"; Skid Length=55"; Skid Spacing=27"; U Tube Extension=12 15/16"; U Tube Radius=5 3/8"; Unit Height=61 1/8"; Unit Radius=22 3/4"; Weight=1550
- 2000 L 400A-QW: BW Inlet Conn X=2 1/2"; BW Inlet NPT=2"; BW Inlet Radius=1"; BW Inlet Y=10 3/8"; BW Outlet Conn X=2 1/2"; BW Outlet NPT=2"; BW Outlet Radius=1"; BW Outlet Y=17 9/16"; BW Plumbing Total Z=20 1/8"; BW Up=10 3/8"; BW Up Radius=1"; BW X=12 13/16"; BW Z=9 5/16"; Boiler Water Flow Rate at 180F=80 GPM; Cold Water Extension=5 5/16"; Cold Water Inlet Z=5 3/8"; Cold Water NPT=2"; Cold Water Radius=1"; Control Enclosure Location=20"; Control Panel Extension=29 3/4"; Drain Extension=26 5/8"; Drain NPT=1"; Drain Radius=1/2"; Energy Extension=38 13/16"; Flat Side Distance=45 1/2"; Front Skid Extension=77 3/4"; Height to Drain=1 3/4"; Height to Energy=28 11/16"; Height to Hot Outlet=68 1/8"; Height to Relief=68 11/16"; Hot Outlet Angle=90.00°; Hot Outlet Extension=23 3/4"; Hot Outlet NPT=2"; Hot Outlet Offset Horiz=23 3/4"; Hot Outlet Offset Vert=0"; Hot Outlet Radius=1"; Rear Skid Extension=22 3/4"; Recovery Rate 40F to 140F (GPH)=950; Relief Valve Extension=25 3/4"; Skid Length=55"; Skid Spacing=27"; U Tube Extension=10 13/16"; U Tube Radius=4 5/16"; Unit Height=85 1/8"; Unit Radius=22 3/4"; Weight=1490
- 2000 L 300A-QW: BW Inlet Conn X=2 1/2"; BW Inlet NPT=2"; BW Inlet Radius=1"; BW Inlet Y=10 3/8"; BW Outlet Conn X=2 1/2"; BW Outlet NPT=2"; BW Outlet Radius=1"; BW Outlet Y=17 9/16"; BW Plumbing Total Z=20 1/8"; BW Up=10 3/8"; BW Up Radius=1"; BW X=12 13/16"; BW Z=9 5/16"; Boiler Water Flow Rate at 180F=80 GPM; Cold Water Extension=5 5/16"; Cold Water Inlet Z=5 3/8"; Cold Water NPT=2"; Cold Water Radius=1"; Control Enclosure Location=20"; Control Panel Extension=29 3/4"; Drain Extension=26 5/8"; Drain NPT=1"; Drain Radius=1/2"; Energy Extension=38 13/16"; Flat Side Distance=45 1/2"; Front Skid Extension=77 3/4"; Height to Drain=1 3/4"; Height to Energy=28 11/16"; Height to Hot Outlet=50 3/8"; Height to Relief=56 3/4"; Hot Outlet Angle=0.00°; Hot Outlet Extension=23 3/4"; Hot Outlet NPT=2"; Hot Outlet Offset Horiz=0"; Hot Outlet Offset Vert=23 3/4"; Hot Outlet Radius=1"; Rear Skid Extension=22 3/4"; Recovery Rate 40F to 140F (GPH)=950; Relief Valve Extension=25 3/4"; Skid Length=55"; Skid Spacing=27"; U Tube Extension=10 13/16"; U Tube Radius=4 5/16"; Unit Height=73 1/8"; Unit Radius=22 3/4"; Weight=1400
- 2000 L 250A-QW: BW Inlet Conn X=2 1/2"; BW Inlet NPT=2"; BW Inlet Radius=1"; BW Inlet Y=10 3/8"; BW Outlet Conn X=2 1/2"; BW Outlet NPT=2"; BW Outlet Radius=1"; BW Outlet Y=17 9/16"; BW Plumbing Total Z=22 1/16"; BW Up=10 3/8"; BW Up Radius=1"; BW X=12 13/16"; BW Z=9 5/16"; Boiler Water Flow Rate at 180F=80 GPM; Cold Water Extension=5 5/16"; Cold Water Inlet Z=5 3/8"; Cold Water NPT=2"; Cold Water Radius=1"; Control Enclosure Location=15 1/2"; Control Panel Extension=29 3/4"; Drain Extension=26 5/8"; Drain NPT=1"; Drain Radius=1/2"; Energy Extension=38 13/16"; Flat Side Distance=45 1/2"; Front Skid Extension=77 3/4"; Height to Drain=1 3/4"; Height to Energy=28 11/16"; Height to Hot Outlet=38 3/8"; Height to Relief=44 3/4"; Hot Outlet Angle=0.00°; Hot Outlet Extension=23 3/4"; Hot Outlet NPT=2"; Hot Outlet Offset Horiz=0"; Hot Outlet Offset Vert=23 3/4"; Hot Outlet Radius=1"; Rear Skid Extension=22 3/4"; Recovery Rate 40F to 140F (GPH)=850; Relief Valve Extension=25 3/4"; Skid Length=55"; Skid Spacing=27"; U Tube Extension=12 3/4"; U Tube Radius=4 5/16"; Unit Height=61 1/8"; Unit Radius=22 3/4"; Weight=1340
- 1900 L 400A-QWD: BW Inlet Conn X=2 15/16"; BW Inlet NPT=2"; BW Inlet Radius=1"; BW Inlet Y=10 3/8"; BW Outlet Conn X=2 15/16"; BW Outlet NPT=2"; BW Outlet Radius=1"; BW Outlet Y=17 9/16"; BW Plumbing Total Z=19 7/8"; BW Up=10 13/16"; BW Up Radius=1"; BW X=13 7/8"; BW Z=9 5/16"; Boiler Water Flow Rate at 180F=80 GPM; Cold Water Extension=6 3/8"; Cold Water Inlet Z=5 1/8"; Cold Water NPT=2 1/2"; Cold Water Radius=1 1/4"; Control Enclosure Location=20"; Control Panel Extension=29 3/4"; Drain Extension=26 5/8"; Drain NPT=1"; Drain Radius=1/2"; Energy Extension=27 13/16"; Flat Side Distance=45 1/2"; Front Skid Extension=77 3/4"; Height to Drain=1 3/4"; Height to Energy=28 11/16"; Height to Hot Outlet=68 1/8"; Height to Relief=68 11/16"; Hot Outlet Angle=90.00°; Hot Outlet Extension=23 3/4"; Hot Outlet NPT=2"; Hot Outlet Offset Horiz=23 3/4"; Hot Outlet Offset Vert=0"; Hot Outlet Radius=1"; Rear Skid Extension=22 3/4"; Recovery Rate 40F to 140F (GPH)=950; Relief Valve Extension=25 3/4"; Skid Length=55"; Skid Spacing=27"; U Tube Extension=10 9/16"; U Tube Radius=5 3/8"; Unit Height=85 1/8"; Unit Radius=22 3/4"; Weight=1660
- 1900 L 300A-QWD: BW Inlet Conn X=2 15/16"; BW Inlet NPT=2"; BW Inlet Radius=1"; BW Inlet Y=10 3/8"; BW Outlet Conn X=2 15/16"; BW Outlet NPT=2"; BW Outlet Radius=1"; BW Outlet Y=17 9/16"; BW Plumbing Total Z=19 7/8"; BW Up=10 13/16"; BW Up Radius=1"; BW X=13 7/8"; BW Z=9 5/16"; Boiler Water Flow Rate at 180F=80 GPM; Cold Water Extension=6 3/8"; Cold Water Inlet Z=5 1/8"; Cold Water NPT=2 1/2"; Cold Water Radius=1 1/4"; Control Enclosure Location=20"; Control Panel Extension=29 3/4"; Drain Extension=26 5/8"; Drain NPT=1"; Drain Radius=1/2"; Energy Extension=27 13/16"; Flat Side Distance=45 1/2"; Front Skid Extension=77 3/4"; Height to Drain=1 3/4"; Height to Energy=28 11/16"; Height to Hot Outlet=50 3/8"; Height to Relief=56 3/4"; Hot Outlet Angle=0.00°; Hot Outlet Extension=23 3/4"; Hot Outlet NPT=2"; Hot Outlet Offset Horiz=0"; Hot Outlet Offset Vert=23 3/4"; Hot Outlet Radius=1"; Rear Skid Extension=22 3/4"; Recovery Rate 40F to 140F (GPH)=950; Relief Valve Extension=25 3/4"; Skid Length=55"; Skid Spacing=27"; U Tube Extension=10 9/16"; U Tube Radius=5 3/8"; Unit Height=73 1/8"; Unit Radius=22 3/4"; Weight=1570
- 1900 L 250A-QWD: BW Inlet Conn X=2 15/16"; BW Inlet NPT=2"; BW Inlet Radius=1"; BW Inlet Y=10 3/8"; BW Outlet Conn X=2 15/16"; BW Outlet NPT=2"; BW Outlet Radius=1"; BW Outlet Y=17 9/16"; BW Plumbing Total Z=22 1/4"; BW Up=10 13/16"; BW Up Radius=1"; BW X=13 7/8"; BW Z=9 5/16"; Boiler Water Flow Rate at 180F=80 GPM; Cold Water Extension=6 3/8"; Cold Water Inlet Z=5 1/8"; Cold Water NPT=2 1/2"; Cold Water Radius=1 1/4"; Control Enclosure Location=15 1/2"; Control Panel Extension=29 3/4"; Drain Extension=26 5/8"; Drain NPT=1"; Drain Radius=1/2"; Energy Extension=27 13/16"; Flat Side Distance=45 1/2"; Front Skid Extension=77 3/4"; Height to Drain=1 3/4"; Height to Energy=28 11/16"; Height to Hot Outlet=38 3/8"; Height to Relief=44 3/4"; Hot Outlet Angle=0.00°; Hot Outlet Extension=23 3/4"; Hot Outlet NPT=2"; Hot Outlet Offset Horiz=0"; Hot Outlet Offset Vert=23 3/4"; Hot Outlet Radius=1"; Rear Skid Extension=22 3/4"; Recovery Rate 40F to 140F (GPH)=950; Relief Valve Extension=25 3/4"; Skid Length=55"; Skid Spacing=27"; U Tube Extension=12 15/16"; U Tube Radius=5 3/8"; Unit Height=61 1/8"; Unit Radius=22 3/4"; Weight=1510
- 1500 L 400A-QW: BW Inlet Conn X=2 1/2"; BW Inlet NPT=1 1/2"; BW Inlet Radius=3/4"; BW Inlet Y=10 3/8"; BW Outlet Conn X=2 1/2"; BW Outlet NPT=1 1/2"; BW Outlet Radius=3/4"; BW Outlet Y=17 9/16"; BW Plumbing Total Z=20 1/8"; BW Up=10 3/8"; BW Up Radius=3/4"; BW X=12 13/16"; BW Z=9 5/16"; Boiler Water Flow Rate at 180F=58 GPM; Cold Water Extension=5 5/16"; Cold Water Inlet Z=5 3/8"; Cold Water NPT=2"; Cold Water Radius=1"; Control Enclosure Location=20"; Control Panel Extension=29 3/4"; Drain Extension=26 5/8"; Drain NPT=1"; Drain Radius=1/2"; Energy Extension=27 13/16"; Flat Side Distance=45 1/2"; Front Skid Extension=68 3/4"; Height to Drain=1 3/4"; Height to Energy=28 11/16"; Height to Hot Outlet=68 1/8"; Height to Relief=68 11/16"; Hot Outlet Angle=90.00°; Hot Outlet Extension=23 3/4"; Hot Outlet NPT=2"; Hot Outlet Offset Horiz=23 3/4"; Hot Outlet Offset Vert=0"; Hot Outlet Radius=1"; Rear Skid Extension=22 3/4"; Recovery Rate 40F to 140F (GPH)=690; Relief Valve Extension=25 3/4"; Skid Length=46"; Skid Spacing=27"; U Tube Extension=10 13/16"; U Tube Radius=4 5/16"; Unit Height=85 1/8"; Unit Radius=22 3/4"; Weight=1470
- 1500 L 300A-QW: BW Inlet Conn X=2 1/2"; BW Inlet NPT=1 1/2"; BW Inlet Radius=3/4"; BW Inlet Y=10 3/8"; BW Outlet Conn X=2 1/2"; BW Outlet NPT=1 1/2"; BW Outlet Radius=3/4"; BW Outlet Y=17 9/16"; BW Plumbing Total Z=20 1/8"; BW Up=10 3/8"; BW Up Radius=3/4"; BW X=12 13/16"; BW Z=9 5/16"; Boiler Water Flow Rate at 180F=58 GPM; Cold Water Extension=5 5/16"; Cold Water Inlet Z=5 3/8"; Cold Water NPT=2"; Cold Water Radius=1"; Control Enclosure Location=20"; Control Panel Extension=29 3/4"; Drain Extension=26 5/8"; Drain NPT=1"; Drain Radius=1/2"; Energy Extension=27 13/16"; Flat Side Distance=45 1/2"; Front Skid Extension=68 3/4"; Height to Drain=1 3/4"; Height to Energy=28 11/16"; Height to Hot Outlet=50 3/8"; Height to Relief=56 3/4"; Hot Outlet Angle=0.00°; Hot Outlet Extension=23 3/4"; Hot Outlet NPT=2"; Hot Outlet Offset Horiz=0"; Hot Outlet Offset Vert=23 3/4"; Hot Outlet Radius=1"; Rear Skid Extension=22 3/4"; Recovery Rate 40F to 140F (GPH)=690; Relief Valve Extension=25 3/4"; Skid Length=46"; Skid Spacing=27"; U Tube Extension=10 13/16"; U Tube Radius=4 5/16"; Unit Height=73 1/8"; Unit Radius=22 3/4"; Weight=1380
- 1500 L 250A-QW: BW Inlet Conn X=2 1/2"; BW Inlet NPT=1 1/2"; BW Inlet Radius=3/4"; BW Inlet Y=10 3/8"; BW Outlet Conn X=2 1/2"; BW Outlet NPT=1 1/2"; BW Outlet Radius=3/4"; BW Outlet Y=17 9/16"; BW Plumbing Total Z=22 1/16"; BW Up=10 3/8"; BW Up Radius=3/4"; BW X=12 13/16"; BW Z=9 5/16"; Boiler Water Flow Rate at 180F=58 GPM; Cold Water Extension=5 5/16"; Cold Water Inlet Z=5 3/8"; Cold Water NPT=2"; Cold Water Radius=1"; Control Enclosure Location=15 1/2"; Control Panel Extension=29 3/4"; Drain Extension=26 5/8"; Drain NPT=1"; Drain Radius=1/2"; Energy Extension=27 13/16"; Flat Side Distance=45 1/2"; Front Skid Extension=68 3/4"; Height to Drain=1 3/4"; Height to Energy=28 11/16"; Height to Hot Outlet=38 3/8"; Height to Relief=44 3/4"; Hot Outlet Angle=0.00°; Hot Outlet Extension=23 3/4"; Hot Outlet NPT=2"; Hot Outlet Offset Horiz=0"; Hot Outlet Offset Vert=23 3/4"; Hot Outlet Radius=1"; Rear Skid Extension=22 3/4"; Recovery Rate 40F to 140F (GPH)=690; Relief Valve Extension=25 3/4"; Skid Length=46"; Skid Spacing=27"; U Tube Extension=12 3/4"; U Tube Radius=4 5/16"; Unit Height=61 1/8"; Unit Radius=22 3/4"; Weight=1320
- 1300 L 400A-QWD: BW Inlet Conn X=2 1/2"; BW Inlet NPT=1 1/2"; BW Inlet Radius=3/4"; BW Inlet Y=8 3/8"; BW Outlet Conn X=2 1/2"; BW Outlet NPT=1 1/2"; BW Outlet Radius=3/4"; BW Outlet Y=15 1/4"; BW Plumbing Total Z=19 1/4"; BW Up=8 5/8"; BW Up Radius=3/4"; BW X=11 11/16"; BW Z=8 7/16"; Boiler Water Flow Rate at 180F=53 GPM; Cold Water Extension=5 5/16"; Cold Water Inlet Z=5 3/8"; Cold Water NPT=2"; Cold Water Radius=1"; Control Enclosure Location=20"; Control Panel Extension=29 3/4"; Drain Extension=26 5/8"; Drain NPT=1"; Drain Radius=1/2"; Energy Extension=27 13/16"; Flat Side Distance=45 1/2"; Front Skid Extension=68 3/4"; Height to Drain=1 3/4"; Height to Energy=28 11/16"; Height to Hot Outlet=68 1/8"; Height to Relief=68 11/16"; Hot Outlet Angle=90.00°; Hot Outlet Extension=23 3/4"; Hot Outlet NPT=2"; Hot Outlet Offset Horiz=23 3/4"; Hot Outlet Offset Vert=0"; Hot Outlet Radius=1"; Rear Skid Extension=22 3/4"; Recovery Rate 40F to 140F (GPH)=620; Relief Valve Extension=25 3/4"; Skid Length=46"; Skid Spacing=27"; U Tube Extension=10 13/16"; U Tube Radius=4 5/16"; Unit Height=85 1/8"; Unit Radius=22 3/4"; Weight=1510
- 1300 L 300A-QWD: BW Inlet Conn X=2 1/2"; BW Inlet NPT=1 1/2"; BW Inlet Radius=3/4"; BW Inlet Y=8 3/8"; BW Outlet Conn X=2 1/2"; BW Outlet NPT=1 1/2"; BW Outlet Radius=3/4"; BW Outlet Y=15 1/4"; BW Plumbing Total Z=19 1/4"; BW Up=8 5/8"; BW Up Radius=3/4"; BW X=11 11/16"; BW Z=8 7/16"; Boiler Water Flow Rate at 180F=53 GPM; Cold Water Extension=5 5/16"; Cold Water Inlet Z=5 3/8"; Cold Water NPT=2"; Cold Water Radius=1"; Control Enclosure Location=20"; Control Panel Extension=29 3/4"; Drain Extension=26 5/8"; Drain NPT=1"; Drain Radius=1/2"; Energy Extension=27 13/16"; Flat Side Distance=45 1/2"; Front Skid Extension=68 3/4"; Height to Drain=1 3/4"; Height to Energy=28 11/16"; Height to Hot Outlet=50 3/8"; Height to Relief=56 3/4"; Hot Outlet Angle=0.00°; Hot Outlet Extension=23 3/4"; Hot Outlet NPT=2"; Hot Outlet Offset Horiz=0"; Hot Outlet Offset Vert=23 3/4"; Hot Outlet Radius=1"; Rear Skid Extension=22 3/4"; Recovery Rate 40F to 140F (GPH)=620; Relief Valve Extension=25 3/4"; Skid Length=46"; Skid Spacing=27"; U Tube Extension=10 13/16"; U Tube Radius=4 5/16"; Unit Height=73 1/8"; Unit Radius=22 3/4"; Weight=1430
- 1300 L 250A-QWD: BW Inlet Conn X=2 1/2"; BW Inlet NPT=1 1/2"; BW Inlet Radius=3/4"; BW Inlet Y=8 3/8"; BW Outlet Conn X=2 1/2"; BW Outlet NPT=1 1/2"; BW Outlet Radius=3/4"; BW Outlet Y=15 1/4"; BW Plumbing Total Z=21 3/16"; BW Up=8 5/8"; BW Up Radius=3/4"; BW X=11 11/16"; BW Z=8 7/16"; Boiler Water Flow Rate at 180F=53 GPM; Cold Water Extension=5 5/16"; Cold Water Inlet Z=5 3/8"; Cold Water NPT=2"; Cold Water Radius=1"; Control Enclosure Location=15 1/2"; Control Panel Extension=29 3/4"; Drain Extension=26 5/8"; Drain NPT=1"; Drain Radius=1/2"; Energy Extension=27 13/16"; Flat Side Distance=45 1/2"; Front Skid Extension=68 3/4"; Height to Drain=1 3/4"; Height to Energy=28 11/16"; Height to Hot Outlet=38 3/8"; Height to Relief=44 3/4"; Hot Outlet Angle=0.00°; Hot Outlet Extension=23 3/4"; Hot Outlet NPT=2"; Hot Outlet Offset Horiz=0"; Hot Outlet Offset Vert=23 3/4"; Hot Outlet Radius=1"; Rear Skid Extension=22 3/4"; Recovery Rate 40F to 140F (GPH)=620; Relief Valve Extension=25 3/4"; Skid Length=46"; Skid Spacing=27"; U Tube Extension=12 3/4"; U Tube Radius=4 5/16"; Unit Height=61 1/8"; Unit Radius=22 3/4"; Weight=1370
- 1100 L 400A-QW: BW Inlet Conn X=1 7/8"; BW Inlet NPT=1 1/4"; BW Inlet Radius=5/8"; BW Inlet Y=8 3/8"; BW Outlet Conn X=1 7/8"; BW Outlet NPT=1 1/4"; BW Outlet Radius=5/8"; BW Outlet Y=15 1/4"; BW Plumbing Total Z=18 1/4"; BW Up=8"; BW Up Radius=5/8"; BW X=11 1/16"; BW Z=8 7/16"; Boiler Water Flow Rate at 180F=43 GPM; Cold Water Extension=4 5/16"; Cold Water Inlet Z=5 5/8"; Cold Water NPT=2"; Cold Water Radius=1"; Control Enclosure Location=20"; Control Panel Extension=29 3/4"; Drain Extension=26 5/8"; Drain NPT=1"; Drain Radius=1/2"; Energy Extension=27 13/16"; Flat Side Distance=45 1/2"; Front Skid Extension=77 3/4"; Height to Drain=1 3/4"; Height to Energy=28 11/16"; Height to Hot Outlet=68 1/8"; Height to Relief=68 11/16"; Hot Outlet Angle=90.00°; Hot Outlet Extension=23 3/4"; Hot Outlet NPT=2"; Hot Outlet Offset Horiz=23 3/4"; Hot Outlet Offset Vert=0"; Hot Outlet Radius=1"; Rear Skid Extension=22 3/4"; Recovery Rate 40F to 140F (GPH)=510; Relief Valve Extension=25 3/4"; Skid Length=55"; Skid Spacing=27"; U Tube Extension=9 13/16"; U Tube Radius=3 5/16"; Unit Height=85 1/8"; Unit Radius=22 3/4"; Weight=1390
- 1100 L 300A-QW: BW Inlet Conn X=1 7/8"; BW Inlet NPT=1 1/4"; BW Inlet Radius=5/8"; BW Inlet Y=8 3/8"; BW Outlet Conn X=1 7/8"; BW Outlet NPT=1 1/4"; BW Outlet Radius=5/8"; BW Outlet Y=15 1/4"; BW Plumbing Total Z=18 1/4"; BW Up=8"; BW Up Radius=5/8"; BW X=11 1/16"; BW Z=8 7/16"; Boiler Water Flow Rate at 180F=43 GPM; Cold Water Extension=4 5/16"; Cold Water Inlet Z=5 5/8"; Cold Water NPT=2"; Cold Water Radius=1"; Control Enclosure Location=20"; Control Panel Extension=29 3/4"; Drain Extension=26 5/8"; Drain NPT=1"; Drain Radius=1/2"; Energy Extension=27 13/16"; Flat Side Distance=45 1/2"; Front Skid Extension=77 3/4"; Height to Drain=1 3/4"; Height to Energy=28 11/16"; Height to Hot Outlet=50 3/8"; Height to Relief=56 3/4"; Hot Outlet Angle=0.00°; Hot Outlet Extension=23 3/4"; Hot Outlet NPT=2"; Hot Outlet Offset Horiz=0"; Hot Outlet Offset Vert=23 3/4"; Hot Outlet Radius=1"; Rear Skid Extension=22 3/4"; Recovery Rate 40F to 140F (GPH)=510; Relief Valve Extension=25 3/4"; Skid Length=55"; Skid Spacing=27"; U Tube Extension=9 13/16"; U Tube Radius=3 5/16"; Unit Height=73 1/8"; Unit Radius=22 3/4"; Weight=1300
- 1100 L 250A-QW: BW Inlet Conn X=1 7/8"; BW Inlet NPT=1 1/4"; BW Inlet Radius=5/8"; BW Inlet Y=8 3/8"; BW Outlet Conn X=1 7/8"; BW Outlet NPT=1 1/4"; BW Outlet Radius=5/8"; BW Outlet Y=15 1/4"; BW Plumbing Total Z=20 9/16"; BW Up=8"; BW Up Radius=5/8"; BW X=11 1/16"; BW Z=8 7/16"; Boiler Water Flow Rate at 180F=43 GPM; Cold Water Extension=4 5/16"; Cold Water Inlet Z=5 5/8"; Cold Water NPT=2"; Cold Water Radius=1"; Control Enclosure Location=15 1/2"; Control Panel Extension=29 3/4"; Drain Extension=26 5/8"; Drain NPT=1"; Drain Radius=1/2"; Energy Extension=38 13/16"; Flat Side Distance=45 1/2"; Front Skid Extension=77 3/4"; Height to Drain=1 3/4"; Height to Energy=28 11/16"; Height to Hot Outlet=38 3/8"; Height to Relief=44 3/4"; Hot Outlet Angle=0.00°; Hot Outlet Extension=23 3/4"; Hot Outlet NPT=2"; Hot Outlet Offset Horiz=0"; Hot Outlet Offset Vert=23 3/4"; Hot Outlet Radius=1"; Rear Skid Extension=22 3/4"; Recovery Rate 40F to 140F (GPH)=510; Relief Valve Extension=25 3/4"; Skid Length=55"; Skid Spacing=27"; U Tube Extension=12 1/8"; U Tube Radius=3 5/16"; Unit Height=61 1/8"; Unit Radius=22 3/4"; Weight=1240
- 800 L 215A-QW: BW Inlet Conn X=1 7/8"; BW Inlet NPT=1 1/4"; BW Inlet Radius=5/8"; BW Inlet Y=6 3/4"; BW Outlet Conn X=1 7/8"; BW Outlet NPT=1 1/4"; BW Outlet Radius=5/8"; BW Outlet Y=14 1/16"; BW Plumbing Total Z=20 7/16"; BW Up=8 7/16"; BW Up Radius=5/8"; BW X=10 7/8"; BW Z=8 5/16"; Boiler Water Flow Rate at 180F=32 GPM; Cold Water Extension=4 5/16"; Cold Water Inlet Z=5 5/8"; Cold Water NPT=2"; Cold Water Radius=1"; Control Enclosure Location=20"; Control Panel Extension=25 1/8"; Drain Extension=22"; Drain NPT=1"; Drain Radius=1/2"; Energy Extension=34 1/8"; Flat Side Distance=34"; Front Skid Extension=72 5/8"; Height to Drain=1 3/4"; Height to Energy=26 1/2"; Height to Hot Outlet=64 1/4"; Height to Relief=64 3/4"; Hot Outlet Angle=90.00°; Hot Outlet Extension=19 1/8"; Hot Outlet NPT=2"; Hot Outlet Offset Horiz=19 1/8"; Hot Outlet Offset Vert=0"; Hot Outlet Radius=1"; Rear Skid Extension=18 1/8"; Recovery Rate 40F to 140F (GPH)=380; Relief Valve Extension=21 1/8"; Skid Length=54 1/2"; Skid Spacing=17"; U Tube Extension=12 1/8"; U Tube Radius=3 5/16"; Unit Height=76"; Unit Radius=18 1/8"; Weight=1260
- 800 L 175A-QW: BW Inlet Conn X=1 7/8"; BW Inlet NPT=1 1/4"; BW Inlet Radius=5/8"; BW Inlet Y=6 3/4"; BW Outlet Conn X=1 7/8"; BW Outlet NPT=1 1/4"; BW Outlet Radius=5/8"; BW Outlet Y=14 1/16"; BW Plumbing Total Z=20 7/16"; BW Up=8 7/16"; BW Up Radius=5/8"; BW X=10 7/8"; BW Z=8 5/16"; Boiler Water Flow Rate at 180F=32 GPM; Cold Water Extension=4 5/16"; Cold Water Inlet Z=5 5/8"; Cold Water NPT=2"; Cold Water Radius=1"; Control Enclosure Location=20"; Control Panel Extension=25 1/8"; Drain Extension=22"; Drain NPT=1"; Drain Radius=1/2"; Energy Extension=34 1/8"; Flat Side Distance=34"; Front Skid Extension=72 5/8"; Height to Drain=1 3/4"; Height to Energy=26 1/2"; Height to Hot Outlet=50 7/8"; Height to Relief=57 3/4"; Hot Outlet Angle=0.00°; Hot Outlet Extension=19 1/8"; Hot Outlet NPT=2"; Hot Outlet Offset Horiz=0"; Hot Outlet Offset Vert=19 1/8"; Hot Outlet Radius=1"; Rear Skid Extension=18 1/8"; Recovery Rate 40F to 140F (GPH)=380; Relief Valve Extension=21 1/8"; Skid Length=54 1/2"; Skid Spacing=17"; U Tube Extension=12 1/8"; U Tube Radius=3 5/16"; Unit Height=69"; Unit Radius=18 1/8"; Weight=1170
- 800 L 150A-QW: BW Inlet Conn X=1 7/8"; BW Inlet NPT=1 1/4"; BW Inlet Radius=5/8"; BW Inlet Y=6 3/4"; BW Outlet Conn X=1 7/8"; BW Outlet NPT=1 1/4"; BW Outlet Radius=5/8"; BW Outlet Y=14 1/16"; BW Plumbing Total Z=20 7/16"; BW Up=8 7/16"; BW Up Radius=5/8"; BW X=10 7/8"; BW Z=8 5/16"; Boiler Water Flow Rate at 180F=32 GPM; Cold Water Extension=4 5/16"; Cold Water Inlet Z=5 5/8"; Cold Water NPT=2"; Cold Water Radius=1"; Control Enclosure Location=15 1/2"; Control Panel Extension=25 1/8"; Drain Extension=22"; Drain NPT=1"; Drain Radius=1/2"; Energy Extension=34 1/8"; Flat Side Distance=34"; Front Skid Extension=72 5/8"; Height to Drain=1 3/4"; Height to Energy=26 1/2"; Height to Hot Outlet=45"; Height to Relief=51 3/4"; Hot Outlet Angle=0.00°; Hot Outlet Extension=19 1/8"; Hot Outlet NPT=2"; Hot Outlet Offset Horiz=0"; Hot Outlet Offset Vert=19 1/8"; Hot Outlet Radius=1"; Rear Skid Extension=18 1/8"; Recovery Rate 40F to 140F (GPH)=380; Relief Valve Extension=21 1/8"; Skid Length=54 1/2"; Skid Spacing=17"; U Tube Extension=12 1/8"; U Tube Radius=3 5/16"; Unit Height=63"; Unit Radius=18 1/8"; Weight=1100
- 700 L 215A-QWD: BW Inlet Conn X=2 1/2"; BW Inlet NPT=1 1/4"; BW Inlet Radius=5/8"; BW Inlet Y=6 3/4"; BW Outlet Conn X=2 1/2"; BW Outlet NPT=1 1/4"; BW Outlet Radius=5/8"; BW Outlet Y=14 1/16"; BW Plumbing Total Z=20 7/16"; BW Up=8 7/16"; BW Up Radius=5/8"; BW X=10 7/8"; BW Z=8 5/16"; Boiler Water Flow Rate at 180F=29 GPM; Cold Water Extension=5 5/16"; Cold Water Inlet Z=5 5/8"; Cold Water NPT=2"; Cold Water Radius=1"; Control Enclosure Location=20"; Control Panel Extension=25 1/8"; Drain Extension=22"; Drain NPT=1"; Drain Radius=1/2"; Energy Extension=34 1/8"; Flat Side Distance=34"; Front Skid Extension=72 5/8"; Height to Drain=1 3/4"; Height to Energy=26 1/2"; Height to Hot Outlet=64 1/4"; Height to Relief=64 3/4"; Hot Outlet Angle=90.00°; Hot Outlet Extension=19 1/8"; Hot Outlet NPT=2"; Hot Outlet Offset Horiz=19 1/8"; Hot Outlet Offset Vert=0"; Hot Outlet Radius=1"; Rear Skid Extension=18 1/8"; Recovery Rate 40F to 140F (GPH)=340; Relief Valve Extension=21 1/8"; Skid Length=54 1/2"; Skid Spacing=17"; U Tube Extension=12 1/8"; U Tube Radius=4 5/16"; Unit Height=76"; Unit Radius=18 1/8"; Weight=1280
- 700 L 175A-QWD: BW Inlet Conn X=2 1/2"; BW Inlet NPT=1 1/4"; BW Inlet Radius=5/8"; BW Inlet Y=6 3/4"; BW Outlet Conn X=2 1/2"; BW Outlet NPT=1 1/4"; BW Outlet Radius=5/8"; BW Outlet Y=14 1/16"; BW Plumbing Total Z=20 7/16"; BW Up=8 7/16"; BW Up Radius=5/8"; BW X=10 7/8"; BW Z=8 5/16"; Boiler Water Flow Rate at 180F=29 GPM; Cold Water Extension=5 5/16"; Cold Water Inlet Z=5 5/8"; Cold Water NPT=2"; Cold Water Radius=1"; Control Enclosure Location=20"; Control Panel Extension=25 1/8"; Drain Extension=22"; Drain NPT=1"; Drain Radius=1/2"; Energy Extension=34 1/8"; Flat Side Distance=34"; Front Skid Extension=72 5/8"; Height to Drain=1 3/4"; Height to Energy=26 1/2"; Height to Hot Outlet=50 7/8"; Height to Relief=57 3/4"; Hot Outlet Angle=0.00°; Hot Outlet Extension=19 1/8"; Hot Outlet NPT=2"; Hot Outlet Offset Horiz=0"; Hot Outlet Offset Vert=19 1/8"; Hot Outlet Radius=1"; Rear Skid Extension=18 1/8"; Recovery Rate 40F to 140F (GPH)=340; Relief Valve Extension=21 1/8"; Skid Length=54 1/2"; Skid Spacing=17"; U Tube Extension=12 1/8"; U Tube Radius=4 5/16"; Unit Height=69"; Unit Radius=18 1/8"; Weight=1190
- 700 L 150A-QWD: BW Inlet Conn X=2 1/2"; BW Inlet NPT=1 1/4"; BW Inlet Radius=5/8"; BW Inlet Y=6 3/4"; BW Outlet Conn X=2 1/2"; BW Outlet NPT=1 1/4"; BW Outlet Radius=5/8"; BW Outlet Y=14 1/16"; BW Plumbing Total Z=20 7/16"; BW Up=8 7/16"; BW Up Radius=5/8"; BW X=10 7/8"; BW Z=8 5/16"; Boiler Water Flow Rate at 180F=29 GPM; Cold Water Extension=5 5/16"; Cold Water Inlet Z=5 5/8"; Cold Water NPT=2"; Cold Water Radius=1"; Control Enclosure Location=15 1/2"; Control Panel Extension=25 1/8"; Drain Extension=22"; Drain NPT=1"; Drain Radius=1/2"; Energy Extension=34 1/8"; Flat Side Distance=34"; Front Skid Extension=72 5/8"; Height to Drain=1 3/4"; Height to Energy=26 1/2"; Height to Hot Outlet=45"; Height to Relief=51 3/4"; Hot Outlet Angle=0.00°; Hot Outlet Extension=19 1/8"; Hot Outlet NPT=2"; Hot Outlet Offset Horiz=0"; Hot Outlet Offset Vert=19 1/8"; Hot Outlet Radius=1"; Rear Skid Extension=18 1/8"; Recovery Rate 40F to 140F (GPH)=340; Relief Valve Extension=21 1/8"; Skid Length=54 1/2"; Skid Spacing=17"; U Tube Extension=12 1/8"; U Tube Radius=4 5/16"; Unit Height=63"; Unit Radius=18 1/8"; Weight=1120
- 6100 L 215A-QWD: BW Inlet Conn X=4 9/16"; BW Inlet NPT=4"; BW Inlet Radius=2"; BW Inlet Y=18 11/16"; BW Outlet Conn X=4 9/16"; BW Outlet NPT=4"; BW Outlet Radius=2"; BW Outlet Y=33 11/16"; BW Plumbing Total Z=24 3/8"; BW Up=17 9/16"; BW Up Radius=2"; BW X=24 1/16"; BW Z=7 1/2"; Boiler Water Flow Rate at 180F=249 GPM; Cold Water Extension=9"; Cold Water Inlet Z=5"; Cold Water NPT=2 1/2"; Cold Water Radius=1 1/4"; Control Enclosure Location=20"; Control Panel Extension=25 1/8"; Drain Extension=22"; Drain NPT=1"; Drain Radius=1/2"; Energy Extension=34 1/8"; Flat Side Distance=34"; Front Skid Extension=72 5/8"; Height to Drain=1 3/4"; Height to Energy=26 1/2"; Height to Hot Outlet=64 1/4"; Height to Relief=64 3/4"; Hot Outlet Angle=90.00°; Hot Outlet Extension=19 1/8"; Hot Outlet NPT=2"; Hot Outlet Offset Horiz=19 1/8"; Hot Outlet Offset Vert=0"; Hot Outlet Radius=1"; Rear Skid Extension=18 1/8"; Recovery Rate 40F to 140F (GPH)=2930; Relief Valve Extension=21 1/8"; Skid Length=54 1/2"; Skid Spacing=17"; U Tube Extension=16 7/8"; U Tube Radius=8"; Unit Height=76"; Unit Radius=18 1/8"; Weight=2170
- 6100 L 175A-QWD: BW Inlet Conn X=4 9/16"; BW Inlet NPT=4"; BW Inlet Radius=2"; BW Inlet Y=18 11/16"; BW Outlet Conn X=4 9/16"; BW Outlet NPT=4"; BW Outlet Radius=2"; BW Outlet Y=33 11/16"; BW Plumbing Total Z=24 3/8"; BW Up=17 9/16"; BW Up Radius=2"; BW X=24 1/16"; BW Z=7 1/2"; Boiler Water Flow Rate at 180F=249 GPM; Cold Water Extension=9"; Cold Water Inlet Z=5"; Cold Water NPT=2 1/2"; Cold Water Radius=1 1/4"; Control Enclosure Location=20"; Control Panel Extension=25 1/8"; Drain Extension=22"; Drain NPT=1"; Drain Radius=1/2"; Energy Extension=34 1/8"; Flat Side Distance=34"; Front Skid Extension=72 5/8"; Height to Drain=1 3/4"; Height to Energy=26 1/2"; Height to Hot Outlet=50 7/8"; Height to Relief=57 3/4"; Hot Outlet Angle=0.00°; Hot Outlet Extension=19 1/8"; Hot Outlet NPT=2"; Hot Outlet Offset Horiz=0"; Hot Outlet Offset Vert=19 1/8"; Hot Outlet Radius=1"; Rear Skid Extension=18 1/8"; Recovery Rate 40F to 140F (GPH)=2930; Relief Valve Extension=21 1/8"; Skid Length=54 1/2"; Skid Spacing=17"; U Tube Extension=16 7/8"; U Tube Radius=8"; Unit Height=69"; Unit Radius=18 1/8"; Weight=2080
- 6100 L 150A-QWD: BW Inlet Conn X=4 9/16"; BW Inlet NPT=4"; BW Inlet Radius=2"; BW Inlet Y=18 11/16"; BW Outlet Conn X=4 9/16"; BW Outlet NPT=4"; BW Outlet Radius=2"; BW Outlet Y=33 11/16"; BW Plumbing Total Z=24 3/8"; BW Up=17 9/16"; BW Up Radius=2"; BW X=24 1/16"; BW Z=7 1/2"; Boiler Water Flow Rate at 180F=249 GPM; Cold Water Extension=9"; Cold Water Inlet Z=5"; Cold Water NPT=2 1/2"; Cold Water Radius=1 1/4"; Control Enclosure Location=15 1/2"; Control Panel Extension=25 1/8"; Drain Extension=22"; Drain NPT=1"; Drain Radius=1/2"; Energy Extension=34 1/8"; Flat Side Distance=34"; Front Skid Extension=72 5/8"; Height to Drain=1 3/4"; Height to Energy=26 1/2"; Height to Hot Outlet=45"; Height to Relief=51 3/4"; Hot Outlet Angle=0.00°; Hot Outlet Extension=19 1/8"; Hot Outlet NPT=2"; Hot Outlet Offset Horiz=0"; Hot Outlet Offset Vert=19 1/8"; Hot Outlet Radius=1"; Rear Skid Extension=18 1/8"; Recovery Rate 40F to 140F (GPH)=2930; Relief Valve Extension=21 1/8"; Skid Length=54 1/2"; Skid Spacing=17"; U Tube Extension=16 7/8"; U Tube Radius=8"; Unit Height=63"; Unit Radius=18 1/8"; Weight=2010
- 4000 L 215A-QW: BW Inlet Conn X=3 13/16"; BW Inlet NPT=3"; BW Inlet Radius=1 1/2"; BW Inlet Y=18 11/16"; BW Outlet Conn X=3 13/16"; BW Outlet NPT=3"; BW Outlet Radius=1 1/2"; BW Outlet Y=33 11/16"; BW Plumbing Total Z=20 3/4"; BW Up=16 13/16"; BW Up Radius=1 1/2"; BW X=23 5/16"; BW Z=7 1/2"; Boiler Water Flow Rate at 180F=152 GPM; Cold Water Extension=7 3/8"; Cold Water Inlet Z=5"; Cold Water NPT=2 1/2"; Cold Water Radius=1 1/4"; Control Enclosure Location=20"; Control Panel Extension=25 1/8"; Drain Extension=22"; Drain NPT=1"; Drain Radius=1/2"; Energy Extension=34 1/8"; Flat Side Distance=34"; Front Skid Extension=72 5/8"; Height to Drain=1 3/4"; Height to Energy=26 1/2"; Height to Hot Outlet=64 1/4"; Height to Relief=64 3/4"; Hot Outlet Angle=90.00°; Hot Outlet Extension=19 1/8"; Hot Outlet NPT=2"; Hot Outlet Offset Horiz=19 1/8"; Hot Outlet Offset Vert=0"; Hot Outlet Radius=1"; Rear Skid Extension=18 1/8"; Recovery Rate 40F to 140F (GPH)=1790; Relief Valve Extension=21 1/8"; Skid Length=54 1/2"; Skid Spacing=17"; U Tube Extension=13 1/4"; U Tube Radius=6 3/8"; Unit Height=76"; Unit Radius=18 1/8"; Weight=1640
- 4000 L 175A-QW: BW Inlet Conn X=3 13/16"; BW Inlet NPT=3"; BW Inlet Radius=1 1/2"; BW Inlet Y=18 11/16"; BW Outlet Conn X=3 13/16"; BW Outlet NPT=3"; BW Outlet Radius=1 1/2"; BW Outlet Y=33 11/16"; BW Plumbing Total Z=20 3/4"; BW Up=16 13/16"; BW Up Radius=1 1/2"; BW X=23 5/16"; BW Z=7 1/2"; Boiler Water Flow Rate at 180F=152 GPM; Cold Water Extension=7 3/8"; Cold Water Inlet Z=5"; Cold Water NPT=2 1/2"; Cold Water Radius=1 1/4"; Control Enclosure Location=20"; Control Panel Extension=25 1/8"; Drain Extension=22"; Drain NPT=1"; Drain Radius=1/2"; Energy Extension=34 1/8"; Flat Side Distance=34"; Front Skid Extension=72 5/8"; Height to Drain=1 3/4"; Height to Energy=26 1/2"; Height to Hot Outlet=50 7/8"; Height to Relief=57 3/4"; Hot Outlet Angle=0.00°; Hot Outlet Extension=19 1/8"; Hot Outlet NPT=2"; Hot Outlet Offset Horiz=0"; Hot Outlet Offset Vert=19 1/8"; Hot Outlet Radius=1"; Rear Skid Extension=18 1/8"; Recovery Rate 40F to 140F (GPH)=1790; Relief Valve Extension=21 1/8"; Skid Length=54 1/2"; Skid Spacing=17"; U Tube Extension=13 1/4"; U Tube Radius=6 3/8"; Unit Height=69"; Unit Radius=18 1/8"; Weight=1550
- 4000 L 150A-QW: BW Inlet Conn X=3 13/16"; BW Inlet NPT=3"; BW Inlet Radius=1 1/2"; BW Inlet Y=18 11/16"; BW Outlet Conn X=3 13/16"; BW Outlet NPT=3"; BW Outlet Radius=1 1/2"; BW Outlet Y=33 11/16"; BW Plumbing Total Z=20 3/4"; BW Up=16 13/16"; BW Up Radius=1 1/2"; BW X=23 5/16"; BW Z=7 1/2"; Boiler Water Flow Rate at 180F=152 GPM; Cold Water Extension=7 3/8"; Cold Water Inlet Z=5"; Cold Water NPT=2 1/2"; Cold Water Radius=1 1/4"; Control Enclosure Location=15 1/2"; Control Panel Extension=25 1/8"; Drain Extension=22"; Drain NPT=1"; Drain Radius=1/2"; Energy Extension=34 1/8"; Flat Side Distance=34"; Front Skid Extension=72 5/8"; Height to Drain=1 3/4"; Height to Energy=26 1/2"; Height to Hot Outlet=45"; Height to Relief=51 3/4"; Hot Outlet Angle=0.00°; Hot Outlet Extension=19 1/8"; Hot Outlet NPT=2"; Hot Outlet Offset Horiz=0"; Hot Outlet Offset Vert=19 1/8"; Hot Outlet Radius=1"; Rear Skid Extension=18 1/8"; Recovery Rate 40F to 140F (GPH)=1790; Relief Valve Extension=21 1/8"; Skid Length=54 1/2"; Skid Spacing=17"; U Tube Extension=13 1/4"; U Tube Radius=6 3/8"; Unit Height=63"; Unit Radius=18 1/8"; Weight=1480
- 3400 L 215A-QWD: BW Inlet Conn X=3 11/16"; BW Inlet NPT=2 1/2"; BW Inlet Radius=1 1/4"; BW Inlet Y=18 11/16"; BW Outlet Conn X=3 11/16"; BW Outlet NPT=2 1/2"; BW Outlet Radius=1 1/4"; BW Outlet Y=33 11/16"; BW Plumbing Total Z=20 3/4"; BW Up=16 13/16"; BW Up Radius=1 1/4"; BW X=23 5/16"; BW Z=7 1/2"; Boiler Water Flow Rate at 180F=138 GPM; Cold Water Extension=7 3/8"; Cold Water Inlet Z=5"; Cold Water NPT=2 1/2"; Cold Water Radius=1 1/4"; Control Enclosure Location=20"; Control Panel Extension=25 1/8"; Drain Extension=22"; Drain NPT=1"; Drain Radius=1/2"; Energy Extension=34 1/8"; Flat Side Distance=34"; Front Skid Extension=72 5/8"; Height to Drain=1 3/4"; Height to Energy=26 1/2"; Height to Hot Outlet=64 1/4"; Height to Relief=64 3/4"; Hot Outlet Angle=90.00°; Hot Outlet Extension=19 1/8"; Hot Outlet NPT=2"; Hot Outlet Offset Horiz=19 1/8"; Hot Outlet Offset Vert=0"; Hot Outlet Radius=1"; Rear Skid Extension=18 1/8"; Recovery Rate 40F to 140F (GPH)=1620; Relief Valve Extension=21 1/8"; Skid Length=54 1/2"; Skid Spacing=17"; U Tube Extension=13 1/4"; U Tube Radius=6 3/8"; Unit Height=76"; Unit Radius=18 1/8"; Weight=1820
- 3400 L 175A-QWD: BW Inlet Conn X=3 11/16"; BW Inlet NPT=2 1/2"; BW Inlet Radius=1 1/4"; BW Inlet Y=18 11/16"; BW Outlet Conn X=3 11/16"; BW Outlet NPT=2 1/2"; BW Outlet Radius=1 1/4"; BW Outlet Y=33 11/16"; BW Plumbing Total Z=20 3/4"; BW Up=16 13/16"; BW Up Radius=1 1/4"; BW X=23 5/16"; BW Z=7 1/2"; Boiler Water Flow Rate at 180F=138 GPM; Cold Water Extension=7 3/8"; Cold Water Inlet Z=5"; Cold Water NPT=2 1/2"; Cold Water Radius=1 1/4"; Control Enclosure Location=20"; Control Panel Extension=25 1/8"; Drain Extension=22"; Drain NPT=1"; Drain Radius=1/2"; Energy Extension=34 1/8"; Flat Side Distance=34"; Front Skid Extension=72 5/8"; Height to Drain=1 3/4"; Height to Energy=26 1/2"; Height to Hot Outlet=50 7/8"; Height to Relief=57 3/4"; Hot Outlet Angle=0.00°; Hot Outlet Extension=19 1/8"; Hot Outlet NPT=2"; Hot Outlet Offset Horiz=0"; Hot Outlet Offset Vert=19 1/8"; Hot Outlet Radius=1"; Rear Skid Extension=18 1/8"; Recovery Rate 40F to 140F (GPH)=1620; Relief Valve Extension=21 1/8"; Skid Length=54 1/2"; Skid Spacing=17"; U Tube Extension=13 1/4"; U Tube Radius=6 3/8"; Unit Height=69"; Unit Radius=18 1/8"; Weight=1720
- 3400 L 150A-QWD: BW Inlet Conn X=3 11/16"; BW Inlet NPT=2 1/2"; BW Inlet Radius=1 1/4"; BW Inlet Y=18 11/16"; BW Outlet Conn X=3 11/16"; BW Outlet NPT=2 1/2"; BW Outlet Radius=1 1/4"; BW Outlet Y=33 11/16"; BW Plumbing Total Z=20 3/4"; BW Up=16 13/16"; BW Up Radius=1 1/4"; BW X=23 5/16"; BW Z=7 1/2"; Boiler Water Flow Rate at 180F=138 GPM; Cold Water Extension=7 3/8"; Cold Water Inlet Z=5"; Cold Water NPT=2 1/2"; Cold Water Radius=1 1/4"; Control Enclosure Location=15 1/2"; Control Panel Extension=25 1/8"; Drain Extension=22"; Drain NPT=1"; Drain Radius=1/2"; Energy Extension=34 1/8"; Flat Side Distance=34"; Front Skid Extension=72 5/8"; Height to Drain=1 3/4"; Height to Energy=26 1/2"; Height to Hot Outlet=45"; Height to Relief=51 3/4"; Hot Outlet Angle=0.00°; Hot Outlet Extension=19 1/8"; Hot Outlet NPT=2"; Hot Outlet Offset Horiz=0"; Hot Outlet Offset Vert=19 1/8"; Hot Outlet Radius=1"; Rear Skid Extension=18 1/8"; Recovery Rate 40F to 140F (GPH)=1620; Relief Valve Extension=21 1/8"; Skid Length=54 1/2"; Skid Spacing=17"; U Tube Extension=13 1/4"; U Tube Radius=6 3/8"; Unit Height=63"; Unit Radius=18 1/8"; Weight=1660
- 300 L 215A-QW: BW Inlet Conn X=1 5/16"; BW Inlet NPT=3/4"; BW Inlet Radius=3/8"; BW Inlet Y=5"; BW Outlet Conn X=1 5/16"; BW Outlet NPT=3/4"; BW Outlet Radius=3/8"; BW Outlet Y=9 1/16"; BW Plumbing Total Z=17 3/16"; BW Up=5 3/4"; BW Up Radius=3/8"; BW X=8 1/16"; BW Z=5 15/16"; Boiler Water Flow Rate at 180F=12 GPM; Cold Water Extension=3 1/4"; Cold Water Inlet Z=5 5/8"; Cold Water NPT=2"; Cold Water Radius=1"; Control Enclosure Location=20"; Control Panel Extension=25 1/8"; Drain Extension=22"; Drain NPT=1"; Drain Radius=1/2"; Energy Extension=23 1/8"; Flat Side Distance=34"; Front Skid Extension=55 1/8"; Height to Drain=1 3/4"; Height to Energy=26 1/2"; Height to Hot Outlet=64 1/4"; Height to Relief=64 3/4"; Hot Outlet Angle=90.00°; Hot Outlet Extension=19 1/8"; Hot Outlet NPT=2"; Hot Outlet Offset Horiz=19 1/8"; Hot Outlet Offset Vert=0"; Hot Outlet Radius=1"; Rear Skid Extension=18 1/8"; Recovery Rate 40F to 140F (GPH)=140; Relief Valve Extension=21 1/8"; Skid Length=37"; Skid Spacing=17"; U Tube Extension=11 1/4"; U Tube Radius=2 1/4"; Unit Height=76"; Unit Radius=18 1/8"; Weight=1210
- 300 L 175A-QW: BW Inlet Conn X=1 5/16"; BW Inlet NPT=3/4"; BW Inlet Radius=3/8"; BW Inlet Y=5"; BW Outlet Conn X=1 5/16"; BW Outlet NPT=3/4"; BW Outlet Radius=3/8"; BW Outlet Y=9 1/16"; BW Plumbing Total Z=17 3/16"; BW Up=5 3/4"; BW Up Radius=3/8"; BW X=8 1/16"; BW Z=5 15/16"; Boiler Water Flow Rate at 180F=12 GPM; Cold Water Extension=3 1/4"; Cold Water Inlet Z=5 5/8"; Cold Water NPT=2"; Cold Water Radius=1"; Control Enclosure Location=20"; Control Panel Extension=25 1/8"; Drain Extension=22"; Drain NPT=1"; Drain Radius=1/2"; Energy Extension=23 1/8"; Flat Side Distance=34"; Front Skid Extension=55 1/8"; Height to Drain=1 3/4"; Height to Energy=26 1/2"; Height to Hot Outlet=50 7/8"; Height to Relief=57 3/4"; Hot Outlet Angle=0.00°; Hot Outlet Extension=19 1/8"; Hot Outlet NPT=2"; Hot Outlet Offset Horiz=0"; Hot Outlet Offset Vert=19 1/8"; Hot Outlet Radius=1"; Rear Skid Extension=18 1/8"; Recovery Rate 40F to 140F (GPH)=140; Relief Valve Extension=21 1/8"; Skid Length=37"; Skid Spacing=17"; U Tube Extension=11 1/4"; U Tube Radius=2 1/4"; Unit Height=69"; Unit Radius=18 1/8"; Weight=1120
- 300 L 150A-QW: BW Inlet Conn X=1 5/16"; BW Inlet NPT=3/4"; BW Inlet Radius=3/8"; BW Inlet Y=5"; BW Outlet Conn X=1 5/16"; BW Outlet NPT=3/4"; BW Outlet Radius=3/8"; BW Outlet Y=9 1/16"; BW Plumbing Total Z=17 3/16"; BW Up=5 3/4"; BW Up Radius=3/8"; BW X=8 1/16"; BW Z=5 15/16"; Boiler Water Flow Rate at 180F=12 GPM; Cold Water Extension=3 1/4"; Cold Water Inlet Z=5 5/8"; Cold Water NPT=2"; Cold Water Radius=1"; Control Enclosure Location=15 1/2"; Control Panel Extension=25 1/8"; Drain Extension=22"; Drain NPT=1"; Drain Radius=1/2"; Energy Extension=23 1/8"; Flat Side Distance=34"; Front Skid Extension=55 1/8"; Height to Drain=1 3/4"; Height to Energy=26 1/2"; Height to Hot Outlet=45"; Height to Relief=51 3/4"; Hot Outlet Angle=0.00°; Hot Outlet Extension=19 1/8"; Hot Outlet NPT=2"; Hot Outlet Offset Horiz=0"; Hot Outlet Offset Vert=19 1/8"; Hot Outlet Radius=1"; Rear Skid Extension=18 1/8"; Recovery Rate 40F to 140F (GPH)=140; Relief Valve Extension=21 1/8"; Skid Length=37"; Skid Spacing=17"; U Tube Extension=11 1/4"; U Tube Radius=2 1/4"; Unit Height=63"; Unit Radius=18 1/8"; Weight=1050
- 2600 L 215A-QW: BW Inlet Conn X=2 15/16"; BW Inlet NPT=2 1/2"; BW Inlet Radius=1 1/4"; BW Inlet Y=12 3/8"; BW Outlet Conn X=2 15/16"; BW Outlet NPT=2 1/2"; BW Outlet Radius=1 1/4"; BW Outlet Y=23 7/16"; BW Plumbing Total Z=24 7/16"; BW Up=13 1/16"; BW Up Radius=1 1/4"; BW X=17 13/16"; BW Z=11 1/2"; Boiler Water Flow Rate at 180F=102 GPM; Cold Water Extension=6 3/8"; Cold Water Inlet Z=5 1/8"; Cold Water NPT=2 1/2"; Cold Water Radius=1 1/4"; Control Enclosure Location=20"; Control Panel Extension=25 1/8"; Drain Extension=22"; Drain NPT=1"; Drain Radius=1/2"; Energy Extension=34 1/8"; Flat Side Distance=34"; Front Skid Extension=72 5/8"; Height to Drain=1 3/4"; Height to Energy=26 1/2"; Height to Hot Outlet=64 1/4"; Height to Relief=64 3/4"; Hot Outlet Angle=90.00°; Hot Outlet Extension=19 1/8"; Hot Outlet NPT=2"; Hot Outlet Offset Horiz=19 1/8"; Hot Outlet Offset Vert=0"; Hot Outlet Radius=1"; Rear Skid Extension=18 1/8"; Recovery Rate 40F to 140F (GPH)=1200; Relief Valve Extension=21 1/8"; Skid Length=54 1/2"; Skid Spacing=17"; U Tube Extension=12 15/16"; U Tube Radius=5 3/8"; Unit Height=76"; Unit Radius=18 1/8"; Weight=1460
- 2600 L 175A-QW: BW Inlet Conn X=2 15/16"; BW Inlet NPT=2 1/2"; BW Inlet Radius=1 1/4"; BW Inlet Y=12 3/8"; BW Outlet Conn X=2 15/16"; BW Outlet NPT=2 1/2"; BW Outlet Radius=1 1/4"; BW Outlet Y=23 7/16"; BW Plumbing Total Z=24 7/16"; BW Up=13 1/16"; BW Up Radius=1 1/4"; BW X=17 13/16"; BW Z=11 1/2"; Boiler Water Flow Rate at 180F=102 GPM; Cold Water Extension=6 3/8"; Cold Water Inlet Z=5 1/8"; Cold Water NPT=2 1/2"; Cold Water Radius=1 1/4"; Control Enclosure Location=20"; Control Panel Extension=25 1/8"; Drain Extension=22"; Drain NPT=1"; Drain Radius=1/2"; Energy Extension=34 1/8"; Flat Side Distance=34"; Front Skid Extension=72 5/8"; Height to Drain=1 3/4"; Height to Energy=26 1/2"; Height to Hot Outlet=50 7/8"; Height to Relief=57 3/4"; Hot Outlet Angle=0.00°; Hot Outlet Extension=19 1/8"; Hot Outlet NPT=2"; Hot Outlet Offset Horiz=0"; Hot Outlet Offset Vert=19 1/8"; Hot Outlet Radius=1"; Rear Skid Extension=18 1/8"; Recovery Rate 40F to 140F (GPH)=1200; Relief Valve Extension=21 1/8"; Skid Length=54 1/2"; Skid Spacing=17"; U Tube Extension=12 15/16"; U Tube Radius=5 3/8"; Unit Height=69"; Unit Radius=18 1/8"; Weight=1370
- 2600 L 150A-QW: BW Inlet Conn X=2 15/16"; BW Inlet NPT=2 1/2"; BW Inlet Radius=1 1/4"; BW Inlet Y=12 3/8"; BW Outlet Conn X=2 15/16"; BW Outlet NPT=2 1/2"; BW Outlet Radius=1 1/4"; BW Outlet Y=23 7/16"; BW Plumbing Total Z=24 7/16"; BW Up=13 1/16"; BW Up Radius=1 1/4"; BW X=17 13/16"; BW Z=11 1/2"; Boiler Water Flow Rate at 180F=102 GPM; Cold Water Extension=6 3/8"; Cold Water Inlet Z=5 1/8"; Cold Water NPT=2 1/2"; Cold Water Radius=1 1/4"; Control Enclosure Location=15 1/2"; Control Panel Extension=25 1/8"; Drain Extension=22"; Drain NPT=1"; Drain Radius=1/2"; Energy Extension=34 1/8"; Flat Side Distance=34"; Front Skid Extension=72 5/8"; Height to Drain=1 3/4"; Height to Energy=26 1/2"; Height to Hot Outlet=45"; Height to Relief=51 3/4"; Hot Outlet Angle=0.00°; Hot Outlet Extension=19 1/8"; Hot Outlet NPT=2"; Hot Outlet Offset Horiz=0"; Hot Outlet Offset Vert=19 1/8"; Hot Outlet Radius=1"; Rear Skid Extension=18 1/8"; Recovery Rate 40F to 140F (GPH)=1200; Relief Valve Extension=21 1/8"; Skid Length=54 1/2"; Skid Spacing=17"; U Tube Extension=12 15/16"; U Tube Radius=5 3/8"; Unit Height=63"; Unit Radius=18 1/8"; Weight=1300
- 250 L 215A-QWD: BW Inlet Conn X=1 5/16"; BW Inlet NPT=3/4"; BW Inlet Radius=3/8"; BW Inlet Y=5"; BW Outlet Conn X=1 5/16"; BW Outlet NPT=3/4"; BW Outlet Radius=3/8"; BW Outlet Y=9 1/16"; BW Plumbing Total Z=17 3/16"; BW Up=5 3/4"; BW Up Radius=3/8"; BW X=8 1/16"; BW Z=5 15/16"; Boiler Water Flow Rate at 180F=11 GPM; Cold Water Extension=3 1/4"; Cold Water Inlet Z=5 5/8"; Cold Water NPT=2"; Cold Water Radius=1"; Control Enclosure Location=20"; Control Panel Extension=25 1/8"; Drain Extension=22"; Drain NPT=1"; Drain Radius=1/2"; Energy Extension=23 1/8"; Flat Side Distance=34"; Front Skid Extension=55 1/8"; Height to Drain=1 3/4"; Height to Energy=26 1/2"; Height to Hot Outlet=64 1/4"; Height to Relief=64 3/4"; Hot Outlet Angle=90.00°; Hot Outlet Extension=19 1/8"; Hot Outlet NPT=2"; Hot Outlet Offset Horiz=19 1/8"; Hot Outlet Offset Vert=0"; Hot Outlet Radius=1"; Rear Skid Extension=18 1/8"; Recovery Rate 40F to 140F (GPH)=130; Relief Valve Extension=21 1/8"; Skid Length=37"; Skid Spacing=17"; U Tube Extension=11 1/4"; U Tube Radius=2 1/4"; Unit Height=76"; Unit Radius=18 1/8"; Weight=1230
- 250 L 175A-QWD: BW Inlet Conn X=1 5/16"; BW Inlet NPT=3/4"; BW Inlet Radius=3/8"; BW Inlet Y=5"; BW Outlet Conn X=1 5/16"; BW Outlet NPT=3/4"; BW Outlet Radius=3/8"; BW Outlet Y=9 1/16"; BW Plumbing Total Z=17 3/16"; BW Up=5 3/4"; BW Up Radius=3/8"; BW X=8 1/16"; BW Z=5 15/16"; Boiler Water Flow Rate at 180F=11 GPM; Cold Water Extension=3 1/4"; Cold Water Inlet Z=5 5/8"; Cold Water NPT=2"; Cold Water Radius=1"; Control Enclosure Location=20"; Control Panel Extension=25 1/8"; Drain Extension=22"; Drain NPT=1"; Drain Radius=1/2"; Energy Extension=23 1/8"; Flat Side Distance=34"; Front Skid Extension=55 1/8"; Height to Drain=1 3/4"; Height to Energy=26 1/2"; Height to Hot Outlet=50 7/8"; Height to Relief=57 3/4"; Hot Outlet Angle=0.00°; Hot Outlet Extension=19 1/8"; Hot Outlet NPT=2"; Hot Outlet Offset Horiz=0"; Hot Outlet Offset Vert=19 1/8"; Hot Outlet Radius=1"; Rear Skid Extension=18 1/8"; Recovery Rate 40F to 140F (GPH)=130; Relief Valve Extension=21 1/8"; Skid Length=37"; Skid Spacing=17"; U Tube Extension=11 1/4"; U Tube Radius=2 1/4"; Unit Height=69"; Unit Radius=18 1/8"; Weight=1140
- 250 L 150A-QWD: BW Inlet Conn X=1 5/16"; BW Inlet NPT=3/4"; BW Inlet Radius=3/8"; BW Inlet Y=5"; BW Outlet Conn X=1 5/16"; BW Outlet NPT=3/4"; BW Outlet Radius=3/8"; BW Outlet Y=9 1/16"; BW Plumbing Total Z=17 3/16"; BW Up=5 3/4"; BW Up Radius=3/8"; BW X=8 1/16"; BW Z=5 15/16"; Boiler Water Flow Rate at 180F=11 GPM; Cold Water Extension=3 1/4"; Cold Water Inlet Z=5 5/8"; Cold Water NPT=2"; Cold Water Radius=1"; Control Enclosure Location=15 1/2"; Control Panel Extension=25 1/8"; Drain Extension=22"; Drain NPT=1"; Drain Radius=1/2"; Energy Extension=23 1/8"; Flat Side Distance=34"; Front Skid Extension=55 1/8"; Height to Drain=1 3/4"; Height to Energy=26 1/2"; Height to Hot Outlet=45"; Height to Relief=51 3/4"; Hot Outlet Angle=0.00°; Hot Outlet Extension=19 1/8"; Hot Outlet NPT=2"; Hot Outlet Offset Horiz=0"; Hot Outlet Offset Vert=19 1/8"; Hot Outlet Radius=1"; Rear Skid Extension=18 1/8"; Recovery Rate 40F to 140F (GPH)=130; Relief Valve Extension=21 1/8"; Skid Length=37"; Skid Spacing=17"; U Tube Extension=11 1/4"; U Tube Radius=2 1/4"; Unit Height=63"; Unit Radius=18 1/8"; Weight=1070
- 2300 L 215A-QW: BW Inlet Conn X=2 15/16"; BW Inlet NPT=2"; BW Inlet Radius=1"; BW Inlet Y=12 3/8"; BW Outlet Conn X=2 15/16"; BW Outlet NPT=2"; BW Outlet Radius=1"; BW Outlet Y=23 7/16"; BW Plumbing Total Z=24 7/16"; BW Up=13 1/16"; BW Up Radius=1"; BW X=17 13/16"; BW Z=11 1/2"; Boiler Water Flow Rate at 180F=87 GPM; Cold Water Extension=6 3/8"; Cold Water Inlet Z=5 1/8"; Cold Water NPT=2 1/2"; Cold Water Radius=1 1/4"; Control Enclosure Location=20"; Control Panel Extension=25 1/8"; Drain Extension=22"; Drain NPT=1"; Drain Radius=1/2"; Energy Extension=23 1/8"; Flat Side Distance=34"; Front Skid Extension=72 5/8"; Height to Drain=1 3/4"; Height to Energy=26 1/2"; Height to Hot Outlet=64 1/4"; Height to Relief=64 3/4"; Hot Outlet Angle=90.00°; Hot Outlet Extension=19 1/8"; Hot Outlet NPT=2"; Hot Outlet Offset Horiz=19 1/8"; Hot Outlet Offset Vert=0"; Hot Outlet Radius=1"; Rear Skid Extension=18 1/8"; Recovery Rate 40F to 140F (GPH)=1020; Relief Valve Extension=21 1/8"; Skid Length=54 1/2"; Skid Spacing=17"; U Tube Extension=12 15/16"; U Tube Radius=5 3/8"; Unit Height=76"; Unit Radius=18 1/8"; Weight=1450
- 2300 L 175A-QW: BW Inlet Conn X=2 15/16"; BW Inlet NPT=2"; BW Inlet Radius=1"; BW Inlet Y=12 3/8"; BW Outlet Conn X=2 15/16"; BW Outlet NPT=2"; BW Outlet Radius=1"; BW Outlet Y=23 7/16"; BW Plumbing Total Z=24 7/16"; BW Up=13 1/16"; BW Up Radius=1"; BW X=17 13/16"; BW Z=11 1/2"; Boiler Water Flow Rate at 180F=87 GPM; Cold Water Extension=6 3/8"; Cold Water Inlet Z=5 1/8"; Cold Water NPT=2 1/2"; Cold Water Radius=1 1/4"; Control Enclosure Location=20"; Control Panel Extension=25 1/8"; Drain Extension=22"; Drain NPT=1"; Drain Radius=1/2"; Energy Extension=23 1/8"; Flat Side Distance=34"; Front Skid Extension=72 5/8"; Height to Drain=1 3/4"; Height to Energy=26 1/2"; Height to Hot Outlet=50 7/8"; Height to Relief=57 3/4"; Hot Outlet Angle=0.00°; Hot Outlet Extension=19 1/8"; Hot Outlet NPT=2"; Hot Outlet Offset Horiz=0"; Hot Outlet Offset Vert=19 1/8"; Hot Outlet Radius=1"; Rear Skid Extension=18 1/8"; Recovery Rate 40F to 140F (GPH)=1020; Relief Valve Extension=21 1/8"; Skid Length=54 1/2"; Skid Spacing=17"; U Tube Extension=12 15/16"; U Tube Radius=5 3/8"; Unit Height=69"; Unit Radius=18 1/8"; Weight=1360
- 2300 L 150A-QW: BW Inlet Conn X=2 15/16"; BW Inlet NPT=2"; BW Inlet Radius=1"; BW Inlet Y=12 3/8"; BW Outlet Conn X=2 15/16"; BW Outlet NPT=2"; BW Outlet Radius=1"; BW Outlet Y=23 7/16"; BW Plumbing Total Z=24 7/16"; BW Up=13 1/16"; BW Up Radius=1"; BW X=17 13/16"; BW Z=11 1/2"; Boiler Water Flow Rate at 180F=87 GPM; Cold Water Extension=6 3/8"; Cold Water Inlet Z=5 1/8"; Cold Water NPT=2 1/2"; Cold Water Radius=1 1/4"; Control Enclosure Location=15 1/2"; Control Panel Extension=25 1/8"; Drain Extension=22"; Drain NPT=1"; Drain Radius=1/2"; Energy Extension=23 1/8"; Flat Side Distance=34"; Front Skid Extension=72 5/8"; Height to Drain=1 3/4"; Height to Energy=26 1/2"; Height to Hot Outlet=45"; Height to Relief=51 3/4"; Hot Outlet Angle=0.00°; Hot Outlet Extension=19 1/8"; Hot Outlet NPT=2"; Hot Outlet Offset Horiz=0"; Hot Outlet Offset Vert=19 1/8"; Hot Outlet Radius=1"; Rear Skid Extension=18 1/8"; Recovery Rate 40F to 140F (GPH)=1020; Relief Valve Extension=21 1/8"; Skid Length=54 1/2"; Skid Spacing=17"; U Tube Extension=12 15/16"; U Tube Radius=5 3/8"; Unit Height=63"; Unit Radius=18 1/8"; Weight=1292
- 2200 L 215A-QWD: BW Inlet Conn X=2 15/16"; BW Inlet NPT=2"; BW Inlet Radius=1"; BW Inlet Y=12 3/8"; BW Outlet Conn X=2 15/16"; BW Outlet NPT=2"; BW Outlet Radius=1"; BW Outlet Y=23 7/16"; BW Plumbing Total Z=24 7/16"; BW Up=13 1/16"; BW Up Radius=1"; BW X=17 13/16"; BW Z=11 1/2"; Boiler Water Flow Rate at 180F=92 GPM; Cold Water Extension=6 3/8"; Cold Water Inlet Z=5 1/8"; Cold Water NPT=2 1/2"; Cold Water Radius=1 1/4"; Control Enclosure Location=20"; Control Panel Extension=25 1/8"; Drain Extension=22"; Drain NPT=1"; Drain Radius=1/2"; Energy Extension=34 1/8"; Flat Side Distance=34"; Front Skid Extension=72 5/8"; Height to Drain=1 3/4"; Height to Energy=26 1/2"; Height to Hot Outlet=64 1/4"; Height to Relief=64 3/4"; Hot Outlet Angle=90.00°; Hot Outlet Extension=19 1/8"; Hot Outlet NPT=2"; Hot Outlet Offset Horiz=19 1/8"; Hot Outlet Offset Vert=0"; Hot Outlet Radius=1"; Rear Skid Extension=18 1/8"; Recovery Rate 40F to 140F (GPH)=1090; Relief Valve Extension=21 1/8"; Skid Length=54 1/2"; Skid Spacing=17"; U Tube Extension=12 15/16"; U Tube Radius=5 3/8"; Unit Height=76"; Unit Radius=18 1/8"; Weight=1580
- 2200 L 175A-QWD: BW Inlet Conn X=2 15/16"; BW Inlet NPT=2"; BW Inlet Radius=1"; BW Inlet Y=12 3/8"; BW Outlet Conn X=2 15/16"; BW Outlet NPT=2"; BW Outlet Radius=1"; BW Outlet Y=23 7/16"; BW Plumbing Total Z=24 7/16"; BW Up=13 1/16"; BW Up Radius=1"; BW X=17 13/16"; BW Z=11 1/2"; Boiler Water Flow Rate at 180F=92 GPM; Cold Water Extension=6 3/8"; Cold Water Inlet Z=5 1/8"; Cold Water NPT=2 1/2"; Cold Water Radius=1 1/4"; Control Enclosure Location=20"; Control Panel Extension=25 1/8"; Drain Extension=22"; Drain NPT=1"; Drain Radius=1/2"; Energy Extension=34 1/8"; Flat Side Distance=34"; Front Skid Extension=72 5/8"; Height to Drain=1 3/4"; Height to Energy=26 1/2"; Height to Hot Outlet=50 7/8"; Height to Relief=57 3/4"; Hot Outlet Angle=0.00°; Hot Outlet Extension=19 1/8"; Hot Outlet NPT=2"; Hot Outlet Offset Horiz=0"; Hot Outlet Offset Vert=19 1/8"; Hot Outlet Radius=1"; Rear Skid Extension=18 1/8"; Recovery Rate 40F to 140F (GPH)=1090; Relief Valve Extension=21 1/8"; Skid Length=54 1/2"; Skid Spacing=17"; U Tube Extension=12 15/16"; U Tube Radius=5 3/8"; Unit Height=69"; Unit Radius=18 1/8"; Weight=1490
- 2200 L 150A-QWD: BW Inlet Conn X=2 15/16"; BW Inlet NPT=2"; BW Inlet Radius=1"; BW Inlet Y=12 3/8"; BW Outlet Conn X=2 15/16"; BW Outlet NPT=2"; BW Outlet Radius=1"; BW Outlet Y=23 7/16"; BW Plumbing Total Z=24 7/16"; BW Up=13 1/16"; BW Up Radius=1"; BW X=17 13/16"; BW Z=11 1/2"; Boiler Water Flow Rate at 180F=92 GPM; Cold Water Extension=6 3/8"; Cold Water Inlet Z=5 1/8"; Cold Water NPT=2 1/2"; Cold Water Radius=1 1/4"; Control Enclosure Location=15 1/2"; Control Panel Extension=25 1/8"; Drain Extension=22"; Drain NPT=1"; Drain Radius=1/2"; Energy Extension=34 1/8"; Flat Side Distance=34"; Front Skid Extension=72 5/8"; Height to Drain=1 3/4"; Height to Energy=26 1/2"; Height to Hot Outlet=45"; Height to Relief=51 3/4"; Hot Outlet Angle=0.00°; Hot Outlet Extension=19 1/8"; Hot Outlet NPT=2"; Hot Outlet Offset Horiz=0"; Hot Outlet Offset Vert=19 1/8"; Hot Outlet Radius=1"; Rear Skid Extension=18 1/8"; Recovery Rate 40F to 140F (GPH)=1090; Relief Valve Extension=21 1/8"; Skid Length=54 1/2"; Skid Spacing=17"; U Tube Extension=12 15/16"; U Tube Radius=5 3/8"; Unit Height=63"; Unit Radius=18 1/8"; Weight=1420
- 1900 L 215A-QWD: BW Inlet Conn X=2 15/16"; BW Inlet NPT=2"; BW Inlet Radius=1"; BW Inlet Y=10 3/8"; BW Outlet Conn X=2 15/16"; BW Outlet NPT=2"; BW Outlet Radius=1"; BW Outlet Y=17 9/16"; BW Plumbing Total Z=22 1/4"; BW Up=10 13/16"; BW Up Radius=1"; BW X=13 7/8"; BW Z=9 5/16"; Boiler Water Flow Rate at 180F=80 GPM; Cold Water Extension=6 3/8"; Cold Water Inlet Z=5 1/8"; Cold Water NPT=2 1/2"; Cold Water Radius=1 1/4"; Control Enclosure Location=20"; Control Panel Extension=25 1/8"; Drain Extension=22"; Drain NPT=1"; Drain Radius=1/2"; Energy Extension=23 1/8"; Flat Side Distance=34"; Front Skid Extension=72 5/8"; Height to Drain=1 3/4"; Height to Energy=26 1/2"; Height to Hot Outlet=64 1/4"; Height to Relief=64 3/4"; Hot Outlet Angle=90.00°; Hot Outlet Extension=19 1/8"; Hot Outlet NPT=2"; Hot Outlet Offset Horiz=19 1/8"; Hot Outlet Offset Vert=0"; Hot Outlet Radius=1"; Rear Skid Extension=18 1/8"; Recovery Rate 40F to 140F (GPH)=950; Relief Valve Extension=21 1/8"; Skid Length=54 1/2"; Skid Spacing=17"; U Tube Extension=12 15/16"; U Tube Radius=5 3/8"; Unit Height=76"; Unit Radius=18 1/8"; Weight=1540
- 1900 L 175A-QWD: BW Inlet Conn X=2 15/16"; BW Inlet NPT=2"; BW Inlet Radius=1"; BW Inlet Y=10 3/8"; BW Outlet Conn X=2 15/16"; BW Outlet NPT=2"; BW Outlet Radius=1"; BW Outlet Y=17 9/16"; BW Plumbing Total Z=22 1/4"; BW Up=10 13/16"; BW Up Radius=1"; BW X=13 7/8"; BW Z=9 5/16"; Boiler Water Flow Rate at 180F=80 GPM; Cold Water Extension=6 3/8"; Cold Water Inlet Z=5 1/8"; Cold Water NPT=2 1/2"; Cold Water Radius=1 1/4"; Control Enclosure Location=20"; Control Panel Extension=25 1/8"; Drain Extension=22"; Drain NPT=1"; Drain Radius=1/2"; Energy Extension=23 1/8"; Flat Side Distance=34"; Front Skid Extension=72 5/8"; Height to Drain=1 3/4"; Height to Energy=26 1/2"; Height to Hot Outlet=50 7/8"; Height to Relief=57 3/4"; Hot Outlet Angle=0.00°; Hot Outlet Extension=19 1/8"; Hot Outlet NPT=2"; Hot Outlet Offset Horiz=0"; Hot Outlet Offset Vert=19 1/8"; Hot Outlet Radius=1"; Rear Skid Extension=18 1/8"; Recovery Rate 40F to 140F (GPH)=950; Relief Valve Extension=21 1/8"; Skid Length=54 1/2"; Skid Spacing=17"; U Tube Extension=12 15/16"; U Tube Radius=5 3/8"; Unit Height=69"; Unit Radius=18 1/8"; Weight=1450
- 1900 L 150A-QWD: BW Inlet Conn X=2 15/16"; BW Inlet NPT=2"; BW Inlet Radius=1"; BW Inlet Y=10 3/8"; BW Outlet Conn X=2 15/16"; BW Outlet NPT=2"; BW Outlet Radius=1"; BW Outlet Y=17 9/16"; BW Plumbing Total Z=22 1/4"; BW Up=10 13/16"; BW Up Radius=1"; BW X=13 7/8"; BW Z=9 5/16"; Boiler Water Flow Rate at 180F=80 GPM; Cold Water Extension=6 3/8"; Cold Water Inlet Z=5 1/8"; Cold Water NPT=2 1/2"; Cold Water Radius=1 1/4"; Control Enclosure Location=15 1/2"; Control Panel Extension=25 1/8"; Drain Extension=22"; Drain NPT=1"; Drain Radius=1/2"; Energy Extension=23 1/8"; Flat Side Distance=34"; Front Skid Extension=72 5/8"; Height to Drain=1 3/4"; Height to Energy=26 1/2"; Height to Hot Outlet=45"; Height to Relief=51 3/4"; Hot Outlet Angle=0.00°; Hot Outlet Extension=19 1/8"; Hot Outlet NPT=2"; Hot Outlet Offset Horiz=0"; Hot Outlet Offset Vert=19 1/8"; Hot Outlet Radius=1"; Rear Skid Extension=18 1/8"; Recovery Rate 40F to 140F (GPH)=950; Relief Valve Extension=21 1/8"; Skid Length=54 1/2"; Skid Spacing=17"; U Tube Extension=12 15/16"; U Tube Radius=5 3/8"; Unit Height=63"; Unit Radius=18 1/8"; Weight=1380
- 1500 L 215A-QW: BW Inlet Conn X=2 1/2"; BW Inlet NPT=1 1/2"; BW Inlet Radius=3/4"; BW Inlet Y=10 3/8"; BW Outlet Conn X=2 1/2"; BW Outlet NPT=1 1/2"; BW Outlet Radius=3/4"; BW Outlet Y=17 9/16"; BW Plumbing Total Z=22 1/16"; BW Up=10 3/8"; BW Up Radius=3/4"; BW X=12 13/16"; BW Z=9 5/16"; Boiler Water Flow Rate at 180F=58 GPM; Cold Water Extension=5 5/16"; Cold Water Inlet Z=5 3/8"; Cold Water NPT=2"; Cold Water Radius=1"; Control Enclosure Location=20"; Control Panel Extension=25 1/8"; Drain Extension=22"; Drain NPT=1"; Drain Radius=1/2"; Energy Extension=34 1/8"; Flat Side Distance=34"; Front Skid Extension=72 5/8"; Height to Drain=1 3/4"; Height to Energy=26 1/2"; Height to Hot Outlet=64 1/4"; Height to Relief=64 3/4"; Hot Outlet Angle=90.00°; Hot Outlet Extension=19 1/8"; Hot Outlet NPT=2"; Hot Outlet Offset Horiz=19 1/8"; Hot Outlet Offset Vert=0"; Hot Outlet Radius=1"; Rear Skid Extension=18 1/8"; Recovery Rate 40F to 140F (GPH)=690; Relief Valve Extension=21 1/8"; Skid Length=54 1/2"; Skid Spacing=17"; U Tube Extension=12 3/4"; U Tube Radius=4 5/16"; Unit Height=76"; Unit Radius=18 1/8"; Weight=1360
- 1500 L 175A-QW: BW Inlet Conn X=2 1/2"; BW Inlet NPT=1 1/2"; BW Inlet Radius=3/4"; BW Inlet Y=10 3/8"; BW Outlet Conn X=2 1/2"; BW Outlet NPT=1 1/2"; BW Outlet Radius=3/4"; BW Outlet Y=17 9/16"; BW Plumbing Total Z=22 1/16"; BW Up=10 3/8"; BW Up Radius=3/4"; BW X=12 13/16"; BW Z=9 5/16"; Boiler Water Flow Rate at 180F=58 GPM; Cold Water Extension=5 5/16"; Cold Water Inlet Z=5 3/8"; Cold Water NPT=2"; Cold Water Radius=1"; Control Enclosure Location=20"; Control Panel Extension=25 1/8"; Drain Extension=22"; Drain NPT=1"; Drain Radius=1/2"; Energy Extension=34 1/8"; Flat Side Distance=34"; Front Skid Extension=72 5/8"; Height to Drain=1 3/4"; Height to Energy=26 1/2"; Height to Hot Outlet=50 7/8"; Height to Relief=57 3/4"; Hot Outlet Angle=0.00°; Hot Outlet Extension=19 1/8"; Hot Outlet NPT=2"; Hot Outlet Offset Horiz=0"; Hot Outlet Offset Vert=19 1/8"; Hot Outlet Radius=1"; Rear Skid Extension=18 1/8"; Recovery Rate 40F to 140F (GPH)=690; Relief Valve Extension=21 1/8"; Skid Length=54 1/2"; Skid Spacing=17"; U Tube Extension=12 3/4"; U Tube Radius=4 5/16"; Unit Height=69"; Unit Radius=18 1/8"; Weight=1260
- 1500 L 150A-QW: BW Inlet Conn X=2 1/2"; BW Inlet NPT=1 1/2"; BW Inlet Radius=3/4"; BW Inlet Y=10 3/8"; BW Outlet Conn X=2 1/2"; BW Outlet NPT=1 1/2"; BW Outlet Radius=3/4"; BW Outlet Y=17 9/16"; BW Plumbing Total Z=22 1/16"; BW Up=10 3/8"; BW Up Radius=3/4"; BW X=12 13/16"; BW Z=9 5/16"; Boiler Water Flow Rate at 180F=58 GPM; Cold Water Extension=5 5/16"; Cold Water Inlet Z=5 3/8"; Cold Water NPT=2"; Cold Water Radius=1"; Control Enclosure Location=15 1/2"; Control Panel Extension=25 1/8"; Drain Extension=22"; Drain NPT=1"; Drain Radius=1/2"; Energy Extension=34 1/8"; Flat Side Distance=34"; Front Skid Extension=72 5/8"; Height to Drain=1 3/4"; Height to Energy=26 1/2"; Height to Hot Outlet=45"; Height to Relief=51 3/4"; Hot Outlet Angle=0.00°; Hot Outlet Extension=19 1/8"; Hot Outlet NPT=2"; Hot Outlet Offset Horiz=0"; Hot Outlet Offset Vert=19 1/8"; Hot Outlet Radius=1"; Rear Skid Extension=18 1/8"; Recovery Rate 40F to 140F (GPH)=690; Relief Valve Extension=21 1/8"; Skid Length=54 1/2"; Skid Spacing=17"; U Tube Extension=12 3/4"; U Tube Radius=4 5/16"; Unit Height=63"; Unit Radius=18 1/8"; Weight=1200
- 1300 L 215A-QWD: BW Inlet Conn X=2 1/2"; BW Inlet NPT=1 1/2"; BW Inlet Radius=3/4"; BW Inlet Y=8 3/8"; BW Outlet Conn X=2 1/2"; BW Outlet NPT=1 1/2"; BW Outlet Radius=3/4"; BW Outlet Y=15 1/4"; BW Plumbing Total Z=21 3/16"; BW Up=8 5/8"; BW Up Radius=3/4"; BW X=11 11/16"; BW Z=8 7/16"; Boiler Water Flow Rate at 180F=53 GPM; Cold Water Extension=5 5/16"; Cold Water Inlet Z=5 3/8"; Cold Water NPT=2"; Cold Water Radius=1"; Control Enclosure Location=20"; Control Panel Extension=25 1/8"; Drain Extension=22"; Drain NPT=1"; Drain Radius=1/2"; Energy Extension=34 1/8"; Flat Side Distance=34"; Front Skid Extension=72 5/8"; Height to Drain=1 3/4"; Height to Energy=26 1/2"; Height to Hot Outlet=64 1/4"; Height to Relief=64 3/4"; Hot Outlet Angle=90.00°; Hot Outlet Extension=19 1/8"; Hot Outlet NPT=2"; Hot Outlet Offset Horiz=19 1/8"; Hot Outlet Offset Vert=0"; Hot Outlet Radius=1"; Rear Skid Extension=18 1/8"; Recovery Rate 40F to 140F (GPH)=620; Relief Valve Extension=21 1/8"; Skid Length=54 1/2"; Skid Spacing=17"; U Tube Extension=12 3/4"; U Tube Radius=4 5/16"; Unit Height=76"; Unit Radius=18 1/8"; Weight=1400
- 1300 L 175A-QWD: BW Inlet Conn X=2 1/2"; BW Inlet NPT=1 1/2"; BW Inlet Radius=3/4"; BW Inlet Y=8 3/8"; BW Outlet Conn X=2 1/2"; BW Outlet NPT=1 1/2"; BW Outlet Radius=3/4"; BW Outlet Y=15 1/4"; BW Plumbing Total Z=21 3/16"; BW Up=8 5/8"; BW Up Radius=3/4"; BW X=11 11/16"; BW Z=8 7/16"; Boiler Water Flow Rate at 180F=53 GPM; Cold Water Extension=5 5/16"; Cold Water Inlet Z=5 3/8"; Cold Water NPT=2"; Cold Water Radius=1"; Control Enclosure Location=20"; Control Panel Extension=25 1/8"; Drain Extension=22"; Drain NPT=1"; Drain Radius=1/2"; Energy Extension=34 1/8"; Flat Side Distance=34"; Front Skid Extension=72 5/8"; Height to Drain=1 3/4"; Height to Energy=26 1/2"; Height to Hot Outlet=50 7/8"; Height to Relief=57 3/4"; Hot Outlet Angle=0.00°; Hot Outlet Extension=19 1/8"; Hot Outlet NPT=2"; Hot Outlet Offset Horiz=0"; Hot Outlet Offset Vert=19 1/8"; Hot Outlet Radius=1"; Rear Skid Extension=18 1/8"; Recovery Rate 40F to 140F (GPH)=620; Relief Valve Extension=21 1/8"; Skid Length=54 1/2"; Skid Spacing=17"; U Tube Extension=12 3/4"; U Tube Radius=4 5/16"; Unit Height=69"; Unit Radius=18 1/8"; Weight=1240
- 1300 L 150A-QWD: BW Inlet Conn X=2 1/2"; BW Inlet NPT=1 1/2"; BW Inlet Radius=3/4"; BW Inlet Y=8 3/8"; BW Outlet Conn X=2 1/2"; BW Outlet NPT=1 1/2"; BW Outlet Radius=3/4"; BW Outlet Y=15 1/4"; BW Plumbing Total Z=21 3/16"; BW Up=8 5/8"; BW Up Radius=3/4"; BW X=11 11/16"; BW Z=8 7/16"; Boiler Water Flow Rate at 180F=53 GPM; Cold Water Extension=5 5/16"; Cold Water Inlet Z=5 3/8"; Cold Water NPT=2"; Cold Water Radius=1"; Control Enclosure Location=15 1/2"; Control Panel Extension=25 1/8"; Drain Extension=22"; Drain NPT=1"; Drain Radius=1/2"; Energy Extension=34 1/8"; Flat Side Distance=34"; Front Skid Extension=72 5/8"; Height to Drain=1 3/4"; Height to Energy=26 1/2"; Height to Hot Outlet=45"; Height to Relief=51 3/4"; Hot Outlet Angle=0.00°; Hot Outlet Extension=19 1/8"; Hot Outlet NPT=2"; Hot Outlet Offset Horiz=0"; Hot Outlet Offset Vert=19 1/8"; Hot Outlet Radius=1"; Rear Skid Extension=18 1/8"; Recovery Rate 40F to 140F (GPH)=620; Relief Valve Extension=21 1/8"; Skid Length=54 1/2"; Skid Spacing=17"; U Tube Extension=12 3/4"; U Tube Radius=4 5/16"; Unit Height=63"; Unit Radius=18 1/8"; Weight=1240

note: column(s) folded — value = type name in every type: Model

## geometry (parser evidence)
native form markers: Sweep x1
no freeform markers — native parametric forms only
